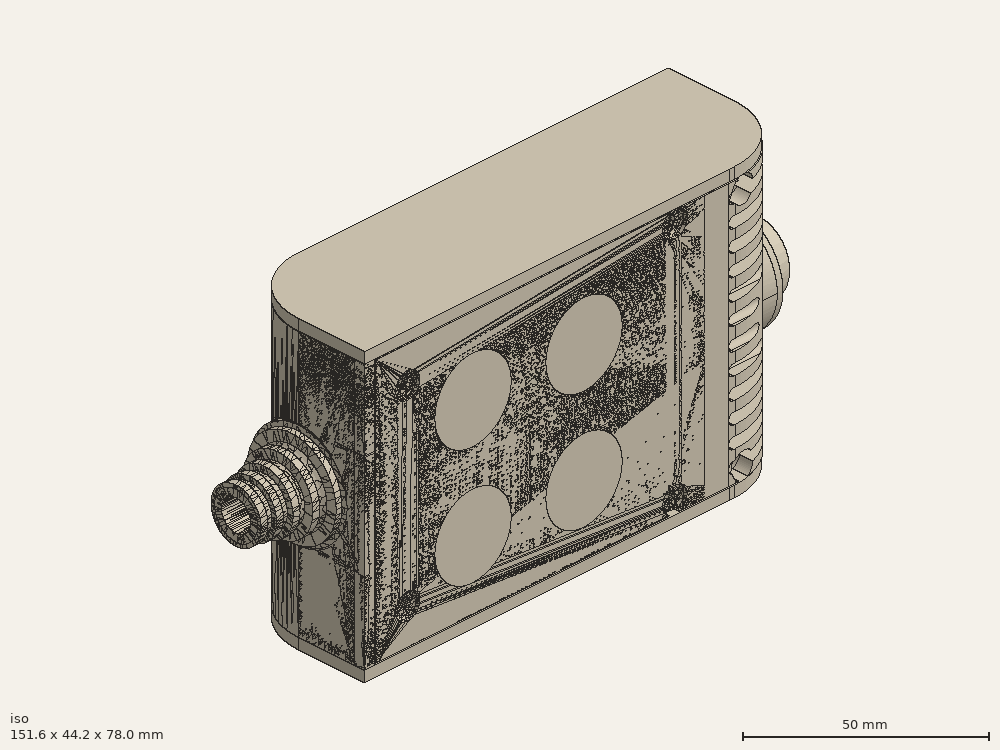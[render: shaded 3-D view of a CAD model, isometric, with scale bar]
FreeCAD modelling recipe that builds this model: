
FCSTD DOCUMENT  (FreeCAD 0.19R0.19.2)
Label: enclosure_188FCStd
License: All rights reserved
LicenseURL: http://en.wikipedia.org/wiki/All_rights_reserved
objects: Part::Revolution×152, Part::MultiFuse×146, Part::Feature×146, Sketcher::SketchObject×84, Part::Cut×70, Part::Cylinder×70, Part::Extrusion×67, Part::Fillet×58, Part::Box×36, App::MeasureDistance×4, PartDesign::Body×2, Image::ImagePlane×1
note: 831 computed .brp shape members not serialized (recipe doc carries the construction recipe); baked Part::Feature solids carry a one-line shape summary decoded from their .brp

FEATURE [Sketcher::SketchObject] Sketch  label="topSketch"
  FullyConstrained = true
  sketch-geometry (20):
    g0: LineSegment StartX=5.21097e-06 StartY=3 StartZ=0 EndX=5.21097e-06 EndY=19 EndZ=0
    g1: ArcOfCircle CenterX=19 CenterY=19 CenterZ=0 NormalX=0 NormalY=0 NormalZ=1 AngleXU=0 Radius=19 StartAngle=1.5708 EndAngle=3.14159
    g2: ArcOfCircle CenterX=19 CenterY=19 CenterZ=0 NormalX=0 NormalY=0 NormalZ=1 AngleXU=0 Radius=16 StartAngle=1.5708 EndAngle=3.14159
    g3: LineSegment StartX=114 StartY=35 StartZ=0 EndX=19 EndY=35 EndZ=0
    g4: LineSegment StartX=5.21097e-06 StartY=3 StartZ=0 EndX=5.21097e-06 EndY=0 EndZ=0
    g5: LineSegment StartX=3 StartY=0 StartZ=0 EndX=5.21097e-06 EndY=0 EndZ=0
    g6: LineSegment StartX=3 StartY=19 StartZ=0 EndX=3 EndY=0 EndZ=0
    g7: LineSegment StartX=19 StartY=38 StartZ=0 EndX=124 EndY=38 EndZ=0
    g8: Circle CenterX=119 CenterY=35 CenterZ=0 NormalX=0 NormalY=0 NormalZ=1 AngleXU=0 Radius=1
    g9: Circle CenterX=121 CenterY=35 CenterZ=0 NormalX=0 NormalY=0 NormalZ=1 AngleXU=0 Radius=1
    g10: Circle CenterX=121 CenterY=33 CenterZ=0 NormalX=0 NormalY=0 NormalZ=1 AngleXU=0 Radius=1
    g11: BSplineCurve PolesCount=3 KnotsCount=2 Degree=2 IsPeriodic=0
    g12: GeomPoint X=119 Y=35 Z=0
    g13: GeomPoint X=121 Y=33 Z=0
    g14: LineSegment StartX=119 StartY=35 StartZ=0 EndX=114 EndY=35 EndZ=0
    g15: ArcOfCircle CenterX=105 CenterY=19 CenterZ=0 NormalX=0 NormalY=0 NormalZ=1 AngleXU=0 Radius=19 StartAngle=5.7297 EndAngle=6.28319
    g16: ArcOfCircle CenterX=105 CenterY=19 CenterZ=0 NormalX=0 NormalY=0 NormalZ=1 AngleXU=0 Radius=16 StartAngle=5.60905 EndAngle=6.28319
    g17: LineSegment StartX=121 StartY=33 StartZ=0 EndX=121 EndY=19 EndZ=0
    g18: LineSegment StartX=124 StartY=38 StartZ=0 EndX=124 EndY=19 EndZ=0
    g19: LineSegment StartX=117.5 StartY=9.01251 StartZ=0 EndX=121.163 EndY=9.0125 EndZ=0
  constraints (46):
    c: Vertical(g0)
    c: Block(g0)
    c: Coincident(g1,g0)
    c: Block(g1)
    c: Coincident(g2,g1)
    c: Block(g2)
    c: Coincident(g3,g2)
    c: Horizontal(g3)
    c: Tangent(g3,g2)
    c: Coincident(g4,g0)
    c: Distance(g4) = 3
    c: Vertical(g4)
    c: Coincident(g5,g4)
    c: Horizontal(g5)
    c: Coincident(g6,g2)
    c: Coincident(g6,g5)
    c: Vertical(g6)
    c: Horizontal(g7)
    c: Distance(g7) = 105
    c: Coincident(g7,g1)
    c: Block(g3)
    c: Weight(g8) = 1
    c: Equal(g8,g9)
    c: Equal(g8,g10)
    c: InternalAlignment(g8,g11)
    c: InternalAlignment(g9,g11)
    c: InternalAlignment(g10,g11)
    c: InternalAlignment(g12,g11)
    c: InternalAlignment(g13,g11)
    c: Block(g11)
    c: Coincident(g14,g11)
    c: Coincident(g14,g3)
    c: Horizontal(g14)
    c: Block(g15)
    c: Coincident(g16,g15)
    c: Block(g16)
    c: Coincident(g17,g11)
    c: Coincident(g17,g16)
    c: Vertical(g17)
    c: Distance(g17) = 14
    c: Coincident(g18,g7)
    c: Coincident(g18,g15)
    c: Vertical(g18)
    c: Distance(g18) = 19
    c: Coincident(g19,g16)
    c: Coincident(g19,g15)
FEATURE [Sketcher::SketchObject] Sketch001  label="bottomSketch"
  FullyConstrained = true
  sketch-geometry (32):
    g0: LineSegment StartX=3.3 StartY=-6.03275e-07 StartZ=0 EndX=98 EndY=-6.03275e-07 EndZ=0
    g1: ArcOfCircle CenterX=98 CenterY=19 CenterZ=0 NormalX=0 NormalY=0 NormalZ=1 AngleXU=0 Radius=19 StartAngle=4.71239 EndAngle=5.71103
    g2: LineSegment StartX=6.3 StartY=8 StartZ=0 EndX=3.3 EndY=8 EndZ=0
    g3: LineSegment StartX=3.3 StartY=8 StartZ=0 EndX=3.3 EndY=-6.03275e-07 EndZ=0
    g4: ArcOfCircle CenterX=8.3 CenterY=5 CenterZ=0 NormalX=0 NormalY=0 NormalZ=1 AngleXU=0 Radius=2 StartAngle=3.14159 EndAngle=4.71239
    g5: LineSegment StartX=6.3 StartY=8 StartZ=0 EndX=6.3 EndY=5 EndZ=0
    g6: ArcOfCircle CenterX=98 CenterY=19 CenterZ=0 NormalX=0 NormalY=0 NormalZ=1 AngleXU=0 Radius=12.7 StartAngle=4.71239 EndAngle=6.28319
    g7: LineSegment StartX=94.7 StartY=3 StartZ=0 EndX=8.3 EndY=3 EndZ=0
    g8-g12: Circle x5 (B-spline internal-alignment scaffolding for g13; pole/knot coordinates omitted)
    g13: BSplineCurve PolesCount=5 KnotsCount=3 Degree=3 IsPeriodic=0
    g14: GeomPoint X=98 Y=6.3 Z=0
    g15: GeomPoint X=96.3938 Y=4.71946 Z=0
    g16: GeomPoint X=94.7 Y=3 Z=0
    g17-g23: Circle x7 (B-spline internal-alignment scaffolding for g24; pole/knot coordinates omitted)
    g24: BSplineCurve PolesCount=7 KnotsCount=5 Degree=3 IsPeriodic=0
    g25-g29: GeomPoint x5 (B-spline internal-alignment scaffolding for g24; pole/knot coordinates omitted)
    g30: ArcOfCircle CenterX=98 CenterY=19 CenterZ=0 NormalX=0 NormalY=0 NormalZ=1 AngleXU=0 Radius=15.7 StartAngle=5.81226 EndAngle=6.28319
    g31: LineSegment StartX=110.7 StartY=19 StartZ=0 EndX=113.7 EndY=19 EndZ=0
  constraints (41):
    c: Horizontal(g0)
    c: Coincident(g1,g0)
    c: Block(g1)
    c: Horizontal(g2)
    c: Distance(g2) = 3
    c: Coincident(g3,g2)
    c: Vertical(g3)
    c: Coincident(g3,g0)
    c: Block(g4)
    c: Block(g2)
    c: Coincident(g5,g2)
    c: Coincident(g5,g4)
    c: Vertical(g5)
    c: Coincident(g6,g1)
    c: Block(g6)
    c: Coincident(g7,g4)
    c: Horizontal(g7)
    c: Block(g0)
    c: Block(g7)
    c: Block(g3)
    c: Coincident(g13,g6)
    c: Weight(g8) = 1
    c: Equal(g8, g9-g12) x4
    c: Coincident(g13,g7)
    c: InternalAlignment(g8-g12 -> g13) x5
    c: InternalAlignment(g14,g13)
    c: InternalAlignment(g15,g13)
    c: InternalAlignment(g16,g13)
    c: Block(g13)
    c: Weight(g17) = 1
    c: Equal(g17, g18-g23) x6
    c: Coincident(g24,g1)
    c: InternalAlignment(g17-g23 -> g24) x7
    c: InternalAlignment(g25-g29 -> g24) x5
    c: Block(g24)
    c: Coincident(g30,g24)
    c: Coincident(g31,g6)
    c: Coincident(g31,g30)
    c: Horizontal(g31)
    c: Block(g31)
    c: Block(g30)
FEATURE [Part::Extrusion] Extrude  label="top"
  Base = -> Sketch
  Dir = (0,0,1)
  DirMode = 2
  FaceMakerClass = Part::FaceMakerBullseye
  LengthFwd = 72
  LengthRev = 0
  Solid = true
  Symmetric = false
FEATURE [Part::Extrusion] Extrude001  label="bottom"
  Base = -> Sketch001
  Dir = (0,0,1)
  DirMode = 2
  FaceMakerClass = Part::FaceMakerBullseye
  LengthFwd = 71.4
  LengthRev = 0
  Placement = pos=(0,0,0.3) rot=(0,0,1;0rad)
  Solid = true
  Symmetric = false
FEATURE [Sketcher::SketchObject] Sketch002  label="topSketch001"
  FullyConstrained = true
  sketch-geometry (8):
    g0: ArcOfCircle CenterX=19 CenterY=19.0975 CenterZ=0 NormalX=0 NormalY=0 NormalZ=1 AngleXU=0 Radius=18.9025 StartAngle=1.5708 EndAngle=3.14674
    g1: LineSegment StartX=0.0977805 StartY=19.0003 StartZ=0 EndX=0.0977805 EndY=0.000251602 EndZ=0
    g2: LineSegment StartX=19 StartY=38 StartZ=0 EndX=124 EndY=38 EndZ=0
    g3: LineSegment StartX=0.0977805 StartY=0.000251602 StartZ=0 EndX=105.098 EndY=0.000251602 EndZ=0
    g4: LineSegment StartX=124 StartY=38 StartZ=0 EndX=125.616 EndY=38 EndZ=0
    g5: LineSegment StartX=105.098 StartY=0.000251602 StartZ=0 EndX=106.713 EndY=0.000251602 EndZ=0
    g6: ArcOfCircle CenterX=106.616 CenterY=19 CenterZ=0 NormalX=0 NormalY=0 NormalZ=1 AngleXU=0 Radius=19 StartAngle=4.71754 EndAngle=6.28319
    g7: LineSegment StartX=125.616 StartY=38 StartZ=0 EndX=125.616 EndY=19 EndZ=0
  constraints (21):
    c: Block(g0)
    c: Coincident(g1,g0)
    c: Vertical(g1)
    c: Horizontal(g2)
    c: Distance(g2) = 105
    c: Coincident(g2,g0)
    c: Distance(g1) = 19
    c: Coincident(g3,g1)
    c: Horizontal(g3)
    c: Distance(g3) = 105
    c: Coincident(g4,g2)
    c: Horizontal(g4)
    c: Distance(g4) = 1.61553
    c: Horizontal(g5)
    c: Equal(g4,g5) = 1.61553
    c: Coincident(g5,g3)
    c: Block(g6)
    c: Coincident(g6,g5)
    c: Coincident(g7,g4)
    c: Coincident(g7,g6)
    c: Vertical(g7)
FEATURE [Part::Extrusion] Extrude002  label="sideA"
  Base = -> Sketch002
  Dir = (0,0,1)
  DirMode = 2
  FaceMakerClass = Part::FaceMakerBullseye
  LengthFwd = 3
  LengthRev = 0
  Placement = pos=(0,0,-3) rot=(0,0,1;0rad)
  Solid = true
  Symmetric = false
FEATURE [Sketcher::SketchObject] Sketch003  label="topSketch002"
  FullyConstrained = true
  sketch-geometry (6):
    g0: LineSegment StartX=19 StartY=38 StartZ=0 EndX=117 EndY=38 EndZ=0
    g1: ArcOfCircle CenterX=19 CenterY=19 CenterZ=0 NormalX=0 NormalY=0 NormalZ=1 AngleXU=0 Radius=19 StartAngle=1.5708 EndAngle=3.14159
    g2: LineSegment StartX=117 StartY=38 StartZ=0 EndX=117 EndY=19 EndZ=0
    g3: LineSegment StartX=98 StartY=1.0161e-12 StartZ=0 EndX=5.22862e-06 EndY=1.0161e-12 EndZ=0
    g4: LineSegment StartX=5.22862e-06 StartY=19 StartZ=0 EndX=5.22862e-06 EndY=1.0161e-12 EndZ=0
    g5: ArcOfCircle CenterX=98 CenterY=19 CenterZ=0 NormalX=0 NormalY=0 NormalZ=1 AngleXU=0 Radius=19 StartAngle=4.71239 EndAngle=6.28319
  constraints (16):
    c: Horizontal(g0)
    c: Distance(g0) = 98
    c: Coincident(g1,g0)
    c: Block(g1)
    c: Coincident(g2,g0)
    c: Vertical(g2)
    c: Distance(g2) = 19
    c: Horizontal(g3)
    c: Coincident(g4,g1)
    c: Vertical(g4)
    c: Coincident(g3,g4)
    c: Block(g3)
    c: Coincident(g5,g2)
    c: Coincident(g5,g3)
    c: Block(g0)
    c: Block(g5)
FEATURE [Sketcher::SketchObject] Sketch004
  FullyConstrained = true
  MapMode = 3
  Placement = pos=(0,0,0) rot=(1,0,0;1.5708rad)
  Support = -> [Extrude]
  sketch-geometry (8):
    g0: Circle CenterX=80.351 CenterY=-67.6202 CenterZ=0 NormalX=0 NormalY=0 NormalZ=1 AngleXU=0 Radius=2
    g1: Circle CenterX=80.351 CenterY=-67.6202 CenterZ=0 NormalX=0 NormalY=0 NormalZ=1 AngleXU=0 Radius=3
    g2: Circle CenterX=80.351 CenterY=-4.92017 CenterZ=0 NormalX=0 NormalY=0 NormalZ=1 AngleXU=0 Radius=2
    g3: Circle CenterX=80.351 CenterY=-4.92017 CenterZ=0 NormalX=0 NormalY=0 NormalZ=1 AngleXU=0 Radius=3
    g4: Circle CenterX=23.851 CenterY=-4.92017 CenterZ=0 NormalX=0 NormalY=0 NormalZ=1 AngleXU=0 Radius=2
    g5: Circle CenterX=23.851 CenterY=-4.92017 CenterZ=0 NormalX=0 NormalY=0 NormalZ=1 AngleXU=0 Radius=3
    g6: Circle CenterX=23.851 CenterY=-67.6202 CenterZ=0 NormalX=0 NormalY=0 NormalZ=1 AngleXU=0 Radius=2
    g7: Circle CenterX=23.851 CenterY=-67.6202 CenterZ=0 NormalX=0 NormalY=0 NormalZ=1 AngleXU=0 Radius=3
  constraints (8):
    c: Block(g3)
    c: Block(g2)
    c: Block(g1)
    c: Block(g0)
    c: Block(g6)
    c: Block(g7)
    c: Block(g4)
    c: Block(g5)
FEATURE [Part::Extrusion] Extrude004
  Base = -> Sketch004
  Dir = (0,-1,2e-16)
  DirMode = 2
  FaceMakerClass = Part::FaceMakerBullseye
  LengthFwd = 6
  LengthRev = 0
  Placement = pos=(0,9,0) rot=(0,0,1;0rad)
  Solid = true
  Symmetric = false
FEATURE [Sketcher::SketchObject] Sketch005
  FullyConstrained = true
  MapMode = 3
  Placement = pos=(0,0,0) rot=(1,0,0;1.5708rad)
  Support = -> [Extrude]
  sketch-geometry (8):
    g0: Circle CenterX=80.351 CenterY=-67.6202 CenterZ=0 NormalX=0 NormalY=0 NormalZ=1 AngleXU=0 Radius=3
    g1: Circle CenterX=80.351 CenterY=-4.92017 CenterZ=0 NormalX=0 NormalY=0 NormalZ=1 AngleXU=0 Radius=3
    g2: Circle CenterX=23.851 CenterY=-4.92017 CenterZ=0 NormalX=0 NormalY=0 NormalZ=1 AngleXU=0 Radius=3
    g3: Circle CenterX=23.851 CenterY=-67.6202 CenterZ=0 NormalX=0 NormalY=0 NormalZ=1 AngleXU=0 Radius=3
    g4: Circle CenterX=23.851 CenterY=-67.6202 CenterZ=0 NormalX=0 NormalY=0 NormalZ=1 AngleXU=0 Radius=5
    g5: Circle CenterX=80.351 CenterY=-67.6202 CenterZ=0 NormalX=0 NormalY=0 NormalZ=1 AngleXU=0 Radius=5
    g6: Circle CenterX=23.851 CenterY=-4.92017 CenterZ=0 NormalX=0 NormalY=0 NormalZ=1 AngleXU=0 Radius=5
    g7: Circle CenterX=80.351 CenterY=-4.92017 CenterZ=0 NormalX=0 NormalY=0 NormalZ=1 AngleXU=0 Radius=5
  constraints (8):
    c: Block(g1)
    c: Block(g0)
    c: Block(g3)
    c: Block(g2)
    c: Block(g5)
    c: Block(g4)
    c: Block(g6)
    c: Block(g7)
FEATURE [Part::Extrusion] Extrude005
  Base = -> Sketch005
  Dir = (0,-1,2e-16)
  DirMode = 2
  FaceMakerClass = Part::FaceMakerBullseye
  LengthFwd = 2
  LengthRev = 0
  Solid = true
  Symmetric = false
FEATURE [Sketcher::SketchObject] Sketch006
  FullyConstrained = true
  MapMode = 3
  Placement = pos=(0,0,0) rot=(1,0,0;1.5708rad)
  sketch-geometry (8):
    g0: Circle CenterX=80.351 CenterY=-67.6202 CenterZ=0 NormalX=0 NormalY=0 NormalZ=1 AngleXU=0 Radius=3
    g1: Circle CenterX=80.351 CenterY=-4.92017 CenterZ=0 NormalX=0 NormalY=0 NormalZ=1 AngleXU=0 Radius=3
    g2: Circle CenterX=23.851 CenterY=-4.92017 CenterZ=0 NormalX=0 NormalY=0 NormalZ=1 AngleXU=0 Radius=3
    g3: Circle CenterX=23.851 CenterY=-67.6202 CenterZ=0 NormalX=0 NormalY=0 NormalZ=1 AngleXU=0 Radius=3
    g4: Circle CenterX=23.851 CenterY=-67.6202 CenterZ=0 NormalX=0 NormalY=0 NormalZ=1 AngleXU=0 Radius=5
    g5: Circle CenterX=80.351 CenterY=-67.6202 CenterZ=0 NormalX=0 NormalY=0 NormalZ=1 AngleXU=0 Radius=5
    g6: Circle CenterX=23.851 CenterY=-4.92017 CenterZ=0 NormalX=0 NormalY=0 NormalZ=1 AngleXU=0 Radius=5
    g7: Circle CenterX=80.351 CenterY=-4.92017 CenterZ=0 NormalX=0 NormalY=0 NormalZ=1 AngleXU=0 Radius=5
  constraints (8):
    c: Block(g1)
    c: Block(g0)
    c: Block(g3)
    c: Block(g2)
    c: Block(g5)
    c: Block(g4)
    c: Block(g6)
    c: Block(g7)
FEATURE [Part::Extrusion] Extrude007
  Base = -> Sketch006
  Dir = (0,-1,2e-16)
  DirMode = 2
  FaceMakerClass = Part::FaceMakerBullseye
  LengthFwd = 2
  LengthRev = 0
  Solid = true
  Symmetric = false
FEATURE [Part::Fillet] Fillet
  Base = -> Extrude007
  Edges = 4 edges r=1.99: [Edge6,Edge12,Edge18,Edge24]
FEATURE [Part::Cut] Cut
  Base = -> Extrude005
  Placement = pos=(0,5,0) rot=(0,0,1;0rad)
  Tool = -> Fillet
FEATURE [Part::MultiFuse] Fusion  label="pCBScrews"
  Placement = pos=(-2.5,0,72.3) rot=(0,0,1;0rad)
  Shapes = -> [Extrude004,Cut]
FEATURE [App::MeasureDistance] Distance  label="Distance: 0.69 mm"
  Distance = 0.685967
  P1 = (24.0138,2.9647,0.3)
  P2 = (23.8901,3,-0.373787)
FEATURE [App::MeasureDistance] Distance001  label="Distance: 0.53 mm"
  Distance = 0.533607
  P1 = (80.2939,3,72.2334)
  P2 = (80.281,2.99661,71.7)
FEATURE [Part::Fillet] Fillet001
  Base = -> Extrude001
  Edges = 1 edges r=2.4: [Edge17]
FEATURE [Part::Fillet] Fillet002  label="bottom001"
  Base = -> Fillet001
  Edges = 1 edges r=2.4: [Edge36]
FEATURE [Part::Fillet] Fillet003  label="top001"
  Base = -> Extrude
  Edges = 1 edges r=2: [Edge1]
FEATURE [Sketcher::SketchObject] Sketch007
  FullyConstrained = true
  sketch-geometry (16):
    g0: LineSegment StartX=4 StartY=0 StartZ=0 EndX=4 EndY=2.4 EndZ=0
    g1: LineSegment StartX=4 StartY=2.4 StartZ=0 EndX=7 EndY=2.4 EndZ=0
    g2: LineSegment StartX=4 StartY=0 StartZ=0 EndX=5.7 EndY=0 EndZ=0
    g3: LineSegment StartX=5.7 StartY=0 StartZ=0 EndX=5.7 EndY=-5.6 EndZ=0
    g4-g8: Circle x5 (B-spline internal-alignment scaffolding for g9; pole/knot coordinates omitted)
    g9: BSplineCurve PolesCount=5 KnotsCount=3 Degree=3 IsPeriodic=0
    g10: GeomPoint X=7 Y=2.4 Z=0
    g11: GeomPoint X=10.4582 Y=-1.55472 Z=0
    g12: GeomPoint X=14 Y=-5.6 Z=0
    g13: LineSegment StartX=14 StartY=-5.6 StartZ=0 EndX=14 EndY=-14.1 EndZ=0
    g14: LineSegment StartX=14 StartY=-14.1 StartZ=0 EndX=6.5 EndY=-14.1 EndZ=0
    g15: LineSegment StartX=5.7 StartY=-5.6 StartZ=0 EndX=6.5 EndY=-14.1 EndZ=0
  constraints (28):
    c: Distance(g0) = 2.4
    c: Vertical(g0)
    c: Block(g0)
    c: Coincident(g1,g0)
    c: Horizontal(g1)
    c: Distance(g1) = 3
    c: Coincident(g2,g0)
    c: Horizontal(g2)
    c: Distance(g2) = 1.7
    c: Coincident(g3,g2)
    c: Vertical(g3)
    c: Distance(g3) = 5.6
    c: Coincident(g9,g1)
    c: Weight(g4) = 1
    c: Equal(g4, g5-g8) x4
    c: InternalAlignment(g4-g8 -> g9) x5
    c: InternalAlignment(g10,g9)
    c: InternalAlignment(g11,g9)
    c: InternalAlignment(g12,g9)
    c: Block(g9)
    c: Coincident(g13,g9)
    c: Vertical(g13)
    c: Distance(g13) = 8.5
    c: Coincident(g14,g13)
    c: Horizontal(g14)
    c: Distance(g14) = 7.5
    c: Coincident(g15,g3)
    c: Coincident(g15,g14)
FEATURE [Part::Feature] Face
  shape: bbox 10 x 16.5 x 2e-07 mm, 1 faces, 0 solids (baked)
FEATURE [Part::Revolution] Revolve  label="plugHousing"
  Angle = 360
  Axis = (0,1,0)
  Base = (0,0,0)
  FaceMakerClass = Part::FaceMakerBullseye
  Placement = pos=(0,0,36.15) rot=(0,0,1;0rad)
  Solid = false
  Source = -> Face
  Symmetric = false
FEATURE [Part::Feature] Face001
  shape: bbox 10 x 16.5 x 2e-07 mm, 1 faces, 0 solids (baked)
FEATURE [Part::Revolution] Revolve001  label="plugHousing001"
  Angle = 360
  Axis = (0,1,0)
  Base = (0,0,0)
  FaceMakerClass = Part::FaceMakerBullseye
  Placement = pos=(0,0,36.15) rot=(0,0,1;0rad)
  Solid = false
  Source = -> Face001
  Symmetric = false
FEATURE [Part::MultiFuse] Fusion001  label="plugHousing002"
  Placement = pos=(0,0,0) rot=(0,0,1;1.5708rad)
  Shapes = -> [Revolve001,Revolve]
FEATURE [Part::Feature] Face002
  shape: bbox 10 x 16.5 x 2e-07 mm, 1 faces, 0 solids (baked)
FEATURE [Part::Revolution] Revolve003  label="plugHousing005"
  Angle = 360
  Axis = (0,1,0)
  Base = (0,0,0)
  FaceMakerClass = Part::FaceMakerBullseye
  Placement = pos=(0,0,36.15) rot=(0,0,1;0rad)
  Solid = false
  Source = -> Face002
  Symmetric = false
FEATURE [Part::Feature] Face003
  shape: bbox 10 x 16.5 x 2e-07 mm, 1 faces, 0 solids (baked)
FEATURE [Part::Revolution] Revolve002  label="plugHousing003"
  Angle = 360
  Axis = (0,1,0)
  Base = (0,0,0)
  FaceMakerClass = Part::FaceMakerBullseye
  Placement = pos=(0,0,36.15) rot=(0,0,1;0rad)
  Solid = false
  Source = -> Face003
  Symmetric = false
FEATURE [Part::MultiFuse] Fusion002  label="plugHousing004"
  Placement = pos=(0,0,0) rot=(0,0,1;1.5708rad)
  Shapes = -> [Revolve002,Revolve003]
FEATURE [Part::MultiFuse] Fusion003  label="plugHousing006"
  Placement = pos=(0,19,0) rot=(0,0,1;3.14159rad)
  Shapes = -> [Fusion002,Fusion001]
FEATURE [Part::Feature] Face004
  shape: bbox 10 x 16.5 x 2e-07 mm, 1 faces, 0 solids (baked)
FEATURE [Part::Revolution] Revolve006  label="plugHousing010"
  Angle = 360
  Axis = (0,1,0)
  Base = (0,0,0)
  FaceMakerClass = Part::FaceMakerBullseye
  Placement = pos=(0,0,36.15) rot=(0,0,1;0rad)
  Solid = false
  Source = -> Face004
  Symmetric = false
FEATURE [Part::Feature] Face005
  shape: bbox 10 x 16.5 x 2e-07 mm, 1 faces, 0 solids (baked)
FEATURE [Part::Revolution] Revolve007  label="plugHousing011"
  Angle = 360
  Axis = (0,1,0)
  Base = (0,0,0)
  FaceMakerClass = Part::FaceMakerBullseye
  Placement = pos=(0,0,36.15) rot=(0,0,1;0rad)
  Solid = false
  Source = -> Face005
  Symmetric = false
FEATURE [Part::Feature] Face006
  shape: bbox 10 x 16.5 x 2e-07 mm, 1 faces, 0 solids (baked)
FEATURE [Part::Revolution] Revolve004  label="plugHousing007"
  Angle = 360
  Axis = (0,1,0)
  Base = (0,0,0)
  FaceMakerClass = Part::FaceMakerBullseye
  Placement = pos=(0,0,36.15) rot=(0,0,1;0rad)
  Solid = false
  Source = -> Face006
  Symmetric = false
FEATURE [Part::MultiFuse] Fusion004  label="plugHousing009"
  Placement = pos=(0,0,0) rot=(0,0,1;1.5708rad)
  Shapes = -> [Revolve004,Revolve007]
FEATURE [Part::Feature] Face007
  shape: bbox 10 x 16.5 x 2e-07 mm, 1 faces, 0 solids (baked)
FEATURE [Part::Revolution] Revolve005  label="plugHousing008"
  Angle = 360
  Axis = (0,1,0)
  Base = (0,0,0)
  FaceMakerClass = Part::FaceMakerBullseye
  Placement = pos=(0,0,36.15) rot=(0,0,1;0rad)
  Solid = false
  Source = -> Face007
  Symmetric = false
FEATURE [Part::MultiFuse] Fusion005  label="plugHousing012"
  Placement = pos=(0,0,0) rot=(0,0,1;1.5708rad)
  Shapes = -> [Revolve006,Revolve005]
FEATURE [Part::MultiFuse] Fusion006  label="plugHousing013"
  Placement = pos=(0,19,0) rot=(0,0,1;3.14159rad)
  Shapes = -> [Fusion005,Fusion004]
FEATURE [Part::MultiFuse] Fusion007  label="plugHousing014"
  Placement = pos=(122.621,0,-0.15) rot=(0,0,1;0rad)
  Shapes = -> [Fusion003,Fusion006]
FEATURE [Part::Cylinder] Cylinder002
  Angle = 360
  AttacherType = Attacher::AttachEngine3D
  Height = 20
  Placement = pos=(0,0,36.15) rot=(0,0,1;0rad)
  Radius = 4
FEATURE [Part::Cylinder] Cylinder003
  Angle = 360
  AttacherType = Attacher::AttachEngine3D
  Height = 10
  Placement = pos=(0,0,36.15) rot=(0,0,1;0rad)
  Radius = 4
FEATURE [Part::MultiFuse] Fusion009  label="removeToCreateHoleForPlugHousing"
  Placement = pos=(70,19,36.15) rot=(0,1,0;1.5708rad)
  Shapes = -> [Cylinder002,Cylinder003]
FEATURE [Part::Cylinder] Cylinder004
  Angle = 360
  AttacherType = Attacher::AttachEngine3D
  Height = 20
  Placement = pos=(0,0,36.15) rot=(0,0,1;0rad)
  Radius = 4
FEATURE [Part::Cylinder] Cylinder005
  Angle = 360
  AttacherType = Attacher::AttachEngine3D
  Height = 10
  Placement = pos=(0,0,36.15) rot=(0,0,1;0rad)
  Radius = 4
FEATURE [Part::MultiFuse] Fusion010  label="removeToCreateHoleForPlugHousing001"
  Placement = pos=(70,19,36.15) rot=(0,1,0;1.5708rad)
  Shapes = -> [Cylinder004,Cylinder005]
FEATURE [Part::Cut] Cut001
  Base = -> Fillet003
  Tool = -> Fusion010
FEATURE [Part::Cut] Cut002  label="Bottom"
  Base = -> Fillet002
  Tool = -> Fusion009
FEATURE [Part::Feature] Face008
  shape: bbox 10 x 16.5 x 2e-07 mm, 1 faces, 0 solids (baked)
FEATURE [Part::Revolution] Revolve011  label="plugHousing021"
  Angle = 360
  Axis = (0,1,0)
  Base = (0,0,0)
  FaceMakerClass = Part::FaceMakerBullseye
  Placement = pos=(0,0,36.15) rot=(0,0,1;0rad)
  Solid = false
  Source = -> Face008
  Symmetric = false
FEATURE [Part::Feature] Face009
  shape: bbox 10 x 16.5 x 2e-07 mm, 1 faces, 0 solids (baked)
FEATURE [Part::Revolution] Revolve012  label="plugHousing022"
  Angle = 360
  Axis = (0,1,0)
  Base = (0,0,0)
  FaceMakerClass = Part::FaceMakerBullseye
  Placement = pos=(0,0,36.15) rot=(0,0,1;0rad)
  Solid = false
  Source = -> Face009
  Symmetric = false
FEATURE [Part::Feature] Face010 .. Face013  x4 (patterned run collapsed; names and placements below)
  shape: bbox 10 x 16.5 x 2e-07 mm, 1 faces, 0 solids (baked)
FEATURE [Part::Revolution] Revolve015  label="plugHousing027"
  Angle = 360
  Axis = (0,1,0)
  Base = (0,0,0)
  FaceMakerClass = Part::FaceMakerBullseye
  Placement = pos=(0,0,36.15) rot=(0,0,1;0rad)
  Solid = false
  Source = -> Face013
  Symmetric = false
FEATURE [Part::Feature] Face014
  shape: bbox 10 x 16.5 x 2e-07 mm, 1 faces, 0 solids (baked)
FEATURE [Part::Feature] Face015
  shape: bbox 10 x 16.5 x 2e-07 mm, 1 faces, 0 solids (baked)
FEATURE [Part::Feature] Face016
  shape: bbox 10 x 16.5 x 2e-07 mm, 1 faces, 0 solids (baked)
FEATURE [Part::Revolution] Revolve019  label="plugHousing033"
  Angle = 360
  Axis = (0,1,0)
  Base = (0,0,0)
  FaceMakerClass = Part::FaceMakerBullseye
  Placement = pos=(0,0,36.15) rot=(0,0,1;0rad)
  Solid = false
  Source = -> Face016
  Symmetric = false
FEATURE [Part::Feature] Face017
  shape: bbox 10 x 16.5 x 2e-07 mm, 1 faces, 0 solids (baked)
FEATURE [Part::Revolution] Revolve020  label="plugHousing034"
  Angle = 360
  Axis = (0,1,0)
  Base = (0,0,0)
  FaceMakerClass = Part::FaceMakerBullseye
  Placement = pos=(0,0,36.15) rot=(0,0,1;0rad)
  Solid = false
  Source = -> Face017
  Symmetric = false
FEATURE [Part::Feature] Face018
  shape: bbox 10 x 16.5 x 2e-07 mm, 1 faces, 0 solids (baked)
FEATURE [Part::Revolution] Revolve016  label="plugHousing030"
  Angle = 360
  Axis = (0,1,0)
  Base = (0,0,0)
  FaceMakerClass = Part::FaceMakerBullseye
  Placement = pos=(0,0,36.15) rot=(0,0,1;0rad)
  Solid = false
  Source = -> Face018
  Symmetric = false
FEATURE [Part::MultiFuse] Fusion020  label="plugHousing038"
  Placement = pos=(0,0,0) rot=(0,0,1;1.5708rad)
  Shapes = -> [Revolve016,Revolve020]
FEATURE [Part::Feature] Face019
  shape: bbox 10 x 16.5 x 2e-07 mm, 1 faces, 0 solids (baked)
FEATURE [Part::Feature] Face020
  shape: bbox 10 x 16.5 x 2e-07 mm, 1 faces, 0 solids (baked)
FEATURE [Part::Revolution] Revolve017  label="plugHousing031"
  Angle = 360
  Axis = (0,1,0)
  Base = (0,0,0)
  FaceMakerClass = Part::FaceMakerBullseye
  Placement = pos=(0,0,36.15) rot=(0,0,1;0rad)
  Solid = false
  Source = -> Face020
  Symmetric = false
FEATURE [Part::MultiFuse] Fusion021  label="plugHousing039"
  Placement = pos=(0,0,0) rot=(0,0,1;1.5708rad)
  Shapes = -> [Revolve019,Revolve017]
FEATURE [Part::MultiFuse] Fusion023  label="plugHousing041"
  Placement = pos=(0,19,0) rot=(0,0,1;3.14159rad)
  Shapes = -> [Fusion021,Fusion020]
FEATURE [Part::Revolution] Revolve022  label="plugHousing043"
  Angle = 360
  Axis = (0,1,0)
  Base = (0,0,0)
  FaceMakerClass = Part::FaceMakerBullseye
  Placement = pos=(0,0,36.15) rot=(0,0,1;0rad)
  Solid = false
  Source = -> Face019
  Symmetric = false
FEATURE [Part::Feature] Face021
  shape: bbox 10 x 16.5 x 2e-07 mm, 1 faces, 0 solids (baked)
FEATURE [Part::Revolution] Revolve023  label="plugHousing044"
  Angle = 360
  Axis = (0,1,0)
  Base = (0,0,0)
  FaceMakerClass = Part::FaceMakerBullseye
  Placement = pos=(0,0,36.15) rot=(0,0,1;0rad)
  Solid = false
  Source = -> Face021
  Symmetric = false
FEATURE [Part::Feature] Face022
  shape: bbox 10 x 16.5 x 2e-07 mm, 1 faces, 0 solids (baked)
FEATURE [Part::Revolution] Revolve018  label="plugHousing032"
  Angle = 360
  Axis = (0,1,0)
  Base = (0,0,0)
  FaceMakerClass = Part::FaceMakerBullseye
  Placement = pos=(0,0,36.15) rot=(0,0,1;0rad)
  Solid = false
  Source = -> Face022
  Symmetric = false
FEATURE [Part::MultiFuse] Fusion022  label="plugHousing040"
  Placement = pos=(0,0,0) rot=(0,0,1;1.5708rad)
  Shapes = -> [Revolve018,Revolve023]
FEATURE [Part::Feature] Face023
  shape: bbox 10 x 16.5 x 2e-07 mm, 1 faces, 0 solids (baked)
FEATURE [Part::Revolution] Revolve021  label="plugHousing035"
  Angle = 360
  Axis = (0,1,0)
  Base = (0,0,0)
  FaceMakerClass = Part::FaceMakerBullseye
  Placement = pos=(0,0,36.15) rot=(0,0,1;0rad)
  Solid = false
  Source = -> Face023
  Symmetric = false
FEATURE [Part::MultiFuse] Fusion018  label="plugHousing036"
  Placement = pos=(0,0,0) rot=(0,0,1;1.5708rad)
  Shapes = -> [Revolve022,Revolve021]
FEATURE [Part::MultiFuse] Fusion019  label="plugHousing037"
  Placement = pos=(0,19,0) rot=(0,0,1;3.14159rad)
  Shapes = -> [Fusion018,Fusion022]
FEATURE [Part::MultiFuse] Fusion024  label="plugHousing042"
  Placement = pos=(122.621,0,-0.15) rot=(0,0,1;0rad)
  Shapes = -> [Fusion023,Fusion019]
FEATURE [Part::Cylinder] Cylinder006
  Angle = 360
  AttacherType = Attacher::AttachEngine3D
  Height = 20
  Placement = pos=(0,0,36.15) rot=(0,0,1;0rad)
  Radius = 14.3
FEATURE [Part::Cylinder] Cylinder007
  Angle = 360
  AttacherType = Attacher::AttachEngine3D
  Height = 10
  Placement = pos=(0,0,36.15) rot=(0,0,1;0rad)
  Radius = 4
FEATURE [Part::MultiFuse] Fusion026  label="removeToCreteHoleForPlugHousing"
  Placement = pos=(70,19,36) rot=(0,1,0;1.5708rad)
  Shapes = -> [Cylinder006,Cylinder007]
FEATURE [Part::Box] Box001  label="Cube001"
  AttacherType = Attacher::AttachEngine3D
  Height = 28
  Length = 3
  Placement = pos=(110.7,19,22) rot=(0,0,1;0rad)
  Width = 15.7
FEATURE [Part::Cut] Cut003  label="top002"
  Base = -> Cut001
  Tool = -> Fusion007
FEATURE [Part::Revolution] Revolve008  label="plugHousing015"
  Angle = 360
  Axis = (0,1,0)
  Base = (0,0,0)
  FaceMakerClass = Part::FaceMakerBullseye
  Placement = pos=(0,0,36.15) rot=(0,0,1;0rad)
  Solid = false
  Source = -> Face010
  Symmetric = false
FEATURE [Part::MultiFuse] Fusion013  label="plugHousing020"
  Placement = pos=(0,0,0) rot=(0,0,1;1.5708rad)
  Shapes = -> [Revolve008,Revolve012]
FEATURE [Part::Cut] Cut004  label="top003"
  Base = -> Cut003
  Placement = pos=(1,0,0) rot=(0,0,1;0rad)
  Tool = -> Fusion026
FEATURE [Part::Cylinder] Cylinder008
  Angle = 360
  AttacherType = Attacher::AttachEngine3D
  Height = 20
  Placement = pos=(0,0,36.15) rot=(0,0,1;0rad)
  Radius = 10.3
FEATURE [Part::Cylinder] Cylinder009
  Angle = 360
  AttacherType = Attacher::AttachEngine3D
  Height = 10
  Placement = pos=(0,0,36.15) rot=(0,0,1;0rad)
  Radius = 4
FEATURE [Part::MultiFuse] Fusion027  label="removeToCreteHoleForPlugHousing001"
  Placement = pos=(70,19,36) rot=(0,1,0;1.5708rad)
  Shapes = -> [Cylinder008,Cylinder009]
FEATURE [Part::Cut] Cut005  label="plugHousingTab"
  Base = -> Box001
  Tool = -> Fusion027
FEATURE [Part::MultiFuse] Fusion028  label="plugHousing045"
  Shapes = -> [Fusion024,Cut005]
FEATURE [Part::Box] Box002  label="Cube002"
  AttacherType = Attacher::AttachEngine3D
  Height = 28.8
  Length = 3
  Placement = pos=(107.3,28,21.6) rot=(0,0,1;0rad)
  Width = 7
FEATURE [Part::Box] Box003  label="Cube003"
  AttacherType = Attacher::AttachEngine3D
  Height = 3
  Length = 6.4
  Placement = pos=(107.3,28,18.6) rot=(0,0,1;0rad)
  Width = 7
FEATURE [Part::Box] Box004  label="Cube004"
  AttacherType = Attacher::AttachEngine3D
  Height = 3
  Length = 6.4
  Placement = pos=(107.3,28,50.4) rot=(0,0,1;0rad)
  Width = 7
FEATURE [Part::MultiFuse] Fusion029  label="plugHousingBracketHolder"
  Shapes = -> [Box004,Box002,Box003]
FEATURE [Part::Cylinder] Cylinder010
  Angle = 360
  AttacherType = Attacher::AttachEngine3D
  Height = 20
  Placement = pos=(0,0,36.15) rot=(0,0,1;0rad)
  Radius = 14.3
FEATURE [Part::Cylinder] Cylinder011
  Angle = 360
  AttacherType = Attacher::AttachEngine3D
  Height = 10
  Placement = pos=(0,0,36.15) rot=(0,0,1;0rad)
  Radius = 4
FEATURE [Part::MultiFuse] Fusion030  label="removeToCreteHoleForPlugHousing002"
  Placement = pos=(70,19,36) rot=(0,1,0;1.5708rad)
  Shapes = -> [Cylinder010,Cylinder011]
FEATURE [Part::Cut] Cut006  label="plugHousingBracketHolder001"
  Base = -> Fusion029
  Tool = -> Fusion030
FEATURE [Part::Cylinder] Cylinder012
  Angle = 360
  AttacherType = Attacher::AttachEngine3D
  Height = 20
  Placement = pos=(0,0,36.15) rot=(0,0,1;0rad)
  Radius = 7
FEATURE [Part::Cylinder] Cylinder013
  Angle = 360
  AttacherType = Attacher::AttachEngine3D
  Height = 10
  Placement = pos=(0,0,36.15) rot=(0,0,1;0rad)
  Radius = 4
FEATURE [Part::MultiFuse] Fusion032  label="removeToCreteHoleForPlugHousing003"
  Placement = pos=(70,19,36) rot=(0,1,0;1.5708rad)
  Shapes = -> [Cylinder012,Cylinder013]
FEATURE [Part::Cut] Cut007  label="bottom002"
  Base = -> Cut002
  Tool = -> Fusion032
FEATURE [Sketcher::SketchObject] Sketch008
  FullyConstrained = true
  sketch-geometry (54):
    g0: LineSegment StartX=-4.2 StartY=0 StartZ=0 EndX=-6.2 EndY=0 EndZ=0
    g1: LineSegment StartX=-14 StartY=-18 StartZ=0 EndX=-14 EndY=-26.5 EndZ=0
    g2: LineSegment StartX=-4.2 StartY=0 StartZ=0 EndX=-4.2 EndY=-13.4877 EndZ=0
    g3: Circle CenterX=-4.2 CenterY=-13.4877 CenterZ=0 NormalX=0 NormalY=0 NormalZ=1 AngleXU=0 Radius=1
    g4: Circle CenterX=-4.2 CenterY=-26.5 CenterZ=0 NormalX=0 NormalY=0 NormalZ=1 AngleXU=0 Radius=1
    g5: Circle CenterX=-8.2 CenterY=-26.5 CenterZ=0 NormalX=0 NormalY=0 NormalZ=1 AngleXU=0 Radius=1
    g6: BSplineCurve PolesCount=3 KnotsCount=2 Degree=2 IsPeriodic=0
    g7: GeomPoint X=-4.2 Y=-13.4877 Z=0
    g8: GeomPoint X=-8.2 Y=-26.5 Z=0
    g9: LineSegment StartX=-14 StartY=-26.5 StartZ=0 EndX=-8.2 EndY=-26.5 EndZ=0
    g10: LineSegment StartX=-10.15 StartY=-12 StartZ=0 EndX=-10.15 EndY=-14 EndZ=0
    g11: LineSegment StartX=-12.8401 StartY=-16 StartZ=0 EndX=-10.1571 EndY=-16 EndZ=0
    g12: LineSegment StartX=-10.15 StartY=-14 StartZ=0 EndX=-8.70761 EndY=-14 EndZ=0
    g13: LineSegment StartX=-12.8401 StartY=-16 StartZ=0 EndX=-12.8401 EndY=-17.6958 EndZ=0
    g14: LineSegment StartX=-10.15 StartY=-12 StartZ=0 EndX=-7.79258 EndY=-12 EndZ=0
    g15: Circle CenterX=-6.2215 CenterY=-2 CenterZ=0 NormalX=0 NormalY=0 NormalZ=1 AngleXU=0 Radius=1
    g16: Circle CenterX=-6.22762 CenterY=-2.58724 CenterZ=0 NormalX=0 NormalY=0 NormalZ=1 AngleXU=0 Radius=1
    g17: Circle CenterX=-6.32538 CenterY=-4 CenterZ=0 NormalX=0 NormalY=0 NormalZ=1 AngleXU=0 Radius=1
    g18: BSplineCurve PolesCount=3 KnotsCount=2 Degree=2 IsPeriodic=0
    g19: GeomPoint X=-6.2215 Y=-2 Z=0
    g20: GeomPoint X=-6.32538 Y=-4 Z=0
    g21: Circle CenterX=-6.48644 CenterY=-5.99526 CenterZ=0 NormalX=0 NormalY=0 NormalZ=1 AngleXU=0 Radius=1
    g22: Circle CenterX=-6.58486 CenterY=-6.99526 CenterZ=0 NormalX=0 NormalY=0 NormalZ=1 AngleXU=0 Radius=1
    g23: Circle CenterX=-6.77343 CenterY=-8 CenterZ=0 NormalX=0 NormalY=0 NormalZ=1 AngleXU=0 Radius=1
    g24: BSplineCurve PolesCount=3 KnotsCount=2 Degree=2 IsPeriodic=0
    g25: GeomPoint X=-6.48644 Y=-5.99526 Z=0
    g26: GeomPoint X=-6.77343 Y=-8 Z=0
    g27: Circle CenterX=-7.19003 CenterY=-10 CenterZ=0 NormalX=0 NormalY=0 NormalZ=1 AngleXU=0 Radius=1
    g28: Circle CenterX=-7.44407 CenterY=-11.0915 CenterZ=0 NormalX=0 NormalY=0 NormalZ=1 AngleXU=0 Radius=1
    g29: Circle CenterX=-7.79258 CenterY=-12 CenterZ=0 NormalX=0 NormalY=0 NormalZ=1 AngleXU=0 Radius=1
    g30: BSplineCurve PolesCount=3 KnotsCount=2 Degree=2 IsPeriodic=0
    g31: GeomPoint X=-7.19003 Y=-10 Z=0
    g32: GeomPoint X=-7.79258 Y=-12 Z=0
    g33: Circle CenterX=-8.70761 CenterY=-14 CenterZ=0 NormalX=0 NormalY=0 NormalZ=1 AngleXU=0 Radius=1
    g34: Circle CenterX=-9.33087 CenterY=-15.1837 CenterZ=0 NormalX=0 NormalY=0 NormalZ=1 AngleXU=0 Radius=1
    g35: Circle CenterX=-10.1571 CenterY=-16 CenterZ=0 NormalX=0 NormalY=0 NormalZ=1 AngleXU=0 Radius=1
    g36: BSplineCurve PolesCount=3 KnotsCount=2 Degree=2 IsPeriodic=0
    g37: GeomPoint X=-8.70761 Y=-14 Z=0
    g38: GeomPoint X=-10.1571 Y=-16 Z=0
    g39: Circle CenterX=-12.8401 CenterY=-17.6958 CenterZ=0 NormalX=0 NormalY=0 NormalZ=1 AngleXU=0 Radius=1
    g40: Circle CenterX=-13.3521 CenterY=-17.9027 CenterZ=0 NormalX=0 NormalY=0 NormalZ=1 AngleXU=0 Radius=1
    g41: Circle CenterX=-14 CenterY=-18 CenterZ=0 NormalX=0 NormalY=0 NormalZ=1 AngleXU=0 Radius=1
    g42: BSplineCurve PolesCount=3 KnotsCount=2 Degree=2 IsPeriodic=0
    g43: GeomPoint X=-12.8401 Y=-17.6958 Z=0
    g44: GeomPoint X=-14 Y=-18 Z=0
    g45: LineSegment StartX=-6.2 StartY=0 StartZ=0 EndX=-7.2 EndY=0 EndZ=0
    g46: LineSegment StartX=-7.2 StartY=0 StartZ=0 EndX=-7.2 EndY=-2 EndZ=0
    g47: LineSegment StartX=-7.2 StartY=-2 StartZ=0 EndX=-6.2215 EndY=-2 EndZ=0
    g48: LineSegment StartX=-6.32538 StartY=-4 StartZ=0 EndX=-7.65538 EndY=-4 EndZ=0
    g49: LineSegment StartX=-7.65538 StartY=-4 StartZ=0 EndX=-7.65538 EndY=-5.99526 EndZ=0
    g50: LineSegment StartX=-7.65538 StartY=-5.99526 StartZ=0 EndX=-6.48644 EndY=-5.99526 EndZ=0
    g51: LineSegment StartX=-6.77343 StartY=-8 StartZ=0 EndX=-8.43343 EndY=-8 EndZ=0
    g52: LineSegment StartX=-8.43343 StartY=-8 StartZ=0 EndX=-8.43343 EndY=-10 EndZ=0
    g53: LineSegment StartX=-8.43343 StartY=-10 StartZ=0 EndX=-7.19003 EndY=-10 EndZ=0
  constraints (112):
    c: Horizontal(g0)
    c: Distance(g0) = 2
    c: Block(g0)
    c: Vertical(g1)
    c: Coincident(g2,g0)
    c: Vertical(g2)
    c: Block(g2)
    c: Coincident(g6,g2)
    c: Weight(g3) = 1
    c: Equal(g3,g4)
    c: Equal(g3,g5)
    c: InternalAlignment(g3,g6)
    c: InternalAlignment(g4,g6)
    c: InternalAlignment(g5,g6)
    c: InternalAlignment(g7,g6)
    c: InternalAlignment(g8,g6)
    c: Block(g6)
    c: Coincident(g9,g1)
    c: Coincident(g9,g6)
    c: Horizontal(g9)
    c: Vertical(g10)
    c: Block(g10)
    c: Horizontal(g11)
    c: Block(g11)
    c: Coincident(g12,g10)
    c: Horizontal(g12)
    c: Block(g12)
    c: Coincident(g13,g11)
    c: Vertical(g13)
    c: Block(g13)
    c: Coincident(g14,g10)
    c: Horizontal(g14)
    c: Block(g14)
    c: Block(g9)
    c: Block(g1)
    c: Weight(g15) = 1
    c: Equal(g15,g16)
    c: Equal(g15,g17)
    c: InternalAlignment(g15,g18)
    c: InternalAlignment(g16,g18)
    c: InternalAlignment(g17,g18)
    c: InternalAlignment(g19,g18)
    c: InternalAlignment(g20,g18)
    c: Weight(g21) = 1
    c: Equal(g21,g22)
    c: Equal(g21,g23)
    c: InternalAlignment(g21,g24)
    c: InternalAlignment(g22,g24)
    c: InternalAlignment(g23,g24)
    c: InternalAlignment(g25,g24)
    c: InternalAlignment(g26,g24)
    c: Weight(g27) = 1
    c: Equal(g27,g28)
    c: Equal(g27,g29)
    c: Coincident(g30,g14)
    c: InternalAlignment(g27,g30)
    c: InternalAlignment(g28,g30)
    c: InternalAlignment(g29,g30)
    c: InternalAlignment(g31,g30)
    c: InternalAlignment(g32,g30)
    c: Coincident(g36,g12)
    c: Weight(g33) = 1
    c: Equal(g33,g34)
    c: Equal(g33,g35)
    c: Coincident(g36,g11)
    c: InternalAlignment(g33,g36)
    c: InternalAlignment(g34,g36)
    c: InternalAlignment(g35,g36)
    c: InternalAlignment(g37,g36)
    c: InternalAlignment(g38,g36)
    c: Coincident(g42,g13)
    c: Weight(g39) = 1
    c: Equal(g39,g40)
    c: Equal(g39,g41)
    c: Coincident(g42,g1)
    c: InternalAlignment(g39,g42)
    c: InternalAlignment(g40,g42)
    c: InternalAlignment(g41,g42)
    c: InternalAlignment(g43,g42)
    c: InternalAlignment(g44,g42)
    c: Block(g18)
    c: Block(g24)
    c: Block(g30)
    c: Block(g36)
    c: Block(g42)
    c: Horizontal(g45)
    c: Coincident(g45,g0)
    c: Vertical(g46)
    c: Coincident(g46,g45)
    c: Coincident(g47,g46)
    c: Coincident(g47,g18)
    c: Horizontal(g47)
    c: Block(g46)
    c: Coincident(g48,g18)
    c: Horizontal(g48)
    c: Distance(g48) = 1.33
    c: Vertical(g49)
    c: Coincident(g49,g48)
    c: Coincident(g50,g49)
    c: Coincident(g50,g24)
    c: Horizontal(g50)
    c: Tangent(g50,g22)
    c: Horizontal(g51)
    c: Coincident(g51,g24)
    c: Block(g51)
    c: Vertical(g52)
    c: Block(g52)
    c: Coincident(g52,g51)
    c: Coincident(g53,g52)
    c: Coincident(g53,g30)
    c: Horizontal(g53)
    c: Distance(g1) = 8.5
FEATURE [Part::Feature] Face024
  shape: bbox 9.8 x 26.5 x 2e-07 mm, 1 faces, 0 solids (baked)
FEATURE [Part::Revolution] Revolve024
  Angle = 360
  Axis = (0,1,0)
  Base = (0,0,0)
  FaceMakerClass = Part::FaceMakerBullseye
  Placement = pos=(0,0,0) rot=(0,0,1;1.5708rad)
  Solid = false
  Source = -> Face024
  Symmetric = false
FEATURE [Part::Feature] Face025
  shape: bbox 9.8 x 26.5 x 2e-07 mm, 1 faces, 0 solids (baked)
FEATURE [Part::Revolution] Revolve025
  Angle = 360
  Axis = (0,1,0)
  Base = (0,0,0)
  FaceMakerClass = Part::FaceMakerBullseye
  Placement = pos=(0,0,0) rot=(0,0,1;1.5708rad)
  Solid = false
  Source = -> Face025
  Symmetric = false
FEATURE [Part::MultiFuse] Fusion033
  Placement = pos=(-18,19,36) rot=(0,0,1;0rad)
  Shapes = -> [Revolve025,Revolve024]
FEATURE [Part::Cylinder] Cylinder014
  Angle = 360
  AttacherType = Attacher::AttachEngine3D
  Height = 20
  Placement = pos=(0,0,36.15) rot=(0,0,1;0rad)
  Radius = 14.3
FEATURE [Part::Cylinder] Cylinder015
  Angle = 360
  AttacherType = Attacher::AttachEngine3D
  Height = 10
  Placement = pos=(0,0,36.15) rot=(0,0,1;0rad)
  Radius = 4
FEATURE [Part::MultiFuse] Fusion034  label="removeToCreteHoleForPlugHousing004"
  Placement = pos=(-42,19,36) rot=(0,1,0;1.5708rad)
  Shapes = -> [Cylinder014,Cylinder015]
FEATURE [Part::Cut] Cut008  label="top004"
  Base = -> Cut004
  Placement = pos=(-1,0,0) rot=(0,0,1;0rad)
  Tool = -> Fusion034
FEATURE [Part::Box] Box005  label="Cube005"
  AttacherType = Attacher::AttachEngine3D
  Height = 28
  Length = 3
  Placement = pos=(110.7,19,22) rot=(0,0,1;0rad)
  Width = 15.7
FEATURE [Part::Cylinder] Cylinder016
  Angle = 360
  AttacherType = Attacher::AttachEngine3D
  Height = 10
  Placement = pos=(0,0,36.15) rot=(0,0,1;0rad)
  Radius = 4
FEATURE [Part::Cylinder] Cylinder017
  Angle = 360
  AttacherType = Attacher::AttachEngine3D
  Height = 20
  Placement = pos=(0,0,36.15) rot=(0,0,1;0rad)
  Radius = 10.3
FEATURE [Part::MultiFuse] Fusion035  label="removeToCreteHoleForPlugHousing005"
  Placement = pos=(70,19,36) rot=(0,1,0;1.5708rad)
  Shapes = -> [Cylinder017,Cylinder016]
FEATURE [Part::Cut] Cut009  label="plugHousingTab001"
  Base = -> Box005
  Placement = pos=(-107.4,-14,0) rot=(0,0,1;0rad)
  Tool = -> Fusion035
FEATURE [Part::Box] Box006  label="Cube006"
  AttacherType = Attacher::AttachEngine3D
  Height = 28
  Length = 3
  Placement = pos=(110.7,19,22) rot=(0,0,1;0rad)
  Width = 15.7
FEATURE [Part::Cylinder] Cylinder018
  Angle = 360
  AttacherType = Attacher::AttachEngine3D
  Height = 10
  Placement = pos=(0,0,36.15) rot=(0,0,1;0rad)
  Radius = 4
FEATURE [Part::Cylinder] Cylinder019
  Angle = 360
  AttacherType = Attacher::AttachEngine3D
  Height = 20
  Placement = pos=(0,0,36.15) rot=(0,0,1;0rad)
  Radius = 10.3
FEATURE [Part::MultiFuse] Fusion036  label="removeToCreteHoleForPlugHousing006"
  Placement = pos=(70,19,36) rot=(0,1,0;1.5708rad)
  Shapes = -> [Cylinder019,Cylinder018]
FEATURE [Part::Cut] Cut010  label="plugHousingTab002"
  Base = -> Box006
  Placement = pos=(-107.4,-14,0) rot=(0,0,1;0rad)
  Tool = -> Fusion036
FEATURE [Part::MultiFuse] Fusion037
  Placement = pos=(9.6,23,0) rot=(0,0,1;3.14159rad)
  Shapes = -> [Cut009,Cut010]
FEATURE [Part::Box] Box  label="Cube"
  AttacherType = Attacher::AttachEngine3D
  Height = 10
  Length = 3
  Placement = pos=(3.3,4,12) rot=(0,0,1;0rad)
  Width = 10
FEATURE [Part::Fillet] Fillet004
  Base = -> Fusion028
  Edges = 1 edges r=2: [Edge25]
FEATURE [Part::Fillet] Fillet005  label="plugHousing046"
  Base = -> Fillet004
  Edges = 1 edges r=2: [Edge8]
FEATURE [Part::Fillet] Fillet006
  Base = -> Box
  Edges = 1 edges r=2: [Edge11]
FEATURE [Part::Box] Box007  label="Cube007"
  AttacherType = Attacher::AttachEngine3D
  Height = 10
  Length = 3
  Placement = pos=(3.3,4,50) rot=(0,0,1;0rad)
  Width = 10
FEATURE [Part::Fillet] Fillet007
  Base = -> Box007
  Edges = 1 edges r=2: [Edge12]
FEATURE [Part::Box] Box008  label="Cube008"
  AttacherType = Attacher::AttachEngine3D
  Height = 28
  Length = 4
  Placement = pos=(5,0,22) rot=(0,0,1;0rad)
  Width = 10
FEATURE [Part::Fillet] Fillet008
  Base = -> Box008
  Edges = 1 edges r=1: [Edge7]
FEATURE [Part::Fillet] Fillet009
  Base = -> Fillet008
  Edges = 1 edges r=2: [Edge5]
FEATURE [Part::Fillet] Fillet010
  Base = -> Fillet009
  Edges = 1 edges r=2: [Edge2]
FEATURE [Sketcher::SketchObject] Sketch009  label="topSketch003"
  FullyConstrained = true
  sketch-geometry (4):
    g0: LineSegment StartX=16.8446 StartY=31.512 StartZ=0 EndX=16.3251 EndY=34.4666 EndZ=0
    g1: ArcOfCircle CenterX=19 CenterY=19.2524 CenterZ=0 NormalX=0 NormalY=0 NormalZ=1 AngleXU=0 Radius=15.4476 StartAngle=1.74483 EndAngle=2.72717
    g2: ArcOfCircle CenterX=19 CenterY=19.2524 CenterZ=0 NormalX=0 NormalY=0 NormalZ=1 AngleXU=0 Radius=12.4476 StartAngle=1.74483 EndAngle=2.73189
    g3: LineSegment StartX=4.86004 StartY=25.4725 StartZ=0 EndX=7.58253 EndY=24.2107 EndZ=0
  constraints (7):
    c: Block(g0)
    c: Coincident(g1,g0)
    c: Coincident(g2,g0)
    c: Coincident(g3,g1)
    c: Coincident(g3,g2)
    c: Block(g1)
    c: Block(g2)
FEATURE [Part::Extrusion] Extrude008
  Base = -> Sketch009
  Dir = (0,0,1)
  DirMode = 2
  FaceMakerClass = Part::FaceMakerBullseye
  LengthFwd = 10
  LengthRev = 0
  Placement = pos=(0,0,31) rot=(0,0,1;0rad)
  Solid = true
  Symmetric = false
FEATURE [Part::Cylinder] Cylinder020
  Angle = 360
  AttacherType = Attacher::AttachEngine3D
  Height = 20
  Placement = pos=(0,0,36.15) rot=(0,0,1;0rad)
  Radius = 8.2
FEATURE [Part::Cylinder] Cylinder021
  Angle = 360
  AttacherType = Attacher::AttachEngine3D
  Height = 10
  Placement = pos=(0,0,36.15) rot=(0,0,1;0rad)
  Radius = 4
FEATURE [Part::MultiFuse] Fusion038  label="removeToCreteHoleForPlugHousing007"
  Placement = pos=(-42,19,36) rot=(0,1,0;1.5708rad)
  Shapes = -> [Cylinder020,Cylinder021]
FEATURE [Part::Cut] Cut011
  Base = -> Extrude008
  Tool = -> Fusion038
FEATURE [Part::Fillet] Fillet011
  Base = -> Cut011
  Edges = 1 edges r=2: [Edge1]
FEATURE [Part::Fillet] Fillet012
  Base = -> Fillet011
  Edges = 1 edges r=2.5: [Edge1]
FEATURE [Part::Fillet] Fillet013
  Base = -> Fillet012
  Edges = 1 edges r=2.5: [Edge2]
FEATURE [Part::Box] Box010  label="Cube010"
  AttacherType = Attacher::AttachEngine3D
  Height = 16
  Length = 8
  Placement = pos=(12.7,31.52,28) rot=(0,0,1;0rad)
  Width = 4
FEATURE [Sketcher::SketchObject] Sketch010  label="topSketch004"
  FullyConstrained = true
  sketch-geometry (4):
    g0: LineSegment StartX=16.8446 StartY=31.512 StartZ=0 EndX=16.3251 EndY=34.4666 EndZ=0
    g1: ArcOfCircle CenterX=19 CenterY=19.2524 CenterZ=0 NormalX=0 NormalY=0 NormalZ=1 AngleXU=0 Radius=15.4476 StartAngle=1.74483 EndAngle=2.72717
    g2: ArcOfCircle CenterX=19 CenterY=19.2524 CenterZ=0 NormalX=0 NormalY=0 NormalZ=1 AngleXU=0 Radius=12.4476 StartAngle=1.74483 EndAngle=2.73189
    g3: LineSegment StartX=4.86004 StartY=25.4725 StartZ=0 EndX=7.58253 EndY=24.2107 EndZ=0
  constraints (7):
    c: Block(g0)
    c: Coincident(g1,g0)
    c: Coincident(g2,g0)
    c: Coincident(g3,g1)
    c: Coincident(g3,g2)
    c: Block(g1)
    c: Block(g2)
FEATURE [Part::Cylinder] Cylinder022
  Angle = 360
  AttacherType = Attacher::AttachEngine3D
  Height = 10
  Placement = pos=(0,0,36.15) rot=(0,0,1;0rad)
  Radius = 4
FEATURE [Sketcher::SketchObject] Sketch011  label="topSketch005"
  FullyConstrained = true
  sketch-geometry (4):
    g0: LineSegment StartX=16.8446 StartY=31.512 StartZ=0 EndX=16.3251 EndY=34.4666 EndZ=0
    g1: ArcOfCircle CenterX=19 CenterY=19.2524 CenterZ=0 NormalX=0 NormalY=0 NormalZ=1 AngleXU=0 Radius=15.4476 StartAngle=1.74483 EndAngle=2.72717
    g2: ArcOfCircle CenterX=19 CenterY=19.2524 CenterZ=0 NormalX=0 NormalY=0 NormalZ=1 AngleXU=0 Radius=12.4476 StartAngle=1.74483 EndAngle=2.73189
    g3: LineSegment StartX=4.86004 StartY=25.4725 StartZ=0 EndX=7.58253 EndY=24.2107 EndZ=0
  constraints (7):
    c: Block(g0)
    c: Coincident(g1,g0)
    c: Coincident(g2,g0)
    c: Coincident(g3,g1)
    c: Coincident(g3,g2)
    c: Block(g1)
    c: Block(g2)
FEATURE [Part::Extrusion] Extrude010
  Base = -> Sketch011
  Dir = (0,0,1)
  DirMode = 2
  FaceMakerClass = Part::FaceMakerBullseye
  LengthFwd = 10.6
  LengthRev = 0
  Placement = pos=(0,0,31) rot=(0,0,1;0rad)
  Solid = true
  Symmetric = false
FEATURE [Part::Cylinder] Cylinder023
  Angle = 360
  AttacherType = Attacher::AttachEngine3D
  Height = 20
  Placement = pos=(0,0,36.15) rot=(0,0,1;0rad)
  Radius = 8.2
FEATURE [Part::MultiFuse] Fusion039  label="removeToCreteHoleForPlugHousing008"
  Placement = pos=(-42,19,36) rot=(0,1,0;1.5708rad)
  Shapes = -> [Cylinder023,Cylinder022]
FEATURE [Part::Cut] Cut012
  Base = -> Extrude010
  Placement = pos=(0,0,-0.3) rot=(0,0,1;0rad)
  Tool = -> Fusion039
FEATURE [Part::Cut] Cut013
  Base = -> Box010
  Tool = -> Cut012
FEATURE [Part::Fillet] Fillet014
  Base = -> Cut013
  Edges = 1 edges r=0.7: [Edge13]
FEATURE [Part::Fillet] Fillet015
  Base = -> Fillet014
  Edges = 1 edges r=0.7: [Edge13]
FEATURE [Part::Fillet] Fillet016
  Base = -> Fillet015
  Edges = 1 edges r=0.7: [Edge16]
FEATURE [Part::Fillet] Fillet017
  Base = -> Fillet016
  Edges = 1 edges r=0.7: [Edge11]
FEATURE [Part::Fillet] Fillet018
  Base = -> Fillet017
  Edges = 1 edges r=0.7: [Edge10]
FEATURE [Part::Fillet] Fillet019
  Base = -> Fillet018
  Edges = 1 edges r=1.2: [Edge5]
FEATURE [Part::Fillet] Fillet020
  Base = -> Fillet019
  Edges = 1 edges r=1.2: [Edge12]
FEATURE [Part::Fillet] Fillet021
  Base = -> Fillet020
  Edges = 1 edges r=2: [Edge1]
  Placement = pos=(0.3,0,0) rot=(0,0,1;0rad)
FEATURE [Part::MultiFuse] Fusion040  label="top005"
  Shapes = -> [Cut008,Fillet021]
FEATURE [Part::MultiFuse] Fusion041  label="wireHolder"
  Shapes = -> [Fusion033,Fillet013]
FEATURE [Part::MultiFuse] Fusion042
  Shapes = -> [Fillet007,Fusion041]
FEATURE [Part::MultiFuse] Fusion043  label="wireHolder001"
  Shapes = -> [Fusion042,Fillet010]
FEATURE [Part::MultiFuse] Fusion044  label="wireHolder002"
  Shapes = -> [Fillet006,Fusion037,Fusion043]
FEATURE [Part::Feature] Face026
  shape: bbox 11 x 6 x 2e-07 mm, 1 faces, 0 solids (baked)
FEATURE [Part::Revolution] Revolve026
  Angle = 360
  Axis = (0,1,0)
  Base = (0,0,0)
  FaceMakerClass = Part::FaceMakerBullseye
  Placement = pos=(30.3,-1,19.7) rot=(0,0,1;0rad)
  Solid = false
  Source = -> Face026
  Symmetric = false
FEATURE [Sketcher::SketchObject] Sketch013  label="topSketch006"
  FullyConstrained = true
  sketch-geometry (13):
    g0: LineSegment StartX=117 StartY=19 StartZ=0 EndX=117 EndY=38 EndZ=0
    g1: ArcOfCircle CenterX=98 CenterY=19 CenterZ=0 NormalX=0 NormalY=0 NormalZ=1 AngleXU=0 Radius=19 StartAngle=5.7297 EndAngle=6.28319
    g2: LineSegment StartX=0 StartY=3 StartZ=0 EndX=0 EndY=19 EndZ=0
    g3: LineSegment StartX=19 StartY=38 StartZ=0 EndX=117 EndY=38 EndZ=0
    g4: ArcOfCircle CenterX=19 CenterY=19 CenterZ=0 NormalX=0 NormalY=0 NormalZ=1 AngleXU=0 Radius=19 StartAngle=1.5708 EndAngle=3.14159
    g5: ArcOfCircle CenterX=19 CenterY=19 CenterZ=0 NormalX=0 NormalY=0 NormalZ=1 AngleXU=0 Radius=16 StartAngle=1.5708 EndAngle=3.14159
    g6: ArcOfCircle CenterX=98 CenterY=19 CenterZ=0 NormalX=0 NormalY=0 NormalZ=1 AngleXU=0 Radius=16 StartAngle=5.60905 EndAngle=6.28319
    g7: LineSegment StartX=114 StartY=19 StartZ=0 EndX=114 EndY=35 EndZ=0
    g8: LineSegment StartX=110.5 StartY=9.01251 StartZ=0 EndX=114.163 EndY=9.01251 EndZ=0
    g9: LineSegment StartX=114 StartY=35 StartZ=0 EndX=19 EndY=35 EndZ=0
    g10: LineSegment StartX=0 StartY=3 StartZ=0 EndX=0 EndY=0 EndZ=0
    g11: LineSegment StartX=3 StartY=0 StartZ=0 EndX=0 EndY=0 EndZ=0
    g12: LineSegment StartX=3 StartY=19 StartZ=0 EndX=3 EndY=0 EndZ=0
  constraints (33):
    c: Vertical(g0)
    c: Distance(g0) = 19
    c: Block(g0)
    c: Coincident(g1,g0)
    c: Block(g1)
    c: Vertical(g2)
    c: Block(g2)
    c: Coincident(g3,g0)
    c: Horizontal(g3)
    c: Distance(g3) = 98
    c: Coincident(g4,g3)
    c: Coincident(g4,g2)
    c: Block(g4)
    c: Coincident(g5,g4)
    c: Coincident(g6,g1)
    c: Block(g6)
    c: Block(g5)
    c: Coincident(g7,g6)
    c: Vertical(g7)
    c: Coincident(g8,g6)
    c: Coincident(g8,g1)
    c: Coincident(g9,g7)
    c: Coincident(g9,g5)
    c: Horizontal(g9)
    c: Tangent(g9,g5)
    c: Coincident(g10,g2)
    c: Distance(g10) = 3
    c: Vertical(g10)
    c: Coincident(g11,g10)
    c: Horizontal(g11)
    c: Coincident(g12,g5)
    c: Coincident(g12,g11)
    c: Vertical(g12)
FEATURE [Part::Extrusion] Extrude011  label="top006"
  Base = -> Sketch013
  Dir = (0,0,1)
  DirMode = 2
  FaceMakerClass = Part::FaceMakerBullseye
  LengthFwd = 72
  LengthRev = 0
  Solid = true
  Symmetric = false
FEATURE [Sketcher::SketchObject] Sketch014
  FullyConstrained = true
  MapMode = 3
  Placement = pos=(0,0,0) rot=(1,0,0;1.5708rad)
  Support = -> [Extrude011]
  sketch-geometry (8):
    g0: Circle CenterX=80.351 CenterY=-67.6202 CenterZ=0 NormalX=0 NormalY=0 NormalZ=1 AngleXU=0 Radius=2
    g1: Circle CenterX=80.351 CenterY=-67.6202 CenterZ=0 NormalX=0 NormalY=0 NormalZ=1 AngleXU=0 Radius=3
    g2: Circle CenterX=80.351 CenterY=-4.92017 CenterZ=0 NormalX=0 NormalY=0 NormalZ=1 AngleXU=0 Radius=2
    g3: Circle CenterX=80.351 CenterY=-4.92017 CenterZ=0 NormalX=0 NormalY=0 NormalZ=1 AngleXU=0 Radius=3
    g4: Circle CenterX=23.851 CenterY=-4.92017 CenterZ=0 NormalX=0 NormalY=0 NormalZ=1 AngleXU=0 Radius=2
    g5: Circle CenterX=23.851 CenterY=-4.92017 CenterZ=0 NormalX=0 NormalY=0 NormalZ=1 AngleXU=0 Radius=3
    g6: Circle CenterX=23.851 CenterY=-67.6202 CenterZ=0 NormalX=0 NormalY=0 NormalZ=1 AngleXU=0 Radius=2
    g7: Circle CenterX=23.851 CenterY=-67.6202 CenterZ=0 NormalX=0 NormalY=0 NormalZ=1 AngleXU=0 Radius=3
  constraints (8):
    c: Block(g3)
    c: Block(g2)
    c: Block(g1)
    c: Block(g0)
    c: Block(g6)
    c: Block(g7)
    c: Block(g4)
    c: Block(g5)
FEATURE [Part::Feature] Face027
  shape: bbox 11 x 6 x 2e-07 mm, 1 faces, 0 solids (baked)
FEATURE [Part::Revolution] Revolve027
  Angle = 360
  Axis = (0,1,0)
  Base = (0,0,0)
  FaceMakerClass = Part::FaceMakerBullseye
  Placement = pos=(30.3,-1,51.7) rot=(0,0,1;0rad)
  Solid = false
  Source = -> Face027
  Symmetric = false
FEATURE [Part::Feature] Face028
  shape: bbox 11 x 6 x 2e-07 mm, 1 faces, 0 solids (baked)
FEATURE [Part::Revolution] Revolve028
  Angle = 360
  Axis = (0,1,0)
  Base = (0,0,0)
  FaceMakerClass = Part::FaceMakerBullseye
  Placement = pos=(62.3,-1,19.7) rot=(0,0,1;0rad)
  Solid = false
  Source = -> Face028
  Symmetric = false
FEATURE [Part::Feature] Face029
  shape: bbox 11 x 6 x 2e-07 mm, 1 faces, 0 solids (baked)
FEATURE [Part::Revolution] Revolve029
  Angle = 360
  Axis = (0,1,0)
  Base = (0,0,0)
  FaceMakerClass = Part::FaceMakerBullseye
  Placement = pos=(62.3,-1,51.7) rot=(0,0,1;0rad)
  Solid = false
  Source = -> Face029
  Symmetric = false
FEATURE [Part::Feature] Wire
  shape: bbox 11 x 5.2 x 2e-07 mm, 0 faces, 0 solids (baked)
FEATURE [Part::Revolution] Revolve030
  Angle = 360
  Axis = (0,1,0)
  Base = (0,0,0)
  FaceMakerClass = Part::FaceMakerBullseye
  Placement = pos=(30.3,38,19.7) rot=(0,0,1;0rad)
  Solid = true
  Source = -> Wire
  Symmetric = false
FEATURE [Part::Feature] Wire001
  shape: bbox 11 x 5.2 x 2e-07 mm, 0 faces, 0 solids (baked)
FEATURE [Part::Revolution] Revolve031
  Angle = 360
  Axis = (0,1,0)
  Base = (0,0,0)
  FaceMakerClass = Part::FaceMakerBullseye
  Placement = pos=(30.3,38,51.7) rot=(0,0,1;0rad)
  Solid = true
  Source = -> Wire001
  Symmetric = false
FEATURE [Part::Feature] Wire002
  shape: bbox 11 x 5.2 x 2e-07 mm, 0 faces, 0 solids (baked)
FEATURE [Part::Revolution] Revolve032
  Angle = 360
  Axis = (0,1,0)
  Base = (0,0,0)
  FaceMakerClass = Part::FaceMakerBullseye
  Placement = pos=(62.3,38,51.7) rot=(0,0,1;0rad)
  Solid = true
  Source = -> Wire002
  Symmetric = false
FEATURE [Part::Feature] Wire003
  shape: bbox 11 x 5.2 x 2e-07 mm, 0 faces, 0 solids (baked)
FEATURE [Part::Revolution] Revolve033
  Angle = 360
  Axis = (0,1,0)
  Base = (0,0,0)
  FaceMakerClass = Part::FaceMakerBullseye
  Placement = pos=(62.3,38,19.7) rot=(0,0,1;0rad)
  Solid = true
  Source = -> Wire003
  Symmetric = false
FEATURE [Part::MultiFuse] Fusion045  label="altRandScrewHousing"
  Shapes = -> [Revolve029,Revolve027,Revolve028,Revolve026]
FEATURE [Part::MultiFuse] Fusion046  label="fanScrewHousing"
  Shapes = -> [Revolve033,Revolve032,Revolve031,Revolve030]
FEATURE [Sketcher::SketchObject] Sketch015
  FullyConstrained = true
  sketch-geometry (17):
    g0: Circle CenterX=-3.5 CenterY=23.5 CenterZ=0 NormalX=0 NormalY=0 NormalZ=1 AngleXU=0 Radius=1
    g1: Circle CenterX=-1 CenterY=15.25 CenterZ=0 NormalX=0 NormalY=0 NormalZ=1 AngleXU=0 Radius=1
    g2: Circle CenterX=-3.5 CenterY=7 CenterZ=0 NormalX=0 NormalY=0 NormalZ=1 AngleXU=0 Radius=1
    g3: BSplineCurve PolesCount=3 KnotsCount=2 Degree=2 IsPeriodic=0
    g4: GeomPoint X=-3.5 Y=23.5 Z=0
    g5: GeomPoint X=-3.5 Y=7 Z=0
    g6: Circle CenterX=-4.8 CenterY=30.5 CenterZ=0 NormalX=0 NormalY=0 NormalZ=1 AngleXU=0 Radius=1
    g7: Circle CenterX=-3.5 CenterY=30.5 CenterZ=0 NormalX=0 NormalY=0 NormalZ=1 AngleXU=0 Radius=1
    g8: Circle CenterX=-3.5 CenterY=29.2 CenterZ=0 NormalX=0 NormalY=0 NormalZ=1 AngleXU=0 Radius=1
    g9: BSplineCurve PolesCount=3 KnotsCount=2 Degree=2 IsPeriodic=0
    g10: GeomPoint X=-4.8 Y=30.5 Z=0
    g11: GeomPoint X=-3.5 Y=29.2 Z=0
    g12: LineSegment StartX=-3.5 StartY=29.2 StartZ=0 EndX=-3.5 EndY=23.5 EndZ=0
    g13: LineSegment StartX=-4.8 StartY=30.5 StartZ=0 EndX=0 EndY=30.5 EndZ=0
    g14: LineSegment StartX=-3.5 StartY=0.3 StartZ=0 EndX=0 EndY=0.3 EndZ=0
    g15: LineSegment StartX=-3.5 StartY=0.3 StartZ=0 EndX=-3.5 EndY=7 EndZ=0
    g16: LineSegment StartX=0 StartY=0.3 StartZ=0 EndX=0 EndY=30.5 EndZ=0
  constraints (33):
    c: Weight(g0) = 1
    c: Equal(g0,g1)
    c: Equal(g0,g2)
    c: InternalAlignment(g0,g3)
    c: InternalAlignment(g1,g3)
    c: InternalAlignment(g2,g3)
    c: InternalAlignment(g4,g3)
    c: InternalAlignment(g5,g3)
    c: Block(g3)
    c: Weight(g6) = 1
    c: Equal(g6,g7)
    c: Equal(g6,g8)
    c: InternalAlignment(g6,g9)
    c: InternalAlignment(g7,g9)
    c: InternalAlignment(g8,g9)
    c: InternalAlignment(g10,g9)
    c: InternalAlignment(g11,g9)
    c: Block(g9)
    c: Coincident(g12,g9)
    c: Coincident(g12,g3)
    c: Vertical(g12)
    c: Coincident(g13,g9)
    c: Horizontal(g13)
    c: Distance(g13) = 4.8
    c: Horizontal(g14)
    c: Block(g14)
    c: Coincident(g15,g14)
    c: Coincident(g15,g3)
    c: Vertical(g15)
    c: Coincident(g16,g14)
    c: Coincident(g16,g13)
    c: Vertical(g16)
    c: Tangent(g16,g1)
FEATURE [Sketcher::SketchObject] Sketch016
  FullyConstrained = true
  sketch-geometry (16):
    g0: Circle CenterX=-3.5 CenterY=23.5 CenterZ=0 NormalX=0 NormalY=0 NormalZ=1 AngleXU=0 Radius=1
    g1: Circle CenterX=-1 CenterY=15.25 CenterZ=0 NormalX=0 NormalY=0 NormalZ=1 AngleXU=0 Radius=1
    g2: Circle CenterX=-3.5 CenterY=7 CenterZ=0 NormalX=0 NormalY=0 NormalZ=1 AngleXU=0 Radius=1
    g3: BSplineCurve PolesCount=3 KnotsCount=2 Degree=2 IsPeriodic=0
    g4: GeomPoint X=-3.5 Y=23.5 Z=0
    g5: GeomPoint X=-3.5 Y=7 Z=0
    g6: LineSegment StartX=-3.5 StartY=28.2 StartZ=0 EndX=-3.5 EndY=23.5 EndZ=0
    g7: LineSegment StartX=0 StartY=29.5 StartZ=0 EndX=0 EndY=30 EndZ=0
    g8: LineSegment StartX=-3.5 StartY=28.2 StartZ=0 EndX=-3.5 EndY=30 EndZ=0
    g9: LineSegment StartX=0 StartY=30 StartZ=0 EndX=0 EndY=30.5 EndZ=0
    g10: LineSegment StartX=0 StartY=30.5 StartZ=0 EndX=-3.5 EndY=30.5 EndZ=0
    g11: LineSegment StartX=-3.5 StartY=30.5 StartZ=0 EndX=-3.5 EndY=30 EndZ=0
    g12: LineSegment StartX=0 StartY=29.5 StartZ=0 EndX=0 EndY=5 EndZ=0
    g13: LineSegment StartX=-3.5 StartY=0.3 StartZ=0 EndX=-3.5 EndY=7 EndZ=0
    g14: LineSegment StartX=-3.5 StartY=0.3 StartZ=0 EndX=0 EndY=0.3 EndZ=0
    g15: LineSegment StartX=0 StartY=5 StartZ=0 EndX=0 EndY=0.3 EndZ=0
  constraints (39):
    c: Weight(g0) = 1
    c: Equal(g0,g1)
    c: Equal(g0,g2)
    c: InternalAlignment(g0,g3)
    c: InternalAlignment(g1,g3)
    c: InternalAlignment(g2,g3)
    c: InternalAlignment(g4,g3)
    c: InternalAlignment(g5,g3)
    c: Block(g3)
    c: Coincident(g6,g3)
    c: Vertical(g6)
    c: Vertical(g7)
    c: Distance(g7) = 0.5
    c: Coincident(g8,g6)
    c: Vertical(g8)
    c: Block(g6)
    c: Block(g7)
    c: Vertical(g9)
    c: Equal(g7,g9) = 0.5
    c: Block(g9)
    c: Coincident(g9,g7)
    c: Horizontal(g10)
    c: Coincident(g10,g9)
    c: Coincident(g11,g10)
    c: Coincident(g11,g8)
    c: Vertical(g11)
    c: Block(g11)
    c: Coincident(g12,g7)
    c: Vertical(g12)
    c: Coincident(g13,g3)
    c: Vertical(g13)
    c: Distance(g13) = 6.7
    c: Coincident(g14,g13)
    c: Horizontal(g14)
    c: Block(g14)
    c: Coincident(g15,g12)
    c: Coincident(g15,g14)
    c: Vertical(g15)
    c: Block(g15)
FEATURE [Sketcher::SketchObject] Sketch017
  FullyConstrained = true
  sketch-geometry (11):
    g0: LineSegment StartX=-3.5 StartY=1e-16 StartZ=0 EndX=-1.6 EndY=1e-16 EndZ=0
    g1: LineSegment StartX=-1.6 StartY=1e-16 StartZ=0 EndX=-1.6 EndY=1.5 EndZ=0
    g2: LineSegment StartX=-3.5 StartY=1.5 StartZ=0 EndX=-1.6 EndY=1.5 EndZ=0
    g3: LineSegment StartX=-3.5 StartY=1e-16 StartZ=0 EndX=-4.8 EndY=1e-16 EndZ=0
    g4: Circle CenterX=-3.5 CenterY=1.3 CenterZ=0 NormalX=0 NormalY=0 NormalZ=1 AngleXU=0 Radius=1
    g5: Circle CenterX=-3.5 CenterY=1e-16 CenterZ=0 NormalX=0 NormalY=0 NormalZ=1 AngleXU=0 Radius=1
    g6: Circle CenterX=-4.8 CenterY=1e-16 CenterZ=0 NormalX=0 NormalY=0 NormalZ=1 AngleXU=0 Radius=1
    g7: BSplineCurve PolesCount=3 KnotsCount=2 Degree=2 IsPeriodic=0
    g8: GeomPoint X=-3.5 Y=1.3 Z=0
    g9: GeomPoint X=-4.8 Y=1e-16 Z=0
    g10: LineSegment StartX=-3.5 StartY=1.3 StartZ=0 EndX=-3.5 EndY=1.5 EndZ=0
  constraints (24):
    c: Horizontal(g0)
    c: Distance(g0) = 1.9
    c: Block(g0)
    c: Coincident(g1,g0)
    c: Vertical(g1)
    c: Coincident(g2,g1)
    c: Horizontal(g2)
    c: Coincident(g3,g0)
    c: Horizontal(g3)
    c: Distance(g3) = 1.3
    c: Weight(g4) = 1
    c: Equal(g4,g5)
    c: Coincident(g5,g0)
    c: Equal(g4,g6)
    c: Coincident(g7,g3)
    c: InternalAlignment(g4,g7)
    c: InternalAlignment(g5,g7)
    c: InternalAlignment(g6,g7)
    c: InternalAlignment(g8,g7)
    c: InternalAlignment(g9,g7)
    c: Coincident(g10,g7)
    c: Coincident(g10,g2)
    c: Vertical(g10)
    c: Block(g10)
FEATURE [Part::Feature] Face035
  shape: bbox 3.2 x 1.5 x 2e-07 mm, 1 faces, 0 solids (baked)
FEATURE [Part::Revolution] Revolve039  label="backCaseScrewRetainer"
  Angle = 360
  Axis = (0,1,0)
  Base = (0,0,0)
  FaceMakerClass = Part::FaceMakerBullseye
  Placement = pos=(12.5,3,62) rot=(0,0,1;0rad)
  Solid = false
  Source = -> Face035
  Symmetric = false
FEATURE [Part::Feature] Face036
  shape: bbox 3.2 x 1.5 x 2e-07 mm, 1 faces, 0 solids (baked)
FEATURE [Part::Feature] Face039
  shape: bbox 4.8 x 30.2 x 2e-07 mm, 1 faces, 0 solids (baked)
FEATURE [Part::Revolution] Revolve043  label="frontCaseScrewPost002"
  Angle = 360
  Axis = (0,1,0)
  Base = (0,0,0)
  FaceMakerClass = Part::FaceMakerBullseye
  Placement = pos=(89.5,4.5,3.5) rot=(0,0,1;0rad)
  Solid = false
  Source = -> Face039
  Symmetric = false
FEATURE [Part::Feature] Face042
  shape: bbox 4.8 x 30.2 x 2e-07 mm, 1 faces, 0 solids (baked)
FEATURE [Part::Revolution] Revolve046  label="frontCaseScrewPost003"
  Angle = 360
  Axis = (0,1,0)
  Base = (0,0,0)
  FaceMakerClass = Part::FaceMakerBullseye
  Placement = pos=(89.5,4.5,68.5) rot=(0,0,1;0rad)
  Solid = false
  Source = -> Face042
  Symmetric = false
FEATURE [Part::Feature] Face043
  shape: bbox 3.2 x 1.5 x 2e-07 mm, 1 faces, 0 solids (baked)
FEATURE [Part::Revolution] Revolve047  label="frontCaseScrewRetainer002"
  Angle = 360
  Axis = (0,1,0)
  Base = (0,0,0)
  FaceMakerClass = Part::FaceMakerBullseye
  Placement = pos=(89.5,3,68.5) rot=(0,0,1;0rad)
  Solid = false
  Source = -> Face043
  Symmetric = false
FEATURE [Part::Feature] Face044
  shape: bbox 3.2 x 1.5 x 2e-07 mm, 1 faces, 0 solids (baked)
FEATURE [Part::Revolution] Revolve048  label="frontCaseScrewRetainer003"
  Angle = 360
  Axis = (0,1,0)
  Base = (0,0,0)
  FaceMakerClass = Part::FaceMakerBullseye
  Placement = pos=(89.5,3,3.5) rot=(0,0,1;0rad)
  Solid = false
  Source = -> Face044
  Symmetric = false
FEATURE [App::MeasureDistance] Distance002  label="Distance: 1.67 mm"
  Distance = 1.66921
  P1 = (99.2361,4.7524,71.7)
  P2 = (99.2347,6.42161,71.7)
FEATURE [Sketcher::SketchObject] Sketch018
  FullyConstrained = true
  sketch-geometry (7):
    g0: LineSegment StartX=0 StartY=0 StartZ=0 EndX=0 EndY=6 EndZ=0
    g1: Circle CenterX=0 CenterY=0 CenterZ=0 NormalX=0 NormalY=0 NormalZ=1 AngleXU=0 Radius=1
    g2: Circle CenterX=8 CenterY=6 CenterZ=0 NormalX=0 NormalY=0 NormalZ=1 AngleXU=0 Radius=1
    g3: BSplineCurve PolesCount=3 KnotsCount=2 Degree=2 IsPeriodic=0
    g4: GeomPoint X=0 Y=0 Z=0
    g5: GeomPoint X=8 Y=6 Z=0
    g6: LineSegment StartX=0 StartY=6 StartZ=0 EndX=8 EndY=6 EndZ=0
  constraints (14):
    c: Coincident(g0,g-1)
    c: Distance(g0) = 6
    c: Vertical(g0)
    c: Coincident(g3,g0)
    c: Weight(g1) = 1
    c: Equal(g1,g2)
    c: InternalAlignment(g1,g3)
    c: InternalAlignment(g2,g3)
    c: InternalAlignment(g4,g3)
    c: InternalAlignment(g5,g3)
    c: Block(g3)
    c: Coincident(g6,g0)
    c: Coincident(g6,g3)
    c: Horizontal(g6)
FEATURE [Part::Extrusion] Extrude012  label="caseScrewPillarBracket"
  Base = -> Sketch018
  Dir = (0,0,1)
  DirMode = 2
  FaceMakerClass = Part::FaceMakerBullseye
  LengthFwd = 2.4
  LengthRev = 0
  Placement = pos=(15.76,29,8.8) rot=(0,1,0;0rad)
  Solid = true
  Symmetric = false
FEATURE [Sketcher::SketchObject] Sketch019
  FullyConstrained = true
  sketch-geometry (7):
    g0: LineSegment StartX=0 StartY=0 StartZ=0 EndX=0 EndY=6 EndZ=0
    g1: Circle CenterX=0 CenterY=0 CenterZ=0 NormalX=0 NormalY=0 NormalZ=1 AngleXU=0 Radius=1
    g2: Circle CenterX=8 CenterY=6 CenterZ=0 NormalX=0 NormalY=0 NormalZ=1 AngleXU=0 Radius=1
    g3: BSplineCurve PolesCount=3 KnotsCount=2 Degree=2 IsPeriodic=0
    g4: GeomPoint X=0 Y=0 Z=0
    g5: GeomPoint X=8 Y=6 Z=0
    g6: LineSegment StartX=0 StartY=6 StartZ=0 EndX=8 EndY=6 EndZ=0
  constraints (14):
    c: Coincident(g0,g-1)
    c: Distance(g0) = 6
    c: Vertical(g0)
    c: Coincident(g3,g0)
    c: Weight(g1) = 1
    c: Equal(g1,g2)
    c: InternalAlignment(g1,g3)
    c: InternalAlignment(g2,g3)
    c: InternalAlignment(g4,g3)
    c: InternalAlignment(g5,g3)
    c: Block(g3)
    c: Coincident(g6,g0)
    c: Coincident(g6,g3)
    c: Horizontal(g6)
FEATURE [Part::Extrusion] Extrude013  label="caseScrewPillarBracket001"
  Base = -> Sketch019
  Dir = (0,0,1)
  DirMode = 2
  FaceMakerClass = Part::FaceMakerBullseye
  LengthFwd = 2.4
  LengthRev = 0
  Placement = pos=(15.76,29,60.8) rot=(0,0,1;0rad)
  Solid = true
  Symmetric = false
FEATURE [Sketcher::SketchObject] Sketch020
  FullyConstrained = true
  sketch-geometry (7):
    g0: LineSegment StartX=0 StartY=0 StartZ=0 EndX=0 EndY=6 EndZ=0
    g1: Circle CenterX=0 CenterY=0 CenterZ=0 NormalX=0 NormalY=0 NormalZ=1 AngleXU=0 Radius=1
    g2: Circle CenterX=8 CenterY=6 CenterZ=0 NormalX=0 NormalY=0 NormalZ=1 AngleXU=0 Radius=1
    g3: BSplineCurve PolesCount=3 KnotsCount=2 Degree=2 IsPeriodic=0
    g4: GeomPoint X=0 Y=0 Z=0
    g5: GeomPoint X=8 Y=6 Z=0
    g6: LineSegment StartX=0 StartY=6 StartZ=0 EndX=8 EndY=6 EndZ=0
  constraints (14):
    c: Coincident(g0,g-1)
    c: Distance(g0) = 6
    c: Vertical(g0)
    c: Coincident(g3,g0)
    c: Weight(g1) = 1
    c: Equal(g1,g2)
    c: InternalAlignment(g1,g3)
    c: InternalAlignment(g2,g3)
    c: InternalAlignment(g4,g3)
    c: InternalAlignment(g5,g3)
    c: Block(g3)
    c: Coincident(g6,g0)
    c: Coincident(g6,g3)
    c: Horizontal(g6)
FEATURE [Part::Extrusion] Extrude014  label="caseScrewPillarBracket002"
  Base = -> Sketch020
  Dir = (0,0,1)
  DirMode = 2
  FaceMakerClass = Part::FaceMakerBullseye
  LengthFwd = 2.4
  LengthRev = 0
  Placement = pos=(13.7,29,13.26) rot=(0,-1,0;1.5708rad)
  Solid = true
  Symmetric = false
FEATURE [Sketcher::SketchObject] Sketch021
  FullyConstrained = true
  sketch-geometry (7):
    g0: LineSegment StartX=0 StartY=0 StartZ=0 EndX=0 EndY=6 EndZ=0
    g1: Circle CenterX=0 CenterY=0 CenterZ=0 NormalX=0 NormalY=0 NormalZ=1 AngleXU=0 Radius=1
    g2: Circle CenterX=8 CenterY=6 CenterZ=0 NormalX=0 NormalY=0 NormalZ=1 AngleXU=0 Radius=1
    g3: BSplineCurve PolesCount=3 KnotsCount=2 Degree=2 IsPeriodic=0
    g4: GeomPoint X=0 Y=0 Z=0
    g5: GeomPoint X=8 Y=6 Z=0
    g6: LineSegment StartX=0 StartY=6 StartZ=0 EndX=8 EndY=6 EndZ=0
  constraints (14):
    c: Coincident(g0,g-1)
    c: Distance(g0) = 6
    c: Vertical(g0)
    c: Coincident(g3,g0)
    c: Weight(g1) = 1
    c: Equal(g1,g2)
    c: InternalAlignment(g1,g3)
    c: InternalAlignment(g2,g3)
    c: InternalAlignment(g4,g3)
    c: InternalAlignment(g5,g3)
    c: Block(g3)
    c: Coincident(g6,g0)
    c: Coincident(g6,g3)
    c: Horizontal(g6)
FEATURE [Part::Extrusion] Extrude015  label="caseScrewPillarBracket003"
  Base = -> Sketch021
  Dir = (0,0,1)
  DirMode = 2
  FaceMakerClass = Part::FaceMakerBullseye
  LengthFwd = 2.4
  LengthRev = 0
  Placement = pos=(11.3,29,58.74) rot=(0,1,0;1.5708rad)
  Solid = true
  Symmetric = false
FEATURE [Sketcher::SketchObject] Sketch022
  FullyConstrained = true
  sketch-geometry (7):
    g0: LineSegment StartX=0 StartY=0 StartZ=0 EndX=0 EndY=6 EndZ=0
    g1: Circle CenterX=0 CenterY=0 CenterZ=0 NormalX=0 NormalY=0 NormalZ=1 AngleXU=0 Radius=1
    g2: Circle CenterX=8 CenterY=6 CenterZ=0 NormalX=0 NormalY=0 NormalZ=1 AngleXU=0 Radius=1
    g3: BSplineCurve PolesCount=3 KnotsCount=2 Degree=2 IsPeriodic=0
    g4: GeomPoint X=0 Y=0 Z=0
    g5: GeomPoint X=8 Y=6 Z=0
    g6: LineSegment StartX=0 StartY=6 StartZ=0 EndX=8 EndY=6 EndZ=0
  constraints (14):
    c: Coincident(g0,g-1)
    c: Distance(g0) = 6
    c: Vertical(g0)
    c: Coincident(g3,g0)
    c: Weight(g1) = 1
    c: Equal(g1,g2)
    c: InternalAlignment(g1,g3)
    c: InternalAlignment(g2,g3)
    c: InternalAlignment(g4,g3)
    c: InternalAlignment(g5,g3)
    c: Block(g3)
    c: Coincident(g6,g0)
    c: Coincident(g6,g3)
    c: Horizontal(g6)
FEATURE [Part::Extrusion] Extrude016  label="caseScrewPillarBracket004"
  Base = -> Sketch022
  Dir = (0,0,1)
  DirMode = 2
  FaceMakerClass = Part::FaceMakerBullseye
  LengthFwd = 2.4
  LengthRev = 0
  Placement = pos=(88.3,29,65.23) rot=(0,1,0;1.5708rad)
  Solid = true
  Symmetric = false
FEATURE [Sketcher::SketchObject] Sketch023
  FullyConstrained = true
  sketch-geometry (7):
    g0: LineSegment StartX=0 StartY=0 StartZ=0 EndX=0 EndY=6 EndZ=0
    g1: Circle CenterX=0 CenterY=0 CenterZ=0 NormalX=0 NormalY=0 NormalZ=1 AngleXU=0 Radius=1
    g2: Circle CenterX=8 CenterY=6 CenterZ=0 NormalX=0 NormalY=0 NormalZ=1 AngleXU=0 Radius=1
    g3: BSplineCurve PolesCount=3 KnotsCount=2 Degree=2 IsPeriodic=0
    g4: GeomPoint X=0 Y=0 Z=0
    g5: GeomPoint X=8 Y=6 Z=0
    g6: LineSegment StartX=0 StartY=6 StartZ=0 EndX=8 EndY=6 EndZ=0
  constraints (14):
    c: Coincident(g0,g-1)
    c: Distance(g0) = 6
    c: Vertical(g0)
    c: Coincident(g3,g0)
    c: Weight(g1) = 1
    c: Equal(g1,g2)
    c: InternalAlignment(g1,g3)
    c: InternalAlignment(g2,g3)
    c: InternalAlignment(g4,g3)
    c: InternalAlignment(g5,g3)
    c: Block(g3)
    c: Coincident(g6,g0)
    c: Coincident(g6,g3)
    c: Horizontal(g6)
FEATURE [Part::Extrusion] Extrude017  label="caseScrewPillarBracket005"
  Base = -> Sketch023
  Dir = (0,0,1)
  DirMode = 2
  FaceMakerClass = Part::FaceMakerBullseye
  LengthFwd = 2.4
  LengthRev = 0
  Placement = pos=(90.7,29,6.77) rot=(0,-1,0;1.5708rad)
  Solid = true
  Symmetric = false
FEATURE [Sketcher::SketchObject] Sketch024
  FullyConstrained = true
  sketch-geometry (7):
    g0: LineSegment StartX=0 StartY=0 StartZ=0 EndX=0 EndY=6 EndZ=0
    g1: Circle CenterX=0 CenterY=0 CenterZ=0 NormalX=0 NormalY=0 NormalZ=1 AngleXU=0 Radius=1
    g2: Circle CenterX=8 CenterY=6 CenterZ=0 NormalX=0 NormalY=0 NormalZ=1 AngleXU=0 Radius=1
    g3: BSplineCurve PolesCount=3 KnotsCount=2 Degree=2 IsPeriodic=0
    g4: GeomPoint X=0 Y=0 Z=0
    g5: GeomPoint X=8 Y=6 Z=0
    g6: LineSegment StartX=0 StartY=6 StartZ=0 EndX=8 EndY=6 EndZ=0
  constraints (14):
    c: Coincident(g0,g-1)
    c: Distance(g0) = 6
    c: Vertical(g0)
    c: Coincident(g3,g0)
    c: Weight(g1) = 1
    c: Equal(g1,g2)
    c: InternalAlignment(g1,g3)
    c: InternalAlignment(g2,g3)
    c: InternalAlignment(g4,g3)
    c: InternalAlignment(g5,g3)
    c: Block(g3)
    c: Coincident(g6,g0)
    c: Coincident(g6,g3)
    c: Horizontal(g6)
FEATURE [Part::Extrusion] Extrude018  label="caseScrewPillarBracket006"
  Base = -> Sketch024
  Dir = (0,0,1)
  DirMode = 2
  FaceMakerClass = Part::FaceMakerBullseye
  LengthFwd = 2.4
  LengthRev = 0
  Placement = pos=(103.7,29,6.77) rot=(0,-1,0;1.5708rad)
  Solid = true
  Symmetric = false
FEATURE [Sketcher::SketchObject] Sketch025
  FullyConstrained = true
  sketch-geometry (7):
    g0: LineSegment StartX=0 StartY=0 StartZ=0 EndX=0 EndY=6 EndZ=0
    g1: Circle CenterX=0 CenterY=0 CenterZ=0 NormalX=0 NormalY=0 NormalZ=1 AngleXU=0 Radius=1
    g2: Circle CenterX=8 CenterY=6 CenterZ=0 NormalX=0 NormalY=0 NormalZ=1 AngleXU=0 Radius=1
    g3: BSplineCurve PolesCount=3 KnotsCount=2 Degree=2 IsPeriodic=0
    g4: GeomPoint X=0 Y=0 Z=0
    g5: GeomPoint X=8 Y=6 Z=0
    g6: LineSegment StartX=0 StartY=6 StartZ=0 EndX=8 EndY=6 EndZ=0
  constraints (14):
    c: Coincident(g0,g-1)
    c: Distance(g0) = 6
    c: Vertical(g0)
    c: Coincident(g3,g0)
    c: Weight(g1) = 1
    c: Equal(g1,g2)
    c: InternalAlignment(g1,g3)
    c: InternalAlignment(g2,g3)
    c: InternalAlignment(g4,g3)
    c: InternalAlignment(g5,g3)
    c: Block(g3)
    c: Coincident(g6,g0)
    c: Coincident(g6,g3)
    c: Horizontal(g6)
FEATURE [Part::Extrusion] Extrude019  label="caseScrewPillarBracket007"
  Base = -> Sketch025
  Dir = (0,0,1)
  DirMode = 2
  FaceMakerClass = Part::FaceMakerBullseye
  LengthFwd = 2.4
  LengthRev = 0
  Placement = pos=(101.3,29,65.23) rot=(0,1,0;1.5708rad)
  Solid = true
  Symmetric = false
FEATURE [Part::Box] Box011  label="frontCaseScrewPillarBracket"
  AttacherType = Attacher::AttachEngine3D
  Height = 2.4
  Length = 16
  Placement = pos=(87,28,2.3) rot=(0,0,1;0rad)
  Width = 7
FEATURE [Part::Box] Box012  label="frontCaseScrewPillarBracket001"
  AttacherType = Attacher::AttachEngine3D
  Height = 2.4
  Length = 16
  Placement = pos=(87,28,67.3) rot=(0,0,1;0rad)
  Width = 7
FEATURE [Sketcher::SketchObject] Sketch026
  FullyConstrained = true
  sketch-geometry (17):
    g0: Circle CenterX=-3.5 CenterY=23.5 CenterZ=0 NormalX=0 NormalY=0 NormalZ=1 AngleXU=0 Radius=1
    g1: Circle CenterX=-1 CenterY=15.25 CenterZ=0 NormalX=0 NormalY=0 NormalZ=1 AngleXU=0 Radius=1
    g2: Circle CenterX=-3.5 CenterY=7 CenterZ=0 NormalX=0 NormalY=0 NormalZ=1 AngleXU=0 Radius=1
    g3: BSplineCurve PolesCount=3 KnotsCount=2 Degree=2 IsPeriodic=0
    g4: GeomPoint X=-3.5 Y=23.5 Z=0
    g5: GeomPoint X=-3.5 Y=7 Z=0
    g6: Circle CenterX=-4.8 CenterY=30.5 CenterZ=0 NormalX=0 NormalY=0 NormalZ=1 AngleXU=0 Radius=1
    g7: Circle CenterX=-3.5 CenterY=30.5 CenterZ=0 NormalX=0 NormalY=0 NormalZ=1 AngleXU=0 Radius=1
    g8: Circle CenterX=-3.5 CenterY=29.2 CenterZ=0 NormalX=0 NormalY=0 NormalZ=1 AngleXU=0 Radius=1
    g9: BSplineCurve PolesCount=3 KnotsCount=2 Degree=2 IsPeriodic=0
    g10: GeomPoint X=-4.8 Y=30.5 Z=0
    g11: GeomPoint X=-3.5 Y=29.2 Z=0
    g12: LineSegment StartX=-3.5 StartY=29.2 StartZ=0 EndX=-3.5 EndY=23.5 EndZ=0
    g13: LineSegment StartX=-4.8 StartY=30.5 StartZ=0 EndX=0 EndY=30.5 EndZ=0
    g14: LineSegment StartX=-3.5 StartY=5 StartZ=0 EndX=-3.5 EndY=7 EndZ=0
    g15: LineSegment StartX=0 StartY=5 StartZ=0 EndX=0 EndY=30.5 EndZ=0
    g16: LineSegment StartX=-3.5 StartY=5 StartZ=0 EndX=0 EndY=5 EndZ=0
  constraints (33):
    c: Weight(g0) = 1
    c: Equal(g0,g1)
    c: Equal(g0,g2)
    c: InternalAlignment(g0,g3)
    c: InternalAlignment(g1,g3)
    c: InternalAlignment(g2,g3)
    c: InternalAlignment(g4,g3)
    c: InternalAlignment(g5,g3)
    c: Block(g3)
    c: Weight(g6) = 1
    c: Equal(g6,g7)
    c: Equal(g6,g8)
    c: InternalAlignment(g6,g9)
    c: InternalAlignment(g7,g9)
    c: InternalAlignment(g8,g9)
    c: InternalAlignment(g10,g9)
    c: InternalAlignment(g11,g9)
    c: Block(g9)
    c: Coincident(g12,g9)
    c: Coincident(g12,g3)
    c: Vertical(g12)
    c: Coincident(g13,g9)
    c: Horizontal(g13)
    c: Distance(g13) = 4.8
    c: Coincident(g14,g3)
    c: Vertical(g14)
    c: Coincident(g15,g13)
    c: Vertical(g15)
    c: Tangent(g15,g1)
    c: Distance(g14) = 2
    c: Coincident(g16,g14)
    c: Horizontal(g16)
    c: Coincident(g15,g16)
FEATURE [Part::Feature] Face050
  shape: bbox 4.8 x 25.5 x 2e-07 mm, 1 faces, 0 solids (baked)
FEATURE [Part::Revolution] Revolve054  label="moreFrontCaseScrewPost001"
  Angle = 360
  Axis = (0,1,0)
  Base = (0,0,0)
  FaceMakerClass = Part::FaceMakerBullseye
  Placement = pos=(102.5,4.5,3.5) rot=(0,0,1;0rad)
  Solid = false
  Source = -> Face050
  Symmetric = false
FEATURE [Part::Feature] Face051
  shape: bbox 4.8 x 25.5 x 2e-07 mm, 1 faces, 0 solids (baked)
FEATURE [Part::Revolution] Revolve055  label="moreFrontCaseScrewPost002"
  Angle = 360
  Axis = (0,1,0)
  Base = (0,0,0)
  FaceMakerClass = Part::FaceMakerBullseye
  Placement = pos=(102.5,4.5,68.5) rot=(0,0,1;0rad)
  Solid = false
  Source = -> Face051
  Symmetric = false
FEATURE [Sketcher::SketchObject] Sketch027
  FullyConstrained = true
  sketch-geometry (10):
    g0: LineSegment StartX=-1.6 StartY=4.7 StartZ=0 EndX=-1.6 EndY=1.7 EndZ=0
    g1: LineSegment StartX=-3.5 StartY=4.7 StartZ=0 EndX=-1.6 EndY=4.7 EndZ=0
    g2: LineSegment StartX=-1.6 StartY=1.7 StartZ=0 EndX=-1.6 EndY=1.5 EndZ=0
    g3: LineSegment StartX=-1.6 StartY=1.5 StartZ=0 EndX=-5.2 EndY=1.5 EndZ=0
    g4: Circle CenterX=-3.5 CenterY=4.7 CenterZ=0 NormalX=0 NormalY=0 NormalZ=1 AngleXU=0 Radius=1
    g5: Circle CenterX=-3.59627 CenterY=2.99743 CenterZ=0 NormalX=0 NormalY=0 NormalZ=1 AngleXU=0 Radius=1
    g6: Circle CenterX=-5.2 CenterY=1.5 CenterZ=0 NormalX=0 NormalY=0 NormalZ=1 AngleXU=0 Radius=1
    g7: BSplineCurve PolesCount=3 KnotsCount=2 Degree=2 IsPeriodic=0
    g8: GeomPoint X=-3.5 Y=4.7 Z=0
    g9: GeomPoint X=-5.2 Y=1.5 Z=0
  constraints (23):
    c: Vertical(g0)
    c: Distance(g0) = 3
    c: Coincident(g1,g0)
    c: Horizontal(g1)
    c: Block(g0)
    c: Block(g1)
    c: Coincident(g2,g0)
    c: Vertical(g2)
    c: Distance(g2) = 0.2
    c: Coincident(g3,g2)
    c: Horizontal(g3)
    c: Block(g3)
    c: Coincident(g7,g1)
    c: Weight(g4) = 1
    c: Equal(g4,g5)
    c: Equal(g4,g6)
    c: Coincident(g7,g3)
    c: InternalAlignment(g4,g7)
    c: InternalAlignment(g5,g7)
    c: InternalAlignment(g6,g7)
    c: InternalAlignment(g8,g7)
    c: InternalAlignment(g9,g7)
    c: Block(g7)
FEATURE [Sketcher::SketchObject] Sketch028
  FullyConstrained = true
  sketch-geometry (18):
    g0: LineSegment StartX=0 StartY=3e-16 StartZ=0 EndX=0 EndY=1.7 EndZ=0
    g1: LineSegment StartX=-3.5 StartY=0 StartZ=0 EndX=-3.5 EndY=0.9 EndZ=0
    g2: Circle CenterX=-2.7 CenterY=1.7 CenterZ=0 NormalX=0 NormalY=0 NormalZ=1 AngleXU=0 Radius=1
    g3: Circle CenterX=-3.5 CenterY=1.7 CenterZ=0 NormalX=0 NormalY=0 NormalZ=1 AngleXU=0 Radius=1
    g4: Circle CenterX=-3.5 CenterY=0.9 CenterZ=0 NormalX=0 NormalY=0 NormalZ=1 AngleXU=0 Radius=1
    g5: BSplineCurve PolesCount=3 KnotsCount=2 Degree=2 IsPeriodic=0
    g6: GeomPoint X=-2.7 Y=1.7 Z=0
    g7: GeomPoint X=-3.5 Y=0.9 Z=0
    g8: LineSegment StartX=-3.5 StartY=0 StartZ=0 EndX=-3.5 EndY=-7 EndZ=0
    g9: LineSegment StartX=0 StartY=3e-16 StartZ=0 EndX=0 EndY=-7 EndZ=0
    g10: LineSegment StartX=-3.5 StartY=-7 StartZ=0 EndX=0 EndY=-7 EndZ=0
    g11: LineSegment StartX=-2.7 StartY=1.7 StartZ=0 EndX=-1.6 EndY=1.7 EndZ=0
    g12: LineSegment StartX=0 StartY=1.7 StartZ=0 EndX=0 EndY=4.5 EndZ=0
    g13: LineSegment StartX=0 StartY=4.5 StartZ=0 EndX=0 EndY=10.8 EndZ=0
    g14: LineSegment StartX=0 StartY=10.8 StartZ=0 EndX=-2 EndY=10.8 EndZ=0
    g15: LineSegment StartX=-1.6 StartY=4.7 StartZ=0 EndX=-1.6 EndY=1.7 EndZ=0
    g16: LineSegment StartX=-1.6 StartY=4.7 StartZ=0 EndX=-2 EndY=4.7 EndZ=0
    g17: LineSegment StartX=-2 StartY=4.7 StartZ=0 EndX=-2 EndY=10.8 EndZ=0
  constraints (44):
    c: Vertical(g0)
    c: Vertical(g1)
    c: Distance(g1) = 0.9
    c: Block(g0)
    c: Distance(g0) = 1.7
    c: Weight(g2) = 1
    c: Equal(g2,g3)
    c: Equal(g2,g4)
    c: Coincident(g5,g1)
    c: InternalAlignment(g2,g5)
    c: InternalAlignment(g3,g5)
    c: InternalAlignment(g4,g5)
    c: InternalAlignment(g6,g5)
    c: InternalAlignment(g7,g5)
    c: Block(g5)
    c: Coincident(g8,g1)
    c: Vertical(g8)
    c: Distance(g8) = 7
    c: Vertical(g9)
    c: Equal(g8,g9) = 7
    c: Coincident(g9,g0)
    c: Coincident(g10,g8)
    c: Coincident(g10,g9)
    c: Horizontal(g10)
    c: Coincident(g11,g5)
    c: Horizontal(g11)
    c: Coincident(g12,g0)
    c: Vertical(g12)
    c: Distance(g12) = 2.8
    c: Coincident(g13,g12)
    c: Vertical(g13)
    c: Distance(g13) = 6.3
    c: Coincident(g14,g13)
    c: Horizontal(g14)
    c: Distance(g14) = 2
    c: Vertical(g15)
    c: Distance(g15) = 3
    c: Block(g11)
    c: Coincident(g15,g11)
    c: Coincident(g16,g15)
    c: Horizontal(g16)
    c: Coincident(g17,g16)
    c: Coincident(g17,g14)
    c: Vertical(g17)
FEATURE [Part::Revolution] Revolve040  label="backCaseScrewRetainer001"
  Angle = 360
  Axis = (0,1,0)
  Base = (0,0,0)
  FaceMakerClass = Part::FaceMakerBullseye
  Placement = pos=(12.5,3,10) rot=(0,0,1;0rad)
  Solid = false
  Source = -> Face036
  Symmetric = false
FEATURE [Part::Feature] Face055
  shape: bbox 3.5 x 30.2 x 2e-07 mm, 1 faces, 0 solids (baked)
FEATURE [Part::Revolution] Revolve059  label="backCaseScrewPost"
  Angle = 360
  Axis = (0,1,0)
  Base = (0,0,0)
  FaceMakerClass = Part::FaceMakerBullseye
  Placement = pos=(12.5,4.5,10) rot=(0,0,1;0rad)
  Solid = false
  Source = -> Face055
  Symmetric = false
FEATURE [Part::Feature] Face056
  shape: bbox 3.5 x 30.2 x 2e-07 mm, 1 faces, 0 solids (baked)
FEATURE [Part::Revolution] Revolve060  label="backCaseScrewPost001"
  Angle = 360
  Axis = (0,1,0)
  Base = (0,0,0)
  FaceMakerClass = Part::FaceMakerBullseye
  Placement = pos=(12.5,4.5,62) rot=(0,0,1;0rad)
  Solid = false
  Source = -> Face056
  Symmetric = false
FEATURE [Part::Feature] Face057
  shape: bbox 3.5 x 17.8 x 2e-07 mm, 1 faces, 0 solids (baked)
FEATURE [Part::Revolution] Revolve061  label="removeToCreateScrewAndThreadedInsertHole"
  Angle = 360
  Axis = (0,1,0)
  Base = (0,0,0)
  FaceMakerClass = Part::FaceMakerBullseye
  Placement = pos=(12.5,0,10) rot=(0,0,1;0rad)
  Solid = false
  Source = -> Face057
  Symmetric = false
FEATURE [Part::Feature] Face058
  shape: bbox 3.5 x 17.8 x 2e-07 mm, 1 faces, 0 solids (baked)
FEATURE [Part::Revolution] Revolve062  label="removeToCreateScrewAndThreadedInsertHole001"
  Angle = 360
  Axis = (0,1,0)
  Base = (0,0,0)
  FaceMakerClass = Part::FaceMakerBullseye
  Placement = pos=(12.5,0,62) rot=(0,0,1;0rad)
  Solid = false
  Source = -> Face058
  Symmetric = false
FEATURE [Part::Feature] Face059
  shape: bbox 3.5 x 17.8 x 2e-07 mm, 1 faces, 0 solids (baked)
FEATURE [Part::Revolution] Revolve063  label="removeToCreateScrewAndThreadedInsertHole002"
  Angle = 360
  Axis = (0,1,0)
  Base = (0,0,0)
  FaceMakerClass = Part::FaceMakerBullseye
  Placement = pos=(89.5,0,68.5) rot=(0,0,1;0rad)
  Solid = false
  Source = -> Face059
  Symmetric = false
FEATURE [Part::Feature] Face060
  shape: bbox 3.5 x 17.8 x 2e-07 mm, 1 faces, 0 solids (baked)
FEATURE [Part::Revolution] Revolve064  label="removeToCreateScrewAndThreadedInsertHole003"
  Angle = 360
  Axis = (0,1,0)
  Base = (0,0,0)
  FaceMakerClass = Part::FaceMakerBullseye
  Placement = pos=(89.5,0,3.5) rot=(0,0,1;0rad)
  Solid = false
  Source = -> Face060
  Symmetric = false
FEATURE [Part::Feature] Face061
  shape: bbox 3.5 x 17.8 x 2e-07 mm, 1 faces, 0 solids (baked)
FEATURE [Part::Revolution] Revolve065  label="removeToCreateScrewAndThreadedInsertHole004"
  Angle = 360
  Axis = (0,1,0)
  Base = (0,0,0)
  FaceMakerClass = Part::FaceMakerBullseye
  Placement = pos=(102.5,4.7,3.5) rot=(0,0,1;0rad)
  Solid = false
  Source = -> Face061
  Symmetric = false
FEATURE [Part::Feature] Face062
  shape: bbox 3.5 x 17.8 x 2e-07 mm, 1 faces, 0 solids (baked)
FEATURE [Part::Revolution] Revolve066  label="removeToCreateScrewAndThreadedInsertHole005"
  Angle = 360
  Axis = (0,1,0)
  Base = (0,0,0)
  FaceMakerClass = Part::FaceMakerBullseye
  Placement = pos=(102.5,4.7,68.5) rot=(0,0,1;0rad)
  Solid = false
  Source = -> Face062
  Symmetric = false
FEATURE [Part::MultiFuse] Fusion047  label="makeHoles"
  Shapes = -> [Revolve066,Revolve065,Revolve064,Revolve063,Revolve062,Revolve061]
FEATURE [Part::Feature] Face063
  shape: bbox 3.6 x 3.2 x 2e-07 mm, 1 faces, 0 solids (baked)
FEATURE [Part::Revolution] Revolve067  label="moreFrontCaseScrewRetainer002"
  Angle = 360
  Axis = (0,1,0)
  Base = (0,0,0)
  FaceMakerClass = Part::FaceMakerBullseye
  Placement = pos=(102.5,4.5,68.5) rot=(0,0,1;0rad)
  Solid = false
  Source = -> Face063
  Symmetric = false
FEATURE [Part::Feature] Face064
  shape: bbox 3.6 x 3.2 x 2e-07 mm, 1 faces, 0 solids (baked)
FEATURE [Part::Revolution] Revolve068  label="moreFrontCaseScrewRetainer003"
  Angle = 360
  Axis = (0,1,0)
  Base = (0,0,0)
  FaceMakerClass = Part::FaceMakerBullseye
  Placement = pos=(102.5,4.5,3.5) rot=(0,0,1;0rad)
  Solid = false
  Source = -> Face064
  Symmetric = false
FEATURE [Part::Feature] Face065
  shape: bbox 3.5 x 17.8 x 2e-07 mm, 1 faces, 0 solids (baked)
FEATURE [Part::Revolution] Revolve069  label="removeToCreateScrewAndThreadedInsertHole006"
  Angle = 360
  Axis = (0,1,0)
  Base = (0,0,0)
  FaceMakerClass = Part::FaceMakerBullseye
  Placement = pos=(12.5,0,10) rot=(0,0,1;0rad)
  Solid = false
  Source = -> Face065
  Symmetric = false
FEATURE [Part::Feature] Face066
  shape: bbox 3.5 x 17.8 x 2e-07 mm, 1 faces, 0 solids (baked)
FEATURE [Part::Revolution] Revolve070  label="removeToCreateScrewAndThreadedInsertHole007"
  Angle = 360
  Axis = (0,1,0)
  Base = (0,0,0)
  FaceMakerClass = Part::FaceMakerBullseye
  Placement = pos=(12.5,0,62) rot=(0,0,1;0rad)
  Solid = false
  Source = -> Face066
  Symmetric = false
FEATURE [Part::Feature] Face067
  shape: bbox 3.5 x 17.8 x 2e-07 mm, 1 faces, 0 solids (baked)
FEATURE [Part::Revolution] Revolve071  label="removeToCreateScrewAndThreadedInsertHole008"
  Angle = 360
  Axis = (0,1,0)
  Base = (0,0,0)
  FaceMakerClass = Part::FaceMakerBullseye
  Placement = pos=(89.5,0,68.5) rot=(0,0,1;0rad)
  Solid = false
  Source = -> Face067
  Symmetric = false
FEATURE [Part::Feature] Face068
  shape: bbox 3.5 x 17.8 x 2e-07 mm, 1 faces, 0 solids (baked)
FEATURE [Part::Revolution] Revolve072  label="removeToCreateScrewAndThreadedInsertHole009"
  Angle = 360
  Axis = (0,1,0)
  Base = (0,0,0)
  FaceMakerClass = Part::FaceMakerBullseye
  Placement = pos=(89.5,0,3.5) rot=(0,0,1;0rad)
  Solid = false
  Source = -> Face068
  Symmetric = false
FEATURE [Part::Feature] Face069
  shape: bbox 3.5 x 17.8 x 2e-07 mm, 1 faces, 0 solids (baked)
FEATURE [Part::Feature] Face070
  shape: bbox 3.5 x 17.8 x 2e-07 mm, 1 faces, 0 solids (baked)
FEATURE [Part::Revolution] Revolve073  label="removeToCreateScrewAndThreadedInsertHole010"
  Angle = 360
  Axis = (0,1,0)
  Base = (0,0,0)
  FaceMakerClass = Part::FaceMakerBullseye
  Placement = pos=(102.5,4.7,3.5) rot=(0,0,1;0rad)
  Solid = false
  Source = -> Face069
  Symmetric = false
FEATURE [Part::Revolution] Revolve074  label="removeToCreateScrewAndThreadedInsertHole011"
  Angle = 360
  Axis = (0,1,0)
  Base = (0,0,0)
  FaceMakerClass = Part::FaceMakerBullseye
  Placement = pos=(102.5,4.7,68.5) rot=(0,0,1;0rad)
  Solid = false
  Source = -> Face070
  Symmetric = false
FEATURE [Part::MultiFuse] Fusion048  label="makeHoles001"
  Shapes = -> [Revolve074,Revolve073,Revolve072,Revolve071,Revolve070,Revolve069]
FEATURE [Part::MultiFuse] Fusion049  label="caseScrewRetainers"
  Shapes = -> [Revolve067,Revolve068,Revolve048,Revolve047,Revolve039,Revolve040]
FEATURE [Part::Cut] Cut015  label="caseScrewRetainers001"
  Base = -> Fusion049
  Tool = -> Fusion048
FEATURE [Part::MultiFuse] Fusion050  label="casePillars"
  Shapes = -> [Revolve055,Revolve054,Revolve043,Revolve046,Revolve059,Revolve060]
FEATURE [Part::Feature] Face071 .. Face076  x6 (patterned run collapsed; names and placements below)
  shape: bbox 3.5 x 17.8 x 2e-07 mm, 1 faces, 0 solids (baked)
FEATURE [Part::Revolution] Revolve075  label="removeToCreateScrewAndThreadedInsertHole012"
  Angle = 360
  Axis = (0,1,0)
  Base = (0,0,0)
  FaceMakerClass = Part::FaceMakerBullseye
  Placement = pos=(12.5,0,10) rot=(0,0,1;0rad)
  Solid = false
  Source = -> Face071
  Symmetric = false
FEATURE [Part::Revolution] Revolve076  label="removeToCreateScrewAndThreadedInsertHole013"
  Angle = 360
  Axis = (0,1,0)
  Base = (0,0,0)
  FaceMakerClass = Part::FaceMakerBullseye
  Placement = pos=(12.5,0,62) rot=(0,0,1;0rad)
  Solid = false
  Source = -> Face072
  Symmetric = false
FEATURE [Part::Revolution] Revolve077  label="removeToCreateScrewAndThreadedInsertHole014"
  Angle = 360
  Axis = (0,1,0)
  Base = (0,0,0)
  FaceMakerClass = Part::FaceMakerBullseye
  Placement = pos=(89.5,0,68.5) rot=(0,0,1;0rad)
  Solid = false
  Source = -> Face073
  Symmetric = false
FEATURE [Part::Revolution] Revolve078  label="removeToCreateScrewAndThreadedInsertHole015"
  Angle = 360
  Axis = (0,1,0)
  Base = (0,0,0)
  FaceMakerClass = Part::FaceMakerBullseye
  Placement = pos=(89.5,0,3.5) rot=(0,0,1;0rad)
  Solid = false
  Source = -> Face074
  Symmetric = false
FEATURE [Part::Revolution] Revolve079  label="removeToCreateScrewAndThreadedInsertHole016"
  Angle = 360
  Axis = (0,1,0)
  Base = (0,0,0)
  FaceMakerClass = Part::FaceMakerBullseye
  Placement = pos=(102.5,4.7,3.5) rot=(0,0,1;0rad)
  Solid = false
  Source = -> Face075
  Symmetric = false
FEATURE [Part::Revolution] Revolve080  label="removeToCreateScrewAndThreadedInsertHole017"
  Angle = 360
  Axis = (0,1,0)
  Base = (0,0,0)
  FaceMakerClass = Part::FaceMakerBullseye
  Placement = pos=(102.5,4.7,68.5) rot=(0,0,1;0rad)
  Solid = false
  Source = -> Face076
  Symmetric = false
FEATURE [Part::MultiFuse] Fusion051  label="makeHoles002"
  Shapes = -> [Revolve080,Revolve079,Revolve078,Revolve077,Revolve076,Revolve075]
FEATURE [Part::Cut] Cut016  label="caesPillars"
  Base = -> Fusion050
  Tool = -> Fusion051
FEATURE [Part::Revolution] Revolve009  label="plugHousing016"
  Angle = 360
  Axis = (0,1,0)
  Base = (0,0,0)
  FaceMakerClass = Part::FaceMakerBullseye
  Placement = pos=(0,0,36.15) rot=(0,0,1;0rad)
  Solid = false
  Source = -> Face012
  Symmetric = false
FEATURE [Part::MultiFuse] Fusion014  label="plugHousing023"
  Placement = pos=(0,0,0) rot=(0,0,1;1.5708rad)
  Shapes = -> [Revolve011,Revolve009]
FEATURE [Part::Revolution] Revolve010  label="plugHousing017"
  Angle = 360
  Axis = (0,1,0)
  Base = (0,0,0)
  FaceMakerClass = Part::FaceMakerBullseye
  Placement = pos=(0,0,36.15) rot=(0,0,1;0rad)
  Solid = false
  Source = -> Face014
  Symmetric = false
FEATURE [Part::MultiFuse] Fusion015  label="plugHousing024"
  Placement = pos=(0,0,0) rot=(0,0,1;1.5708rad)
  Shapes = -> [Revolve010,Revolve015]
FEATURE [Part::Revolution] Revolve014  label="plugHousing026"
  Angle = 360
  Axis = (0,1,0)
  Base = (0,0,0)
  FaceMakerClass = Part::FaceMakerBullseye
  Placement = pos=(0,0,36.15) rot=(0,0,1;0rad)
  Solid = false
  Source = -> Face011
  Symmetric = false
FEATURE [Part::Revolution] Revolve013  label="plugHousing025"
  Angle = 360
  Axis = (0,1,0)
  Base = (0,0,0)
  FaceMakerClass = Part::FaceMakerBullseye
  Placement = pos=(0,0,36.15) rot=(0,0,1;0rad)
  Solid = false
  Source = -> Face015
  Symmetric = false
FEATURE [Part::MultiFuse] Fusion016  label="plugHousing028"
  Placement = pos=(0,19,0) rot=(0,0,1;3.14159rad)
  Shapes = -> [Fusion014,Fusion013]
FEATURE [Part::MultiFuse] Fusion011  label="plugHousing018"
  Placement = pos=(0,0,0) rot=(0,0,1;1.5708rad)
  Shapes = -> [Revolve014,Revolve013]
FEATURE [Part::MultiFuse] Fusion012  label="plugHousing019"
  Placement = pos=(0,19,0) rot=(0,0,1;3.14159rad)
  Shapes = -> [Fusion011,Fusion015]
FEATURE [Part::MultiFuse] Fusion017  label="plugHousing029"
  Placement = pos=(122.621,0,-0.15) rot=(0,0,1;0rad)
  Shapes = -> [Fusion016,Fusion012]
FEATURE [Part::MultiFuse] Fusion052  label="casePillarRetainers"
  Shapes = -> [Extrude012,Extrude013,Extrude014,Extrude015,Extrude016,Extrude017,Extrude018,Extrude019,Box011,Box012]
FEATURE [Part::Feature] Face077
  shape: bbox 3.5 x 17.8 x 2e-07 mm, 1 faces, 0 solids (baked)
FEATURE [Part::Revolution] Revolve081  label="removeToCreateScrewAndThreadedInsertHole018"
  Angle = 360
  Axis = (0,1,0)
  Base = (0,0,0)
  FaceMakerClass = Part::FaceMakerBullseye
  Placement = pos=(62.3,30.3,19.7) rot=(0,0,1;0rad)
  Solid = false
  Source = -> Face077
  Symmetric = false
FEATURE [Part::Feature] Face078
  shape: bbox 3.5 x 17.8 x 2e-07 mm, 1 faces, 0 solids (baked)
FEATURE [Part::Revolution] Revolve082  label="removeToCreateScrewAndThreadedInsertHole019"
  Angle = 360
  Axis = (0,1,0)
  Base = (0,0,0)
  FaceMakerClass = Part::FaceMakerBullseye
  Placement = pos=(62.3,30.3,51.7) rot=(0,0,1;0rad)
  Solid = false
  Source = -> Face078
  Symmetric = false
FEATURE [Part::Feature] Face079
  shape: bbox 3.5 x 17.8 x 2e-07 mm, 1 faces, 0 solids (baked)
FEATURE [Part::Revolution] Revolve083  label="removeToCreateScrewAndThreadedInsertHole020"
  Angle = 360
  Axis = (0,1,0)
  Base = (0,0,0)
  FaceMakerClass = Part::FaceMakerBullseye
  Placement = pos=(30.3,30.3,19.7) rot=(0,0,1;0rad)
  Solid = false
  Source = -> Face079
  Symmetric = false
FEATURE [Part::Feature] Face080
  shape: bbox 3.5 x 17.8 x 2e-07 mm, 1 faces, 0 solids (baked)
FEATURE [Part::Revolution] Revolve084  label="removeToCreateScrewAndThreadedInsertHole021"
  Angle = 360
  Axis = (0,1,0)
  Base = (0,0,0)
  FaceMakerClass = Part::FaceMakerBullseye
  Placement = pos=(30.3,30.3,51.7) rot=(0,0,1;0rad)
  Solid = false
  Source = -> Face080
  Symmetric = false
FEATURE [Part::MultiFuse] Fusion053  label="createThreadedInsertHolesForFan"
  Shapes = -> [Revolve081,Revolve082,Revolve083,Revolve084]
FEATURE [Part::Cut] Cut017  label="fanScrewHousing001"
  Base = -> Fusion046
  Tool = -> Fusion053
FEATURE [Part::Feature] Face081
  shape: bbox 3.5 x 17.8 x 2e-07 mm, 1 faces, 0 solids (baked)
FEATURE [Part::Revolution] Revolve085  label="removeToCreateScrewAndThreadedInsertHole022"
  Angle = 360
  Axis = (0,1,0)
  Base = (0,0,0)
  FaceMakerClass = Part::FaceMakerBullseye
  Placement = pos=(62.3,30.3,19.7) rot=(0,0,1;0rad)
  Solid = false
  Source = -> Face081
  Symmetric = false
FEATURE [Part::Feature] Face082
  shape: bbox 3.5 x 17.8 x 2e-07 mm, 1 faces, 0 solids (baked)
FEATURE [Part::Revolution] Revolve086  label="removeToCreateScrewAndThreadedInsertHole023"
  Angle = 360
  Axis = (0,1,0)
  Base = (0,0,0)
  FaceMakerClass = Part::FaceMakerBullseye
  Placement = pos=(62.3,30.3,51.7) rot=(0,0,1;0rad)
  Solid = false
  Source = -> Face082
  Symmetric = false
FEATURE [Part::Feature] Face083
  shape: bbox 3.5 x 17.8 x 2e-07 mm, 1 faces, 0 solids (baked)
FEATURE [Part::Revolution] Revolve087  label="removeToCreateScrewAndThreadedInsertHole024"
  Angle = 360
  Axis = (0,1,0)
  Base = (0,0,0)
  FaceMakerClass = Part::FaceMakerBullseye
  Placement = pos=(30.3,30.3,19.7) rot=(0,0,1;0rad)
  Solid = false
  Source = -> Face083
  Symmetric = false
FEATURE [Part::Feature] Face084
  shape: bbox 3.5 x 17.8 x 2e-07 mm, 1 faces, 0 solids (baked)
FEATURE [Part::Revolution] Revolve088  label="removeToCreateScrewAndThreadedInsertHole025"
  Angle = 360
  Axis = (0,1,0)
  Base = (0,0,0)
  FaceMakerClass = Part::FaceMakerBullseye
  Placement = pos=(30.3,30.3,51.7) rot=(0,0,1;0rad)
  Solid = false
  Source = -> Face084
  Symmetric = false
FEATURE [Part::MultiFuse] Fusion054  label="createThreadedInsertHolesForFan001"
  Shapes = -> [Revolve085,Revolve086,Revolve087,Revolve088]
FEATURE [Part::Cut] Cut018  label="top007"
  Base = -> Fusion040
  Tool = -> Fusion054
FEATURE [Sketcher::SketchObject] Sketch029
  FullyConstrained = false
  Placement = pos=(0,0,0) rot=(1,0,0;1.5708rad)
  sketch-geometry (24):
    g0: ArcOfCircle CenterX=-4 CenterY=-10.5 CenterZ=0 NormalX=0 NormalY=0 NormalZ=1 AngleXU=0 Radius=1.5 StartAngle=6e-16 EndAngle=3.14159
    g1: ArcOfCircle CenterX=-34.2 CenterY=-10.5 CenterZ=0 NormalX=0 NormalY=0 NormalZ=1 AngleXU=0 Radius=1.5 StartAngle=0 EndAngle=3.14159
    g2: ArcOfCircle CenterX=-34.2 CenterY=-27.7 CenterZ=0 NormalX=0 NormalY=0 NormalZ=1 AngleXU=0 Radius=1.5 StartAngle=3.14159 EndAngle=6.28319
    g3: ArcOfCircle CenterX=-4 CenterY=-27.7 CenterZ=0 NormalX=0 NormalY=0 NormalZ=1 AngleXU=0 Radius=1.5 StartAngle=3.1416 EndAngle=6.28319
    g4: ArcOfCircle CenterX=-10 CenterY=-4.3 CenterZ=0 NormalX=0 NormalY=0 NormalZ=1 AngleXU=0 Radius=1.5 StartAngle=2e-16 EndAngle=3.14159
    g5: ArcOfCircle CenterX=-16.1 CenterY=-1.8 CenterZ=0 NormalX=0 NormalY=0 NormalZ=1 AngleXU=0 Radius=1.5 StartAngle=5e-16 EndAngle=3.14159
    g6: ArcOfCircle CenterX=-22.1 CenterY=-1.8 CenterZ=0 NormalX=0 NormalY=0 NormalZ=1 AngleXU=0 Radius=1.5 StartAngle=5e-16 EndAngle=3.14159
    g7: ArcOfCircle CenterX=-28.2 CenterY=-4.3 CenterZ=0 NormalX=0 NormalY=0 NormalZ=1 AngleXU=0 Radius=1.5 StartAngle=2e-16 EndAngle=3.14159
    g8: ArcOfCircle CenterX=-10 CenterY=-33.9 CenterZ=0 NormalX=0 NormalY=0 NormalZ=1 AngleXU=0 Radius=1.5 StartAngle=3.14159 EndAngle=6.28319
    g9: ArcOfCircle CenterX=-16.1 CenterY=-36.4 CenterZ=0 NormalX=0 NormalY=0 NormalZ=1 AngleXU=0 Radius=1.5 StartAngle=3.14159 EndAngle=6.28319
    g10: ArcOfCircle CenterX=-22.1 CenterY=-36.4 CenterZ=0 NormalX=0 NormalY=0 NormalZ=1 AngleXU=0 Radius=1.5 StartAngle=3.14159 EndAngle=6.28319
    g11: ArcOfCircle CenterX=-28.2 CenterY=-33.9 CenterZ=0 NormalX=0 NormalY=0 NormalZ=1 AngleXU=0 Radius=1.5 StartAngle=3.14159 EndAngle=6.28319
    g12: LineSegment StartX=-35.7 StartY=-10.5 StartZ=0 EndX=-35.7 EndY=-27.7 EndZ=0
    g13: LineSegment StartX=-32.7 StartY=-10.5 StartZ=0 EndX=-32.7 EndY=-27.7 EndZ=0
    g14: LineSegment StartX=-29.7 StartY=-33.9 StartZ=0 EndX=-29.7 EndY=-4.3 EndZ=0
    g15: LineSegment StartX=-26.7 StartY=-33.9 StartZ=0 EndX=-26.7 EndY=-4.3 EndZ=0
    g16: LineSegment StartX=-2.5 StartY=-10.5 StartZ=0 EndX=-2.5 EndY=-27.7 EndZ=0
    g17: LineSegment StartX=-8.5 StartY=-4.3 StartZ=0 EndX=-8.5 EndY=-33.9 EndZ=0
    g18: LineSegment StartX=-5.5 StartY=-10.5 StartZ=0 EndX=-5.5 EndY=-27.7 EndZ=0
    g19: LineSegment StartX=-11.5 StartY=-4.3 StartZ=0 EndX=-11.5 EndY=-33.9 EndZ=0
    g20: LineSegment StartX=-14.6 StartY=-1.8 StartZ=0 EndX=-14.6 EndY=-36.4 EndZ=0
    g21: LineSegment StartX=-17.6 StartY=-1.8 StartZ=0 EndX=-17.6 EndY=-36.4 EndZ=0
    g22: LineSegment StartX=-20.6 StartY=-36.4 StartZ=0 EndX=-20.6 EndY=-1.8 EndZ=0
    g23: LineSegment StartX=-23.6 StartY=-1.8 StartZ=0 EndX=-23.6 EndY=-36.4 EndZ=0
  constraints (48):
    c: Block(g0)
    c: Block(g1)
    c: Block(g2)
    c: Block(g3)
    c: Block(g4)
    c: Block(g5)
    c: Block(g6)
    c: Block(g7)
    c: Block(g8)
    c: Block(g9)
    c: Block(g10)
    c: Block(g11)
    c: Coincident(g12,g1)
    c: Coincident(g12,g2)
    c: Vertical(g12)
    c: Coincident(g13,g1)
    c: Coincident(g13,g2)
    c: Vertical(g13)
    c: Coincident(g14,g11)
    c: Coincident(g14,g7)
    c: Vertical(g14)
    c: Coincident(g15,g11)
    c: Coincident(g15,g7)
    c: Vertical(g15)
    c: Coincident(g16,g0)
    c: Coincident(g16,g3)
    c: Vertical(g16)
    c: Coincident(g17,g4)
    c: Coincident(g17,g8)
    c: Vertical(g17)
    c: Coincident(g18,g0)
    c: Coincident(g18,g3)
    c: Vertical(g18)
    c: Coincident(g19,g4)
    c: Coincident(g19,g8)
    c: Vertical(g19)
    c: Coincident(g20,g5)
    c: Coincident(g20,g9)
    c: Vertical(g20)
    c: Coincident(g21,g5)
    c: Coincident(g21,g9)
    c: Vertical(g21)
    c: Coincident(g22,g10)
    c: Coincident(g22,g6)
    c: Vertical(g22)
    c: Coincident(g23,g6)
    c: Coincident(g23,g10)
    c: Vertical(g23)
FEATURE [Part::Extrusion] Extrude020  label="removeToCreateFanGrillHoles"
  Base = -> Sketch029
  Dir = (0,-1,6e-16)
  DirMode = 2
  FaceMakerClass = Part::FaceMakerBullseye
  LengthFwd = 10
  LengthRev = 0
  Placement = pos=(65.4,44,54.82) rot=(0,0,1;0rad)
  Solid = true
  Symmetric = false
FEATURE [Part::MultiFuse] Fusion055  label="top008"
  Shapes = -> [Cut017,Cut018]
FEATURE [Part::Cut] Cut019  label="top009"
  Base = -> Fusion055
  Tool = -> Extrude020
FEATURE [App::MeasureDistance] Distance003  label="Distance: 71.95 mm"
  Distance = 71.9513
  P1 = (117,38,72)
  P2 = (117,38,0.0487319)
FEATURE [Sketcher::SketchObject] Sketch030
  FullyConstrained = true
  Placement = pos=(117,19,0) rot=(0.57735,0.57735,0.57735;2.0944rad)
  sketch-geometry (48):
    g0: LineSegment StartX=-49.19 StartY=69.25 StartZ=0 EndX=-49.19 EndY=66.25 EndZ=0
    g1: LineSegment StartX=-49.19 StartY=63.5 StartZ=0 EndX=-49.19 EndY=60.5 EndZ=0
    g2: LineSegment StartX=-49.19 StartY=57.75 StartZ=0 EndX=-49.19 EndY=54.75 EndZ=0
    g3: LineSegment StartX=-49.19 StartY=52 StartZ=0 EndX=-49.19 EndY=49 EndZ=0
    g4: LineSegment StartX=-49.19 StartY=46.25 StartZ=0 EndX=-49.19 EndY=43.25 EndZ=0
    g5: LineSegment StartX=-49.19 StartY=40.5 StartZ=0 EndX=-49.19 EndY=37.5 EndZ=0
    g6: LineSegment StartX=-49.19 StartY=34.5 StartZ=0 EndX=-49.19 EndY=31.5 EndZ=0
    g7: LineSegment StartX=-49.19 StartY=28.75 StartZ=0 EndX=-49.19 EndY=25.75 EndZ=0
    g8: LineSegment StartX=-49.19 StartY=23 StartZ=0 EndX=-49.19 EndY=20 EndZ=0
    g9: LineSegment StartX=-49.19 StartY=17.25 StartZ=0 EndX=-49.19 EndY=14.25 EndZ=0
    g10: LineSegment StartX=-49.19 StartY=11.5 StartZ=0 EndX=-49.19 EndY=8.5 EndZ=0
    g11: LineSegment StartX=-49.19 StartY=5.75 StartZ=0 EndX=-49.19 EndY=2.75 EndZ=0
    g12: ArcOfCircle CenterX=-1.5 CenterY=67.75 CenterZ=0 NormalX=0 NormalY=0 NormalZ=1 AngleXU=0 Radius=1.5 StartAngle=4.71239 EndAngle=7.85398
    g13: ArcOfCircle CenterX=-1.5 CenterY=62 CenterZ=0 NormalX=0 NormalY=0 NormalZ=1 AngleXU=0 Radius=1.5 StartAngle=4.71239 EndAngle=7.85398
    g14: ArcOfCircle CenterX=-1.5 CenterY=56.25 CenterZ=0 NormalX=0 NormalY=0 NormalZ=1 AngleXU=0 Radius=1.5 StartAngle=4.71239 EndAngle=7.85398
    g15: ArcOfCircle CenterX=-11.49 CenterY=50.5 CenterZ=0 NormalX=0 NormalY=0 NormalZ=1 AngleXU=0 Radius=1.5 StartAngle=4.71239 EndAngle=7.85398
    g16: ArcOfCircle CenterX=-16.28 CenterY=44.75 CenterZ=0 NormalX=0 NormalY=0 NormalZ=1 AngleXU=0 Radius=1.5 StartAngle=4.71239 EndAngle=7.85398
    g17: ArcOfCircle CenterX=-18.2337 CenterY=39 CenterZ=0 NormalX=0 NormalY=0 NormalZ=1 AngleXU=0 Radius=1.5 StartAngle=4.71485 EndAngle=7.85398
    g18: ArcOfCircle CenterX=-16.2837 CenterY=27.25 CenterZ=0 NormalX=0 NormalY=0 NormalZ=1 AngleXU=0 Radius=1.5 StartAngle=4.71485 EndAngle=7.85398
    g19: ArcOfCircle CenterX=-18.2337 CenterY=33 CenterZ=0 NormalX=0 NormalY=0 NormalZ=1 AngleXU=0 Radius=1.5 StartAngle=4.71485 EndAngle=7.85398
    g20: ArcOfCircle CenterX=-11.49 CenterY=21.5 CenterZ=0 NormalX=0 NormalY=0 NormalZ=1 AngleXU=0 Radius=1.5 StartAngle=4.71239 EndAngle=7.85398
    g21: ArcOfCircle CenterX=-1.5 CenterY=4.25 CenterZ=0 NormalX=0 NormalY=0 NormalZ=1 AngleXU=0 Radius=1.5 StartAngle=4.71239 EndAngle=7.85398
    g22: ArcOfCircle CenterX=-1.5 CenterY=10 CenterZ=0 NormalX=0 NormalY=0 NormalZ=1 AngleXU=0 Radius=1.5 StartAngle=4.71239 EndAngle=7.85398
    g23: ArcOfCircle CenterX=-1.5 CenterY=15.75 CenterZ=0 NormalX=0 NormalY=0 NormalZ=1 AngleXU=0 Radius=1.5 StartAngle=4.71239 EndAngle=7.85398
    g24: LineSegment StartX=-49.19 StartY=69.25 StartZ=0 EndX=-1.5 EndY=69.25 EndZ=0
    g25: LineSegment StartX=-49.19 StartY=66.25 StartZ=0 EndX=-1.5 EndY=66.25 EndZ=0
    g26: LineSegment StartX=-49.19 StartY=63.5 StartZ=0 EndX=-1.5 EndY=63.5 EndZ=0
    g27: LineSegment StartX=-49.19 StartY=60.5 StartZ=0 EndX=-1.5 EndY=60.5 EndZ=0
    g28: LineSegment StartX=-49.19 StartY=57.75 StartZ=0 EndX=-1.5 EndY=57.75 EndZ=0
    g29: LineSegment StartX=-49.19 StartY=54.75 StartZ=0 EndX=-1.5 EndY=54.75 EndZ=0
    g30: LineSegment StartX=-49.19 StartY=52 StartZ=0 EndX=-11.49 EndY=52 EndZ=0
    g31: LineSegment StartX=-49.19 StartY=49 StartZ=0 EndX=-11.49 EndY=49 EndZ=0
    g32: LineSegment StartX=-49.19 StartY=46.25 StartZ=0 EndX=-16.28 EndY=46.25 EndZ=0
    g33: LineSegment StartX=-49.19 StartY=43.25 StartZ=0 EndX=-16.28 EndY=43.25 EndZ=0
    g34: LineSegment StartX=-49.19 StartY=40.5 StartZ=0 EndX=-18.2337 EndY=40.5 EndZ=0
    g35: LineSegment StartX=-49.19 StartY=37.5 StartZ=0 EndX=-18.23 EndY=37.5 EndZ=0
    g36: LineSegment StartX=-49.19 StartY=34.5 StartZ=0 EndX=-18.2337 EndY=34.5 EndZ=0
    g37: LineSegment StartX=-49.19 StartY=31.5 StartZ=0 EndX=-18.23 EndY=31.5 EndZ=0
    g38: LineSegment StartX=-49.19 StartY=28.75 StartZ=0 EndX=-16.2837 EndY=28.75 EndZ=0
    g39: LineSegment StartX=-49.19 StartY=25.75 StartZ=0 EndX=-16.28 EndY=25.75 EndZ=0
    g40: LineSegment StartX=-49.19 StartY=23 StartZ=0 EndX=-11.49 EndY=23 EndZ=0
    g41: LineSegment StartX=-49.19 StartY=20 StartZ=0 EndX=-11.49 EndY=20 EndZ=0
    g42: LineSegment StartX=-49.19 StartY=17.25 StartZ=0 EndX=-1.5 EndY=17.25 EndZ=0
    g43: LineSegment StartX=-49.19 StartY=14.25 StartZ=0 EndX=-1.5 EndY=14.25 EndZ=0
    g44: LineSegment StartX=-49.19 StartY=11.5 StartZ=0 EndX=-1.5 EndY=11.5 EndZ=0
    g45: LineSegment StartX=-49.19 StartY=8.5 StartZ=0 EndX=-1.5 EndY=8.5 EndZ=0
    g46: LineSegment StartX=-49.19 StartY=5.75 StartZ=0 EndX=-1.5 EndY=5.75 EndZ=0
    g47: LineSegment StartX=-49.19 StartY=2.75 StartZ=0 EndX=-1.5 EndY=2.75 EndZ=0
  constraints (120):
    c: Vertical(g0)
    c: Distance(g0) = 3
    c: Block(g0)
    c: Vertical(g1)
    c: Distance(g1) = 3
    c: Vertical(g2)
    c: Equal(g0,g2) = 3
    c: Block(g2)
    c: Vertical(g3)
    c: Equal(g1,g3) = 3
    c: Vertical(g4)
    c: Equal(g0,g4) = 3
    c: Block(g4)
    c: Vertical(g5)
    c: Equal(g1,g5) = 3
    c: Vertical(g6)
    c: Equal(g0,g6) = 3
    c: Block(g6)
    c: Vertical(g7)
    c: Equal(g1,g7) = 3
    c: Vertical(g8)
    c: Equal(g0,g8) = 3
    c: Block(g8)
    c: Vertical(g9)
    c: Equal(g1,g9) = 3
    c: Vertical(g10)
    c: Equal(g0,g10) = 3
    c: Block(g10)
    c: Vertical(g11)
    c: Equal(g1,g11) = 3
    c: Block(g12)
    c: Block(g13)
    c: Block(g14)
    c: Block(g15)
    c: Block(g16)
    c: Block(g17)
    c: Block(g18)
    c: Block(g19)
    c: Block(g20)
    c: Block(g21)
    c: Block(g22)
    c: Block(g23)
    c: Block(g11)
    c: Block(g9)
    c: Block(g7)
    c: Block(g5)
    c: Block(g3)
    c: Block(g1)
    c: Coincident(g24,g0)
    c: Coincident(g24,g12)
    c: Horizontal(g24)
    c: Coincident(g25,g0)
    c: Coincident(g25,g12)
    c: Horizontal(g25)
    c: Coincident(g26,g1)
    c: Coincident(g26,g13)
    c: Horizontal(g26)
    c: Coincident(g27,g1)
    c: Coincident(g27,g13)
    c: Horizontal(g27)
    c: Coincident(g28,g2)
    c: Coincident(g28,g14)
    c: Horizontal(g28)
    c: Coincident(g29,g2)
    c: Coincident(g29,g14)
    c: Horizontal(g29)
    c: Coincident(g30,g3)
    c: Coincident(g30,g15)
    c: Horizontal(g30)
    c: Coincident(g31,g3)
    c: Coincident(g31,g15)
    c: Horizontal(g31)
    c: Coincident(g32,g4)
    c: Coincident(g32,g16)
    c: Horizontal(g32)
    c: Coincident(g33,g4)
    c: Coincident(g33,g16)
    c: Horizontal(g33)
    c: Coincident(g34,g5)
    c: Coincident(g34,g17)
    c: Horizontal(g34)
    c: Coincident(g35,g5)
    c: Coincident(g35,g17)
    c: Horizontal(g35)
    c: Coincident(g36,g6)
    c: Coincident(g36,g19)
    c: Horizontal(g36)
    c: Coincident(g37,g6)
    c: Coincident(g37,g19)
    c: Horizontal(g37)
    c: Coincident(g38,g7)
    c: Coincident(g38,g18)
    c: Horizontal(g38)
    c: Coincident(g39,g7)
    c: Coincident(g39,g18)
    c: Horizontal(g39)
    c: Coincident(g40,g8)
    c: Coincident(g40,g20)
    c: Horizontal(g40)
    c: Coincident(g41,g8)
    c: Coincident(g41,g20)
    c: Horizontal(g41)
    c: Coincident(g42,g9)
    c: Coincident(g42,g23)
    c: Horizontal(g42)
    c: Coincident(g43,g9)
    c: Coincident(g43,g23)
    c: Horizontal(g43)
    c: Coincident(g44,g10)
    c: Coincident(g44,g22)
    c: Horizontal(g44)
    c: Coincident(g45,g10)
    c: Coincident(g45,g22)
    c: Horizontal(g45)
    c: Coincident(g46,g11)
    c: Coincident(g46,g21)
    c: Horizontal(g46)
    c: Coincident(g47,g11)
    c: Coincident(g47,g21)
    c: Horizontal(g47)
FEATURE [Sketcher::SketchObject] Sketch031
  FullyConstrained = true
  Placement = pos=(117,19,0) rot=(0.57735,0.57735,0.57735;2.0944rad)
  sketch-geometry (24):
    g0: ArcOfCircle CenterX=-49.19 CenterY=67.75 CenterZ=0 NormalX=0 NormalY=0 NormalZ=1 AngleXU=0 Radius=1.5 StartAngle=1.5708 EndAngle=4.71239
    g1: ArcOfCircle CenterX=-49.19 CenterY=62 CenterZ=0 NormalX=0 NormalY=0 NormalZ=1 AngleXU=0 Radius=1.5 StartAngle=1.5708 EndAngle=4.71239
    g2: ArcOfCircle CenterX=-49.19 CenterY=56.25 CenterZ=0 NormalX=0 NormalY=0 NormalZ=1 AngleXU=0 Radius=1.5 StartAngle=1.5708 EndAngle=4.71239
    g3: ArcOfCircle CenterX=-49.19 CenterY=50.5 CenterZ=0 NormalX=0 NormalY=0 NormalZ=1 AngleXU=0 Radius=1.5 StartAngle=1.5708 EndAngle=4.71239
    g4: ArcOfCircle CenterX=-49.19 CenterY=44.75 CenterZ=0 NormalX=0 NormalY=0 NormalZ=1 AngleXU=0 Radius=1.5 StartAngle=1.5708 EndAngle=4.71239
    g5: ArcOfCircle CenterX=-49.19 CenterY=39 CenterZ=0 NormalX=0 NormalY=0 NormalZ=1 AngleXU=0 Radius=1.5 StartAngle=1.5708 EndAngle=4.71239
    g6: ArcOfCircle CenterX=-49.19 CenterY=33 CenterZ=0 NormalX=0 NormalY=0 NormalZ=1 AngleXU=0 Radius=1.5 StartAngle=1.5708 EndAngle=4.71239
    g7: ArcOfCircle CenterX=-49.19 CenterY=27.25 CenterZ=0 NormalX=0 NormalY=0 NormalZ=1 AngleXU=0 Radius=1.5 StartAngle=1.5708 EndAngle=4.71239
    g8: ArcOfCircle CenterX=-49.19 CenterY=21.5 CenterZ=0 NormalX=0 NormalY=0 NormalZ=1 AngleXU=0 Radius=1.5 StartAngle=1.5708 EndAngle=4.71239
    g9: ArcOfCircle CenterX=-49.19 CenterY=15.75 CenterZ=0 NormalX=0 NormalY=0 NormalZ=1 AngleXU=0 Radius=1.5 StartAngle=1.5708 EndAngle=4.71239
    g10: ArcOfCircle CenterX=-49.19 CenterY=10 CenterZ=0 NormalX=0 NormalY=0 NormalZ=1 AngleXU=0 Radius=1.5 StartAngle=1.5708 EndAngle=4.71239
    g11: ArcOfCircle CenterX=-49.19 CenterY=4.25 CenterZ=0 NormalX=0 NormalY=0 NormalZ=1 AngleXU=0 Radius=1.5 StartAngle=1.5708 EndAngle=4.71239
    g12: LineSegment StartX=-49.19 StartY=69.25 StartZ=0 EndX=-49.19 EndY=66.25 EndZ=0
    g13: LineSegment StartX=-49.19 StartY=63.5 StartZ=0 EndX=-49.19 EndY=60.5 EndZ=0
    g14: LineSegment StartX=-49.19 StartY=57.75 StartZ=0 EndX=-49.19 EndY=54.75 EndZ=0
    g15: LineSegment StartX=-49.19 StartY=52 StartZ=0 EndX=-49.19 EndY=49 EndZ=0
    g16: LineSegment StartX=-49.19 StartY=46.25 StartZ=0 EndX=-49.19 EndY=43.25 EndZ=0
    g17: LineSegment StartX=-49.19 StartY=40.5 StartZ=0 EndX=-49.19 EndY=37.5 EndZ=0
    g18: LineSegment StartX=-49.19 StartY=34.5 StartZ=0 EndX=-49.19 EndY=31.5 EndZ=0
    g19: LineSegment StartX=-49.19 StartY=28.75 StartZ=0 EndX=-49.19 EndY=25.75 EndZ=0
    g20: LineSegment StartX=-49.19 StartY=23 StartZ=0 EndX=-49.19 EndY=20 EndZ=0
    g21: LineSegment StartX=-49.19 StartY=17.25 StartZ=0 EndX=-49.19 EndY=14.25 EndZ=0
    g22: LineSegment StartX=-49.19 StartY=11.5 StartZ=0 EndX=-49.19 EndY=8.5 EndZ=0
    g23: LineSegment StartX=-49.19 StartY=5.75 StartZ=0 EndX=-49.19 EndY=2.75 EndZ=0
  constraints (48):
    c: Block(g0)
    c: Block(g1)
    c: Block(g2)
    c: Block(g3)
    c: Block(g4)
    c: Block(g5)
    c: Block(g6)
    c: Block(g7)
    c: Block(g8)
    c: Block(g9)
    c: Block(g10)
    c: Block(g11)
    c: Coincident(g12,g0)
    c: Coincident(g12,g0)
    c: Vertical(g12)
    c: Vertical(g13)
    c: Coincident(g13,g1)
    c: Vertical(g14)
    c: Coincident(g14,g2)
    c: Vertical(g15)
    c: Coincident(g15,g3)
    c: Vertical(g16)
    c: Coincident(g16,g4)
    c: Vertical(g17)
    c: Coincident(g17,g5)
    c: Vertical(g18)
    c: Coincident(g18,g6)
    c: Vertical(g19)
    c: Coincident(g19,g7)
    c: Vertical(g20)
    c: Coincident(g20,g8)
    c: Vertical(g21)
    c: Coincident(g21,g9)
    c: Vertical(g22)
    c: Coincident(g22,g10)
    c: Vertical(g23)
    c: Coincident(g23,g11)
    c: Block(g23)
    c: Block(g22)
    c: Block(g21)
    c: Block(g20)
    c: Block(g13)
    c: Block(g14)
    c: Block(g15)
    c: Block(g16)
    c: Block(g17)
    c: Block(g18)
    c: Block(g19)
FEATURE [Part::Extrusion] Extrude022
  Base = -> Sketch030
  Dir = (1,-2e-16,2e-16)
  DirMode = 2
  FaceMakerClass = Part::FaceMakerBullseye
  LengthFwd = 19
  LengthRev = 0
  Placement = pos=(-19,0,0) rot=(0,0,1;0rad)
  Solid = true
  Symmetric = false
FEATURE [Part::Fillet] Fillet022
  Base = -> Extrude022
  Edges = 24 edges r=1.49: [Edge6,Edge11,Edge18,Edge23,Edge30,Edge35,Edge42,Edge47,Edge54,Edge59,Edge66,Edge71,Edge78,Edge83,Edge90,Edge95,Edge102,Edge107,Edge114,Edge119,Edge126,Edge131,Edge138,Edge143]
FEATURE [Part::Cut] Cut020  label="top010"
  Base = -> Cut019
  Tool = -> Fillet022
FEATURE [Sketcher::SketchObject] Sketch032
  FullyConstrained = true
  Placement = pos=(117,19,0) rot=(0.57735,0.57735,0.57735;2.0944rad)
  sketch-geometry (48):
    g0: LineSegment StartX=-49.19 StartY=69.25 StartZ=0 EndX=-49.19 EndY=66.25 EndZ=0
    g1: LineSegment StartX=-49.19 StartY=63.5 StartZ=0 EndX=-49.19 EndY=60.5 EndZ=0
    g2: LineSegment StartX=-49.19 StartY=57.75 StartZ=0 EndX=-49.19 EndY=54.75 EndZ=0
    g3: LineSegment StartX=-49.19 StartY=52 StartZ=0 EndX=-49.19 EndY=49 EndZ=0
    g4: LineSegment StartX=-49.19 StartY=46.25 StartZ=0 EndX=-49.19 EndY=43.25 EndZ=0
    g5: LineSegment StartX=-49.19 StartY=40.5 StartZ=0 EndX=-49.19 EndY=37.5 EndZ=0
    g6: LineSegment StartX=-49.19 StartY=34.5 StartZ=0 EndX=-49.19 EndY=31.5 EndZ=0
    g7: LineSegment StartX=-49.19 StartY=28.75 StartZ=0 EndX=-49.19 EndY=25.75 EndZ=0
    g8: LineSegment StartX=-49.19 StartY=23 StartZ=0 EndX=-49.19 EndY=20 EndZ=0
    g9: LineSegment StartX=-49.19 StartY=17.25 StartZ=0 EndX=-49.19 EndY=14.25 EndZ=0
    g10: LineSegment StartX=-49.19 StartY=11.5 StartZ=0 EndX=-49.19 EndY=8.5 EndZ=0
    g11: LineSegment StartX=-49.19 StartY=5.75 StartZ=0 EndX=-49.19 EndY=2.75 EndZ=0
    g12: ArcOfCircle CenterX=-1.5 CenterY=67.75 CenterZ=0 NormalX=0 NormalY=0 NormalZ=1 AngleXU=0 Radius=1.5 StartAngle=4.71239 EndAngle=7.85398
    g13: ArcOfCircle CenterX=-1.5 CenterY=62 CenterZ=0 NormalX=0 NormalY=0 NormalZ=1 AngleXU=0 Radius=1.5 StartAngle=4.71239 EndAngle=7.85398
    g14: ArcOfCircle CenterX=-1.5 CenterY=56.25 CenterZ=0 NormalX=0 NormalY=0 NormalZ=1 AngleXU=0 Radius=1.5 StartAngle=4.71239 EndAngle=7.85398
    g15: ArcOfCircle CenterX=-11.49 CenterY=50.5 CenterZ=0 NormalX=0 NormalY=0 NormalZ=1 AngleXU=0 Radius=1.5 StartAngle=4.71239 EndAngle=7.85398
    g16: ArcOfCircle CenterX=-16.28 CenterY=44.75 CenterZ=0 NormalX=0 NormalY=0 NormalZ=1 AngleXU=0 Radius=1.5 StartAngle=4.71239 EndAngle=7.85398
    g17: ArcOfCircle CenterX=-18.2337 CenterY=39 CenterZ=0 NormalX=0 NormalY=0 NormalZ=1 AngleXU=0 Radius=1.5 StartAngle=4.71485 EndAngle=7.85398
    g18: ArcOfCircle CenterX=-16.2837 CenterY=27.25 CenterZ=0 NormalX=0 NormalY=0 NormalZ=1 AngleXU=0 Radius=1.5 StartAngle=4.71485 EndAngle=7.85398
    g19: ArcOfCircle CenterX=-18.2337 CenterY=33 CenterZ=0 NormalX=0 NormalY=0 NormalZ=1 AngleXU=0 Radius=1.5 StartAngle=4.71485 EndAngle=7.85398
    g20: ArcOfCircle CenterX=-11.49 CenterY=21.5 CenterZ=0 NormalX=0 NormalY=0 NormalZ=1 AngleXU=0 Radius=1.5 StartAngle=4.71239 EndAngle=7.85398
    g21: ArcOfCircle CenterX=-1.5 CenterY=4.25 CenterZ=0 NormalX=0 NormalY=0 NormalZ=1 AngleXU=0 Radius=1.5 StartAngle=4.71239 EndAngle=7.85398
    g22: ArcOfCircle CenterX=-1.5 CenterY=10 CenterZ=0 NormalX=0 NormalY=0 NormalZ=1 AngleXU=0 Radius=1.5 StartAngle=4.71239 EndAngle=7.85398
    g23: ArcOfCircle CenterX=-1.5 CenterY=15.75 CenterZ=0 NormalX=0 NormalY=0 NormalZ=1 AngleXU=0 Radius=1.5 StartAngle=4.71239 EndAngle=7.85398
    g24: LineSegment StartX=-49.19 StartY=69.25 StartZ=0 EndX=-1.5 EndY=69.25 EndZ=0
    g25: LineSegment StartX=-49.19 StartY=66.25 StartZ=0 EndX=-1.5 EndY=66.25 EndZ=0
    g26: LineSegment StartX=-49.19 StartY=63.5 StartZ=0 EndX=-1.5 EndY=63.5 EndZ=0
    g27: LineSegment StartX=-49.19 StartY=60.5 StartZ=0 EndX=-1.5 EndY=60.5 EndZ=0
    g28: LineSegment StartX=-49.19 StartY=57.75 StartZ=0 EndX=-1.5 EndY=57.75 EndZ=0
    g29: LineSegment StartX=-49.19 StartY=54.75 StartZ=0 EndX=-1.5 EndY=54.75 EndZ=0
    g30: LineSegment StartX=-49.19 StartY=52 StartZ=0 EndX=-11.49 EndY=52 EndZ=0
    g31: LineSegment StartX=-49.19 StartY=49 StartZ=0 EndX=-11.49 EndY=49 EndZ=0
    g32: LineSegment StartX=-49.19 StartY=46.25 StartZ=0 EndX=-16.28 EndY=46.25 EndZ=0
    g33: LineSegment StartX=-49.19 StartY=43.25 StartZ=0 EndX=-16.28 EndY=43.25 EndZ=0
    g34: LineSegment StartX=-49.19 StartY=40.5 StartZ=0 EndX=-18.2337 EndY=40.5 EndZ=0
    g35: LineSegment StartX=-49.19 StartY=37.5 StartZ=0 EndX=-18.23 EndY=37.5 EndZ=0
    g36: LineSegment StartX=-49.19 StartY=34.5 StartZ=0 EndX=-18.2337 EndY=34.5 EndZ=0
    g37: LineSegment StartX=-49.19 StartY=31.5 StartZ=0 EndX=-18.23 EndY=31.5 EndZ=0
    g38: LineSegment StartX=-49.19 StartY=28.75 StartZ=0 EndX=-16.2837 EndY=28.75 EndZ=0
    g39: LineSegment StartX=-49.19 StartY=25.75 StartZ=0 EndX=-16.28 EndY=25.75 EndZ=0
    g40: LineSegment StartX=-49.19 StartY=23 StartZ=0 EndX=-11.49 EndY=23 EndZ=0
    g41: LineSegment StartX=-49.19 StartY=20 StartZ=0 EndX=-11.49 EndY=20 EndZ=0
    g42: LineSegment StartX=-49.19 StartY=17.25 StartZ=0 EndX=-1.5 EndY=17.25 EndZ=0
    g43: LineSegment StartX=-49.19 StartY=14.25 StartZ=0 EndX=-1.5 EndY=14.25 EndZ=0
    g44: LineSegment StartX=-49.19 StartY=11.5 StartZ=0 EndX=-1.5 EndY=11.5 EndZ=0
    g45: LineSegment StartX=-49.19 StartY=8.5 StartZ=0 EndX=-1.5 EndY=8.5 EndZ=0
    g46: LineSegment StartX=-49.19 StartY=5.75 StartZ=0 EndX=-1.5 EndY=5.75 EndZ=0
    g47: LineSegment StartX=-49.19 StartY=2.75 StartZ=0 EndX=-1.5 EndY=2.75 EndZ=0
  constraints (120):
    c: Vertical(g0)
    c: Distance(g0) = 3
    c: Block(g0)
    c: Vertical(g1)
    c: Distance(g1) = 3
    c: Vertical(g2)
    c: Equal(g0,g2) = 3
    c: Block(g2)
    c: Vertical(g3)
    c: Equal(g1,g3) = 3
    c: Vertical(g4)
    c: Equal(g0,g4) = 3
    c: Block(g4)
    c: Vertical(g5)
    c: Equal(g1,g5) = 3
    c: Vertical(g6)
    c: Equal(g0,g6) = 3
    c: Block(g6)
    c: Vertical(g7)
    c: Equal(g1,g7) = 3
    c: Vertical(g8)
    c: Equal(g0,g8) = 3
    c: Block(g8)
    c: Vertical(g9)
    c: Equal(g1,g9) = 3
    c: Vertical(g10)
    c: Equal(g0,g10) = 3
    c: Block(g10)
    c: Vertical(g11)
    c: Equal(g1,g11) = 3
    c: Block(g12)
    c: Block(g13)
    c: Block(g14)
    c: Block(g15)
    c: Block(g16)
    c: Block(g17)
    c: Block(g18)
    c: Block(g19)
    c: Block(g20)
    c: Block(g21)
    c: Block(g22)
    c: Block(g23)
    c: Block(g11)
    c: Block(g9)
    c: Block(g7)
    c: Block(g5)
    c: Block(g3)
    c: Block(g1)
    c: Coincident(g24,g0)
    c: Coincident(g24,g12)
    c: Horizontal(g24)
    c: Coincident(g25,g0)
    c: Coincident(g25,g12)
    c: Horizontal(g25)
    c: Coincident(g26,g1)
    c: Coincident(g26,g13)
    c: Horizontal(g26)
    c: Coincident(g27,g1)
    c: Coincident(g27,g13)
    c: Horizontal(g27)
    c: Coincident(g28,g2)
    c: Coincident(g28,g14)
    c: Horizontal(g28)
    c: Coincident(g29,g2)
    c: Coincident(g29,g14)
    c: Horizontal(g29)
    c: Coincident(g30,g3)
    c: Coincident(g30,g15)
    c: Horizontal(g30)
    c: Coincident(g31,g3)
    c: Coincident(g31,g15)
    c: Horizontal(g31)
    c: Coincident(g32,g4)
    c: Coincident(g32,g16)
    c: Horizontal(g32)
    c: Coincident(g33,g4)
    c: Coincident(g33,g16)
    c: Horizontal(g33)
    c: Coincident(g34,g5)
    c: Coincident(g34,g17)
    c: Horizontal(g34)
    c: Coincident(g35,g5)
    c: Coincident(g35,g17)
    c: Horizontal(g35)
    c: Coincident(g36,g6)
    c: Coincident(g36,g19)
    c: Horizontal(g36)
    c: Coincident(g37,g6)
    c: Coincident(g37,g19)
    c: Horizontal(g37)
    c: Coincident(g38,g7)
    c: Coincident(g38,g18)
    c: Horizontal(g38)
    c: Coincident(g39,g7)
    c: Coincident(g39,g18)
    c: Horizontal(g39)
    c: Coincident(g40,g8)
    c: Coincident(g40,g20)
    c: Horizontal(g40)
    c: Coincident(g41,g8)
    c: Coincident(g41,g20)
    c: Horizontal(g41)
    c: Coincident(g42,g9)
    c: Coincident(g42,g23)
    c: Horizontal(g42)
    c: Coincident(g43,g9)
    c: Coincident(g43,g23)
    c: Horizontal(g43)
    c: Coincident(g44,g10)
    c: Coincident(g44,g22)
    c: Horizontal(g44)
    c: Coincident(g45,g10)
    c: Coincident(g45,g22)
    c: Horizontal(g45)
    c: Coincident(g46,g11)
    c: Coincident(g46,g21)
    c: Horizontal(g46)
    c: Coincident(g47,g11)
    c: Coincident(g47,g21)
    c: Horizontal(g47)
FEATURE [Part::Extrusion] Extrude023
  Base = -> Sketch032
  Dir = (1,-2e-16,2e-16)
  DirMode = 2
  FaceMakerClass = Part::FaceMakerBullseye
  LengthFwd = 19
  LengthRev = 0
  Placement = pos=(-19,0,0) rot=(0,0,1;0rad)
  Solid = true
  Symmetric = false
FEATURE [Part::Fillet] Fillet023
  Base = -> Extrude023
  Edges = <same value as first occurrence — deduplicated (x6 in doc)>
  Placement = pos=(0,0.05,0) rot=(0,0,1;0rad)
FEATURE [Part::Cut] Cut014  label="bottom003"
  Base = -> Cut007
  Tool = -> Fusion047
FEATURE [Part::Cut] Cut021  label="bottom004"
  Base = -> Cut014
  Tool = -> Fillet023
FEATURE [Sketcher::SketchObject] Sketch033
  FullyConstrained = true
  Placement = pos=(117,19,0) rot=(0.57735,0.57735,0.57735;2.0944rad)
  sketch-geometry (8):
    g0: LineSegment StartX=-49.19 StartY=69.25 StartZ=0 EndX=-49.19 EndY=66.25 EndZ=0
    g1: LineSegment StartX=-49.19 StartY=5.75 StartZ=0 EndX=-49.19 EndY=2.75 EndZ=0
    g2: ArcOfCircle CenterX=-1.5 CenterY=67.75 CenterZ=0 NormalX=0 NormalY=0 NormalZ=1 AngleXU=0 Radius=1.5 StartAngle=4.71239 EndAngle=7.85398
    g3: ArcOfCircle CenterX=-1.5 CenterY=4.25 CenterZ=0 NormalX=0 NormalY=0 NormalZ=1 AngleXU=0 Radius=1.5 StartAngle=4.71239 EndAngle=7.85398
    g4: LineSegment StartX=-49.19 StartY=69.25 StartZ=0 EndX=-1.5 EndY=69.25 EndZ=0
    g5: LineSegment StartX=-49.19 StartY=66.25 StartZ=0 EndX=-1.5 EndY=66.25 EndZ=0
    g6: LineSegment StartX=-49.19 StartY=5.75 StartZ=0 EndX=-1.5 EndY=5.75 EndZ=0
    g7: LineSegment StartX=-49.19 StartY=2.75 StartZ=0 EndX=-1.5 EndY=2.75 EndZ=0
  constraints (19):
    c: Vertical(g0)
    c: Distance(g0) = 3
    c: Block(g0)
    c: Vertical(g1)
    c: Block(g2)
    c: Block(g3)
    c: Block(g1)
    c: Coincident(g4,g0)
    c: Coincident(g4,g2)
    c: Horizontal(g4)
    c: Coincident(g5,g0)
    c: Coincident(g5,g2)
    c: Horizontal(g5)
    c: Coincident(g6,g1)
    c: Coincident(g6,g3)
    c: Horizontal(g6)
    c: Coincident(g7,g1)
    c: Coincident(g7,g3)
    c: Horizontal(g7)
FEATURE [Sketcher::SketchObject] Sketch034
  FullyConstrained = true
  Placement = pos=(117,19,0) rot=(0.57735,0.57735,0.57735;2.0944rad)
  sketch-geometry (8):
    g0: LineSegment StartX=-49.19 StartY=63.5 StartZ=0 EndX=-49.19 EndY=60.5 EndZ=0
    g1: LineSegment StartX=-49.19 StartY=11.5 StartZ=0 EndX=-49.19 EndY=8.5 EndZ=0
    g2: ArcOfCircle CenterX=-1.5 CenterY=62 CenterZ=0 NormalX=0 NormalY=0 NormalZ=1 AngleXU=0 Radius=1.5 StartAngle=4.71239 EndAngle=7.85398
    g3: ArcOfCircle CenterX=-1.5 CenterY=10 CenterZ=0 NormalX=0 NormalY=0 NormalZ=1 AngleXU=0 Radius=1.5 StartAngle=4.71239 EndAngle=7.85398
    g4: LineSegment StartX=-49.19 StartY=63.5 StartZ=0 EndX=-1.5 EndY=63.5 EndZ=0
    g5: LineSegment StartX=-49.19 StartY=60.5 StartZ=0 EndX=-1.5 EndY=60.5 EndZ=0
    g6: LineSegment StartX=-49.19 StartY=11.5 StartZ=0 EndX=-1.5 EndY=11.5 EndZ=0
    g7: LineSegment StartX=-49.19 StartY=8.5 StartZ=0 EndX=-1.5 EndY=8.5 EndZ=0
  constraints (19):
    c: Vertical(g0)
    c: Distance(g0) = 3
    c: Vertical(g1)
    c: Block(g1)
    c: Block(g2)
    c: Block(g3)
    c: Block(g0)
    c: Coincident(g4,g0)
    c: Coincident(g4,g2)
    c: Horizontal(g4)
    c: Coincident(g5,g0)
    c: Coincident(g5,g2)
    c: Horizontal(g5)
    c: Coincident(g6,g1)
    c: Coincident(g6,g3)
    c: Horizontal(g6)
    c: Coincident(g7,g1)
    c: Coincident(g7,g3)
    c: Horizontal(g7)
FEATURE [Part::Extrusion] Extrude024
  Base = -> Sketch033
  Dir = (1,0,0)
  DirMode = 2
  FaceMakerClass = Part::FaceMakerBullseye
  LengthFwd = 10
  LengthRev = 0
  Solid = true
  Symmetric = false
FEATURE [Part::Extrusion] Extrude025
  Base = -> Sketch034
  Dir = (1,0,0)
  DirMode = 2
  FaceMakerClass = Part::FaceMakerBullseye
  LengthFwd = 10
  LengthRev = 0
  Solid = true
  Symmetric = false
FEATURE [Part::Fillet] Fillet024  label="removeFromtMoreFrontCaseScrewRetainers"
  Base = -> Extrude024
  Edges = 4 edges r=1.49: [Edge6,Edge11,Edge18,Edge23]
  Placement = pos=(-11,0,0) rot=(0,0,1;0rad)
FEATURE [Part::Fillet] Fillet025  label="removeFromtMoreFrontCaseScrewRetainers001"
  Base = -> Extrude025
  Edges = 4 edges r=1.49: [Edge6,Edge11,Edge18,Edge23]
  Placement = pos=(-19,0,0) rot=(0,0,1;0rad)
FEATURE [Part::Cut] Cut022
  Base = -> Cut015
  Tool = -> Fillet025
FEATURE [Part::Cut] Cut023  label="screwRetainers"
  Base = -> Cut022
  Tool = -> Fillet024
FEATURE [Part::MultiFuse] Fusion056  label="bottom005"
  Shapes = -> [Fusion044,Cut021]
FEATURE [Part::MultiFuse] Fusion057  label="casePillars001"
  Shapes = -> [Cut016,Fusion052]
FEATURE [Part::MultiFuse] Fusion058  label="bottom006"
  Shapes = -> [Fusion056,Cut023]
FEATURE [Part::MultiFuse] Fusion059  label="bottom007"
  Shapes = -> [Fusion058,Fillet005]
FEATURE [Part::MultiFuse] Fusion060  label="bottom008"
  Shapes = -> [Fusion059,Fusion]
FEATURE [Part::MultiFuse] Fusion061  label="top011"
  Shapes = -> [Cut006,Cut020]
FEATURE [Part::MultiFuse] Fusion062  label="top012"
  Shapes = -> [Fusion057,Fusion061]
FEATURE [Sketcher::SketchObject] Sketch035  label="topSketch007"
  FullyConstrained = true
  sketch-geometry (6):
    g0: LineSegment StartX=19 StartY=38 StartZ=0 EndX=117 EndY=38 EndZ=0
    g1: ArcOfCircle CenterX=19 CenterY=19 CenterZ=0 NormalX=0 NormalY=0 NormalZ=1 AngleXU=0 Radius=19 StartAngle=1.5708 EndAngle=3.14159
    g2: LineSegment StartX=117 StartY=38 StartZ=0 EndX=117 EndY=19 EndZ=0
    g3: LineSegment StartX=98 StartY=1.0161e-12 StartZ=0 EndX=5.22862e-06 EndY=1.0161e-12 EndZ=0
    g4: LineSegment StartX=5.22862e-06 StartY=19 StartZ=0 EndX=5.22862e-06 EndY=1.0161e-12 EndZ=0
    g5: ArcOfCircle CenterX=98 CenterY=19 CenterZ=0 NormalX=0 NormalY=0 NormalZ=1 AngleXU=0 Radius=19 StartAngle=4.71239 EndAngle=6.28319
  constraints (16):
    c: Horizontal(g0)
    c: Distance(g0) = 98
    c: Coincident(g1,g0)
    c: Block(g1)
    c: Coincident(g2,g0)
    c: Vertical(g2)
    c: Distance(g2) = 19
    c: Horizontal(g3)
    c: Coincident(g4,g1)
    c: Vertical(g4)
    c: Coincident(g3,g4)
    c: Block(g3)
    c: Coincident(g5,g2)
    c: Coincident(g5,g3)
    c: Block(g0)
    c: Block(g5)
FEATURE [Part::Extrusion] Extrude026  label="sideA001"
  Base = -> Sketch035
  Dir = (0,0,1)
  DirMode = 2
  FaceMakerClass = Part::FaceMakerBullseye
  LengthFwd = 3
  LengthRev = 0
  Placement = pos=(0,0,-2.7) rot=(0,0,1;0rad)
  Solid = true
  Symmetric = false
FEATURE [Sketcher::SketchObject] Sketch036  label="topSketch008"
  FullyConstrained = true
  sketch-geometry (6):
    g0: LineSegment StartX=19 StartY=38 StartZ=0 EndX=117 EndY=38 EndZ=0
    g1: ArcOfCircle CenterX=19 CenterY=19 CenterZ=0 NormalX=0 NormalY=0 NormalZ=1 AngleXU=0 Radius=19 StartAngle=1.5708 EndAngle=3.14159
    g2: LineSegment StartX=117 StartY=38 StartZ=0 EndX=117 EndY=19 EndZ=0
    g3: LineSegment StartX=98 StartY=1.0161e-12 StartZ=0 EndX=5.22862e-06 EndY=1.0161e-12 EndZ=0
    g4: LineSegment StartX=5.22862e-06 StartY=19 StartZ=0 EndX=5.22862e-06 EndY=1.0161e-12 EndZ=0
    g5: ArcOfCircle CenterX=98 CenterY=19 CenterZ=0 NormalX=0 NormalY=0 NormalZ=1 AngleXU=0 Radius=19 StartAngle=4.71239 EndAngle=6.28319
  constraints (16):
    c: Horizontal(g0)
    c: Distance(g0) = 98
    c: Coincident(g1,g0)
    c: Block(g1)
    c: Coincident(g2,g0)
    c: Vertical(g2)
    c: Distance(g2) = 19
    c: Horizontal(g3)
    c: Coincident(g4,g1)
    c: Vertical(g4)
    c: Coincident(g3,g4)
    c: Block(g3)
    c: Coincident(g5,g2)
    c: Coincident(g5,g3)
    c: Block(g0)
    c: Block(g5)
FEATURE [Part::Extrusion] Extrude027  label="sideB001"
  Base = -> Sketch036
  Dir = (0,0,1)
  DirMode = 2
  FaceMakerClass = Part::FaceMakerBullseye
  LengthFwd = 3
  LengthRev = 0
  Placement = pos=(0,0,71.7) rot=(0,0,1;0rad)
  Solid = true
  Symmetric = false
FEATURE [Part::MultiFuse] Fusion064  label="removeFromBottom"
  Shapes = -> [Extrude026,Extrude027]
FEATURE [Part::Cut] Cut024  label="bottom009"
  Base = -> Fusion060
  Tool = -> Fusion064
FEATURE [Sketcher::SketchObject] Sketch037  label="topSketch009"
  FullyConstrained = true
  sketch-geometry (8):
    g0: ArcOfCircle CenterX=19 CenterY=19.1201 CenterZ=0 NormalX=0 NormalY=0 NormalZ=1 AngleXU=0 Radius=18.8799 StartAngle=1.5708 EndAngle=3.14793
    g1: LineSegment StartX=0.120501 StartY=19.0004 StartZ=0 EndX=0.120501 EndY=0.000382114 EndZ=0
    g2: LineSegment StartX=19 StartY=38 StartZ=0 EndX=124 EndY=38 EndZ=0
    g3: LineSegment StartX=0.120501 StartY=0.000382114 StartZ=0 EndX=105.121 EndY=0.000382114 EndZ=0
    g4: LineSegment StartX=124 StartY=38 StartZ=0 EndX=125.616 EndY=38 EndZ=0
    g5: LineSegment StartX=105.121 StartY=0.000382114 StartZ=0 EndX=106.736 EndY=0.000382114 EndZ=0
    g6: ArcOfCircle CenterX=106.616 CenterY=19 CenterZ=0 NormalX=0 NormalY=0 NormalZ=1 AngleXU=0 Radius=19 StartAngle=4.71873 EndAngle=6.28319
    g7: LineSegment StartX=125.616 StartY=38 StartZ=0 EndX=125.616 EndY=19 EndZ=0
  constraints (21):
    c: Block(g0)
    c: Coincident(g1,g0)
    c: Vertical(g1)
    c: Horizontal(g2)
    c: Distance(g2) = 105
    c: Coincident(g2,g0)
    c: Distance(g1) = 19
    c: Coincident(g3,g1)
    c: Horizontal(g3)
    c: Distance(g3) = 105
    c: Coincident(g4,g2)
    c: Horizontal(g4)
    c: Distance(g4) = 1.61553
    c: Horizontal(g5)
    c: Equal(g4,g5) = 1.61553
    c: Coincident(g5,g3)
    c: Block(g6)
    c: Coincident(g6,g5)
    c: Coincident(g7,g4)
    c: Coincident(g7,g6)
    c: Vertical(g7)
FEATURE [Part::Extrusion] Extrude028  label="sideB"
  Base = -> Sketch037
  Dir = (0,0,1)
  DirMode = 2
  FaceMakerClass = Part::FaceMakerBullseye
  LengthFwd = 3
  LengthRev = 0
  Placement = pos=(0,0,72) rot=(0,0,1;0rad)
  Solid = true
  Symmetric = false
FEATURE [Sketcher::SketchObject] Sketch038  label="topSketch010"
  FullyConstrained = true
  sketch-geometry (22):
    g0: LineSegment StartX=5.21097e-06 StartY=3 StartZ=0 EndX=5.21097e-06 EndY=19 EndZ=0
    g1: ArcOfCircle CenterX=19 CenterY=19 CenterZ=0 NormalX=0 NormalY=0 NormalZ=1 AngleXU=0 Radius=19 StartAngle=1.5708 EndAngle=3.14159
    g2: ArcOfCircle CenterX=19 CenterY=19 CenterZ=0 NormalX=0 NormalY=0 NormalZ=1 AngleXU=0 Radius=16 StartAngle=1.5708 EndAngle=3.14159
    g3: LineSegment StartX=114 StartY=35 StartZ=0 EndX=19 EndY=35 EndZ=0
    g4: LineSegment StartX=5.21097e-06 StartY=3 StartZ=0 EndX=5.21097e-06 EndY=0 EndZ=0
    g5: LineSegment StartX=3 StartY=0 StartZ=0 EndX=5.21097e-06 EndY=0 EndZ=0
    g6: LineSegment StartX=3 StartY=19 StartZ=0 EndX=3 EndY=0 EndZ=0
    g7: LineSegment StartX=19 StartY=38 StartZ=0 EndX=124 EndY=38 EndZ=0
    g8: Circle CenterX=119 CenterY=35 CenterZ=0 NormalX=0 NormalY=0 NormalZ=1 AngleXU=0 Radius=1
    g9: Circle CenterX=121 CenterY=35 CenterZ=0 NormalX=0 NormalY=0 NormalZ=1 AngleXU=0 Radius=1
    g10: Circle CenterX=121 CenterY=33 CenterZ=0 NormalX=0 NormalY=0 NormalZ=1 AngleXU=0 Radius=1
    g11: BSplineCurve PolesCount=3 KnotsCount=2 Degree=2 IsPeriodic=0
    g12: GeomPoint X=119 Y=35 Z=0
    g13: GeomPoint X=121 Y=33 Z=0
    g14: LineSegment StartX=119 StartY=35 StartZ=0 EndX=114 EndY=35 EndZ=0
    g15: ArcOfCircle CenterX=105 CenterY=19 CenterZ=0 NormalX=0 NormalY=0 NormalZ=1 AngleXU=0 Radius=16 StartAngle=5.60905 EndAngle=6.28319
    g16: LineSegment StartX=121 StartY=33 StartZ=0 EndX=121 EndY=19 EndZ=0
    g17: LineSegment StartX=117.5 StartY=9.01251 StartZ=0 EndX=121.163 EndY=9.0125 EndZ=0
    g18: ArcOfCircle CenterX=105 CenterY=19 CenterZ=0 NormalX=0 NormalY=0 NormalZ=1 AngleXU=0 Radius=20.6155 StartAngle=5.7297 EndAngle=6.28319
    g19: LineSegment StartX=121.163 StartY=9.0125 StartZ=0 EndX=122.538 EndY=8.16329 EndZ=0
    g20: LineSegment StartX=124 StartY=38 StartZ=0 EndX=125.616 EndY=38 EndZ=0
    g21: LineSegment StartX=125.616 StartY=19 StartZ=0 EndX=125.616 EndY=38 EndZ=0
  constraints (49):
    c: Vertical(g0)
    c: Block(g0)
    c: Coincident(g1,g0)
    c: Block(g1)
    c: Coincident(g2,g1)
    c: Block(g2)
    c: Coincident(g3,g2)
    c: Horizontal(g3)
    c: Tangent(g3,g2)
    c: Coincident(g4,g0)
    c: Distance(g4) = 3
    c: Vertical(g4)
    c: Coincident(g5,g4)
    c: Horizontal(g5)
    c: Coincident(g6,g2)
    c: Coincident(g6,g5)
    c: Vertical(g6)
    c: Horizontal(g7)
    c: Distance(g7) = 105
    c: Coincident(g7,g1)
    c: Block(g3)
    c: Weight(g8) = 1
    c: Equal(g8,g9)
    c: Equal(g8,g10)
    c: InternalAlignment(g8,g11)
    c: InternalAlignment(g9,g11)
    c: InternalAlignment(g10,g11)
    c: InternalAlignment(g12,g11)
    c: InternalAlignment(g13,g11)
    c: Block(g11)
    c: Coincident(g14,g11)
    c: Coincident(g14,g3)
    c: Horizontal(g14)
    c: Block(g15)
    c: Coincident(g16,g11)
    c: Coincident(g16,g15)
    c: Vertical(g16)
    c: Distance(g16) = 14
    c: Coincident(g17,g15)
    c: Block(g18)
    c: Coincident(g19,g18)
    c: Coincident(g20,g7)
    c: Horizontal(g20)
    c: Vertical(g21)
    c: Coincident(g20,g21)
    c: Block(g20)
    c: Block(g21)
    c: Block(g19)
    c: Block(g17)
FEATURE [Part::Extrusion] Extrude029
  Base = -> Sketch038
  Dir = (0,0,1)
  DirMode = 2
  FaceMakerClass = Part::FaceMakerBullseye
  LengthFwd = 72
  LengthRev = 0
  Solid = true
  Symmetric = false
FEATURE [Part::Feature] Face085
  shape: bbox 4.8 x 25.5 x 2e-07 mm, 1 faces, 0 solids (baked)
FEATURE [Part::Revolution] Revolve089  label="moreFrontCaseScrewPost003"
  Angle = 360
  Axis = (0,1,0)
  Base = (0,0,0)
  FaceMakerClass = Part::FaceMakerBullseye
  Placement = pos=(109.5,4.5,3.5) rot=(0,0,1;0rad)
  Solid = false
  Source = -> Face085
  Symmetric = false
FEATURE [Part::Feature] Face086
  shape: bbox 4.8 x 25.5 x 2e-07 mm, 1 faces, 0 solids (baked)
FEATURE [Part::Revolution] Revolve090  label="moreFrontCaseScrewPost004"
  Angle = 360
  Axis = (0,1,0)
  Base = (0,0,0)
  FaceMakerClass = Part::FaceMakerBullseye
  Placement = pos=(109.5,4.5,68.5) rot=(0,0,1;0rad)
  Solid = false
  Source = -> Face086
  Symmetric = false
FEATURE [Part::Fillet] Fillet026  label="top013"
  Base = -> Extrude029
  Edges = 1 edges r=2: [Edge35]
FEATURE [Sketcher::SketchObject] Sketch039
  FullyConstrained = true
  sketch-geometry (7):
    g0: LineSegment StartX=0 StartY=0 StartZ=0 EndX=0 EndY=6 EndZ=0
    g1: Circle CenterX=0 CenterY=0 CenterZ=0 NormalX=0 NormalY=0 NormalZ=1 AngleXU=0 Radius=1
    g2: Circle CenterX=8 CenterY=6 CenterZ=0 NormalX=0 NormalY=0 NormalZ=1 AngleXU=0 Radius=1
    g3: BSplineCurve PolesCount=3 KnotsCount=2 Degree=2 IsPeriodic=0
    g4: GeomPoint X=0 Y=0 Z=0
    g5: GeomPoint X=8 Y=6 Z=0
    g6: LineSegment StartX=0 StartY=6 StartZ=0 EndX=8 EndY=6 EndZ=0
  constraints (14):
    c: Coincident(g0,g-1)
    c: Distance(g0) = 6
    c: Vertical(g0)
    c: Coincident(g3,g0)
    c: Weight(g1) = 1
    c: Equal(g1,g2)
    c: InternalAlignment(g1,g3)
    c: InternalAlignment(g2,g3)
    c: InternalAlignment(g4,g3)
    c: InternalAlignment(g5,g3)
    c: Block(g3)
    c: Coincident(g6,g0)
    c: Coincident(g6,g3)
    c: Horizontal(g6)
FEATURE [Sketcher::SketchObject] Sketch040
  FullyConstrained = true
  sketch-geometry (7):
    g0: LineSegment StartX=0 StartY=0 StartZ=0 EndX=0 EndY=6 EndZ=0
    g1: Circle CenterX=0 CenterY=0 CenterZ=0 NormalX=0 NormalY=0 NormalZ=1 AngleXU=0 Radius=1
    g2: Circle CenterX=8 CenterY=6 CenterZ=0 NormalX=0 NormalY=0 NormalZ=1 AngleXU=0 Radius=1
    g3: BSplineCurve PolesCount=3 KnotsCount=2 Degree=2 IsPeriodic=0
    g4: GeomPoint X=0 Y=0 Z=0
    g5: GeomPoint X=8 Y=6 Z=0
    g6: LineSegment StartX=0 StartY=6 StartZ=0 EndX=8 EndY=6 EndZ=0
  constraints (14):
    c: Coincident(g0,g-1)
    c: Distance(g0) = 6
    c: Vertical(g0)
    c: Coincident(g3,g0)
    c: Weight(g1) = 1
    c: Equal(g1,g2)
    c: InternalAlignment(g1,g3)
    c: InternalAlignment(g2,g3)
    c: InternalAlignment(g4,g3)
    c: InternalAlignment(g5,g3)
    c: Block(g3)
    c: Coincident(g6,g0)
    c: Coincident(g6,g3)
    c: Horizontal(g6)
FEATURE [Sketcher::SketchObject] Sketch041
  FullyConstrained = true
  sketch-geometry (7):
    g0: LineSegment StartX=0 StartY=0 StartZ=0 EndX=0 EndY=6 EndZ=0
    g1: Circle CenterX=0 CenterY=0 CenterZ=0 NormalX=0 NormalY=0 NormalZ=1 AngleXU=0 Radius=1
    g2: Circle CenterX=8 CenterY=6 CenterZ=0 NormalX=0 NormalY=0 NormalZ=1 AngleXU=0 Radius=1
    g3: BSplineCurve PolesCount=3 KnotsCount=2 Degree=2 IsPeriodic=0
    g4: GeomPoint X=0 Y=0 Z=0
    g5: GeomPoint X=8 Y=6 Z=0
    g6: LineSegment StartX=0 StartY=6 StartZ=0 EndX=8 EndY=6 EndZ=0
  constraints (14):
    c: Coincident(g0,g-1)
    c: Distance(g0) = 6
    c: Vertical(g0)
    c: Coincident(g3,g0)
    c: Weight(g1) = 1
    c: Equal(g1,g2)
    c: InternalAlignment(g1,g3)
    c: InternalAlignment(g2,g3)
    c: InternalAlignment(g4,g3)
    c: InternalAlignment(g5,g3)
    c: Block(g3)
    c: Coincident(g6,g0)
    c: Coincident(g6,g3)
    c: Horizontal(g6)
FEATURE [Sketcher::SketchObject] Sketch042
  FullyConstrained = true
  sketch-geometry (7):
    g0: LineSegment StartX=0 StartY=0 StartZ=0 EndX=0 EndY=6 EndZ=0
    g1: Circle CenterX=0 CenterY=0 CenterZ=0 NormalX=0 NormalY=0 NormalZ=1 AngleXU=0 Radius=1
    g2: Circle CenterX=8 CenterY=6 CenterZ=0 NormalX=0 NormalY=0 NormalZ=1 AngleXU=0 Radius=1
    g3: BSplineCurve PolesCount=3 KnotsCount=2 Degree=2 IsPeriodic=0
    g4: GeomPoint X=0 Y=0 Z=0
    g5: GeomPoint X=8 Y=6 Z=0
    g6: LineSegment StartX=0 StartY=6 StartZ=0 EndX=8 EndY=6 EndZ=0
  constraints (14):
    c: Coincident(g0,g-1)
    c: Distance(g0) = 6
    c: Vertical(g0)
    c: Coincident(g3,g0)
    c: Weight(g1) = 1
    c: Equal(g1,g2)
    c: InternalAlignment(g1,g3)
    c: InternalAlignment(g2,g3)
    c: InternalAlignment(g4,g3)
    c: InternalAlignment(g5,g3)
    c: Block(g3)
    c: Coincident(g6,g0)
    c: Coincident(g6,g3)
    c: Horizontal(g6)
FEATURE [Part::Extrusion] Extrude030  label="caseScrewPillarBracket008"
  Base = -> Sketch039
  Dir = (0,0,1)
  DirMode = 2
  FaceMakerClass = Part::FaceMakerBullseye
  LengthFwd = 2.4
  LengthRev = 0
  Placement = pos=(15.76,29,8.8) rot=(0,1,0;0rad)
  Solid = true
  Symmetric = false
FEATURE [Part::Extrusion] Extrude031  label="caseScrewPillarBracket009"
  Base = -> Sketch040
  Dir = (0,0,1)
  DirMode = 2
  FaceMakerClass = Part::FaceMakerBullseye
  LengthFwd = 2.4
  LengthRev = 0
  Placement = pos=(15.76,29,60.8) rot=(0,0,1;0rad)
  Solid = true
  Symmetric = false
FEATURE [Part::Extrusion] Extrude032  label="caseScrewPillarBracket010"
  Base = -> Sketch041
  Dir = (0,0,1)
  DirMode = 2
  FaceMakerClass = Part::FaceMakerBullseye
  LengthFwd = 2.4
  LengthRev = 0
  Placement = pos=(13.7,29,13.26) rot=(0,-1,0;1.5708rad)
  Solid = true
  Symmetric = false
FEATURE [Part::Extrusion] Extrude033  label="caseScrewPillarBracket011"
  Base = -> Sketch042
  Dir = (0,0,1)
  DirMode = 2
  FaceMakerClass = Part::FaceMakerBullseye
  LengthFwd = 2.4
  LengthRev = 0
  Placement = pos=(11.3,29,58.74) rot=(0,1,0;1.5708rad)
  Solid = true
  Symmetric = false
FEATURE [Sketcher::SketchObject] Sketch043
  FullyConstrained = true
  sketch-geometry (7):
    g0: LineSegment StartX=0 StartY=0 StartZ=0 EndX=0 EndY=6 EndZ=0
    g1: Circle CenterX=0 CenterY=0 CenterZ=0 NormalX=0 NormalY=0 NormalZ=1 AngleXU=0 Radius=1
    g2: Circle CenterX=8 CenterY=6 CenterZ=0 NormalX=0 NormalY=0 NormalZ=1 AngleXU=0 Radius=1
    g3: BSplineCurve PolesCount=3 KnotsCount=2 Degree=2 IsPeriodic=0
    g4: GeomPoint X=0 Y=0 Z=0
    g5: GeomPoint X=8 Y=6 Z=0
    g6: LineSegment StartX=0 StartY=6 StartZ=0 EndX=8 EndY=6 EndZ=0
  constraints (14):
    c: Coincident(g0,g-1)
    c: Distance(g0) = 6
    c: Vertical(g0)
    c: Coincident(g3,g0)
    c: Weight(g1) = 1
    c: Equal(g1,g2)
    c: InternalAlignment(g1,g3)
    c: InternalAlignment(g2,g3)
    c: InternalAlignment(g4,g3)
    c: InternalAlignment(g5,g3)
    c: Block(g3)
    c: Coincident(g6,g0)
    c: Coincident(g6,g3)
    c: Horizontal(g6)
FEATURE [Part::Extrusion] Extrude034  label="caseScrewPillarBracket012"
  Base = -> Sketch043
  Dir = (0,0,1)
  DirMode = 2
  FaceMakerClass = Part::FaceMakerBullseye
  LengthFwd = 2.4
  LengthRev = 0
  Placement = pos=(88.3,29,65.23) rot=(0,1,0;1.5708rad)
  Solid = true
  Symmetric = false
FEATURE [Sketcher::SketchObject] Sketch044
  FullyConstrained = true
  sketch-geometry (7):
    g0: LineSegment StartX=0 StartY=0 StartZ=0 EndX=0 EndY=6 EndZ=0
    g1: Circle CenterX=0 CenterY=0 CenterZ=0 NormalX=0 NormalY=0 NormalZ=1 AngleXU=0 Radius=1
    g2: Circle CenterX=8 CenterY=6 CenterZ=0 NormalX=0 NormalY=0 NormalZ=1 AngleXU=0 Radius=1
    g3: BSplineCurve PolesCount=3 KnotsCount=2 Degree=2 IsPeriodic=0
    g4: GeomPoint X=0 Y=0 Z=0
    g5: GeomPoint X=8 Y=6 Z=0
    g6: LineSegment StartX=0 StartY=6 StartZ=0 EndX=8 EndY=6 EndZ=0
  constraints (14):
    c: Coincident(g0,g-1)
    c: Distance(g0) = 6
    c: Vertical(g0)
    c: Coincident(g3,g0)
    c: Weight(g1) = 1
    c: Equal(g1,g2)
    c: InternalAlignment(g1,g3)
    c: InternalAlignment(g2,g3)
    c: InternalAlignment(g4,g3)
    c: InternalAlignment(g5,g3)
    c: Block(g3)
    c: Coincident(g6,g0)
    c: Coincident(g6,g3)
    c: Horizontal(g6)
FEATURE [Part::Extrusion] Extrude035  label="caseScrewPillarBracket013"
  Base = -> Sketch044
  Dir = (0,0,1)
  DirMode = 2
  FaceMakerClass = Part::FaceMakerBullseye
  LengthFwd = 2.4
  LengthRev = 0
  Placement = pos=(90.7,29,6.77) rot=(0,-1,0;1.5708rad)
  Solid = true
  Symmetric = false
FEATURE [Sketcher::SketchObject] Sketch045
  FullyConstrained = true
  sketch-geometry (7):
    g0: LineSegment StartX=0 StartY=0 StartZ=0 EndX=0 EndY=6 EndZ=0
    g1: Circle CenterX=0 CenterY=0 CenterZ=0 NormalX=0 NormalY=0 NormalZ=1 AngleXU=0 Radius=1
    g2: Circle CenterX=8 CenterY=6 CenterZ=0 NormalX=0 NormalY=0 NormalZ=1 AngleXU=0 Radius=1
    g3: BSplineCurve PolesCount=3 KnotsCount=2 Degree=2 IsPeriodic=0
    g4: GeomPoint X=0 Y=0 Z=0
    g5: GeomPoint X=8 Y=6 Z=0
    g6: LineSegment StartX=0 StartY=6 StartZ=0 EndX=8 EndY=6 EndZ=0
  constraints (14):
    c: Coincident(g0,g-1)
    c: Distance(g0) = 6
    c: Vertical(g0)
    c: Coincident(g3,g0)
    c: Weight(g1) = 1
    c: Equal(g1,g2)
    c: InternalAlignment(g1,g3)
    c: InternalAlignment(g2,g3)
    c: InternalAlignment(g4,g3)
    c: InternalAlignment(g5,g3)
    c: Block(g3)
    c: Coincident(g6,g0)
    c: Coincident(g6,g3)
    c: Horizontal(g6)
FEATURE [Sketcher::SketchObject] Sketch046
  FullyConstrained = true
  sketch-geometry (7):
    g0: LineSegment StartX=0 StartY=0 StartZ=0 EndX=0 EndY=6 EndZ=0
    g1: Circle CenterX=0 CenterY=0 CenterZ=0 NormalX=0 NormalY=0 NormalZ=1 AngleXU=0 Radius=1
    g2: Circle CenterX=8 CenterY=6 CenterZ=0 NormalX=0 NormalY=0 NormalZ=1 AngleXU=0 Radius=1
    g3: BSplineCurve PolesCount=3 KnotsCount=2 Degree=2 IsPeriodic=0
    g4: GeomPoint X=0 Y=0 Z=0
    g5: GeomPoint X=8 Y=6 Z=0
    g6: LineSegment StartX=0 StartY=6 StartZ=0 EndX=8 EndY=6 EndZ=0
  constraints (14):
    c: Coincident(g0,g-1)
    c: Distance(g0) = 6
    c: Vertical(g0)
    c: Coincident(g3,g0)
    c: Weight(g1) = 1
    c: Equal(g1,g2)
    c: InternalAlignment(g1,g3)
    c: InternalAlignment(g2,g3)
    c: InternalAlignment(g4,g3)
    c: InternalAlignment(g5,g3)
    c: Block(g3)
    c: Coincident(g6,g0)
    c: Coincident(g6,g3)
    c: Horizontal(g6)
FEATURE [Part::Extrusion] Extrude036  label="caseScrewPillarBracket014"
  Base = -> Sketch045
  Dir = (0,0,1)
  DirMode = 2
  FaceMakerClass = Part::FaceMakerBullseye
  LengthFwd = 2.4
  LengthRev = 0
  Placement = pos=(110.7,29,6.77) rot=(0,-1,0;1.5708rad)
  Solid = true
  Symmetric = false
FEATURE [Part::Extrusion] Extrude037  label="caseScrewPillarBracket015"
  Base = -> Sketch046
  Dir = (0,0,1)
  DirMode = 2
  FaceMakerClass = Part::FaceMakerBullseye
  LengthFwd = 2.4
  LengthRev = 0
  Placement = pos=(108.3,29,65.23) rot=(0,1,0;1.5708rad)
  Solid = true
  Symmetric = false
FEATURE [Part::Box] Box013  label="frontCaseScrewPillarBracket002"
  AttacherType = Attacher::AttachEngine3D
  Height = 2.4
  Length = 22
  Placement = pos=(87,28,2.3) rot=(0,0,1;0rad)
  Width = 7
FEATURE [Part::Box] Box014  label="frontCaseScrewPillarBracket003"
  AttacherType = Attacher::AttachEngine3D
  Height = 2.4
  Length = 22
  Placement = pos=(87,28,67.3) rot=(0,0,1;0rad)
  Width = 7
FEATURE [Part::Feature] Face087
  shape: bbox 4.8 x 30.2 x 2e-07 mm, 1 faces, 0 solids (baked)
FEATURE [Part::Revolution] Revolve091  label="frontCaseScrewPost004"
  Angle = 360
  Axis = (0,1,0)
  Base = (0,0,0)
  FaceMakerClass = Part::FaceMakerBullseye
  Placement = pos=(89.5,4.5,3.5) rot=(0,0,1;0rad)
  Solid = false
  Source = -> Face087
  Symmetric = false
FEATURE [Part::Feature] Face088
  shape: bbox 4.8 x 30.2 x 2e-07 mm, 1 faces, 0 solids (baked)
FEATURE [Part::Revolution] Revolve092  label="frontCaseScrewPost005"
  Angle = 360
  Axis = (0,1,0)
  Base = (0,0,0)
  FaceMakerClass = Part::FaceMakerBullseye
  Placement = pos=(89.5,4.5,68.5) rot=(0,0,1;0rad)
  Solid = false
  Source = -> Face088
  Symmetric = false
FEATURE [Part::Feature] Face089
  shape: bbox 3.5 x 30.2 x 2e-07 mm, 1 faces, 0 solids (baked)
FEATURE [Part::Revolution] Revolve093  label="backCaseScrewPost002"
  Angle = 360
  Axis = (0,1,0)
  Base = (0,0,0)
  FaceMakerClass = Part::FaceMakerBullseye
  Placement = pos=(12.5,4.5,10) rot=(0,0,1;0rad)
  Solid = false
  Source = -> Face089
  Symmetric = false
FEATURE [Part::Feature] Face090
  shape: bbox 3.5 x 30.2 x 2e-07 mm, 1 faces, 0 solids (baked)
FEATURE [Part::Revolution] Revolve094  label="backCaseScrewPost003"
  Angle = 360
  Axis = (0,1,0)
  Base = (0,0,0)
  FaceMakerClass = Part::FaceMakerBullseye
  Placement = pos=(12.5,4.5,62) rot=(0,0,1;0rad)
  Solid = false
  Source = -> Face090
  Symmetric = false
FEATURE [Part::Box] Box015  label="Cube011"
  AttacherType = Attacher::AttachEngine3D
  Height = 28.8
  Length = 3
  Placement = pos=(107.3,28,21.6) rot=(0,0,1;0rad)
  Width = 7
FEATURE [Part::Box] Box016  label="Cube012"
  AttacherType = Attacher::AttachEngine3D
  Height = 3
  Length = 7.4
  Placement = pos=(107.3,28,18.6) rot=(0,0,1;0rad)
  Width = 7
FEATURE [Part::Box] Box017  label="Cube013"
  AttacherType = Attacher::AttachEngine3D
  Height = 3
  Length = 7.4
  Placement = pos=(107.3,28,50.4) rot=(0,0,1;0rad)
  Width = 7
FEATURE [Part::Cylinder] Cylinder024
  Angle = 360
  AttacherType = Attacher::AttachEngine3D
  Height = 20
  Placement = pos=(0,0,36.15) rot=(0,0,1;0rad)
  Radius = 14.3
FEATURE [Part::Cylinder] Cylinder025
  Angle = 360
  AttacherType = Attacher::AttachEngine3D
  Height = 10
  Placement = pos=(0,0,36.15) rot=(0,0,1;0rad)
  Radius = 4
FEATURE [Part::MultiFuse] Fusion066  label="removeToCreteHoleForPlugHousing009"
  Placement = pos=(70,19,36) rot=(0,1,0;1.5708rad)
  Shapes = -> [Cylinder024,Cylinder025]
FEATURE [Part::MultiFuse] Fusion065  label="plugHousingBracketHolder002"
  Shapes = -> [Box017,Box015,Box016]
FEATURE [Part::Cut] Cut025  label="plugHousingBracketHolder003"
  Base = -> Fusion065
  Placement = pos=(7,0,0) rot=(0,0,1;0rad)
  Tool = -> Fusion066
FEATURE [Sketcher::SketchObject] Sketch047
  FullyConstrained = false
  Placement = pos=(0,0,0) rot=(1,0,0;1.5708rad)
  sketch-geometry (24):
    g0: ArcOfCircle CenterX=-4 CenterY=-10.5 CenterZ=0 NormalX=0 NormalY=0 NormalZ=1 AngleXU=0 Radius=1.5 StartAngle=6e-16 EndAngle=3.14159
    g1: ArcOfCircle CenterX=-34.2 CenterY=-10.5 CenterZ=0 NormalX=0 NormalY=0 NormalZ=1 AngleXU=0 Radius=1.5 StartAngle=0 EndAngle=3.14159
    g2: ArcOfCircle CenterX=-34.2 CenterY=-27.7 CenterZ=0 NormalX=0 NormalY=0 NormalZ=1 AngleXU=0 Radius=1.5 StartAngle=3.14159 EndAngle=6.28319
    g3: ArcOfCircle CenterX=-4 CenterY=-27.7 CenterZ=0 NormalX=0 NormalY=0 NormalZ=1 AngleXU=0 Radius=1.5 StartAngle=3.1416 EndAngle=6.28319
    g4: ArcOfCircle CenterX=-10 CenterY=-4.3 CenterZ=0 NormalX=0 NormalY=0 NormalZ=1 AngleXU=0 Radius=1.5 StartAngle=2e-16 EndAngle=3.14159
    g5: ArcOfCircle CenterX=-16.1 CenterY=-1.8 CenterZ=0 NormalX=0 NormalY=0 NormalZ=1 AngleXU=0 Radius=1.5 StartAngle=5e-16 EndAngle=3.14159
    g6: ArcOfCircle CenterX=-22.1 CenterY=-1.8 CenterZ=0 NormalX=0 NormalY=0 NormalZ=1 AngleXU=0 Radius=1.5 StartAngle=5e-16 EndAngle=3.14159
    g7: ArcOfCircle CenterX=-28.2 CenterY=-4.3 CenterZ=0 NormalX=0 NormalY=0 NormalZ=1 AngleXU=0 Radius=1.5 StartAngle=2e-16 EndAngle=3.14159
    g8: ArcOfCircle CenterX=-10 CenterY=-33.9 CenterZ=0 NormalX=0 NormalY=0 NormalZ=1 AngleXU=0 Radius=1.5 StartAngle=3.14159 EndAngle=6.28319
    g9: ArcOfCircle CenterX=-16.1 CenterY=-36.4 CenterZ=0 NormalX=0 NormalY=0 NormalZ=1 AngleXU=0 Radius=1.5 StartAngle=3.14159 EndAngle=6.28319
    g10: ArcOfCircle CenterX=-22.1 CenterY=-36.4 CenterZ=0 NormalX=0 NormalY=0 NormalZ=1 AngleXU=0 Radius=1.5 StartAngle=3.14159 EndAngle=6.28319
    g11: ArcOfCircle CenterX=-28.2 CenterY=-33.9 CenterZ=0 NormalX=0 NormalY=0 NormalZ=1 AngleXU=0 Radius=1.5 StartAngle=3.14159 EndAngle=6.28319
    g12: LineSegment StartX=-35.7 StartY=-10.5 StartZ=0 EndX=-35.7 EndY=-27.7 EndZ=0
    g13: LineSegment StartX=-32.7 StartY=-10.5 StartZ=0 EndX=-32.7 EndY=-27.7 EndZ=0
    g14: LineSegment StartX=-29.7 StartY=-33.9 StartZ=0 EndX=-29.7 EndY=-4.3 EndZ=0
    g15: LineSegment StartX=-26.7 StartY=-33.9 StartZ=0 EndX=-26.7 EndY=-4.3 EndZ=0
    g16: LineSegment StartX=-2.5 StartY=-10.5 StartZ=0 EndX=-2.5 EndY=-27.7 EndZ=0
    g17: LineSegment StartX=-8.5 StartY=-4.3 StartZ=0 EndX=-8.5 EndY=-33.9 EndZ=0
    g18: LineSegment StartX=-5.5 StartY=-10.5 StartZ=0 EndX=-5.5 EndY=-27.7 EndZ=0
    g19: LineSegment StartX=-11.5 StartY=-4.3 StartZ=0 EndX=-11.5 EndY=-33.9 EndZ=0
    g20: LineSegment StartX=-14.6 StartY=-1.8 StartZ=0 EndX=-14.6 EndY=-36.4 EndZ=0
    g21: LineSegment StartX=-17.6 StartY=-1.8 StartZ=0 EndX=-17.6 EndY=-36.4 EndZ=0
    g22: LineSegment StartX=-20.6 StartY=-36.4 StartZ=0 EndX=-20.6 EndY=-1.8 EndZ=0
    g23: LineSegment StartX=-23.6 StartY=-1.8 StartZ=0 EndX=-23.6 EndY=-36.4 EndZ=0
  constraints (48):
    c: Block(g0)
    c: Block(g1)
    c: Block(g2)
    c: Block(g3)
    c: Block(g4)
    c: Block(g5)
    c: Block(g6)
    c: Block(g7)
    c: Block(g8)
    c: Block(g9)
    c: Block(g10)
    c: Block(g11)
    c: Coincident(g12,g1)
    c: Coincident(g12,g2)
    c: Vertical(g12)
    c: Coincident(g13,g1)
    c: Coincident(g13,g2)
    c: Vertical(g13)
    c: Coincident(g14,g11)
    c: Coincident(g14,g7)
    c: Vertical(g14)
    c: Coincident(g15,g11)
    c: Coincident(g15,g7)
    c: Vertical(g15)
    c: Coincident(g16,g0)
    c: Coincident(g16,g3)
    c: Vertical(g16)
    c: Coincident(g17,g4)
    c: Coincident(g17,g8)
    c: Vertical(g17)
    c: Coincident(g18,g0)
    c: Coincident(g18,g3)
    c: Vertical(g18)
    c: Coincident(g19,g4)
    c: Coincident(g19,g8)
    c: Vertical(g19)
    c: Coincident(g20,g5)
    c: Coincident(g20,g9)
    c: Vertical(g20)
    c: Coincident(g21,g5)
    c: Coincident(g21,g9)
    c: Vertical(g21)
    c: Coincident(g22,g10)
    c: Coincident(g22,g6)
    c: Vertical(g22)
    c: Coincident(g23,g6)
    c: Coincident(g23,g10)
    c: Vertical(g23)
FEATURE [Part::Extrusion] Extrude038  label="removeToCreateFanGrillHoles001"
  Base = -> Sketch047
  Dir = (0,-1,6e-16)
  DirMode = 2
  FaceMakerClass = Part::FaceMakerBullseye
  LengthFwd = 10
  LengthRev = 0
  Placement = pos=(65.4,44,54.82) rot=(0,0,1;0rad)
  Solid = true
  Symmetric = false
FEATURE [Part::Feature] Wire004
  shape: bbox 11 x 5.2 x 2e-07 mm, 0 faces, 0 solids (baked)
FEATURE [Part::Revolution] Revolve095
  Angle = 360
  Axis = (0,1,0)
  Base = (0,0,0)
  FaceMakerClass = Part::FaceMakerBullseye
  Placement = pos=(30.3,38,19.7) rot=(0,0,1;0rad)
  Solid = true
  Source = -> Wire004
  Symmetric = false
FEATURE [Part::Feature] Wire005
  shape: bbox 11 x 5.2 x 2e-07 mm, 0 faces, 0 solids (baked)
FEATURE [Part::Revolution] Revolve096
  Angle = 360
  Axis = (0,1,0)
  Base = (0,0,0)
  FaceMakerClass = Part::FaceMakerBullseye
  Placement = pos=(30.3,38,51.7) rot=(0,0,1;0rad)
  Solid = true
  Source = -> Wire005
  Symmetric = false
FEATURE [Part::Feature] Wire006
  shape: bbox 11 x 5.2 x 2e-07 mm, 0 faces, 0 solids (baked)
FEATURE [Part::Revolution] Revolve097
  Angle = 360
  Axis = (0,1,0)
  Base = (0,0,0)
  FaceMakerClass = Part::FaceMakerBullseye
  Placement = pos=(62.3,38,51.7) rot=(0,0,1;0rad)
  Solid = true
  Source = -> Wire006
  Symmetric = false
FEATURE [Part::Feature] Wire007
  shape: bbox 11 x 5.2 x 2e-07 mm, 0 faces, 0 solids (baked)
FEATURE [Part::Revolution] Revolve098
  Angle = 360
  Axis = (0,1,0)
  Base = (0,0,0)
  FaceMakerClass = Part::FaceMakerBullseye
  Placement = pos=(62.3,38,19.7) rot=(0,0,1;0rad)
  Solid = true
  Source = -> Wire007
  Symmetric = false
FEATURE [Part::MultiFuse] Fusion067  label="fanScrewHousing002"
  Shapes = -> [Revolve098,Revolve097,Revolve096,Revolve095]
FEATURE [Part::Feature] Face091 .. Face094  x4 (patterned run collapsed; names and placements below)
  shape: bbox 3.5 x 17.8 x 2e-07 mm, 1 faces, 0 solids (baked)
FEATURE [Part::Revolution] Revolve099  label="removeToCreateScrewAndThreadedInsertHole026"
  Angle = 360
  Axis = (0,1,0)
  Base = (0,0,0)
  FaceMakerClass = Part::FaceMakerBullseye
  Placement = pos=(62.3,30.3,19.7) rot=(0,0,1;0rad)
  Solid = false
  Source = -> Face091
  Symmetric = false
FEATURE [Part::Revolution] Revolve100  label="removeToCreateScrewAndThreadedInsertHole027"
  Angle = 360
  Axis = (0,1,0)
  Base = (0,0,0)
  FaceMakerClass = Part::FaceMakerBullseye
  Placement = pos=(62.3,30.3,51.7) rot=(0,0,1;0rad)
  Solid = false
  Source = -> Face092
  Symmetric = false
FEATURE [Part::Revolution] Revolve101  label="removeToCreateScrewAndThreadedInsertHole028"
  Angle = 360
  Axis = (0,1,0)
  Base = (0,0,0)
  FaceMakerClass = Part::FaceMakerBullseye
  Placement = pos=(30.3,30.3,19.7) rot=(0,0,1;0rad)
  Solid = false
  Source = -> Face093
  Symmetric = false
FEATURE [Part::Revolution] Revolve102  label="removeToCreateScrewAndThreadedInsertHole029"
  Angle = 360
  Axis = (0,1,0)
  Base = (0,0,0)
  FaceMakerClass = Part::FaceMakerBullseye
  Placement = pos=(30.3,30.3,51.7) rot=(0,0,1;0rad)
  Solid = false
  Source = -> Face094
  Symmetric = false
FEATURE [Part::MultiFuse] Fusion068  label="createThreadedInsertHolesForFan002"
  Shapes = -> [Revolve099,Revolve100,Revolve101,Revolve102]
FEATURE [Part::Cut] Cut026  label="fanScrewHousing003"
  Base = -> Fusion067
  Tool = -> Fusion068
FEATURE [Sketcher::SketchObject] Sketch048
  FullyConstrained = false
  Placement = pos=(0,0,0) rot=(1,0,0;1.5708rad)
  sketch-geometry (24):
    g0: ArcOfCircle CenterX=-4 CenterY=-10.5 CenterZ=0 NormalX=0 NormalY=0 NormalZ=1 AngleXU=0 Radius=1.5 StartAngle=6e-16 EndAngle=3.14159
    g1: ArcOfCircle CenterX=-34.2 CenterY=-10.5 CenterZ=0 NormalX=0 NormalY=0 NormalZ=1 AngleXU=0 Radius=1.5 StartAngle=0 EndAngle=3.14159
    g2: ArcOfCircle CenterX=-34.2 CenterY=-27.7 CenterZ=0 NormalX=0 NormalY=0 NormalZ=1 AngleXU=0 Radius=1.5 StartAngle=3.14159 EndAngle=6.28319
    g3: ArcOfCircle CenterX=-4 CenterY=-27.7 CenterZ=0 NormalX=0 NormalY=0 NormalZ=1 AngleXU=0 Radius=1.5 StartAngle=3.1416 EndAngle=6.28319
    g4: ArcOfCircle CenterX=-10 CenterY=-4.3 CenterZ=0 NormalX=0 NormalY=0 NormalZ=1 AngleXU=0 Radius=1.5 StartAngle=2e-16 EndAngle=3.14159
    g5: ArcOfCircle CenterX=-16.1 CenterY=-1.8 CenterZ=0 NormalX=0 NormalY=0 NormalZ=1 AngleXU=0 Radius=1.5 StartAngle=5e-16 EndAngle=3.14159
    g6: ArcOfCircle CenterX=-22.1 CenterY=-1.8 CenterZ=0 NormalX=0 NormalY=0 NormalZ=1 AngleXU=0 Radius=1.5 StartAngle=5e-16 EndAngle=3.14159
    g7: ArcOfCircle CenterX=-28.2 CenterY=-4.3 CenterZ=0 NormalX=0 NormalY=0 NormalZ=1 AngleXU=0 Radius=1.5 StartAngle=2e-16 EndAngle=3.14159
    g8: ArcOfCircle CenterX=-10 CenterY=-33.9 CenterZ=0 NormalX=0 NormalY=0 NormalZ=1 AngleXU=0 Radius=1.5 StartAngle=3.14159 EndAngle=6.28319
    g9: ArcOfCircle CenterX=-16.1 CenterY=-36.4 CenterZ=0 NormalX=0 NormalY=0 NormalZ=1 AngleXU=0 Radius=1.5 StartAngle=3.14159 EndAngle=6.28319
    g10: ArcOfCircle CenterX=-22.1 CenterY=-36.4 CenterZ=0 NormalX=0 NormalY=0 NormalZ=1 AngleXU=0 Radius=1.5 StartAngle=3.14159 EndAngle=6.28319
    g11: ArcOfCircle CenterX=-28.2 CenterY=-33.9 CenterZ=0 NormalX=0 NormalY=0 NormalZ=1 AngleXU=0 Radius=1.5 StartAngle=3.14159 EndAngle=6.28319
    g12: LineSegment StartX=-35.7 StartY=-10.5 StartZ=0 EndX=-35.7 EndY=-27.7 EndZ=0
    g13: LineSegment StartX=-32.7 StartY=-10.5 StartZ=0 EndX=-32.7 EndY=-27.7 EndZ=0
    g14: LineSegment StartX=-29.7 StartY=-33.9 StartZ=0 EndX=-29.7 EndY=-4.3 EndZ=0
    g15: LineSegment StartX=-26.7 StartY=-33.9 StartZ=0 EndX=-26.7 EndY=-4.3 EndZ=0
    g16: LineSegment StartX=-2.5 StartY=-10.5 StartZ=0 EndX=-2.5 EndY=-27.7 EndZ=0
    g17: LineSegment StartX=-8.5 StartY=-4.3 StartZ=0 EndX=-8.5 EndY=-33.9 EndZ=0
    g18: LineSegment StartX=-5.5 StartY=-10.5 StartZ=0 EndX=-5.5 EndY=-27.7 EndZ=0
    g19: LineSegment StartX=-11.5 StartY=-4.3 StartZ=0 EndX=-11.5 EndY=-33.9 EndZ=0
    g20: LineSegment StartX=-14.6 StartY=-1.8 StartZ=0 EndX=-14.6 EndY=-36.4 EndZ=0
    g21: LineSegment StartX=-17.6 StartY=-1.8 StartZ=0 EndX=-17.6 EndY=-36.4 EndZ=0
    g22: LineSegment StartX=-20.6 StartY=-36.4 StartZ=0 EndX=-20.6 EndY=-1.8 EndZ=0
    g23: LineSegment StartX=-23.6 StartY=-1.8 StartZ=0 EndX=-23.6 EndY=-36.4 EndZ=0
  constraints (48):
    c: Block(g0)
    c: Block(g1)
    c: Block(g2)
    c: Block(g3)
    c: Block(g4)
    c: Block(g5)
    c: Block(g6)
    c: Block(g7)
    c: Block(g8)
    c: Block(g9)
    c: Block(g10)
    c: Block(g11)
    c: Coincident(g12,g1)
    c: Coincident(g12,g2)
    c: Vertical(g12)
    c: Coincident(g13,g1)
    c: Coincident(g13,g2)
    c: Vertical(g13)
    c: Coincident(g14,g11)
    c: Coincident(g14,g7)
    c: Vertical(g14)
    c: Coincident(g15,g11)
    c: Coincident(g15,g7)
    c: Vertical(g15)
    c: Coincident(g16,g0)
    c: Coincident(g16,g3)
    c: Vertical(g16)
    c: Coincident(g17,g4)
    c: Coincident(g17,g8)
    c: Vertical(g17)
    c: Coincident(g18,g0)
    c: Coincident(g18,g3)
    c: Vertical(g18)
    c: Coincident(g19,g4)
    c: Coincident(g19,g8)
    c: Vertical(g19)
    c: Coincident(g20,g5)
    c: Coincident(g20,g9)
    c: Vertical(g20)
    c: Coincident(g21,g5)
    c: Coincident(g21,g9)
    c: Vertical(g21)
    c: Coincident(g22,g10)
    c: Coincident(g22,g6)
    c: Vertical(g22)
    c: Coincident(g23,g6)
    c: Coincident(g23,g10)
    c: Vertical(g23)
FEATURE [Part::Extrusion] Extrude039  label="removeToCreateFanGrillHoles002"
  Base = -> Sketch048
  Dir = (0,-1,6e-16)
  DirMode = 2
  FaceMakerClass = Part::FaceMakerBullseye
  LengthFwd = 10
  LengthRev = 0
  Placement = pos=(65.4,44,54.82) rot=(0,0,1;0rad)
  Solid = true
  Symmetric = false
FEATURE [Part::Cut] Cut027  label="fanScrewHousing004"
  Base = -> Cut026
  Tool = -> Extrude038
FEATURE [Part::Cut] Cut028  label="top014"
  Base = -> Fillet026
  Tool = -> Extrude039
FEATURE [Part::Feature] Face095 .. Face098  x4 (patterned run collapsed; names and placements below)
  shape: bbox 3.5 x 17.8 x 2e-07 mm, 1 faces, 0 solids (baked)
FEATURE [Part::Revolution] Revolve103  label="removeToCreateScrewAndThreadedInsertHole030"
  Angle = 360
  Axis = (0,1,0)
  Base = (0,0,0)
  FaceMakerClass = Part::FaceMakerBullseye
  Placement = pos=(62.3,30.3,19.7) rot=(0,0,1;0rad)
  Solid = false
  Source = -> Face095
  Symmetric = false
FEATURE [Part::Revolution] Revolve104  label="removeToCreateScrewAndThreadedInsertHole031"
  Angle = 360
  Axis = (0,1,0)
  Base = (0,0,0)
  FaceMakerClass = Part::FaceMakerBullseye
  Placement = pos=(62.3,30.3,51.7) rot=(0,0,1;0rad)
  Solid = false
  Source = -> Face096
  Symmetric = false
FEATURE [Part::Revolution] Revolve105  label="removeToCreateScrewAndThreadedInsertHole032"
  Angle = 360
  Axis = (0,1,0)
  Base = (0,0,0)
  FaceMakerClass = Part::FaceMakerBullseye
  Placement = pos=(30.3,30.3,19.7) rot=(0,0,1;0rad)
  Solid = false
  Source = -> Face097
  Symmetric = false
FEATURE [Part::Revolution] Revolve106  label="removeToCreateScrewAndThreadedInsertHole033"
  Angle = 360
  Axis = (0,1,0)
  Base = (0,0,0)
  FaceMakerClass = Part::FaceMakerBullseye
  Placement = pos=(30.3,30.3,51.7) rot=(0,0,1;0rad)
  Solid = false
  Source = -> Face098
  Symmetric = false
FEATURE [Part::MultiFuse] Fusion069  label="createThreadedInsertHolesForFan003"
  Shapes = -> [Revolve103,Revolve104,Revolve105,Revolve106]
FEATURE [Part::Cut] Cut029  label="top015"
  Base = -> Cut028
  Tool = -> Fusion054
FEATURE [Part::Cut] Cut030  label="fanScrewHousing005"
  Base = -> Cut027
  Tool = -> Fusion069
FEATURE [Part::Cylinder] Cylinder026  label="removeToCreteHoleForPlugHousing010"
  Angle = 360
  AttacherType = Attacher::AttachEngine3D
  Height = 20
  Placement = pos=(-2,19,36) rot=(0,1,0;1.5708rad)
  Radius = 14.3
FEATURE [Part::Box] Box018  label="removeToCreteHoleForPlugHousing011"
  AttacherType = Attacher::AttachEngine3D
  Height = 28.6
  Length = 10
  Placement = pos=(-2,0,21.7) rot=(0,0,1;0rad)
  Width = 19
FEATURE [Part::Box] Box019  label="wireHolderBottomCaseBit"
  AttacherType = Attacher::AttachEngine3D
  Height = 28
  Length = 3
  Placement = pos=(0,0,22) rot=(0,0,1;0rad)
  Width = 21
FEATURE [Part::Cylinder] Cylinder027  label="removeToCreteHoleForPlugHousing012"
  Angle = 360
  AttacherType = Attacher::AttachEngine3D
  Height = 20
  Placement = pos=(-2,19,36) rot=(0,1,0;1.5708rad)
  Radius = 14.3
FEATURE [Part::Cut] Cut031  label="wireHolderBottomCaseBit001"
  Base = -> Box019
  Tool = -> Cylinder027
FEATURE [Part::MultiFuse] Fusion070  label="removeToCreteHoleForPlugHousing013"
  Shapes = -> [Box018,Cylinder026]
FEATURE [Part::Cut] Cut032  label="top016"
  Base = -> Cut029
  Tool = -> Fusion070
FEATURE [Part::Cylinder] Cylinder028
  Angle = 360
  AttacherType = Attacher::AttachEngine3D
  Height = 20
  Placement = pos=(0,0,36.15) rot=(0,0,1;0rad)
  Radius = 14.3
FEATURE [Part::Cylinder] Cylinder029
  Angle = 360
  AttacherType = Attacher::AttachEngine3D
  Height = 10
  Placement = pos=(0,0,36.15) rot=(0,0,1;0rad)
  Radius = 4
FEATURE [Part::MultiFuse] Fusion071  label="removeToCreteHoleForPlugHousing014"
  Placement = pos=(70,19,36) rot=(0,1,0;1.5708rad)
  Shapes = -> [Cylinder028,Cylinder029]
FEATURE [Sketcher::SketchObject] Sketch049  label="topSketch011"
  FullyConstrained = true
  sketch-geometry (4):
    g0: ArcOfCircle CenterX=105 CenterY=19 CenterZ=0 NormalX=0 NormalY=0 NormalZ=1 AngleXU=0 Radius=20.6155 StartAngle=5.54125 EndAngle=6.28319
    g1: ArcOfCircle CenterX=105 CenterY=19 CenterZ=0 NormalX=0 NormalY=0 NormalZ=1 AngleXU=0 Radius=13 StartAngle=5.54125 EndAngle=6.28319
    g2: LineSegment StartX=118 StartY=19 StartZ=0 EndX=125.616 EndY=19 EndZ=0
    g3: LineSegment StartX=114.583 StartY=10.2157 StartZ=0 EndX=120.197 EndY=5.06982 EndZ=0
  constraints (7):
    c: Block(g0)
    c: Block(g1)
    c: Coincident(g2,g1)
    c: Coincident(g2,g0)
    c: Horizontal(g2)
    c: Coincident(g3,g1)
    c: Coincident(g3,g0)
FEATURE [Part::Box] Box020  label="removeToCreteHoleForPlugHousing015"
  AttacherType = Attacher::AttachEngine3D
  Height = 28.6
  Length = 20
  Placement = pos=(106.15,0,21.7) rot=(0,0,1;0rad)
  Width = 19
FEATURE [Part::MultiFuse] Fusion072  label="removeToCreteHoleForPlugHousing016"
  Shapes = -> [Box020,Fusion071]
FEATURE [Part::Cut] Cut033  label="removeToCreteHoleForPlugHousing017"
  Base = -> Cut032
  Tool = -> Fusion072
FEATURE [Part::Cylinder] Cylinder030
  Angle = 360
  AttacherType = Attacher::AttachEngine3D
  Height = 20
  Placement = pos=(0,0,36.15) rot=(0,0,1;0rad)
  Radius = 14.3
FEATURE [Part::Cylinder] Cylinder031
  Angle = 360
  AttacherType = Attacher::AttachEngine3D
  Height = 10
  Placement = pos=(0,0,36.15) rot=(0,0,1;0rad)
  Radius = 4
FEATURE [Part::Box] Box021  label="removeToCreteHoleForPlugHousing019"
  AttacherType = Attacher::AttachEngine3D
  Height = 28.6
  Length = 20
  Placement = pos=(106.15,0,21.7) rot=(0,0,1;0rad)
  Width = 19
FEATURE [Part::MultiFuse] Fusion074  label="removeToCreteHoleForPlugHousing020"
  Placement = pos=(70,19,36) rot=(0,1,0;1.5708rad)
  Shapes = -> [Cylinder030,Cylinder031]
FEATURE [Part::MultiFuse] Fusion073  label="removeToCreteHoleForPlugHousing018"
  Placement = pos=(0,0,28.3) rot=(0,0,1;0rad)
  Shapes = -> [Box021,Fusion074]
FEATURE [Part::Cylinder] Cylinder032
  Angle = 360
  AttacherType = Attacher::AttachEngine3D
  Height = 20
  Placement = pos=(0,0,36.15) rot=(0,0,1;0rad)
  Radius = 14.3
FEATURE [Part::Cylinder] Cylinder033
  Angle = 360
  AttacherType = Attacher::AttachEngine3D
  Height = 10
  Placement = pos=(0,0,36.15) rot=(0,0,1;0rad)
  Radius = 4
FEATURE [Part::Box] Box022  label="removeToCreteHoleForPlugHousing021"
  AttacherType = Attacher::AttachEngine3D
  Height = 28.6
  Length = 20
  Placement = pos=(106.15,0,21.7) rot=(0,0,1;0rad)
  Width = 19
FEATURE [Part::MultiFuse] Fusion076  label="removeToCreteHoleForPlugHousing023"
  Placement = pos=(70,19,36) rot=(0,1,0;1.5708rad)
  Shapes = -> [Cylinder032,Cylinder033]
FEATURE [Part::MultiFuse] Fusion075  label="removeToCreteHoleForPlugHousing022"
  Placement = pos=(0,0,-28.3) rot=(0,0,1;0rad)
  Shapes = -> [Box022,Fusion076]
FEATURE [Part::MultiFuse] Fusion077  label="removeToCreatePlugHousingBottomBit"
  Shapes = -> [Fusion075,Fusion073]
FEATURE [Part::Cylinder] Cylinder034
  Angle = 360
  AttacherType = Attacher::AttachEngine3D
  Height = 20
  Placement = pos=(0,0,36.15) rot=(0,0,1;0rad)
  Radius = 14
FEATURE [Part::Cylinder] Cylinder035
  Angle = 360
  AttacherType = Attacher::AttachEngine3D
  Height = 10
  Placement = pos=(0,0,36.15) rot=(0,0,1;0rad)
  Radius = 4
FEATURE [Part::MultiFuse] Fusion078  label="removeToCreteHoleForPlugHousing024"
  Placement = pos=(70,19,36) rot=(0,1,0;1.5708rad)
  Shapes = -> [Cylinder034,Cylinder035]
FEATURE [Part::MultiFuse] Fusion079  label="removeToCreatePlugHousingBottomBit001"
  Shapes = -> [Fusion078,Fusion077]
FEATURE [Part::Extrusion] Extrude040  label="bottomPlugHousingBit"
  Base = -> Sketch049
  Dir = (0,0,1)
  DirMode = 2
  FaceMakerClass = Part::FaceMakerBullseye
  LengthFwd = 72
  LengthRev = 0
  Solid = true
  Symmetric = false
FEATURE [Part::Cut] Cut034  label="bottomPlugHousingBit001"
  Base = -> Extrude040
  Placement = pos=(-0.09,0,0) rot=(0,0,1;0rad)
  Tool = -> Fusion079
FEATURE [Part::Box] Box023  label="Cube014"
  AttacherType = Attacher::AttachEngine3D
  Height = 16
  Length = 8
  Placement = pos=(12.7,31.52,28) rot=(0,0,1;0rad)
  Width = 4
FEATURE [Part::Cylinder] Cylinder036
  Angle = 360
  AttacherType = Attacher::AttachEngine3D
  Height = 10
  Placement = pos=(0,0,36.15) rot=(0,0,1;0rad)
  Radius = 4
FEATURE [Part::Cylinder] Cylinder037
  Angle = 360
  AttacherType = Attacher::AttachEngine3D
  Height = 20
  Placement = pos=(0,0,36.15) rot=(0,0,1;0rad)
  Radius = 8.2
FEATURE [Part::MultiFuse] Fusion080  label="removeToCreteHoleForPlugHousing025"
  Placement = pos=(-42,19,36) rot=(0,1,0;1.5708rad)
  Shapes = -> [Cylinder037,Cylinder036]
FEATURE [Sketcher::SketchObject] Sketch050  label="topSketch012"
  FullyConstrained = true
  sketch-geometry (4):
    g0: LineSegment StartX=16.8446 StartY=31.512 StartZ=0 EndX=16.3251 EndY=34.4666 EndZ=0
    g1: ArcOfCircle CenterX=19 CenterY=19.2524 CenterZ=0 NormalX=0 NormalY=0 NormalZ=1 AngleXU=0 Radius=15.4476 StartAngle=1.74483 EndAngle=2.72717
    g2: ArcOfCircle CenterX=19 CenterY=19.2524 CenterZ=0 NormalX=0 NormalY=0 NormalZ=1 AngleXU=0 Radius=12.4476 StartAngle=1.74483 EndAngle=2.73189
    g3: LineSegment StartX=4.86004 StartY=25.4725 StartZ=0 EndX=7.58253 EndY=24.2107 EndZ=0
  constraints (7):
    c: Block(g0)
    c: Coincident(g1,g0)
    c: Coincident(g2,g0)
    c: Coincident(g3,g1)
    c: Coincident(g3,g2)
    c: Block(g1)
    c: Block(g2)
FEATURE [Part::Extrusion] Extrude041
  Base = -> Sketch050
  Dir = (0,0,1)
  DirMode = 2
  FaceMakerClass = Part::FaceMakerBullseye
  LengthFwd = 10.6
  LengthRev = 0
  Placement = pos=(0,0,31) rot=(0,0,1;0rad)
  Solid = true
  Symmetric = false
FEATURE [Part::Cut] Cut035
  Base = -> Extrude041
  Placement = pos=(0,0,-0.3) rot=(0,0,1;0rad)
  Tool = -> Fusion080
FEATURE [Part::Cut] Cut036
  Base = -> Box023
  Tool = -> Cut035
FEATURE [Part::Fillet] Fillet027
  Base = -> Cut036
  Edges = 1 edges r=0.7: [Edge13]
FEATURE [Part::Fillet] Fillet028
  Base = -> Fillet027
  Edges = 1 edges r=0.7: [Edge13]
FEATURE [Part::Fillet] Fillet029
  Base = -> Fillet028
  Edges = 1 edges r=0.7: [Edge16]
FEATURE [Part::Fillet] Fillet030
  Base = -> Fillet029
  Edges = 1 edges r=0.7: [Edge11]
FEATURE [Part::Fillet] Fillet031
  Base = -> Fillet030
  Edges = 1 edges r=0.7: [Edge10]
FEATURE [Part::Fillet] Fillet032
  Base = -> Fillet031
  Edges = 1 edges r=1.2: [Edge5]
FEATURE [Part::Fillet] Fillet033
  Base = -> Fillet032
  Edges = 1 edges r=1.2: [Edge12]
FEATURE [Part::Fillet] Fillet034  label="wireHousingRetainer"
  Base = -> Fillet033
  Edges = 1 edges r=2: [Edge1]
  Placement = pos=(0.3,0,0) rot=(0,0,1;0rad)
FEATURE [Part::Feature] Face099
  shape: bbox 3.5 x 17.8 x 2e-07 mm, 1 faces, 0 solids (baked)
FEATURE [Part::Revolution] Revolve107  label="removeToCreateScrewAndThreadedInsertHole034"
  Angle = 360
  Axis = (0,1,0)
  Base = (0,0,0)
  FaceMakerClass = Part::FaceMakerBullseye
  Placement = pos=(12.5,0,10) rot=(0,0,1;0rad)
  Solid = false
  Source = -> Face099
  Symmetric = false
FEATURE [Part::Feature] Face100
  shape: bbox 3.5 x 17.8 x 2e-07 mm, 1 faces, 0 solids (baked)
FEATURE [Part::Revolution] Revolve108  label="removeToCreateScrewAndThreadedInsertHole035"
  Angle = 360
  Axis = (0,1,0)
  Base = (0,0,0)
  FaceMakerClass = Part::FaceMakerBullseye
  Placement = pos=(12.5,0,62) rot=(0,0,1;0rad)
  Solid = false
  Source = -> Face100
  Symmetric = false
FEATURE [Part::Feature] Face101
  shape: bbox 3.5 x 17.8 x 2e-07 mm, 1 faces, 0 solids (baked)
FEATURE [Part::Revolution] Revolve109  label="removeToCreateScrewAndThreadedInsertHole036"
  Angle = 360
  Axis = (0,1,0)
  Base = (0,0,0)
  FaceMakerClass = Part::FaceMakerBullseye
  Placement = pos=(89.5,0,68.5) rot=(0,0,1;0rad)
  Solid = false
  Source = -> Face101
  Symmetric = false
FEATURE [Part::Feature] Face102
  shape: bbox 3.5 x 17.8 x 2e-07 mm, 1 faces, 0 solids (baked)
FEATURE [Part::Revolution] Revolve110  label="removeToCreateScrewAndThreadedInsertHole037"
  Angle = 360
  Axis = (0,1,0)
  Base = (0,0,0)
  FaceMakerClass = Part::FaceMakerBullseye
  Placement = pos=(89.5,0,3.5) rot=(0,0,1;0rad)
  Solid = false
  Source = -> Face102
  Symmetric = false
FEATURE [Part::Feature] Face103
  shape: bbox 3.5 x 17.8 x 2e-07 mm, 1 faces, 0 solids (baked)
FEATURE [Part::Revolution] Revolve111  label="removeToCreateScrewAndThreadedInsertHole038"
  Angle = 360
  Axis = (0,1,0)
  Base = (0,0,0)
  FaceMakerClass = Part::FaceMakerBullseye
  Placement = pos=(109.5,4.7,3.5) rot=(0,0,1;0rad)
  Solid = false
  Source = -> Face103
  Symmetric = false
FEATURE [Part::Feature] Face104
  shape: bbox 3.5 x 17.8 x 2e-07 mm, 1 faces, 0 solids (baked)
FEATURE [Part::Revolution] Revolve112  label="removeToCreateScrewAndThreadedInsertHole039"
  Angle = 360
  Axis = (0,1,0)
  Base = (0,0,0)
  FaceMakerClass = Part::FaceMakerBullseye
  Placement = pos=(109.5,4.7,68.5) rot=(0,0,1;0rad)
  Solid = false
  Source = -> Face104
  Symmetric = false
FEATURE [Part::MultiFuse] Fusion081  label="removeToCreateScrewAndThreadedInsertHole040"
  Shapes = -> [Revolve107,Revolve108,Revolve109,Revolve110,Revolve111,Revolve112]
FEATURE [Part::MultiFuse] Fusion082  label="casePillars002"
  Shapes = -> [Revolve094,Revolve092,Revolve090,Revolve089,Revolve091,Revolve093]
FEATURE [Part::Cut] Cut037  label="casePillars003"
  Base = -> Fusion082
  Tool = -> Fusion081
FEATURE [Sketcher::SketchObject] Sketch051
  FullyConstrained = true
  Placement = pos=(117,19,0) rot=(0.57735,0.57735,0.57735;2.0944rad)
  sketch-geometry (48):
    g0: LineSegment StartX=-49.19 StartY=69.25 StartZ=0 EndX=-49.19 EndY=66.25 EndZ=0
    g1: LineSegment StartX=-49.19 StartY=63.5 StartZ=0 EndX=-49.19 EndY=60.5 EndZ=0
    g2: LineSegment StartX=-49.19 StartY=57.75 StartZ=0 EndX=-49.19 EndY=54.75 EndZ=0
    g3: LineSegment StartX=-49.19 StartY=52 StartZ=0 EndX=-49.19 EndY=49 EndZ=0
    g4: LineSegment StartX=-49.19 StartY=46.25 StartZ=0 EndX=-49.19 EndY=43.25 EndZ=0
    g5: LineSegment StartX=-49.19 StartY=40.5 StartZ=0 EndX=-49.19 EndY=37.5 EndZ=0
    g6: LineSegment StartX=-49.19 StartY=34.5 StartZ=0 EndX=-49.19 EndY=31.5 EndZ=0
    g7: LineSegment StartX=-49.19 StartY=28.75 StartZ=0 EndX=-49.19 EndY=25.75 EndZ=0
    g8: LineSegment StartX=-49.19 StartY=23 StartZ=0 EndX=-49.19 EndY=20 EndZ=0
    g9: LineSegment StartX=-49.19 StartY=17.25 StartZ=0 EndX=-49.19 EndY=14.25 EndZ=0
    g10: LineSegment StartX=-49.19 StartY=11.5 StartZ=0 EndX=-49.19 EndY=8.5 EndZ=0
    g11: LineSegment StartX=-49.19 StartY=5.75 StartZ=0 EndX=-49.19 EndY=2.75 EndZ=0
    g12: ArcOfCircle CenterX=-1.5 CenterY=67.75 CenterZ=0 NormalX=0 NormalY=0 NormalZ=1 AngleXU=0 Radius=1.5 StartAngle=4.71239 EndAngle=7.85398
    g13: ArcOfCircle CenterX=-1.5 CenterY=62 CenterZ=0 NormalX=0 NormalY=0 NormalZ=1 AngleXU=0 Radius=1.5 StartAngle=4.71239 EndAngle=7.85398
    g14: ArcOfCircle CenterX=-1.5 CenterY=56.25 CenterZ=0 NormalX=0 NormalY=0 NormalZ=1 AngleXU=0 Radius=1.5 StartAngle=4.71239 EndAngle=7.85398
    g15: ArcOfCircle CenterX=-11.49 CenterY=50.5 CenterZ=0 NormalX=0 NormalY=0 NormalZ=1 AngleXU=0 Radius=1.5 StartAngle=4.71239 EndAngle=7.85398
    g16: ArcOfCircle CenterX=-16.28 CenterY=44.75 CenterZ=0 NormalX=0 NormalY=0 NormalZ=1 AngleXU=0 Radius=1.5 StartAngle=4.71239 EndAngle=7.85398
    g17: ArcOfCircle CenterX=-18.2337 CenterY=39 CenterZ=0 NormalX=0 NormalY=0 NormalZ=1 AngleXU=0 Radius=1.5 StartAngle=4.71485 EndAngle=7.85398
    g18: ArcOfCircle CenterX=-16.2837 CenterY=27.25 CenterZ=0 NormalX=0 NormalY=0 NormalZ=1 AngleXU=0 Radius=1.5 StartAngle=4.71485 EndAngle=7.85398
    g19: ArcOfCircle CenterX=-18.2337 CenterY=33 CenterZ=0 NormalX=0 NormalY=0 NormalZ=1 AngleXU=0 Radius=1.5 StartAngle=4.71485 EndAngle=7.85398
    g20: ArcOfCircle CenterX=-11.49 CenterY=21.5 CenterZ=0 NormalX=0 NormalY=0 NormalZ=1 AngleXU=0 Radius=1.5 StartAngle=4.71239 EndAngle=7.85398
    g21: ArcOfCircle CenterX=-1.5 CenterY=4.25 CenterZ=0 NormalX=0 NormalY=0 NormalZ=1 AngleXU=0 Radius=1.5 StartAngle=4.71239 EndAngle=7.85398
    g22: ArcOfCircle CenterX=-1.5 CenterY=10 CenterZ=0 NormalX=0 NormalY=0 NormalZ=1 AngleXU=0 Radius=1.5 StartAngle=4.71239 EndAngle=7.85398
    g23: ArcOfCircle CenterX=-1.5 CenterY=15.75 CenterZ=0 NormalX=0 NormalY=0 NormalZ=1 AngleXU=0 Radius=1.5 StartAngle=4.71239 EndAngle=7.85398
    g24: LineSegment StartX=-49.19 StartY=69.25 StartZ=0 EndX=-1.5 EndY=69.25 EndZ=0
    g25: LineSegment StartX=-49.19 StartY=66.25 StartZ=0 EndX=-1.5 EndY=66.25 EndZ=0
    g26: LineSegment StartX=-49.19 StartY=63.5 StartZ=0 EndX=-1.5 EndY=63.5 EndZ=0
    g27: LineSegment StartX=-49.19 StartY=60.5 StartZ=0 EndX=-1.5 EndY=60.5 EndZ=0
    g28: LineSegment StartX=-49.19 StartY=57.75 StartZ=0 EndX=-1.5 EndY=57.75 EndZ=0
    g29: LineSegment StartX=-49.19 StartY=54.75 StartZ=0 EndX=-1.5 EndY=54.75 EndZ=0
    g30: LineSegment StartX=-49.19 StartY=52 StartZ=0 EndX=-11.49 EndY=52 EndZ=0
    g31: LineSegment StartX=-49.19 StartY=49 StartZ=0 EndX=-11.49 EndY=49 EndZ=0
    g32: LineSegment StartX=-49.19 StartY=46.25 StartZ=0 EndX=-16.28 EndY=46.25 EndZ=0
    g33: LineSegment StartX=-49.19 StartY=43.25 StartZ=0 EndX=-16.28 EndY=43.25 EndZ=0
    g34: LineSegment StartX=-49.19 StartY=40.5 StartZ=0 EndX=-18.2337 EndY=40.5 EndZ=0
    g35: LineSegment StartX=-49.19 StartY=37.5 StartZ=0 EndX=-18.23 EndY=37.5 EndZ=0
    g36: LineSegment StartX=-49.19 StartY=34.5 StartZ=0 EndX=-18.2337 EndY=34.5 EndZ=0
    g37: LineSegment StartX=-49.19 StartY=31.5 StartZ=0 EndX=-18.23 EndY=31.5 EndZ=0
    g38: LineSegment StartX=-49.19 StartY=28.75 StartZ=0 EndX=-16.2837 EndY=28.75 EndZ=0
    g39: LineSegment StartX=-49.19 StartY=25.75 StartZ=0 EndX=-16.28 EndY=25.75 EndZ=0
    g40: LineSegment StartX=-49.19 StartY=23 StartZ=0 EndX=-11.49 EndY=23 EndZ=0
    g41: LineSegment StartX=-49.19 StartY=20 StartZ=0 EndX=-11.49 EndY=20 EndZ=0
    g42: LineSegment StartX=-49.19 StartY=17.25 StartZ=0 EndX=-1.5 EndY=17.25 EndZ=0
    g43: LineSegment StartX=-49.19 StartY=14.25 StartZ=0 EndX=-1.5 EndY=14.25 EndZ=0
    g44: LineSegment StartX=-49.19 StartY=11.5 StartZ=0 EndX=-1.5 EndY=11.5 EndZ=0
    g45: LineSegment StartX=-49.19 StartY=8.5 StartZ=0 EndX=-1.5 EndY=8.5 EndZ=0
    g46: LineSegment StartX=-49.19 StartY=5.75 StartZ=0 EndX=-1.5 EndY=5.75 EndZ=0
    g47: LineSegment StartX=-49.19 StartY=2.75 StartZ=0 EndX=-1.5 EndY=2.75 EndZ=0
  constraints (120):
    c: Vertical(g0)
    c: Distance(g0) = 3
    c: Block(g0)
    c: Vertical(g1)
    c: Distance(g1) = 3
    c: Vertical(g2)
    c: Equal(g0,g2) = 3
    c: Block(g2)
    c: Vertical(g3)
    c: Equal(g1,g3) = 3
    c: Vertical(g4)
    c: Equal(g0,g4) = 3
    c: Block(g4)
    c: Vertical(g5)
    c: Equal(g1,g5) = 3
    c: Vertical(g6)
    c: Equal(g0,g6) = 3
    c: Block(g6)
    c: Vertical(g7)
    c: Equal(g1,g7) = 3
    c: Vertical(g8)
    c: Equal(g0,g8) = 3
    c: Block(g8)
    c: Vertical(g9)
    c: Equal(g1,g9) = 3
    c: Vertical(g10)
    c: Equal(g0,g10) = 3
    c: Block(g10)
    c: Vertical(g11)
    c: Equal(g1,g11) = 3
    c: Block(g12)
    c: Block(g13)
    c: Block(g14)
    c: Block(g15)
    c: Block(g16)
    c: Block(g17)
    c: Block(g18)
    c: Block(g19)
    c: Block(g20)
    c: Block(g21)
    c: Block(g22)
    c: Block(g23)
    c: Block(g11)
    c: Block(g9)
    c: Block(g7)
    c: Block(g5)
    c: Block(g3)
    c: Block(g1)
    c: Coincident(g24,g0)
    c: Coincident(g24,g12)
    c: Horizontal(g24)
    c: Coincident(g25,g0)
    c: Coincident(g25,g12)
    c: Horizontal(g25)
    c: Coincident(g26,g1)
    c: Coincident(g26,g13)
    c: Horizontal(g26)
    c: Coincident(g27,g1)
    c: Coincident(g27,g13)
    c: Horizontal(g27)
    c: Coincident(g28,g2)
    c: Coincident(g28,g14)
    c: Horizontal(g28)
    c: Coincident(g29,g2)
    c: Coincident(g29,g14)
    c: Horizontal(g29)
    c: Coincident(g30,g3)
    c: Coincident(g30,g15)
    c: Horizontal(g30)
    c: Coincident(g31,g3)
    c: Coincident(g31,g15)
    c: Horizontal(g31)
    c: Coincident(g32,g4)
    c: Coincident(g32,g16)
    c: Horizontal(g32)
    c: Coincident(g33,g4)
    c: Coincident(g33,g16)
    c: Horizontal(g33)
    c: Coincident(g34,g5)
    c: Coincident(g34,g17)
    c: Horizontal(g34)
    c: Coincident(g35,g5)
    c: Coincident(g35,g17)
    c: Horizontal(g35)
    c: Coincident(g36,g6)
    c: Coincident(g36,g19)
    c: Horizontal(g36)
    c: Coincident(g37,g6)
    c: Coincident(g37,g19)
    c: Horizontal(g37)
    c: Coincident(g38,g7)
    c: Coincident(g38,g18)
    c: Horizontal(g38)
    c: Coincident(g39,g7)
    c: Coincident(g39,g18)
    c: Horizontal(g39)
    c: Coincident(g40,g8)
    c: Coincident(g40,g20)
    c: Horizontal(g40)
    c: Coincident(g41,g8)
    c: Coincident(g41,g20)
    c: Horizontal(g41)
    c: Coincident(g42,g9)
    c: Coincident(g42,g23)
    c: Horizontal(g42)
    c: Coincident(g43,g9)
    c: Coincident(g43,g23)
    c: Horizontal(g43)
    c: Coincident(g44,g10)
    c: Coincident(g44,g22)
    c: Horizontal(g44)
    c: Coincident(g45,g10)
    c: Coincident(g45,g22)
    c: Horizontal(g45)
    c: Coincident(g46,g11)
    c: Coincident(g46,g21)
    c: Horizontal(g46)
    c: Coincident(g47,g11)
    c: Coincident(g47,g21)
    c: Horizontal(g47)
FEATURE [Part::Extrusion] Extrude042
  Base = -> Sketch051
  Dir = (1,-2e-16,2e-16)
  DirMode = 2
  FaceMakerClass = Part::FaceMakerBullseye
  LengthFwd = 19
  LengthRev = 0
  Placement = pos=(-19,0,0) rot=(0,0,1;0rad)
  Solid = true
  Symmetric = false
FEATURE [Part::Fillet] Fillet035  label="removeToCreateVentalationHoles"
  Base = -> Extrude042
  Edges = <same value as first occurrence — deduplicated (x6 in doc)>
  Placement = pos=(7,0,0) rot=(0,0,1;0rad)
FEATURE [Part::Cut] Cut038  label="top017"
  Base = -> Cut033
  Tool = -> Fillet035
FEATURE [Sketcher::SketchObject] Sketch052  label="bottomSketch001"
  FullyConstrained = true
  sketch-geometry (45):
    g0: LineSegment StartX=6.29999 StartY=8 StartZ=0 EndX=3.29999 EndY=8 EndZ=0
    g1: LineSegment StartX=3.29999 StartY=8 StartZ=0 EndX=3.29999 EndY=-6.03275e-07 EndZ=0
    g2: ArcOfCircle CenterX=8.29999 CenterY=5 CenterZ=0 NormalX=0 NormalY=0 NormalZ=1 AngleXU=0 Radius=2 StartAngle=3.14159 EndAngle=4.71239
    g3: LineSegment StartX=6.29999 StartY=8 StartZ=0 EndX=6.29999 EndY=5 EndZ=0
    g4: ArcOfCircle CenterX=105 CenterY=19 CenterZ=0 NormalX=0 NormalY=0 NormalZ=1 AngleXU=0 Radius=12.7 StartAngle=4.71239 EndAngle=5.94289
    g5-g11: Circle x7 (B-spline internal-alignment scaffolding for g12; pole/knot coordinates omitted)
    g12: BSplineCurve PolesCount=7 KnotsCount=5 Degree=3 IsPeriodic=0
    g13-g17: GeomPoint x5 (B-spline internal-alignment scaffolding for g12; pole/knot coordinates omitted)
    g18: ArcOfCircle CenterX=105 CenterY=19 CenterZ=0 NormalX=0 NormalY=0 NormalZ=1 AngleXU=0 Radius=15.7 StartAngle=5.81226 EndAngle=6.28319
    g19: BSplineCurve PolesCount=5 KnotsCount=3 Degree=3 IsPeriodic=0
    g20: LineSegment StartX=8.29999 StartY=3 StartZ=0 EndX=101.7 EndY=3 EndZ=0
    g21: LineSegment StartX=3.29999 StartY=-6.03275e-07 StartZ=0 EndX=105 EndY=-6.03275e-07 EndZ=0
    g22: LineSegment StartX=120.974 StartY=8.71251 StartZ=0 EndX=122.332 EndY=7.83778 EndZ=0
    g23: LineSegment StartX=105 StartY=-6.03274e-07 StartZ=0 EndX=113 EndY=-6.03274e-07 EndZ=0
    g24: ArcOfCircle CenterX=105 CenterY=19 CenterZ=0 NormalX=0 NormalY=0 NormalZ=1 AngleXU=0 Radius=20.6155 StartAngle=5.11091 EndAngle=5.71103
    g25: ArcOfCircle CenterX=117.7 CenterY=19 CenterZ=0 NormalX=0 NormalY=0 NormalZ=1 AngleXU=0 Radius=3 StartAngle=1.2e-15 EndAngle=2.10468
    g26: Circle CenterX=116.345 CenterY=16.3232 CenterZ=0 NormalX=0 NormalY=0 NormalZ=1 AngleXU=0 Radius=1
    g27: Circle CenterX=117.24 CenterY=15.7584 CenterZ=0 NormalX=0 NormalY=0 NormalZ=1 AngleXU=0 Radius=1
    g28: Circle CenterX=116.972 CenterY=14.7612 CenterZ=0 NormalX=0 NormalY=0 NormalZ=1 AngleXU=0 Radius=1
    g29: BSplineCurve PolesCount=3 KnotsCount=2 Degree=2 IsPeriodic=0
    g30: GeomPoint X=116.345 Y=16.3232 Z=0
    g31: GeomPoint X=116.972 Y=14.7612 Z=0
    g32: Circle CenterX=115.828 CenterY=17.157 CenterZ=0 NormalX=0 NormalY=0 NormalZ=1 AngleXU=0 Radius=1
    g33: Circle CenterX=115.841 CenterY=16.639 CenterZ=0 NormalX=0 NormalY=0 NormalZ=1 AngleXU=0 Radius=1
    g34: Circle CenterX=116.345 CenterY=16.3232 CenterZ=0 NormalX=0 NormalY=0 NormalZ=1 AngleXU=0 Radius=1
    g35: BSplineCurve PolesCount=3 KnotsCount=2 Degree=2 IsPeriodic=0
    g36: GeomPoint X=115.828 Y=17.157 Z=0
    g37: GeomPoint X=116.345 Y=16.3232 Z=0
    g38: LineSegment StartX=115.828 StartY=17.157 StartZ=0 EndX=115.828 EndY=20.8307 EndZ=0
    g39: Circle CenterX=115.828 CenterY=20.8307 CenterZ=0 NormalX=0 NormalY=0 NormalZ=1 AngleXU=0 Radius=1
    g40: Circle CenterX=115.831 CenterY=21.3396 CenterZ=0 NormalX=0 NormalY=0 NormalZ=1 AngleXU=0 Radius=1
    g41: Circle CenterX=116.173 CenterY=21.5825 CenterZ=0 NormalX=0 NormalY=0 NormalZ=1 AngleXU=0 Radius=1
    g42: BSplineCurve PolesCount=3 KnotsCount=2 Degree=2 IsPeriodic=0
    g43: GeomPoint X=115.828 Y=20.8307 Z=0
    g44: GeomPoint X=116.173 Y=21.5825 Z=0
  constraints (70):
    c: Horizontal(g0)
    c: Distance(g0) = 3
    c: Coincident(g1,g0)
    c: Vertical(g1)
    c: Block(g2)
    c: Block(g0)
    c: Coincident(g3,g0)
    c: Coincident(g3,g2)
    c: Vertical(g3)
    c: Block(g1)
    c: Block(g4)
    c: Coincident(g19,g4)
    c: Block(g19)
    c: Equal(g5, g6-g11) x6
    c: InternalAlignment(g5-g11 -> g12) x7
    c: InternalAlignment(g13-g17 -> g12) x5
    c: Block(g12)
    c: Coincident(g18,g12)
    c: Block(g18)
    c: Coincident(g20,g2)
    c: Coincident(g20,g19)
    c: Horizontal(g20)
    c: Distance(g20) = 93.4
    c: Coincident(g21,g1)
    c: Horizontal(g21)
    c: Distance(g21) = 101.7
    c: Horizontal(g23)
    c: Distance(g23) = 8
    c: Coincident(g24,g23)
    c: Block(g23)
    c: Coincident(g22,g24)
    c: Block(g24)
    c: Block(g22)
    c: Distance(g22) = 1.61553
    c: Coincident(g25,g18)
    c: Block(g25)
    c: Weight(g26) = 1
    c: Equal(g26,g27)
    c: Equal(g26,g28)
    c: Coincident(g29,g4)
    c: InternalAlignment(g26,g29)
    c: InternalAlignment(g27,g29)
    c: InternalAlignment(g28,g29)
    c: InternalAlignment(g30,g29)
    c: InternalAlignment(g31,g29)
    c: Block(g29)
    c: Weight(g32) = 1
    c: Equal(g32,g33)
    c: Equal(g32,g34)
    c: Coincident(g35,g29)
    c: InternalAlignment(g32,g35)
    c: InternalAlignment(g33,g35)
    c: InternalAlignment(g34,g35)
    c: InternalAlignment(g36,g35)
    c: InternalAlignment(g37,g35)
    c: Block(g35)
    c: Coincident(g38,g35)
    c: Vertical(g38)
    c: Block(g38)
    c: Coincident(g42,g38)
    c: Weight(g39) = 1
    c: Equal(g39,g40)
    c: Equal(g39,g41)
    c: Coincident(g42,g25)
    c: InternalAlignment(g39,g42)
    c: InternalAlignment(g40,g42)
    c: InternalAlignment(g41,g42)
    c: InternalAlignment(g43,g42)
    c: InternalAlignment(g44,g42)
    c: Block(g42)
FEATURE [Part::Extrusion] Extrude043  label="bottom010"
  Base = -> Sketch052
  Dir = (0,0,1)
  DirMode = 2
  FaceMakerClass = Part::FaceMakerBullseye
  LengthFwd = 71.4
  LengthRev = 0
  Placement = pos=(0,0,0.3) rot=(0,0,1;0rad)
  Solid = true
  Symmetric = false
FEATURE [Sketcher::SketchObject] Sketch053  label="topSketch013"
  FullyConstrained = true
  sketch-geometry (22):
    g0: LineSegment StartX=5.21097e-06 StartY=3 StartZ=0 EndX=5.21097e-06 EndY=19 EndZ=0
    g1: ArcOfCircle CenterX=19 CenterY=19 CenterZ=0 NormalX=0 NormalY=0 NormalZ=1 AngleXU=0 Radius=19 StartAngle=1.5708 EndAngle=3.14159
    g2: ArcOfCircle CenterX=19 CenterY=19 CenterZ=0 NormalX=0 NormalY=0 NormalZ=1 AngleXU=0 Radius=16 StartAngle=1.5708 EndAngle=3.14159
    g3: LineSegment StartX=114 StartY=35 StartZ=0 EndX=19 EndY=35 EndZ=0
    g4: LineSegment StartX=5.21097e-06 StartY=3 StartZ=0 EndX=5.21097e-06 EndY=0 EndZ=0
    g5: LineSegment StartX=3 StartY=0 StartZ=0 EndX=5.21097e-06 EndY=0 EndZ=0
    g6: LineSegment StartX=3 StartY=19 StartZ=0 EndX=3 EndY=0 EndZ=0
    g7: LineSegment StartX=19 StartY=38 StartZ=0 EndX=124 EndY=38 EndZ=0
    g8: Circle CenterX=119 CenterY=35 CenterZ=0 NormalX=0 NormalY=0 NormalZ=1 AngleXU=0 Radius=1
    g9: Circle CenterX=121 CenterY=35 CenterZ=0 NormalX=0 NormalY=0 NormalZ=1 AngleXU=0 Radius=1
    g10: Circle CenterX=121 CenterY=33 CenterZ=0 NormalX=0 NormalY=0 NormalZ=1 AngleXU=0 Radius=1
    g11: BSplineCurve PolesCount=3 KnotsCount=2 Degree=2 IsPeriodic=0
    g12: GeomPoint X=119 Y=35 Z=0
    g13: GeomPoint X=121 Y=33 Z=0
    g14: LineSegment StartX=119 StartY=35 StartZ=0 EndX=114 EndY=35 EndZ=0
    g15: ArcOfCircle CenterX=105 CenterY=19 CenterZ=0 NormalX=0 NormalY=0 NormalZ=1 AngleXU=0 Radius=16 StartAngle=5.60905 EndAngle=6.28319
    g16: LineSegment StartX=121 StartY=33 StartZ=0 EndX=121 EndY=19 EndZ=0
    g17: LineSegment StartX=117.5 StartY=9.01251 StartZ=0 EndX=121.163 EndY=9.0125 EndZ=0
    g18: ArcOfCircle CenterX=105 CenterY=19 CenterZ=0 NormalX=0 NormalY=0 NormalZ=1 AngleXU=0 Radius=20.6155 StartAngle=5.7297 EndAngle=6.28319
    g19: LineSegment StartX=121.163 StartY=9.0125 StartZ=0 EndX=122.538 EndY=8.16329 EndZ=0
    g20: LineSegment StartX=124 StartY=38 StartZ=0 EndX=125.616 EndY=38 EndZ=0
    g21: LineSegment StartX=125.616 StartY=19 StartZ=0 EndX=125.616 EndY=38 EndZ=0
  constraints (50):
    c: Vertical(g0)
    c: Block(g0)
    c: Coincident(g1,g0)
    c: Block(g1)
    c: Coincident(g2,g1)
    c: Block(g2)
    c: Coincident(g3,g2)
    c: Horizontal(g3)
    c: Tangent(g3,g2)
    c: Coincident(g4,g0)
    c: Distance(g4) = 3
    c: Vertical(g4)
    c: Coincident(g5,g4)
    c: Horizontal(g5)
    c: Coincident(g6,g2)
    c: Coincident(g6,g5)
    c: Vertical(g6)
    c: Horizontal(g7)
    c: Distance(g7) = 105
    c: Coincident(g7,g1)
    c: Block(g3)
    c: Weight(g8) = 1
    c: Equal(g8,g9)
    c: Equal(g8,g10)
    c: InternalAlignment(g8,g11)
    c: InternalAlignment(g9,g11)
    c: InternalAlignment(g10,g11)
    c: InternalAlignment(g12,g11)
    c: InternalAlignment(g13,g11)
    c: Block(g11)
    c: Coincident(g14,g11)
    c: Coincident(g14,g3)
    c: Horizontal(g14)
    c: Block(g15)
    c: Coincident(g16,g11)
    c: Coincident(g16,g15)
    c: Vertical(g16)
    c: Distance(g16) = 14
    c: Coincident(g17,g15)
    c: Block(g18)
    c: Coincident(g19,g18)
    c: Coincident(g20,g7)
    c: Horizontal(g20)
    c: Vertical(g21)
    c: Coincident(g20,g21)
    c: Block(g20)
    c: Block(g21)
    c: Block(g19)
    c: Block(g17)
    c: Distance(g20) = 1.61553
FEATURE [Part::Extrusion] Extrude044
  Base = -> Sketch053
  Dir = (0,0,1)
  DirMode = 2
  FaceMakerClass = Part::FaceMakerBullseye
  LengthFwd = 72
  LengthRev = 0
  Solid = true
  Symmetric = false
FEATURE [Part::Fillet] Fillet036  label="top018"
  Base = -> Extrude044
  Edges = 1 edges r=2: [Edge41]
FEATURE [Sketcher::SketchObject] Sketch054
  FullyConstrained = false
  Placement = pos=(0,0,0) rot=(1,0,0;1.5708rad)
  sketch-geometry (24):
    g0: ArcOfCircle CenterX=-4 CenterY=-10.5 CenterZ=0 NormalX=0 NormalY=0 NormalZ=1 AngleXU=0 Radius=1.5 StartAngle=6e-16 EndAngle=3.14159
    g1: ArcOfCircle CenterX=-34.2 CenterY=-10.5 CenterZ=0 NormalX=0 NormalY=0 NormalZ=1 AngleXU=0 Radius=1.5 StartAngle=0 EndAngle=3.14159
    g2: ArcOfCircle CenterX=-34.2 CenterY=-27.7 CenterZ=0 NormalX=0 NormalY=0 NormalZ=1 AngleXU=0 Radius=1.5 StartAngle=3.14159 EndAngle=6.28319
    g3: ArcOfCircle CenterX=-4 CenterY=-27.7 CenterZ=0 NormalX=0 NormalY=0 NormalZ=1 AngleXU=0 Radius=1.5 StartAngle=3.1416 EndAngle=6.28319
    g4: ArcOfCircle CenterX=-10 CenterY=-4.3 CenterZ=0 NormalX=0 NormalY=0 NormalZ=1 AngleXU=0 Radius=1.5 StartAngle=2e-16 EndAngle=3.14159
    g5: ArcOfCircle CenterX=-16.1 CenterY=-1.8 CenterZ=0 NormalX=0 NormalY=0 NormalZ=1 AngleXU=0 Radius=1.5 StartAngle=5e-16 EndAngle=3.14159
    g6: ArcOfCircle CenterX=-22.1 CenterY=-1.8 CenterZ=0 NormalX=0 NormalY=0 NormalZ=1 AngleXU=0 Radius=1.5 StartAngle=5e-16 EndAngle=3.14159
    g7: ArcOfCircle CenterX=-28.2 CenterY=-4.3 CenterZ=0 NormalX=0 NormalY=0 NormalZ=1 AngleXU=0 Radius=1.5 StartAngle=2e-16 EndAngle=3.14159
    g8: ArcOfCircle CenterX=-10 CenterY=-33.9 CenterZ=0 NormalX=0 NormalY=0 NormalZ=1 AngleXU=0 Radius=1.5 StartAngle=3.14159 EndAngle=6.28319
    g9: ArcOfCircle CenterX=-16.1 CenterY=-36.4 CenterZ=0 NormalX=0 NormalY=0 NormalZ=1 AngleXU=0 Radius=1.5 StartAngle=3.14159 EndAngle=6.28319
    g10: ArcOfCircle CenterX=-22.1 CenterY=-36.4 CenterZ=0 NormalX=0 NormalY=0 NormalZ=1 AngleXU=0 Radius=1.5 StartAngle=3.14159 EndAngle=6.28319
    g11: ArcOfCircle CenterX=-28.2 CenterY=-33.9 CenterZ=0 NormalX=0 NormalY=0 NormalZ=1 AngleXU=0 Radius=1.5 StartAngle=3.14159 EndAngle=6.28319
    g12: LineSegment StartX=-35.7 StartY=-10.5 StartZ=0 EndX=-35.7 EndY=-27.7 EndZ=0
    g13: LineSegment StartX=-32.7 StartY=-10.5 StartZ=0 EndX=-32.7 EndY=-27.7 EndZ=0
    g14: LineSegment StartX=-29.7 StartY=-33.9 StartZ=0 EndX=-29.7 EndY=-4.3 EndZ=0
    g15: LineSegment StartX=-26.7 StartY=-33.9 StartZ=0 EndX=-26.7 EndY=-4.3 EndZ=0
    g16: LineSegment StartX=-2.5 StartY=-10.5 StartZ=0 EndX=-2.5 EndY=-27.7 EndZ=0
    g17: LineSegment StartX=-8.5 StartY=-4.3 StartZ=0 EndX=-8.5 EndY=-33.9 EndZ=0
    g18: LineSegment StartX=-5.5 StartY=-10.5 StartZ=0 EndX=-5.5 EndY=-27.7 EndZ=0
    g19: LineSegment StartX=-11.5 StartY=-4.3 StartZ=0 EndX=-11.5 EndY=-33.9 EndZ=0
    g20: LineSegment StartX=-14.6 StartY=-1.8 StartZ=0 EndX=-14.6 EndY=-36.4 EndZ=0
    g21: LineSegment StartX=-17.6 StartY=-1.8 StartZ=0 EndX=-17.6 EndY=-36.4 EndZ=0
    g22: LineSegment StartX=-20.6 StartY=-36.4 StartZ=0 EndX=-20.6 EndY=-1.8 EndZ=0
    g23: LineSegment StartX=-23.6 StartY=-1.8 StartZ=0 EndX=-23.6 EndY=-36.4 EndZ=0
  constraints (48):
    c: Block(g0)
    c: Block(g1)
    c: Block(g2)
    c: Block(g3)
    c: Block(g4)
    c: Block(g5)
    c: Block(g6)
    c: Block(g7)
    c: Block(g8)
    c: Block(g9)
    c: Block(g10)
    c: Block(g11)
    c: Coincident(g12,g1)
    c: Coincident(g12,g2)
    c: Vertical(g12)
    c: Coincident(g13,g1)
    c: Coincident(g13,g2)
    c: Vertical(g13)
    c: Coincident(g14,g11)
    c: Coincident(g14,g7)
    c: Vertical(g14)
    c: Coincident(g15,g11)
    c: Coincident(g15,g7)
    c: Vertical(g15)
    c: Coincident(g16,g0)
    c: Coincident(g16,g3)
    c: Vertical(g16)
    c: Coincident(g17,g4)
    c: Coincident(g17,g8)
    c: Vertical(g17)
    c: Coincident(g18,g0)
    c: Coincident(g18,g3)
    c: Vertical(g18)
    c: Coincident(g19,g4)
    c: Coincident(g19,g8)
    c: Vertical(g19)
    c: Coincident(g20,g5)
    c: Coincident(g20,g9)
    c: Vertical(g20)
    c: Coincident(g21,g5)
    c: Coincident(g21,g9)
    c: Vertical(g21)
    c: Coincident(g22,g10)
    c: Coincident(g22,g6)
    c: Vertical(g22)
    c: Coincident(g23,g6)
    c: Coincident(g23,g10)
    c: Vertical(g23)
FEATURE [Part::Extrusion] Extrude045  label="removeToCreateFanGrillHoles003"
  Base = -> Sketch054
  Dir = (0,-1,6e-16)
  DirMode = 2
  FaceMakerClass = Part::FaceMakerBullseye
  LengthFwd = 10
  LengthRev = 0
  Placement = pos=(65.4,44,54.82) rot=(0,0,1;0rad)
  Solid = true
  Symmetric = false
FEATURE [Part::Feature] Face105 .. Face108  x4 (patterned run collapsed; names and placements below)
  shape: bbox 3.5 x 17.8 x 2e-07 mm, 1 faces, 0 solids (baked)
FEATURE [Part::Revolution] Revolve113  label="removeToCreateScrewAndThreadedInsertHole041"
  Angle = 360
  Axis = (0,1,0)
  Base = (0,0,0)
  FaceMakerClass = Part::FaceMakerBullseye
  Placement = pos=(62.3,30.3,19.7) rot=(0,0,1;0rad)
  Solid = false
  Source = -> Face105
  Symmetric = false
FEATURE [Part::Revolution] Revolve114  label="removeToCreateScrewAndThreadedInsertHole042"
  Angle = 360
  Axis = (0,1,0)
  Base = (0,0,0)
  FaceMakerClass = Part::FaceMakerBullseye
  Placement = pos=(62.3,30.3,51.7) rot=(0,0,1;0rad)
  Solid = false
  Source = -> Face106
  Symmetric = false
FEATURE [Part::Revolution] Revolve115  label="removeToCreateScrewAndThreadedInsertHole043"
  Angle = 360
  Axis = (0,1,0)
  Base = (0,0,0)
  FaceMakerClass = Part::FaceMakerBullseye
  Placement = pos=(30.3,30.3,19.7) rot=(0,0,1;0rad)
  Solid = false
  Source = -> Face107
  Symmetric = false
FEATURE [Part::Revolution] Revolve116  label="removeToCreateScrewAndThreadedInsertHole044"
  Angle = 360
  Axis = (0,1,0)
  Base = (0,0,0)
  FaceMakerClass = Part::FaceMakerBullseye
  Placement = pos=(30.3,30.3,51.7) rot=(0,0,1;0rad)
  Solid = false
  Source = -> Face108
  Symmetric = false
FEATURE [Part::MultiFuse] Fusion083  label="createThreadedInsertHolesForFan004"
  Shapes = -> [Revolve113,Revolve114,Revolve115,Revolve116]
FEATURE [Part::Box] Box024  label="removeToCreteHoleForPlugHousing026"
  AttacherType = Attacher::AttachEngine3D
  Height = 28.6
  Length = 10
  Placement = pos=(-2,0,21.7) rot=(0,0,1;0rad)
  Width = 19
FEATURE [Part::Cylinder] Cylinder038  label="removeToCreteHoleForPlugHousing027"
  Angle = 360
  AttacherType = Attacher::AttachEngine3D
  Height = 20
  Placement = pos=(-2,19,36) rot=(0,1,0;1.5708rad)
  Radius = 14.3
FEATURE [Part::MultiFuse] Fusion084  label="removeToCreteHoleForPlugHousing028"
  Shapes = -> [Box024,Cylinder038]
FEATURE [Part::Cylinder] Cylinder039
  Angle = 360
  AttacherType = Attacher::AttachEngine3D
  Height = 20
  Placement = pos=(0,0,36.15) rot=(0,0,1;0rad)
  Radius = 14.3
FEATURE [Part::Cylinder] Cylinder040
  Angle = 360
  AttacherType = Attacher::AttachEngine3D
  Height = 10
  Placement = pos=(0,0,36.15) rot=(0,0,1;0rad)
  Radius = 4
FEATURE [Part::Box] Box025  label="removeToCreteHoleForPlugHousing030"
  AttacherType = Attacher::AttachEngine3D
  Height = 28.6
  Length = 20
  Placement = pos=(106.15,0,21.7) rot=(0,0,1;0rad)
  Width = 19
FEATURE [Part::MultiFuse] Fusion086  label="removeToCreteHoleForPlugHousing031"
  Placement = pos=(70,19,36) rot=(0,1,0;1.5708rad)
  Shapes = -> [Cylinder039,Cylinder040]
FEATURE [Part::MultiFuse] Fusion085  label="removeToCreteHoleForPlugHousing029"
  Shapes = -> [Box025,Fusion086]
FEATURE [Sketcher::SketchObject] Sketch055
  FullyConstrained = true
  Placement = pos=(117,19,0) rot=(0.57735,0.57735,0.57735;2.0944rad)
  sketch-geometry (48):
    g0: LineSegment StartX=-49.19 StartY=69.25 StartZ=0 EndX=-49.19 EndY=66.25 EndZ=0
    g1: LineSegment StartX=-49.19 StartY=63.5 StartZ=0 EndX=-49.19 EndY=60.5 EndZ=0
    g2: LineSegment StartX=-49.19 StartY=57.75 StartZ=0 EndX=-49.19 EndY=54.75 EndZ=0
    g3: LineSegment StartX=-49.19 StartY=52 StartZ=0 EndX=-49.19 EndY=49 EndZ=0
    g4: LineSegment StartX=-49.19 StartY=46.25 StartZ=0 EndX=-49.19 EndY=43.25 EndZ=0
    g5: LineSegment StartX=-49.19 StartY=40.5 StartZ=0 EndX=-49.19 EndY=37.5 EndZ=0
    g6: LineSegment StartX=-49.19 StartY=34.5 StartZ=0 EndX=-49.19 EndY=31.5 EndZ=0
    g7: LineSegment StartX=-49.19 StartY=28.75 StartZ=0 EndX=-49.19 EndY=25.75 EndZ=0
    g8: LineSegment StartX=-49.19 StartY=23 StartZ=0 EndX=-49.19 EndY=20 EndZ=0
    g9: LineSegment StartX=-49.19 StartY=17.25 StartZ=0 EndX=-49.19 EndY=14.25 EndZ=0
    g10: LineSegment StartX=-49.19 StartY=11.5 StartZ=0 EndX=-49.19 EndY=8.5 EndZ=0
    g11: LineSegment StartX=-49.19 StartY=5.75 StartZ=0 EndX=-49.19 EndY=2.75 EndZ=0
    g12: ArcOfCircle CenterX=-1.5 CenterY=67.75 CenterZ=0 NormalX=0 NormalY=0 NormalZ=1 AngleXU=0 Radius=1.5 StartAngle=4.71239 EndAngle=7.85398
    g13: ArcOfCircle CenterX=-1.5 CenterY=62 CenterZ=0 NormalX=0 NormalY=0 NormalZ=1 AngleXU=0 Radius=1.5 StartAngle=4.71239 EndAngle=7.85398
    g14: ArcOfCircle CenterX=-1.5 CenterY=56.25 CenterZ=0 NormalX=0 NormalY=0 NormalZ=1 AngleXU=0 Radius=1.5 StartAngle=4.71239 EndAngle=7.85398
    g15: ArcOfCircle CenterX=-11.49 CenterY=50.5 CenterZ=0 NormalX=0 NormalY=0 NormalZ=1 AngleXU=0 Radius=1.5 StartAngle=4.71239 EndAngle=7.85398
    g16: ArcOfCircle CenterX=-16.28 CenterY=44.75 CenterZ=0 NormalX=0 NormalY=0 NormalZ=1 AngleXU=0 Radius=1.5 StartAngle=4.71239 EndAngle=7.85398
    g17: ArcOfCircle CenterX=-18.2337 CenterY=39 CenterZ=0 NormalX=0 NormalY=0 NormalZ=1 AngleXU=0 Radius=1.5 StartAngle=4.71485 EndAngle=7.85398
    g18: ArcOfCircle CenterX=-16.2837 CenterY=27.25 CenterZ=0 NormalX=0 NormalY=0 NormalZ=1 AngleXU=0 Radius=1.5 StartAngle=4.71485 EndAngle=7.85398
    g19: ArcOfCircle CenterX=-18.2337 CenterY=33 CenterZ=0 NormalX=0 NormalY=0 NormalZ=1 AngleXU=0 Radius=1.5 StartAngle=4.71485 EndAngle=7.85398
    g20: ArcOfCircle CenterX=-11.49 CenterY=21.5 CenterZ=0 NormalX=0 NormalY=0 NormalZ=1 AngleXU=0 Radius=1.5 StartAngle=4.71239 EndAngle=7.85398
    g21: ArcOfCircle CenterX=-1.5 CenterY=4.25 CenterZ=0 NormalX=0 NormalY=0 NormalZ=1 AngleXU=0 Radius=1.5 StartAngle=4.71239 EndAngle=7.85398
    g22: ArcOfCircle CenterX=-1.5 CenterY=10 CenterZ=0 NormalX=0 NormalY=0 NormalZ=1 AngleXU=0 Radius=1.5 StartAngle=4.71239 EndAngle=7.85398
    g23: ArcOfCircle CenterX=-1.5 CenterY=15.75 CenterZ=0 NormalX=0 NormalY=0 NormalZ=1 AngleXU=0 Radius=1.5 StartAngle=4.71239 EndAngle=7.85398
    g24: LineSegment StartX=-49.19 StartY=69.25 StartZ=0 EndX=-1.5 EndY=69.25 EndZ=0
    g25: LineSegment StartX=-49.19 StartY=66.25 StartZ=0 EndX=-1.5 EndY=66.25 EndZ=0
    g26: LineSegment StartX=-49.19 StartY=63.5 StartZ=0 EndX=-1.5 EndY=63.5 EndZ=0
    g27: LineSegment StartX=-49.19 StartY=60.5 StartZ=0 EndX=-1.5 EndY=60.5 EndZ=0
    g28: LineSegment StartX=-49.19 StartY=57.75 StartZ=0 EndX=-1.5 EndY=57.75 EndZ=0
    g29: LineSegment StartX=-49.19 StartY=54.75 StartZ=0 EndX=-1.5 EndY=54.75 EndZ=0
    g30: LineSegment StartX=-49.19 StartY=52 StartZ=0 EndX=-11.49 EndY=52 EndZ=0
    g31: LineSegment StartX=-49.19 StartY=49 StartZ=0 EndX=-11.49 EndY=49 EndZ=0
    g32: LineSegment StartX=-49.19 StartY=46.25 StartZ=0 EndX=-16.28 EndY=46.25 EndZ=0
    g33: LineSegment StartX=-49.19 StartY=43.25 StartZ=0 EndX=-16.28 EndY=43.25 EndZ=0
    g34: LineSegment StartX=-49.19 StartY=40.5 StartZ=0 EndX=-18.2337 EndY=40.5 EndZ=0
    g35: LineSegment StartX=-49.19 StartY=37.5 StartZ=0 EndX=-18.23 EndY=37.5 EndZ=0
    g36: LineSegment StartX=-49.19 StartY=34.5 StartZ=0 EndX=-18.2337 EndY=34.5 EndZ=0
    g37: LineSegment StartX=-49.19 StartY=31.5 StartZ=0 EndX=-18.23 EndY=31.5 EndZ=0
    g38: LineSegment StartX=-49.19 StartY=28.75 StartZ=0 EndX=-16.2837 EndY=28.75 EndZ=0
    g39: LineSegment StartX=-49.19 StartY=25.75 StartZ=0 EndX=-16.28 EndY=25.75 EndZ=0
    g40: LineSegment StartX=-49.19 StartY=23 StartZ=0 EndX=-11.49 EndY=23 EndZ=0
    g41: LineSegment StartX=-49.19 StartY=20 StartZ=0 EndX=-11.49 EndY=20 EndZ=0
    g42: LineSegment StartX=-49.19 StartY=17.25 StartZ=0 EndX=-1.5 EndY=17.25 EndZ=0
    g43: LineSegment StartX=-49.19 StartY=14.25 StartZ=0 EndX=-1.5 EndY=14.25 EndZ=0
    g44: LineSegment StartX=-49.19 StartY=11.5 StartZ=0 EndX=-1.5 EndY=11.5 EndZ=0
    g45: LineSegment StartX=-49.19 StartY=8.5 StartZ=0 EndX=-1.5 EndY=8.5 EndZ=0
    g46: LineSegment StartX=-49.19 StartY=5.75 StartZ=0 EndX=-1.5 EndY=5.75 EndZ=0
    g47: LineSegment StartX=-49.19 StartY=2.75 StartZ=0 EndX=-1.5 EndY=2.75 EndZ=0
  constraints (120):
    c: Vertical(g0)
    c: Distance(g0) = 3
    c: Block(g0)
    c: Vertical(g1)
    c: Distance(g1) = 3
    c: Vertical(g2)
    c: Equal(g0,g2) = 3
    c: Block(g2)
    c: Vertical(g3)
    c: Equal(g1,g3) = 3
    c: Vertical(g4)
    c: Equal(g0,g4) = 3
    c: Block(g4)
    c: Vertical(g5)
    c: Equal(g1,g5) = 3
    c: Vertical(g6)
    c: Equal(g0,g6) = 3
    c: Block(g6)
    c: Vertical(g7)
    c: Equal(g1,g7) = 3
    c: Vertical(g8)
    c: Equal(g0,g8) = 3
    c: Block(g8)
    c: Vertical(g9)
    c: Equal(g1,g9) = 3
    c: Vertical(g10)
    c: Equal(g0,g10) = 3
    c: Block(g10)
    c: Vertical(g11)
    c: Equal(g1,g11) = 3
    c: Block(g12)
    c: Block(g13)
    c: Block(g14)
    c: Block(g15)
    c: Block(g16)
    c: Block(g17)
    c: Block(g18)
    c: Block(g19)
    c: Block(g20)
    c: Block(g21)
    c: Block(g22)
    c: Block(g23)
    c: Block(g11)
    c: Block(g9)
    c: Block(g7)
    c: Block(g5)
    c: Block(g3)
    c: Block(g1)
    c: Coincident(g24,g0)
    c: Coincident(g24,g12)
    c: Horizontal(g24)
    c: Coincident(g25,g0)
    c: Coincident(g25,g12)
    c: Horizontal(g25)
    c: Coincident(g26,g1)
    c: Coincident(g26,g13)
    c: Horizontal(g26)
    c: Coincident(g27,g1)
    c: Coincident(g27,g13)
    c: Horizontal(g27)
    c: Coincident(g28,g2)
    c: Coincident(g28,g14)
    c: Horizontal(g28)
    c: Coincident(g29,g2)
    c: Coincident(g29,g14)
    c: Horizontal(g29)
    c: Coincident(g30,g3)
    c: Coincident(g30,g15)
    c: Horizontal(g30)
    c: Coincident(g31,g3)
    c: Coincident(g31,g15)
    c: Horizontal(g31)
    c: Coincident(g32,g4)
    c: Coincident(g32,g16)
    c: Horizontal(g32)
    c: Coincident(g33,g4)
    c: Coincident(g33,g16)
    c: Horizontal(g33)
    c: Coincident(g34,g5)
    c: Coincident(g34,g17)
    c: Horizontal(g34)
    c: Coincident(g35,g5)
    c: Coincident(g35,g17)
    c: Horizontal(g35)
    c: Coincident(g36,g6)
    c: Coincident(g36,g19)
    c: Horizontal(g36)
    c: Coincident(g37,g6)
    c: Coincident(g37,g19)
    c: Horizontal(g37)
    c: Coincident(g38,g7)
    c: Coincident(g38,g18)
    c: Horizontal(g38)
    c: Coincident(g39,g7)
    c: Coincident(g39,g18)
    c: Horizontal(g39)
    c: Coincident(g40,g8)
    c: Coincident(g40,g20)
    c: Horizontal(g40)
    c: Coincident(g41,g8)
    c: Coincident(g41,g20)
    c: Horizontal(g41)
    c: Coincident(g42,g9)
    c: Coincident(g42,g23)
    c: Horizontal(g42)
    c: Coincident(g43,g9)
    c: Coincident(g43,g23)
    c: Horizontal(g43)
    c: Coincident(g44,g10)
    c: Coincident(g44,g22)
    c: Horizontal(g44)
    c: Coincident(g45,g10)
    c: Coincident(g45,g22)
    c: Horizontal(g45)
    c: Coincident(g46,g11)
    c: Coincident(g46,g21)
    c: Horizontal(g46)
    c: Coincident(g47,g11)
    c: Coincident(g47,g21)
    c: Horizontal(g47)
FEATURE [Part::Extrusion] Extrude046
  Base = -> Sketch055
  Dir = (1,0,0)
  DirMode = 2
  FaceMakerClass = Part::FaceMakerBullseye
  LengthFwd = 23
  LengthRev = 0
  Placement = pos=(-19,0,0) rot=(0,0,1;0rad)
  Solid = true
  Symmetric = false
FEATURE [Part::Fillet] Fillet038  label="removeToCreateVentalationHoles001"
  Base = -> Extrude046
  Edges = <same value as first occurrence — deduplicated (x6 in doc)>
  Placement = pos=(7,0,0) rot=(0,0,1;0rad)
FEATURE [Sketcher::SketchObject] Sketch056  label="topSketch014"
  FullyConstrained = true
  sketch-geometry (22):
    g0: LineSegment StartX=5.21097e-06 StartY=3 StartZ=0 EndX=5.21097e-06 EndY=19 EndZ=0
    g1: ArcOfCircle CenterX=19 CenterY=19 CenterZ=0 NormalX=0 NormalY=0 NormalZ=1 AngleXU=0 Radius=19 StartAngle=1.5708 EndAngle=3.14159
    g2: ArcOfCircle CenterX=19 CenterY=19 CenterZ=0 NormalX=0 NormalY=0 NormalZ=1 AngleXU=0 Radius=16 StartAngle=1.5708 EndAngle=3.14159
    g3: LineSegment StartX=114 StartY=35 StartZ=0 EndX=19 EndY=35 EndZ=0
    g4: LineSegment StartX=5.21097e-06 StartY=3 StartZ=0 EndX=5.21097e-06 EndY=0 EndZ=0
    g5: LineSegment StartX=3 StartY=0 StartZ=0 EndX=5.21097e-06 EndY=0 EndZ=0
    g6: LineSegment StartX=3 StartY=19 StartZ=0 EndX=3 EndY=0 EndZ=0
    g7: LineSegment StartX=19 StartY=38 StartZ=0 EndX=124 EndY=38 EndZ=0
    g8: Circle CenterX=119 CenterY=35 CenterZ=0 NormalX=0 NormalY=0 NormalZ=1 AngleXU=0 Radius=1
    g9: Circle CenterX=121 CenterY=35 CenterZ=0 NormalX=0 NormalY=0 NormalZ=1 AngleXU=0 Radius=1
    g10: Circle CenterX=121 CenterY=33 CenterZ=0 NormalX=0 NormalY=0 NormalZ=1 AngleXU=0 Radius=1
    g11: BSplineCurve PolesCount=3 KnotsCount=2 Degree=2 IsPeriodic=0
    g12: GeomPoint X=119 Y=35 Z=0
    g13: GeomPoint X=121 Y=33 Z=0
    g14: LineSegment StartX=119 StartY=35 StartZ=0 EndX=114 EndY=35 EndZ=0
    g15: ArcOfCircle CenterX=105 CenterY=19 CenterZ=0 NormalX=0 NormalY=0 NormalZ=1 AngleXU=0 Radius=16 StartAngle=5.60905 EndAngle=6.28319
    g16: LineSegment StartX=121 StartY=33 StartZ=0 EndX=121 EndY=19 EndZ=0
    g17: LineSegment StartX=117.5 StartY=9.01251 StartZ=0 EndX=121.163 EndY=9.0125 EndZ=0
    g18: ArcOfCircle CenterX=105 CenterY=19 CenterZ=0 NormalX=0 NormalY=0 NormalZ=1 AngleXU=0 Radius=20.6155 StartAngle=5.7297 EndAngle=6.28319
    g19: LineSegment StartX=121.163 StartY=9.0125 StartZ=0 EndX=122.538 EndY=8.16329 EndZ=0
    g20: LineSegment StartX=124 StartY=38 StartZ=0 EndX=125.616 EndY=38 EndZ=0
    g21: LineSegment StartX=125.616 StartY=19 StartZ=0 EndX=125.616 EndY=38 EndZ=0
  constraints (49):
    c: Vertical(g0)
    c: Block(g0)
    c: Coincident(g1,g0)
    c: Block(g1)
    c: Coincident(g2,g1)
    c: Block(g2)
    c: Coincident(g3,g2)
    c: Horizontal(g3)
    c: Tangent(g3,g2)
    c: Coincident(g4,g0)
    c: Distance(g4) = 3
    c: Vertical(g4)
    c: Coincident(g5,g4)
    c: Horizontal(g5)
    c: Coincident(g6,g2)
    c: Coincident(g6,g5)
    c: Vertical(g6)
    c: Horizontal(g7)
    c: Distance(g7) = 105
    c: Coincident(g7,g1)
    c: Block(g3)
    c: Weight(g8) = 1
    c: Equal(g8,g9)
    c: Equal(g8,g10)
    c: InternalAlignment(g8,g11)
    c: InternalAlignment(g9,g11)
    c: InternalAlignment(g10,g11)
    c: InternalAlignment(g12,g11)
    c: InternalAlignment(g13,g11)
    c: Block(g11)
    c: Coincident(g14,g11)
    c: Coincident(g14,g3)
    c: Horizontal(g14)
    c: Block(g15)
    c: Coincident(g16,g11)
    c: Coincident(g16,g15)
    c: Vertical(g16)
    c: Distance(g16) = 14
    c: Coincident(g17,g15)
    c: Block(g18)
    c: Coincident(g19,g18)
    c: Coincident(g20,g7)
    c: Horizontal(g20)
    c: Vertical(g21)
    c: Coincident(g20,g21)
    c: Block(g20)
    c: Block(g21)
    c: Block(g19)
    c: Block(g17)
FEATURE [Part::Box] Box026  label="removeToCreteHoleForPlugHousing032"
  AttacherType = Attacher::AttachEngine3D
  Height = 28.6
  Length = 10
  Placement = pos=(-2,0,21.7) rot=(0,0,1;0rad)
  Width = 19
FEATURE [Part::Feature] Face109 .. Face112  x4 (patterned run collapsed; names and placements below)
  shape: bbox 3.5 x 17.8 x 2e-07 mm, 1 faces, 0 solids (baked)
FEATURE [Part::Revolution] Revolve117  label="removeToCreateScrewAndThreadedInsertHole045"
  Angle = 360
  Axis = (0,1,0)
  Base = (0,0,0)
  FaceMakerClass = Part::FaceMakerBullseye
  Placement = pos=(62.3,30.3,19.7) rot=(0,0,1;0rad)
  Solid = false
  Source = -> Face109
  Symmetric = false
FEATURE [Part::Revolution] Revolve118  label="removeToCreateScrewAndThreadedInsertHole046"
  Angle = 360
  Axis = (0,1,0)
  Base = (0,0,0)
  FaceMakerClass = Part::FaceMakerBullseye
  Placement = pos=(62.3,30.3,51.7) rot=(0,0,1;0rad)
  Solid = false
  Source = -> Face110
  Symmetric = false
FEATURE [Part::Revolution] Revolve119  label="removeToCreateScrewAndThreadedInsertHole047"
  Angle = 360
  Axis = (0,1,0)
  Base = (0,0,0)
  FaceMakerClass = Part::FaceMakerBullseye
  Placement = pos=(30.3,30.3,19.7) rot=(0,0,1;0rad)
  Solid = false
  Source = -> Face111
  Symmetric = false
FEATURE [Part::Revolution] Revolve120  label="removeToCreateScrewAndThreadedInsertHole048"
  Angle = 360
  Axis = (0,1,0)
  Base = (0,0,0)
  FaceMakerClass = Part::FaceMakerBullseye
  Placement = pos=(30.3,30.3,51.7) rot=(0,0,1;0rad)
  Solid = false
  Source = -> Face112
  Symmetric = false
FEATURE [Part::MultiFuse] Fusion087  label="createThreadedInsertHolesForFan005"
  Shapes = -> [Revolve117,Revolve118,Revolve119,Revolve120]
FEATURE [Part::Extrusion] Extrude047
  Base = -> Sketch056
  Dir = (0,0,1)
  DirMode = 2
  FaceMakerClass = Part::FaceMakerBullseye
  LengthFwd = 72
  LengthRev = 0
  Solid = true
  Symmetric = false
FEATURE [Part::Fillet] Fillet039  label="top019"
  Base = -> Extrude047
  Edges = 1 edges r=2: [Edge35]
FEATURE [Sketcher::SketchObject] Sketch057
  FullyConstrained = false
  Placement = pos=(0,0,0) rot=(1,0,0;1.5708rad)
  sketch-geometry (24):
    g0: ArcOfCircle CenterX=-4 CenterY=-10.5 CenterZ=0 NormalX=0 NormalY=0 NormalZ=1 AngleXU=0 Radius=1.5 StartAngle=6e-16 EndAngle=3.14159
    g1: ArcOfCircle CenterX=-34.2 CenterY=-10.5 CenterZ=0 NormalX=0 NormalY=0 NormalZ=1 AngleXU=0 Radius=1.5 StartAngle=0 EndAngle=3.14159
    g2: ArcOfCircle CenterX=-34.2 CenterY=-27.7 CenterZ=0 NormalX=0 NormalY=0 NormalZ=1 AngleXU=0 Radius=1.5 StartAngle=3.14159 EndAngle=6.28319
    g3: ArcOfCircle CenterX=-4 CenterY=-27.7 CenterZ=0 NormalX=0 NormalY=0 NormalZ=1 AngleXU=0 Radius=1.5 StartAngle=3.1416 EndAngle=6.28319
    g4: ArcOfCircle CenterX=-10 CenterY=-4.3 CenterZ=0 NormalX=0 NormalY=0 NormalZ=1 AngleXU=0 Radius=1.5 StartAngle=2e-16 EndAngle=3.14159
    g5: ArcOfCircle CenterX=-16.1 CenterY=-1.8 CenterZ=0 NormalX=0 NormalY=0 NormalZ=1 AngleXU=0 Radius=1.5 StartAngle=5e-16 EndAngle=3.14159
    g6: ArcOfCircle CenterX=-22.1 CenterY=-1.8 CenterZ=0 NormalX=0 NormalY=0 NormalZ=1 AngleXU=0 Radius=1.5 StartAngle=5e-16 EndAngle=3.14159
    g7: ArcOfCircle CenterX=-28.2 CenterY=-4.3 CenterZ=0 NormalX=0 NormalY=0 NormalZ=1 AngleXU=0 Radius=1.5 StartAngle=2e-16 EndAngle=3.14159
    g8: ArcOfCircle CenterX=-10 CenterY=-33.9 CenterZ=0 NormalX=0 NormalY=0 NormalZ=1 AngleXU=0 Radius=1.5 StartAngle=3.14159 EndAngle=6.28319
    g9: ArcOfCircle CenterX=-16.1 CenterY=-36.4 CenterZ=0 NormalX=0 NormalY=0 NormalZ=1 AngleXU=0 Radius=1.5 StartAngle=3.14159 EndAngle=6.28319
    g10: ArcOfCircle CenterX=-22.1 CenterY=-36.4 CenterZ=0 NormalX=0 NormalY=0 NormalZ=1 AngleXU=0 Radius=1.5 StartAngle=3.14159 EndAngle=6.28319
    g11: ArcOfCircle CenterX=-28.2 CenterY=-33.9 CenterZ=0 NormalX=0 NormalY=0 NormalZ=1 AngleXU=0 Radius=1.5 StartAngle=3.14159 EndAngle=6.28319
    g12: LineSegment StartX=-35.7 StartY=-10.5 StartZ=0 EndX=-35.7 EndY=-27.7 EndZ=0
    g13: LineSegment StartX=-32.7 StartY=-10.5 StartZ=0 EndX=-32.7 EndY=-27.7 EndZ=0
    g14: LineSegment StartX=-29.7 StartY=-33.9 StartZ=0 EndX=-29.7 EndY=-4.3 EndZ=0
    g15: LineSegment StartX=-26.7 StartY=-33.9 StartZ=0 EndX=-26.7 EndY=-4.3 EndZ=0
    g16: LineSegment StartX=-2.5 StartY=-10.5 StartZ=0 EndX=-2.5 EndY=-27.7 EndZ=0
    g17: LineSegment StartX=-8.5 StartY=-4.3 StartZ=0 EndX=-8.5 EndY=-33.9 EndZ=0
    g18: LineSegment StartX=-5.5 StartY=-10.5 StartZ=0 EndX=-5.5 EndY=-27.7 EndZ=0
    g19: LineSegment StartX=-11.5 StartY=-4.3 StartZ=0 EndX=-11.5 EndY=-33.9 EndZ=0
    g20: LineSegment StartX=-14.6 StartY=-1.8 StartZ=0 EndX=-14.6 EndY=-36.4 EndZ=0
    g21: LineSegment StartX=-17.6 StartY=-1.8 StartZ=0 EndX=-17.6 EndY=-36.4 EndZ=0
    g22: LineSegment StartX=-20.6 StartY=-36.4 StartZ=0 EndX=-20.6 EndY=-1.8 EndZ=0
    g23: LineSegment StartX=-23.6 StartY=-1.8 StartZ=0 EndX=-23.6 EndY=-36.4 EndZ=0
  constraints (48):
    c: Block(g0)
    c: Block(g1)
    c: Block(g2)
    c: Block(g3)
    c: Block(g4)
    c: Block(g5)
    c: Block(g6)
    c: Block(g7)
    c: Block(g8)
    c: Block(g9)
    c: Block(g10)
    c: Block(g11)
    c: Coincident(g12,g1)
    c: Coincident(g12,g2)
    c: Vertical(g12)
    c: Coincident(g13,g1)
    c: Coincident(g13,g2)
    c: Vertical(g13)
    c: Coincident(g14,g11)
    c: Coincident(g14,g7)
    c: Vertical(g14)
    c: Coincident(g15,g11)
    c: Coincident(g15,g7)
    c: Vertical(g15)
    c: Coincident(g16,g0)
    c: Coincident(g16,g3)
    c: Vertical(g16)
    c: Coincident(g17,g4)
    c: Coincident(g17,g8)
    c: Vertical(g17)
    c: Coincident(g18,g0)
    c: Coincident(g18,g3)
    c: Vertical(g18)
    c: Coincident(g19,g4)
    c: Coincident(g19,g8)
    c: Vertical(g19)
    c: Coincident(g20,g5)
    c: Coincident(g20,g9)
    c: Vertical(g20)
    c: Coincident(g21,g5)
    c: Coincident(g21,g9)
    c: Vertical(g21)
    c: Coincident(g22,g10)
    c: Coincident(g22,g6)
    c: Vertical(g22)
    c: Coincident(g23,g6)
    c: Coincident(g23,g10)
    c: Vertical(g23)
FEATURE [Part::Extrusion] Extrude048  label="removeToCreateFanGrillHoles004"
  Base = -> Sketch057
  Dir = (0,-1,6e-16)
  DirMode = 2
  FaceMakerClass = Part::FaceMakerBullseye
  LengthFwd = 10
  LengthRev = 0
  Placement = pos=(65.4,44,54.82) rot=(0,0,1;0rad)
  Solid = true
  Symmetric = false
FEATURE [Part::Cut] Cut040  label="top021"
  Base = -> Fillet039
  Tool = -> Extrude048
FEATURE [Part::Cylinder] Cylinder041  label="removeToCreteHoleForPlugHousing034"
  Angle = 360
  AttacherType = Attacher::AttachEngine3D
  Height = 20
  Placement = pos=(-2,19,36) rot=(0,1,0;1.5708rad)
  Radius = 14.3
FEATURE [Part::MultiFuse] Fusion089  label="removeToCreteHoleForPlugHousing035"
  Shapes = -> [Box026,Cylinder041]
FEATURE [Part::Cylinder] Cylinder042
  Angle = 360
  AttacherType = Attacher::AttachEngine3D
  Height = 20
  Placement = pos=(0,0,36.15) rot=(0,0,1;0rad)
  Radius = 14.3
FEATURE [Part::Cylinder] Cylinder043
  Angle = 360
  AttacherType = Attacher::AttachEngine3D
  Height = 10
  Placement = pos=(0,0,36.15) rot=(0,0,1;0rad)
  Radius = 4
FEATURE [Part::Box] Box027  label="removeToCreteHoleForPlugHousing036"
  AttacherType = Attacher::AttachEngine3D
  Height = 28.6
  Length = 20
  Placement = pos=(106.15,0,21.7) rot=(0,0,1;0rad)
  Width = 19
FEATURE [Part::Cut] Cut041  label="top022"
  Base = -> Cut040
  Tool = -> Fusion087
FEATURE [Part::Cut] Cut039  label="top020"
  Base = -> Cut041
  Tool = -> Fusion089
FEATURE [Part::MultiFuse] Fusion090  label="removeToCreteHoleForPlugHousing037"
  Placement = pos=(70,19,36) rot=(0,1,0;1.5708rad)
  Shapes = -> [Cylinder042,Cylinder043]
FEATURE [Part::MultiFuse] Fusion088  label="removeToCreteHoleForPlugHousing033"
  Shapes = -> [Box027,Fusion090]
FEATURE [Part::Cut] Cut042  label="removeToCreteHoleForPlugHousing038"
  Base = -> Cut039
  Tool = -> Fusion088
FEATURE [Part::MultiFuse] Fusion091  label="removeFromTop"
  Shapes = -> [Fillet038,Fusion085,Fusion084,Fusion083,Extrude045]
FEATURE [Part::Cut] Cut043  label="REAL TOP ====="
  Base = -> Fillet036
  Tool = -> Fusion091
FEATURE [Part::MultiFuse] Fusion092  label="caseScrewPillarBracket016"
  Shapes = -> [Extrude030,Extrude031,Extrude032,Extrude033,Extrude034,Extrude035,Extrude036,Extrude037,Box013,Box014]
FEATURE [Sketcher::SketchObject] Sketch058  label="topSketch015"
  FullyConstrained = true
  sketch-geometry (20):
    g0: LineSegment StartX=5.21097e-06 StartY=3 StartZ=0 EndX=5.21097e-06 EndY=19 EndZ=0
    g1: ArcOfCircle CenterX=19 CenterY=19 CenterZ=0 NormalX=0 NormalY=0 NormalZ=1 AngleXU=0 Radius=19 StartAngle=1.5708 EndAngle=3.14159
    g2: ArcOfCircle CenterX=19 CenterY=19 CenterZ=0 NormalX=0 NormalY=0 NormalZ=1 AngleXU=0 Radius=16 StartAngle=1.5708 EndAngle=3.14159
    g3: LineSegment StartX=114 StartY=35 StartZ=0 EndX=19 EndY=35 EndZ=0
    g4: LineSegment StartX=5.21097e-06 StartY=3 StartZ=0 EndX=5.21097e-06 EndY=0 EndZ=0
    g5: LineSegment StartX=3 StartY=0 StartZ=0 EndX=5.21097e-06 EndY=0 EndZ=0
    g6: LineSegment StartX=3 StartY=19 StartZ=0 EndX=3 EndY=0 EndZ=0
    g7: LineSegment StartX=19 StartY=38 StartZ=0 EndX=124 EndY=38 EndZ=0
    g8: Circle CenterX=119 CenterY=35 CenterZ=0 NormalX=0 NormalY=0 NormalZ=1 AngleXU=0 Radius=1
    g9: Circle CenterX=121 CenterY=35 CenterZ=0 NormalX=0 NormalY=0 NormalZ=1 AngleXU=0 Radius=1
    g10: Circle CenterX=121 CenterY=33 CenterZ=0 NormalX=0 NormalY=0 NormalZ=1 AngleXU=0 Radius=1
    g11: BSplineCurve PolesCount=3 KnotsCount=2 Degree=2 IsPeriodic=0
    g12: GeomPoint X=119 Y=35 Z=0
    g13: GeomPoint X=121 Y=33 Z=0
    g14: LineSegment StartX=119 StartY=35 StartZ=0 EndX=114 EndY=35 EndZ=0
    g15: ArcOfCircle CenterX=105 CenterY=19 CenterZ=0 NormalX=0 NormalY=0 NormalZ=1 AngleXU=0 Radius=19 StartAngle=5.7297 EndAngle=6.28319
    g16: ArcOfCircle CenterX=105 CenterY=19 CenterZ=0 NormalX=0 NormalY=0 NormalZ=1 AngleXU=0 Radius=16 StartAngle=5.60905 EndAngle=6.28319
    g17: LineSegment StartX=121 StartY=33 StartZ=0 EndX=121 EndY=19 EndZ=0
    g18: LineSegment StartX=124 StartY=38 StartZ=0 EndX=124 EndY=19 EndZ=0
    g19: LineSegment StartX=117.5 StartY=9.01251 StartZ=0 EndX=121.163 EndY=9.0125 EndZ=0
  constraints (46):
    c: Vertical(g0)
    c: Block(g0)
    c: Coincident(g1,g0)
    c: Block(g1)
    c: Coincident(g2,g1)
    c: Block(g2)
    c: Coincident(g3,g2)
    c: Horizontal(g3)
    c: Tangent(g3,g2)
    c: Coincident(g4,g0)
    c: Distance(g4) = 3
    c: Vertical(g4)
    c: Coincident(g5,g4)
    c: Horizontal(g5)
    c: Coincident(g6,g2)
    c: Coincident(g6,g5)
    c: Vertical(g6)
    c: Horizontal(g7)
    c: Distance(g7) = 105
    c: Coincident(g7,g1)
    c: Block(g3)
    c: Weight(g8) = 1
    c: Equal(g8,g9)
    c: Equal(g8,g10)
    c: InternalAlignment(g8,g11)
    c: InternalAlignment(g9,g11)
    c: InternalAlignment(g10,g11)
    c: InternalAlignment(g12,g11)
    c: InternalAlignment(g13,g11)
    c: Block(g11)
    c: Coincident(g14,g11)
    c: Coincident(g14,g3)
    c: Horizontal(g14)
    c: Block(g15)
    c: Coincident(g16,g15)
    c: Block(g16)
    c: Coincident(g17,g11)
    c: Coincident(g17,g16)
    c: Vertical(g17)
    c: Distance(g17) = 14
    c: Coincident(g18,g7)
    c: Coincident(g18,g15)
    c: Vertical(g18)
    c: Distance(g18) = 19
    c: Coincident(g19,g16)
    c: Coincident(g19,g15)
FEATURE [Part::Extrusion] Extrude049  label="top023"
  Base = -> Sketch058
  Dir = (0,0,1)
  DirMode = 2
  FaceMakerClass = Part::FaceMakerBullseye
  LengthFwd = 72
  LengthRev = 0
  Solid = true
  Symmetric = false
FEATURE [Sketcher::SketchObject] Sketch059
  FullyConstrained = true
  MapMode = 3
  Placement = pos=(0,0,0) rot=(1,0,0;1.5708rad)
  Support = -> [Extrude049]
  sketch-geometry (8):
    g0: Circle CenterX=80.351 CenterY=-67.6202 CenterZ=0 NormalX=0 NormalY=0 NormalZ=1 AngleXU=0 Radius=2
    g1: Circle CenterX=80.351 CenterY=-67.6202 CenterZ=0 NormalX=0 NormalY=0 NormalZ=1 AngleXU=0 Radius=3
    g2: Circle CenterX=80.351 CenterY=-4.92017 CenterZ=0 NormalX=0 NormalY=0 NormalZ=1 AngleXU=0 Radius=2
    g3: Circle CenterX=80.351 CenterY=-4.92017 CenterZ=0 NormalX=0 NormalY=0 NormalZ=1 AngleXU=0 Radius=3
    g4: Circle CenterX=23.851 CenterY=-4.92017 CenterZ=0 NormalX=0 NormalY=0 NormalZ=1 AngleXU=0 Radius=2
    g5: Circle CenterX=23.851 CenterY=-4.92017 CenterZ=0 NormalX=0 NormalY=0 NormalZ=1 AngleXU=0 Radius=3
    g6: Circle CenterX=23.851 CenterY=-67.6202 CenterZ=0 NormalX=0 NormalY=0 NormalZ=1 AngleXU=0 Radius=2
    g7: Circle CenterX=23.851 CenterY=-67.6202 CenterZ=0 NormalX=0 NormalY=0 NormalZ=1 AngleXU=0 Radius=3
  constraints (8):
    c: Block(g3)
    c: Block(g2)
    c: Block(g1)
    c: Block(g0)
    c: Block(g6)
    c: Block(g7)
    c: Block(g4)
    c: Block(g5)
FEATURE [Sketcher::SketchObject] Sketch060
  FullyConstrained = true
  MapMode = 3
  Placement = pos=(0,0,0) rot=(1,0,0;1.5708rad)
  Support = -> [Extrude049]
  sketch-geometry (8):
    g0: Circle CenterX=80.351 CenterY=-67.6202 CenterZ=0 NormalX=0 NormalY=0 NormalZ=1 AngleXU=0 Radius=3
    g1: Circle CenterX=80.351 CenterY=-4.92017 CenterZ=0 NormalX=0 NormalY=0 NormalZ=1 AngleXU=0 Radius=3
    g2: Circle CenterX=23.851 CenterY=-4.92017 CenterZ=0 NormalX=0 NormalY=0 NormalZ=1 AngleXU=0 Radius=3
    g3: Circle CenterX=23.851 CenterY=-67.6202 CenterZ=0 NormalX=0 NormalY=0 NormalZ=1 AngleXU=0 Radius=3
    g4: Circle CenterX=23.851 CenterY=-67.6202 CenterZ=0 NormalX=0 NormalY=0 NormalZ=1 AngleXU=0 Radius=5
    g5: Circle CenterX=80.351 CenterY=-67.6202 CenterZ=0 NormalX=0 NormalY=0 NormalZ=1 AngleXU=0 Radius=5
    g6: Circle CenterX=23.851 CenterY=-4.92017 CenterZ=0 NormalX=0 NormalY=0 NormalZ=1 AngleXU=0 Radius=5
    g7: Circle CenterX=80.351 CenterY=-4.92017 CenterZ=0 NormalX=0 NormalY=0 NormalZ=1 AngleXU=0 Radius=5
  constraints (8):
    c: Block(g1)
    c: Block(g0)
    c: Block(g3)
    c: Block(g2)
    c: Block(g5)
    c: Block(g4)
    c: Block(g6)
    c: Block(g7)
FEATURE [Sketcher::SketchObject] Sketch061
  FullyConstrained = true
  MapMode = 3
  Placement = pos=(0,0,0) rot=(1,0,0;1.5708rad)
  sketch-geometry (8):
    g0: Circle CenterX=80.351 CenterY=-67.6202 CenterZ=0 NormalX=0 NormalY=0 NormalZ=1 AngleXU=0 Radius=3
    g1: Circle CenterX=80.351 CenterY=-4.92017 CenterZ=0 NormalX=0 NormalY=0 NormalZ=1 AngleXU=0 Radius=3
    g2: Circle CenterX=23.851 CenterY=-4.92017 CenterZ=0 NormalX=0 NormalY=0 NormalZ=1 AngleXU=0 Radius=3
    g3: Circle CenterX=23.851 CenterY=-67.6202 CenterZ=0 NormalX=0 NormalY=0 NormalZ=1 AngleXU=0 Radius=3
    g4: Circle CenterX=23.851 CenterY=-67.6202 CenterZ=0 NormalX=0 NormalY=0 NormalZ=1 AngleXU=0 Radius=5
    g5: Circle CenterX=80.351 CenterY=-67.6202 CenterZ=0 NormalX=0 NormalY=0 NormalZ=1 AngleXU=0 Radius=5
    g6: Circle CenterX=23.851 CenterY=-4.92017 CenterZ=0 NormalX=0 NormalY=0 NormalZ=1 AngleXU=0 Radius=5
    g7: Circle CenterX=80.351 CenterY=-4.92017 CenterZ=0 NormalX=0 NormalY=0 NormalZ=1 AngleXU=0 Radius=5
  constraints (8):
    c: Block(g1)
    c: Block(g0)
    c: Block(g3)
    c: Block(g2)
    c: Block(g5)
    c: Block(g4)
    c: Block(g6)
    c: Block(g7)
FEATURE [Sketcher::SketchObject] Sketch062  label="topSketch016"
  FullyConstrained = true
  sketch-geometry (20):
    g0: LineSegment StartX=5.21097e-06 StartY=3 StartZ=0 EndX=5.21097e-06 EndY=19 EndZ=0
    g1: ArcOfCircle CenterX=19 CenterY=19 CenterZ=0 NormalX=0 NormalY=0 NormalZ=1 AngleXU=0 Radius=19 StartAngle=1.5708 EndAngle=3.14159
    g2: ArcOfCircle CenterX=19 CenterY=19 CenterZ=0 NormalX=0 NormalY=0 NormalZ=1 AngleXU=0 Radius=16 StartAngle=1.5708 EndAngle=3.14159
    g3: LineSegment StartX=114 StartY=35 StartZ=0 EndX=19 EndY=35 EndZ=0
    g4: LineSegment StartX=5.21097e-06 StartY=3 StartZ=0 EndX=5.21097e-06 EndY=0 EndZ=0
    g5: LineSegment StartX=3 StartY=0 StartZ=0 EndX=5.21097e-06 EndY=0 EndZ=0
    g6: LineSegment StartX=3 StartY=19 StartZ=0 EndX=3 EndY=0 EndZ=0
    g7: LineSegment StartX=19 StartY=38 StartZ=0 EndX=124 EndY=38 EndZ=0
    g8: Circle CenterX=119 CenterY=35 CenterZ=0 NormalX=0 NormalY=0 NormalZ=1 AngleXU=0 Radius=1
    g9: Circle CenterX=121 CenterY=35 CenterZ=0 NormalX=0 NormalY=0 NormalZ=1 AngleXU=0 Radius=1
    g10: Circle CenterX=121 CenterY=33 CenterZ=0 NormalX=0 NormalY=0 NormalZ=1 AngleXU=0 Radius=1
    g11: BSplineCurve PolesCount=3 KnotsCount=2 Degree=2 IsPeriodic=0
    g12: GeomPoint X=119 Y=35 Z=0
    g13: GeomPoint X=121 Y=33 Z=0
    g14: LineSegment StartX=119 StartY=35 StartZ=0 EndX=114 EndY=35 EndZ=0
    g15: ArcOfCircle CenterX=105 CenterY=19 CenterZ=0 NormalX=0 NormalY=0 NormalZ=1 AngleXU=0 Radius=19 StartAngle=5.7297 EndAngle=6.28319
    g16: ArcOfCircle CenterX=105 CenterY=19 CenterZ=0 NormalX=0 NormalY=0 NormalZ=1 AngleXU=0 Radius=16 StartAngle=5.60905 EndAngle=6.28319
    g17: LineSegment StartX=121 StartY=33 StartZ=0 EndX=121 EndY=19 EndZ=0
    g18: LineSegment StartX=124 StartY=38 StartZ=0 EndX=124 EndY=19 EndZ=0
    g19: LineSegment StartX=117.5 StartY=9.01251 StartZ=0 EndX=121.163 EndY=9.0125 EndZ=0
  constraints (46):
    c: Vertical(g0)
    c: Block(g0)
    c: Coincident(g1,g0)
    c: Block(g1)
    c: Coincident(g2,g1)
    c: Block(g2)
    c: Coincident(g3,g2)
    c: Horizontal(g3)
    c: Tangent(g3,g2)
    c: Coincident(g4,g0)
    c: Distance(g4) = 3
    c: Vertical(g4)
    c: Coincident(g5,g4)
    c: Horizontal(g5)
    c: Coincident(g6,g2)
    c: Coincident(g6,g5)
    c: Vertical(g6)
    c: Horizontal(g7)
    c: Distance(g7) = 105
    c: Coincident(g7,g1)
    c: Block(g3)
    c: Weight(g8) = 1
    c: Equal(g8,g9)
    c: Equal(g8,g10)
    c: InternalAlignment(g8,g11)
    c: InternalAlignment(g9,g11)
    c: InternalAlignment(g10,g11)
    c: InternalAlignment(g12,g11)
    c: InternalAlignment(g13,g11)
    c: Block(g11)
    c: Coincident(g14,g11)
    c: Coincident(g14,g3)
    c: Horizontal(g14)
    c: Block(g15)
    c: Coincident(g16,g15)
    c: Block(g16)
    c: Coincident(g17,g11)
    c: Coincident(g17,g16)
    c: Vertical(g17)
    c: Distance(g17) = 14
    c: Coincident(g18,g7)
    c: Coincident(g18,g15)
    c: Vertical(g18)
    c: Distance(g18) = 19
    c: Coincident(g19,g16)
    c: Coincident(g19,g15)
FEATURE [Part::Extrusion] Extrude053  label="top024"
  Base = -> Sketch062
  Dir = (0,0,1)
  DirMode = 2
  FaceMakerClass = Part::FaceMakerBullseye
  LengthFwd = 72
  LengthRev = 0
  Solid = true
  Symmetric = false
FEATURE [Sketcher::SketchObject] Sketch063
  FullyConstrained = true
  MapMode = 3
  Placement = pos=(0,0,0) rot=(1,0,0;1.5708rad)
  Support = -> [Extrude053]
  sketch-geometry (8):
    g0: Circle CenterX=80.351 CenterY=-67.6202 CenterZ=0 NormalX=0 NormalY=0 NormalZ=1 AngleXU=0 Radius=2
    g1: Circle CenterX=80.351 CenterY=-67.6202 CenterZ=0 NormalX=0 NormalY=0 NormalZ=1 AngleXU=0 Radius=3
    g2: Circle CenterX=80.351 CenterY=-4.92017 CenterZ=0 NormalX=0 NormalY=0 NormalZ=1 AngleXU=0 Radius=2
    g3: Circle CenterX=80.351 CenterY=-4.92017 CenterZ=0 NormalX=0 NormalY=0 NormalZ=1 AngleXU=0 Radius=3
    g4: Circle CenterX=23.851 CenterY=-4.92017 CenterZ=0 NormalX=0 NormalY=0 NormalZ=1 AngleXU=0 Radius=2
    g5: Circle CenterX=23.851 CenterY=-4.92017 CenterZ=0 NormalX=0 NormalY=0 NormalZ=1 AngleXU=0 Radius=3
    g6: Circle CenterX=23.851 CenterY=-67.6202 CenterZ=0 NormalX=0 NormalY=0 NormalZ=1 AngleXU=0 Radius=2
    g7: Circle CenterX=23.851 CenterY=-67.6202 CenterZ=0 NormalX=0 NormalY=0 NormalZ=1 AngleXU=0 Radius=3
  constraints (8):
    c: Block(g3)
    c: Block(g2)
    c: Block(g1)
    c: Block(g0)
    c: Block(g6)
    c: Block(g7)
    c: Block(g4)
    c: Block(g5)
FEATURE [Part::Extrusion] Extrude054
  Base = -> Sketch063
  Dir = (0,-1,2e-16)
  DirMode = 2
  FaceMakerClass = Part::FaceMakerBullseye
  LengthFwd = 6
  LengthRev = 0
  Placement = pos=(0,9,0) rot=(0,0,1;0rad)
  Solid = true
  Symmetric = false
FEATURE [Sketcher::SketchObject] Sketch064  label="topSketch017"
  FullyConstrained = true
  sketch-geometry (20):
    g0: LineSegment StartX=5.21097e-06 StartY=3 StartZ=0 EndX=5.21097e-06 EndY=19 EndZ=0
    g1: ArcOfCircle CenterX=19 CenterY=19 CenterZ=0 NormalX=0 NormalY=0 NormalZ=1 AngleXU=0 Radius=19 StartAngle=1.5708 EndAngle=3.14159
    g2: ArcOfCircle CenterX=19 CenterY=19 CenterZ=0 NormalX=0 NormalY=0 NormalZ=1 AngleXU=0 Radius=16 StartAngle=1.5708 EndAngle=3.14159
    g3: LineSegment StartX=114 StartY=35 StartZ=0 EndX=19 EndY=35 EndZ=0
    g4: LineSegment StartX=5.21097e-06 StartY=3 StartZ=0 EndX=5.21097e-06 EndY=0 EndZ=0
    g5: LineSegment StartX=3 StartY=0 StartZ=0 EndX=5.21097e-06 EndY=0 EndZ=0
    g6: LineSegment StartX=3 StartY=19 StartZ=0 EndX=3 EndY=0 EndZ=0
    g7: LineSegment StartX=19 StartY=38 StartZ=0 EndX=124 EndY=38 EndZ=0
    g8: Circle CenterX=119 CenterY=35 CenterZ=0 NormalX=0 NormalY=0 NormalZ=1 AngleXU=0 Radius=1
    g9: Circle CenterX=121 CenterY=35 CenterZ=0 NormalX=0 NormalY=0 NormalZ=1 AngleXU=0 Radius=1
    g10: Circle CenterX=121 CenterY=33 CenterZ=0 NormalX=0 NormalY=0 NormalZ=1 AngleXU=0 Radius=1
    g11: BSplineCurve PolesCount=3 KnotsCount=2 Degree=2 IsPeriodic=0
    g12: GeomPoint X=119 Y=35 Z=0
    g13: GeomPoint X=121 Y=33 Z=0
    g14: LineSegment StartX=119 StartY=35 StartZ=0 EndX=114 EndY=35 EndZ=0
    g15: ArcOfCircle CenterX=105 CenterY=19 CenterZ=0 NormalX=0 NormalY=0 NormalZ=1 AngleXU=0 Radius=19 StartAngle=5.7297 EndAngle=6.28319
    g16: ArcOfCircle CenterX=105 CenterY=19 CenterZ=0 NormalX=0 NormalY=0 NormalZ=1 AngleXU=0 Radius=16 StartAngle=5.60905 EndAngle=6.28319
    g17: LineSegment StartX=121 StartY=33 StartZ=0 EndX=121 EndY=19 EndZ=0
    g18: LineSegment StartX=124 StartY=38 StartZ=0 EndX=124 EndY=19 EndZ=0
    g19: LineSegment StartX=117.5 StartY=9.01251 StartZ=0 EndX=121.163 EndY=9.0125 EndZ=0
  constraints (46):
    c: Vertical(g0)
    c: Block(g0)
    c: Coincident(g1,g0)
    c: Block(g1)
    c: Coincident(g2,g1)
    c: Block(g2)
    c: Coincident(g3,g2)
    c: Horizontal(g3)
    c: Tangent(g3,g2)
    c: Coincident(g4,g0)
    c: Distance(g4) = 3
    c: Vertical(g4)
    c: Coincident(g5,g4)
    c: Horizontal(g5)
    c: Coincident(g6,g2)
    c: Coincident(g6,g5)
    c: Vertical(g6)
    c: Horizontal(g7)
    c: Distance(g7) = 105
    c: Coincident(g7,g1)
    c: Block(g3)
    c: Weight(g8) = 1
    c: Equal(g8,g9)
    c: Equal(g8,g10)
    c: InternalAlignment(g8,g11)
    c: InternalAlignment(g9,g11)
    c: InternalAlignment(g10,g11)
    c: InternalAlignment(g12,g11)
    c: InternalAlignment(g13,g11)
    c: Block(g11)
    c: Coincident(g14,g11)
    c: Coincident(g14,g3)
    c: Horizontal(g14)
    c: Block(g15)
    c: Coincident(g16,g15)
    c: Block(g16)
    c: Coincident(g17,g11)
    c: Coincident(g17,g16)
    c: Vertical(g17)
    c: Distance(g17) = 14
    c: Coincident(g18,g7)
    c: Coincident(g18,g15)
    c: Vertical(g18)
    c: Distance(g18) = 19
    c: Coincident(g19,g16)
    c: Coincident(g19,g15)
FEATURE [Sketcher::SketchObject] Sketch065
  FullyConstrained = true
  MapMode = 3
  Placement = pos=(0,0,0) rot=(1,0,0;1.5708rad)
  sketch-geometry (8):
    g0: Circle CenterX=80.351 CenterY=-67.6202 CenterZ=0 NormalX=0 NormalY=0 NormalZ=1 AngleXU=0 Radius=3
    g1: Circle CenterX=80.351 CenterY=-4.92017 CenterZ=0 NormalX=0 NormalY=0 NormalZ=1 AngleXU=0 Radius=3
    g2: Circle CenterX=23.851 CenterY=-4.92017 CenterZ=0 NormalX=0 NormalY=0 NormalZ=1 AngleXU=0 Radius=3
    g3: Circle CenterX=23.851 CenterY=-67.6202 CenterZ=0 NormalX=0 NormalY=0 NormalZ=1 AngleXU=0 Radius=3
    g4: Circle CenterX=23.851 CenterY=-67.6202 CenterZ=0 NormalX=0 NormalY=0 NormalZ=1 AngleXU=0 Radius=5
    g5: Circle CenterX=80.351 CenterY=-67.6202 CenterZ=0 NormalX=0 NormalY=0 NormalZ=1 AngleXU=0 Radius=5
    g6: Circle CenterX=23.851 CenterY=-4.92017 CenterZ=0 NormalX=0 NormalY=0 NormalZ=1 AngleXU=0 Radius=5
    g7: Circle CenterX=80.351 CenterY=-4.92017 CenterZ=0 NormalX=0 NormalY=0 NormalZ=1 AngleXU=0 Radius=5
  constraints (8):
    c: Block(g1)
    c: Block(g0)
    c: Block(g3)
    c: Block(g2)
    c: Block(g5)
    c: Block(g4)
    c: Block(g6)
    c: Block(g7)
FEATURE [Part::Extrusion] Extrude056
  Base = -> Sketch065
  Dir = (0,-1,2e-16)
  DirMode = 2
  FaceMakerClass = Part::FaceMakerBullseye
  LengthFwd = 2
  LengthRev = 0
  Solid = true
  Symmetric = false
FEATURE [Part::Extrusion] Extrude057  label="top025"
  Base = -> Sketch064
  Dir = (0,0,1)
  DirMode = 2
  FaceMakerClass = Part::FaceMakerBullseye
  LengthFwd = 72
  LengthRev = 0
  Solid = true
  Symmetric = false
FEATURE [Sketcher::SketchObject] Sketch066
  FullyConstrained = true
  MapMode = 3
  Placement = pos=(0,0,0) rot=(1,0,0;1.5708rad)
  Support = -> [Extrude057]
  sketch-geometry (8):
    g0: Circle CenterX=80.351 CenterY=-67.6202 CenterZ=0 NormalX=0 NormalY=0 NormalZ=1 AngleXU=0 Radius=3
    g1: Circle CenterX=80.351 CenterY=-4.92017 CenterZ=0 NormalX=0 NormalY=0 NormalZ=1 AngleXU=0 Radius=3
    g2: Circle CenterX=23.851 CenterY=-4.92017 CenterZ=0 NormalX=0 NormalY=0 NormalZ=1 AngleXU=0 Radius=3
    g3: Circle CenterX=23.851 CenterY=-67.6202 CenterZ=0 NormalX=0 NormalY=0 NormalZ=1 AngleXU=0 Radius=3
    g4: Circle CenterX=23.851 CenterY=-67.6202 CenterZ=0 NormalX=0 NormalY=0 NormalZ=1 AngleXU=0 Radius=5
    g5: Circle CenterX=80.351 CenterY=-67.6202 CenterZ=0 NormalX=0 NormalY=0 NormalZ=1 AngleXU=0 Radius=5
    g6: Circle CenterX=23.851 CenterY=-4.92017 CenterZ=0 NormalX=0 NormalY=0 NormalZ=1 AngleXU=0 Radius=5
    g7: Circle CenterX=80.351 CenterY=-4.92017 CenterZ=0 NormalX=0 NormalY=0 NormalZ=1 AngleXU=0 Radius=5
  constraints (8):
    c: Block(g1)
    c: Block(g0)
    c: Block(g3)
    c: Block(g2)
    c: Block(g5)
    c: Block(g4)
    c: Block(g6)
    c: Block(g7)
FEATURE [Part::Extrusion] Extrude055
  Base = -> Sketch066
  Dir = (0,-1,2e-16)
  DirMode = 2
  FaceMakerClass = Part::FaceMakerBullseye
  LengthFwd = 2
  LengthRev = 0
  Solid = true
  Symmetric = false
FEATURE [Part::Fillet] Fillet041
  Base = -> Extrude056
  Edges = 4 edges r=1.99: [Edge6,Edge12,Edge18,Edge24]
FEATURE [Part::Cut] Cut045
  Base = -> Extrude055
  Placement = pos=(0,6,0) rot=(0,0,1;0rad)
  Tool = -> Fillet041
FEATURE [Part::MultiFuse] Fusion095  label="pcbScrewPillars"
  Placement = pos=(-3.2,-1,72.3) rot=(0,0,1;0rad)
  Shapes = -> [Cut045,Extrude054]
FEATURE [Part::Feature] Face113
  shape: bbox 3.2 x 1.5 x 2e-07 mm, 1 faces, 0 solids (baked)
FEATURE [Part::Revolution] Revolve121  label="backCaseScrewRetainer002"
  Angle = 360
  Axis = (0,1,0)
  Base = (0,0,0)
  FaceMakerClass = Part::FaceMakerBullseye
  Placement = pos=(12.5,3,62) rot=(0,0,1;0rad)
  Solid = false
  Source = -> Face113
  Symmetric = false
FEATURE [Part::Feature] Face114
  shape: bbox 3.2 x 1.5 x 2e-07 mm, 1 faces, 0 solids (baked)
FEATURE [Part::Feature] Face115
  shape: bbox 3.2 x 1.5 x 2e-07 mm, 1 faces, 0 solids (baked)
FEATURE [Part::Feature] Face116
  shape: bbox 3.2 x 1.5 x 2e-07 mm, 1 faces, 0 solids (baked)
FEATURE [Part::Revolution] Revolve122  label="frontCaseScrewRetainer004"
  Angle = 360
  Axis = (0,1,0)
  Base = (0,0,0)
  FaceMakerClass = Part::FaceMakerBullseye
  Placement = pos=(89.5,3,68.5) rot=(0,0,1;0rad)
  Solid = false
  Source = -> Face115
  Symmetric = false
FEATURE [Part::Revolution] Revolve123  label="frontCaseScrewRetainer005"
  Angle = 360
  Axis = (0,1,0)
  Base = (0,0,0)
  FaceMakerClass = Part::FaceMakerBullseye
  Placement = pos=(89.5,3,3.5) rot=(0,0,1;0rad)
  Solid = false
  Source = -> Face116
  Symmetric = false
FEATURE [Part::Revolution] Revolve124  label="backCaseScrewRetainer003"
  Angle = 360
  Axis = (0,1,0)
  Base = (0,0,0)
  FaceMakerClass = Part::FaceMakerBullseye
  Placement = pos=(12.5,3,10) rot=(0,0,1;0rad)
  Solid = false
  Source = -> Face114
  Symmetric = false
FEATURE [Part::Feature] Face117
  shape: bbox 3.6 x 3.2 x 2e-07 mm, 1 faces, 0 solids (baked)
FEATURE [Part::Revolution] Revolve125  label="moreFrontCaseScrewRetainer004"
  Angle = 360
  Axis = (0,1,0)
  Base = (0,0,0)
  FaceMakerClass = Part::FaceMakerBullseye
  Placement = pos=(109.5,4.5,68.5) rot=(0,0,1;0rad)
  Solid = false
  Source = -> Face117
  Symmetric = false
FEATURE [Part::Feature] Face118
  shape: bbox 3.6 x 3.2 x 2e-07 mm, 1 faces, 0 solids (baked)
FEATURE [Part::Revolution] Revolve126  label="moreFrontCaseScrewRetainer005"
  Angle = 360
  Axis = (0,1,0)
  Base = (0,0,0)
  FaceMakerClass = Part::FaceMakerBullseye
  Placement = pos=(109.5,4.5,3.5) rot=(0,0,1;0rad)
  Solid = false
  Source = -> Face118
  Symmetric = false
FEATURE [Part::MultiFuse] Fusion096  label="screwRetainers001"
  Shapes = -> [Revolve126,Revolve125,Revolve124,Revolve123,Revolve122,Revolve121]
FEATURE [Part::Feature] Face119
  shape: bbox 10 x 16.5 x 2e-07 mm, 1 faces, 0 solids (baked)
FEATURE [Part::Revolution] Revolve130  label="plugHousing050"
  Angle = 360
  Axis = (0,1,0)
  Base = (0,0,0)
  FaceMakerClass = Part::FaceMakerBullseye
  Placement = pos=(0,0,36.15) rot=(0,0,1;0rad)
  Solid = false
  Source = -> Face119
  Symmetric = false
FEATURE [Part::Feature] Face120
  shape: bbox 10 x 16.5 x 2e-07 mm, 1 faces, 0 solids (baked)
FEATURE [Part::Feature] Face121
  shape: bbox 10 x 16.5 x 2e-07 mm, 1 faces, 0 solids (baked)
FEATURE [Part::Revolution] Revolve127  label="plugHousing047"
  Angle = 360
  Axis = (0,1,0)
  Base = (0,0,0)
  FaceMakerClass = Part::FaceMakerBullseye
  Placement = pos=(0,0,36.15) rot=(0,0,1;0rad)
  Solid = false
  Source = -> Face121
  Symmetric = false
FEATURE [Part::Feature] Face122
  shape: bbox 10 x 16.5 x 2e-07 mm, 1 faces, 0 solids (baked)
FEATURE [Part::Feature] Face123
  shape: bbox 10 x 16.5 x 2e-07 mm, 1 faces, 0 solids (baked)
FEATURE [Part::Revolution] Revolve128  label="plugHousing048"
  Angle = 360
  Axis = (0,1,0)
  Base = (0,0,0)
  FaceMakerClass = Part::FaceMakerBullseye
  Placement = pos=(0,0,36.15) rot=(0,0,1;0rad)
  Solid = false
  Source = -> Face123
  Symmetric = false
FEATURE [Part::MultiFuse] Fusion100  label="plugHousing054"
  Placement = pos=(0,0,0) rot=(0,0,1;1.5708rad)
  Shapes = -> [Revolve130,Revolve128]
FEATURE [Part::Feature] Face124
  shape: bbox 10 x 16.5 x 2e-07 mm, 1 faces, 0 solids (baked)
FEATURE [Part::Feature] Face125
  shape: bbox 10 x 16.5 x 2e-07 mm, 1 faces, 0 solids (baked)
FEATURE [Part::Revolution] Revolve129  label="plugHousing049"
  Angle = 360
  Axis = (0,1,0)
  Base = (0,0,0)
  FaceMakerClass = Part::FaceMakerBullseye
  Placement = pos=(0,0,36.15) rot=(0,0,1;0rad)
  Solid = false
  Source = -> Face125
  Symmetric = false
FEATURE [Part::Feature] Face126
  shape: bbox 10 x 16.5 x 2e-07 mm, 1 faces, 0 solids (baked)
FEATURE [Part::Revolution] Revolve131  label="plugHousing058"
  Angle = 360
  Axis = (0,1,0)
  Base = (0,0,0)
  FaceMakerClass = Part::FaceMakerBullseye
  Placement = pos=(0,0,36.15) rot=(0,0,1;0rad)
  Solid = false
  Source = -> Face120
  Symmetric = false
FEATURE [Part::MultiFuse] Fusion099  label="plugHousing053"
  Placement = pos=(0,0,0) rot=(0,0,1;1.5708rad)
  Shapes = -> [Revolve127,Revolve131]
FEATURE [Part::MultiFuse] Fusion102  label="plugHousing056"
  Placement = pos=(0,19,0) rot=(0,0,1;3.14159rad)
  Shapes = -> [Fusion100,Fusion099]
FEATURE [Part::Revolution] Revolve132  label="plugHousing059"
  Angle = 360
  Axis = (0,1,0)
  Base = (0,0,0)
  FaceMakerClass = Part::FaceMakerBullseye
  Placement = pos=(0,0,36.15) rot=(0,0,1;0rad)
  Solid = false
  Source = -> Face126
  Symmetric = false
FEATURE [Part::Revolution] Revolve133  label="plugHousing060"
  Angle = 360
  Axis = (0,1,0)
  Base = (0,0,0)
  FaceMakerClass = Part::FaceMakerBullseye
  Placement = pos=(0,0,36.15) rot=(0,0,1;0rad)
  Solid = false
  Source = -> Face122
  Symmetric = false
FEATURE [Part::MultiFuse] Fusion097  label="plugHousing051"
  Placement = pos=(0,0,0) rot=(0,0,1;1.5708rad)
  Shapes = -> [Revolve133,Revolve132]
FEATURE [Part::Revolution] Revolve134  label="plugHousing061"
  Angle = 360
  Axis = (0,1,0)
  Base = (0,0,0)
  FaceMakerClass = Part::FaceMakerBullseye
  Placement = pos=(0,0,36.15) rot=(0,0,1;0rad)
  Solid = false
  Source = -> Face124
  Symmetric = false
FEATURE [Part::MultiFuse] Fusion101  label="plugHousing055"
  Placement = pos=(0,0,0) rot=(0,0,1;1.5708rad)
  Shapes = -> [Revolve129,Revolve134]
FEATURE [Part::MultiFuse] Fusion098  label="plugHousing052"
  Placement = pos=(0,19,0) rot=(0,0,1;3.14159rad)
  Shapes = -> [Fusion097,Fusion101]
FEATURE [Part::MultiFuse] Fusion103  label="plugHousing057"
  Placement = pos=(122.621,0,-0.15) rot=(0,0,1;0rad)
  Shapes = -> [Fusion102,Fusion098]
FEATURE [Part::Box] Box028  label="Cube015"
  AttacherType = Attacher::AttachEngine3D
  Height = 28
  Length = 3
  Placement = pos=(110.7,19,22) rot=(0,0,1;0rad)
  Width = 15.7
FEATURE [Part::Cylinder] Cylinder044
  Angle = 360
  AttacherType = Attacher::AttachEngine3D
  Height = 20
  Placement = pos=(0,0,36.15) rot=(0,0,1;0rad)
  Radius = 10.3
FEATURE [Part::Cylinder] Cylinder045
  Angle = 360
  AttacherType = Attacher::AttachEngine3D
  Height = 10
  Placement = pos=(0,0,36.15) rot=(0,0,1;0rad)
  Radius = 4
FEATURE [Part::MultiFuse] Fusion104  label="removeToCreteHoleForPlugHousing040"
  Placement = pos=(70,19,36) rot=(0,1,0;1.5708rad)
  Shapes = -> [Cylinder044,Cylinder045]
FEATURE [Part::Cut] Cut046  label="plugHousingTab003"
  Base = -> Box028
  Tool = -> Fusion104
FEATURE [Part::MultiFuse] Fusion105  label="plugHousing062"
  Shapes = -> [Fusion103,Cut046]
FEATURE [Part::Fillet] Fillet042
  Base = -> Fusion105
  Edges = 1 edges r=2: [Edge25]
FEATURE [Part::Fillet] Fillet043  label="plugHousing063"
  Base = -> Fillet042
  Edges = 1 edges r=2: [Edge8]
  Placement = pos=(7,0,0) rot=(0,0,1;0rad)
FEATURE [Part::Feature] Face127
  shape: bbox 10 x 16.5 x 2e-07 mm, 1 faces, 0 solids (baked)
FEATURE [Part::Feature] Face128
  shape: bbox 10 x 16.5 x 2e-07 mm, 1 faces, 0 solids (baked)
FEATURE [Part::Revolution] Revolve137  label="plugHousing070"
  Angle = 360
  Axis = (0,1,0)
  Base = (0,0,0)
  FaceMakerClass = Part::FaceMakerBullseye
  Placement = pos=(0,0,36.15) rot=(0,0,1;0rad)
  Solid = false
  Source = -> Face127
  Symmetric = false
FEATURE [Part::Revolution] Revolve140  label="plugHousing073"
  Angle = 360
  Axis = (0,1,0)
  Base = (0,0,0)
  FaceMakerClass = Part::FaceMakerBullseye
  Placement = pos=(0,0,36.15) rot=(0,0,1;0rad)
  Solid = false
  Source = -> Face128
  Symmetric = false
FEATURE [Part::Feature] Face129
  shape: bbox 10 x 16.5 x 2e-07 mm, 1 faces, 0 solids (baked)
FEATURE [Part::Revolution] Revolve138  label="plugHousing071"
  Angle = 360
  Axis = (0,1,0)
  Base = (0,0,0)
  FaceMakerClass = Part::FaceMakerBullseye
  Placement = pos=(0,0,36.15) rot=(0,0,1;0rad)
  Solid = false
  Source = -> Face129
  Symmetric = false
FEATURE [Part::Feature] Face130
  shape: bbox 10 x 16.5 x 2e-07 mm, 1 faces, 0 solids (baked)
FEATURE [Part::Revolution] Revolve139  label="plugHousing072"
  Angle = 360
  Axis = (0,1,0)
  Base = (0,0,0)
  FaceMakerClass = Part::FaceMakerBullseye
  Placement = pos=(0,0,36.15) rot=(0,0,1;0rad)
  Solid = false
  Source = -> Face130
  Symmetric = false
FEATURE [Part::Feature] Face131
  shape: bbox 10 x 16.5 x 2e-07 mm, 1 faces, 0 solids (baked)
FEATURE [Part::Revolution] Revolve135  label="plugHousing068"
  Angle = 360
  Axis = (0,1,0)
  Base = (0,0,0)
  FaceMakerClass = Part::FaceMakerBullseye
  Placement = pos=(0,0,36.15) rot=(0,0,1;0rad)
  Solid = false
  Source = -> Face131
  Symmetric = false
FEATURE [Part::MultiFuse] Fusion112  label="plugHousing078"
  Placement = pos=(0,0,0) rot=(0,0,1;1.5708rad)
  Shapes = -> [Revolve135,Revolve139]
FEATURE [Part::Feature] Face132
  shape: bbox 10 x 16.5 x 2e-07 mm, 1 faces, 0 solids (baked)
FEATURE [Part::Revolution] Revolve141  label="plugHousing074"
  Angle = 360
  Axis = (0,1,0)
  Base = (0,0,0)
  FaceMakerClass = Part::FaceMakerBullseye
  Placement = pos=(0,0,36.15) rot=(0,0,1;0rad)
  Solid = false
  Source = -> Face132
  Symmetric = false
FEATURE [Part::MultiFuse] Fusion110  label="plugHousing076"
  Placement = pos=(0,0,0) rot=(0,0,1;1.5708rad)
  Shapes = -> [Revolve141,Revolve140]
FEATURE [Part::Feature] Face133
  shape: bbox 10 x 16.5 x 2e-07 mm, 1 faces, 0 solids (baked)
FEATURE [Part::Revolution] Revolve136  label="plugHousing069"
  Angle = 360
  Axis = (0,1,0)
  Base = (0,0,0)
  FaceMakerClass = Part::FaceMakerBullseye
  Placement = pos=(0,0,36.15) rot=(0,0,1;0rad)
  Solid = false
  Source = -> Face133
  Symmetric = false
FEATURE [Part::MultiFuse] Fusion106  label="plugHousing064"
  Placement = pos=(0,0,0) rot=(0,0,1;1.5708rad)
  Shapes = -> [Revolve138,Revolve136]
FEATURE [Part::MultiFuse] Fusion108  label="plugHousing066"
  Placement = pos=(0,19,0) rot=(0,0,1;3.14159rad)
  Shapes = -> [Fusion106,Fusion112]
FEATURE [Part::Feature] Face134
  shape: bbox 10 x 16.5 x 2e-07 mm, 1 faces, 0 solids (baked)
FEATURE [Part::Revolution] Revolve142  label="plugHousing075"
  Angle = 360
  Axis = (0,1,0)
  Base = (0,0,0)
  FaceMakerClass = Part::FaceMakerBullseye
  Placement = pos=(0,0,36.15) rot=(0,0,1;0rad)
  Solid = false
  Source = -> Face134
  Symmetric = false
FEATURE [Part::MultiFuse] Fusion107  label="plugHousing065"
  Placement = pos=(0,0,0) rot=(0,0,1;1.5708rad)
  Shapes = -> [Revolve137,Revolve142]
FEATURE [Part::MultiFuse] Fusion111  label="plugHousing077"
  Placement = pos=(0,19,0) rot=(0,0,1;3.14159rad)
  Shapes = -> [Fusion110,Fusion107]
FEATURE [Part::MultiFuse] Fusion109  label="plugHousing067"
  Placement = pos=(131.236,0,-0.15) rot=(0,0,1;0rad)
  Shapes = -> [Fusion108,Fusion111]
FEATURE [Part::MultiFuse] Fusion113  label="plugHousing079"
  Shapes = -> [Fillet043,Fusion109]
FEATURE [Part::Feature] Face135
  shape: bbox 3.5 x 17.8 x 2e-07 mm, 1 faces, 0 solids (baked)
FEATURE [Part::Revolution] Revolve143  label="removeToCreateScrewAndThreadedInsertHole049"
  Angle = 360
  Axis = (0,1,0)
  Base = (0,0,0)
  FaceMakerClass = Part::FaceMakerBullseye
  Placement = pos=(12.5,0,10) rot=(0,0,1;0rad)
  Solid = false
  Source = -> Face135
  Symmetric = false
FEATURE [Part::Feature] Face136
  shape: bbox 3.5 x 17.8 x 2e-07 mm, 1 faces, 0 solids (baked)
FEATURE [Part::Revolution] Revolve144  label="removeToCreateScrewAndThreadedInsertHole050"
  Angle = 360
  Axis = (0,1,0)
  Base = (0,0,0)
  FaceMakerClass = Part::FaceMakerBullseye
  Placement = pos=(12.5,0,62) rot=(0,0,1;0rad)
  Solid = false
  Source = -> Face136
  Symmetric = false
FEATURE [Part::Feature] Face137
  shape: bbox 3.5 x 17.8 x 2e-07 mm, 1 faces, 0 solids (baked)
FEATURE [Part::Revolution] Revolve145  label="removeToCreateScrewAndThreadedInsertHole051"
  Angle = 360
  Axis = (0,1,0)
  Base = (0,0,0)
  FaceMakerClass = Part::FaceMakerBullseye
  Placement = pos=(89.5,0,68.5) rot=(0,0,1;0rad)
  Solid = false
  Source = -> Face137
  Symmetric = false
FEATURE [Part::Feature] Face138
  shape: bbox 3.5 x 17.8 x 2e-07 mm, 1 faces, 0 solids (baked)
FEATURE [Part::Revolution] Revolve146  label="removeToCreateScrewAndThreadedInsertHole052"
  Angle = 360
  Axis = (0,1,0)
  Base = (0,0,0)
  FaceMakerClass = Part::FaceMakerBullseye
  Placement = pos=(89.5,0,3.5) rot=(0,0,1;0rad)
  Solid = false
  Source = -> Face138
  Symmetric = false
FEATURE [Part::Feature] Face139
  shape: bbox 3.5 x 17.8 x 2e-07 mm, 1 faces, 0 solids (baked)
FEATURE [Part::Revolution] Revolve147  label="removeToCreateScrewAndThreadedInsertHole053"
  Angle = 360
  Axis = (0,1,0)
  Base = (0,0,0)
  FaceMakerClass = Part::FaceMakerBullseye
  Placement = pos=(109.5,4.7,3.5) rot=(0,0,1;0rad)
  Solid = false
  Source = -> Face139
  Symmetric = false
FEATURE [Part::Feature] Face140
  shape: bbox 3.5 x 17.8 x 2e-07 mm, 1 faces, 0 solids (baked)
FEATURE [Part::Revolution] Revolve148  label="removeToCreateScrewAndThreadedInsertHole054"
  Angle = 360
  Axis = (0,1,0)
  Base = (0,0,0)
  FaceMakerClass = Part::FaceMakerBullseye
  Placement = pos=(109.5,4.7,68.5) rot=(0,0,1;0rad)
  Solid = false
  Source = -> Face140
  Symmetric = false
FEATURE [Part::MultiFuse] Fusion114  label="removeToCreateScrewAndThreadedInsertHole055"
  Shapes = -> [Revolve148,Revolve147,Revolve146,Revolve145,Revolve144,Revolve143]
FEATURE [Part::Cut] Cut047  label="casePillars004"
  Base = -> Cut037
  Tool = -> Fusion114
FEATURE [Part::Feature] Face141
  shape: bbox 3.5 x 17.8 x 2e-07 mm, 1 faces, 0 solids (baked)
FEATURE [Part::Feature] Face142
  shape: bbox 3.5 x 17.8 x 2e-07 mm, 1 faces, 0 solids (baked)
FEATURE [Part::Feature] Face143
  shape: bbox 3.5 x 17.8 x 2e-07 mm, 1 faces, 0 solids (baked)
FEATURE [Part::Revolution] Revolve149  label="removeToCreateScrewAndThreadedInsertHole057"
  Angle = 360
  Axis = (0,1,0)
  Base = (0,0,0)
  FaceMakerClass = Part::FaceMakerBullseye
  Placement = pos=(12.5,0,10) rot=(0,0,1;0rad)
  Solid = false
  Source = -> Face141
  Symmetric = false
FEATURE [Part::Feature] Face144
  shape: bbox 3.5 x 17.8 x 2e-07 mm, 1 faces, 0 solids (baked)
FEATURE [Part::Feature] Face145
  shape: bbox 3.5 x 17.8 x 2e-07 mm, 1 faces, 0 solids (baked)
FEATURE [Part::Feature] Face146
  shape: bbox 3.5 x 17.8 x 2e-07 mm, 1 faces, 0 solids (baked)
FEATURE [Part::Revolution] Revolve150  label="removeToCreateScrewAndThreadedInsertHole058"
  Angle = 360
  Axis = (0,1,0)
  Base = (0,0,0)
  FaceMakerClass = Part::FaceMakerBullseye
  Placement = pos=(12.5,0,62) rot=(0,0,1;0rad)
  Solid = false
  Source = -> Face146
  Symmetric = false
FEATURE [Part::Revolution] Revolve151  label="removeToCreateScrewAndThreadedInsertHole059"
  Angle = 360
  Axis = (0,1,0)
  Base = (0,0,0)
  FaceMakerClass = Part::FaceMakerBullseye
  Placement = pos=(89.5,0,68.5) rot=(0,0,1;0rad)
  Solid = false
  Source = -> Face143
  Symmetric = false
FEATURE [Part::Revolution] Revolve152  label="removeToCreateScrewAndThreadedInsertHole060"
  Angle = 360
  Axis = (0,1,0)
  Base = (0,0,0)
  FaceMakerClass = Part::FaceMakerBullseye
  Placement = pos=(89.5,0,3.5) rot=(0,0,1;0rad)
  Solid = false
  Source = -> Face142
  Symmetric = false
FEATURE [Part::Revolution] Revolve153  label="removeToCreateScrewAndThreadedInsertHole061"
  Angle = 360
  Axis = (0,1,0)
  Base = (0,0,0)
  FaceMakerClass = Part::FaceMakerBullseye
  Placement = pos=(109.5,4.7,3.5) rot=(0,0,1;0rad)
  Solid = false
  Source = -> Face145
  Symmetric = false
FEATURE [Part::Revolution] Revolve154  label="removeToCreateScrewAndThreadedInsertHole062"
  Angle = 360
  Axis = (0,1,0)
  Base = (0,0,0)
  FaceMakerClass = Part::FaceMakerBullseye
  Placement = pos=(109.5,4.7,68.5) rot=(0,0,1;0rad)
  Solid = false
  Source = -> Face144
  Symmetric = false
FEATURE [Part::MultiFuse] Fusion115  label="removeToCreateScrewAndThreadedInsertHole056"
  Shapes = -> [Revolve154,Revolve153,Revolve152,Revolve151,Revolve150,Revolve149]
FEATURE [Part::Feature] Face147
  shape: bbox 9.8 x 26.5 x 2e-07 mm, 1 faces, 0 solids (baked)
FEATURE [Part::Revolution] Revolve155
  Angle = 360
  Axis = (0,1,0)
  Base = (0,0,0)
  FaceMakerClass = Part::FaceMakerBullseye
  Placement = pos=(0,0,0) rot=(0,0,1;1.5708rad)
  Solid = false
  Source = -> Face147
  Symmetric = false
FEATURE [Part::Feature] Face148
  shape: bbox 9.8 x 26.5 x 2e-07 mm, 1 faces, 0 solids (baked)
FEATURE [Part::Revolution] Revolve156
  Angle = 360
  Axis = (0,1,0)
  Base = (0,0,0)
  FaceMakerClass = Part::FaceMakerBullseye
  Placement = pos=(0,0,0) rot=(0,0,1;1.5708rad)
  Solid = false
  Source = -> Face148
  Symmetric = false
FEATURE [Part::MultiFuse] Fusion116
  Placement = pos=(-18,19,36) rot=(0,0,1;0rad)
  Shapes = -> [Revolve156,Revolve155]
FEATURE [Part::Box] Box029  label="Cube016"
  AttacherType = Attacher::AttachEngine3D
  Height = 28
  Length = 3
  Placement = pos=(110.7,19,22) rot=(0,0,1;0rad)
  Width = 15.7
FEATURE [Part::Cylinder] Cylinder046
  Angle = 360
  AttacherType = Attacher::AttachEngine3D
  Height = 10
  Placement = pos=(0,0,36.15) rot=(0,0,1;0rad)
  Radius = 4
FEATURE [Part::Cylinder] Cylinder047
  Angle = 360
  AttacherType = Attacher::AttachEngine3D
  Height = 20
  Placement = pos=(0,0,36.15) rot=(0,0,1;0rad)
  Radius = 10.3
FEATURE [Part::MultiFuse] Fusion117  label="removeToCreteHoleForPlugHousing041"
  Placement = pos=(70,19,36) rot=(0,1,0;1.5708rad)
  Shapes = -> [Cylinder047,Cylinder046]
FEATURE [Part::Cut] Cut049  label="plugHousingTab004"
  Base = -> Box029
  Placement = pos=(-107.4,-14,0) rot=(0,0,1;0rad)
  Tool = -> Fusion117
FEATURE [Part::Box] Box030  label="Cube017"
  AttacherType = Attacher::AttachEngine3D
  Height = 28
  Length = 3
  Placement = pos=(110.7,19,22) rot=(0,0,1;0rad)
  Width = 15.7
FEATURE [Part::Cylinder] Cylinder048
  Angle = 360
  AttacherType = Attacher::AttachEngine3D
  Height = 10
  Placement = pos=(0,0,36.15) rot=(0,0,1;0rad)
  Radius = 4
FEATURE [Part::Cylinder] Cylinder049
  Angle = 360
  AttacherType = Attacher::AttachEngine3D
  Height = 20
  Placement = pos=(0,0,36.15) rot=(0,0,1;0rad)
  Radius = 10.3
FEATURE [Part::MultiFuse] Fusion118  label="removeToCreteHoleForPlugHousing042"
  Placement = pos=(70,19,36) rot=(0,1,0;1.5708rad)
  Shapes = -> [Cylinder049,Cylinder048]
FEATURE [Part::Cut] Cut050  label="plugHousingTab005"
  Base = -> Box030
  Placement = pos=(-107.4,-14,0) rot=(0,0,1;0rad)
  Tool = -> Fusion118
FEATURE [Part::MultiFuse] Fusion119
  Placement = pos=(9.6,23,0) rot=(0,0,1;3.14159rad)
  Shapes = -> [Cut049,Cut050]
FEATURE [Part::Box] Box031  label="Cube018"
  AttacherType = Attacher::AttachEngine3D
  Height = 10
  Length = 3
  Placement = pos=(3.3,4,12) rot=(0,0,1;0rad)
  Width = 10
FEATURE [Part::Fillet] Fillet044
  Base = -> Box031
  Edges = 1 edges r=2: [Edge11]
FEATURE [Part::Box] Box032  label="Cube019"
  AttacherType = Attacher::AttachEngine3D
  Height = 10
  Length = 3
  Placement = pos=(3.3,4,50) rot=(0,0,1;0rad)
  Width = 10
FEATURE [Part::Fillet] Fillet045
  Base = -> Box032
  Edges = 1 edges r=2: [Edge12]
FEATURE [Part::Box] Box033  label="Cube020"
  AttacherType = Attacher::AttachEngine3D
  Height = 28
  Length = 4
  Placement = pos=(5,0,22) rot=(0,0,1;0rad)
  Width = 10
FEATURE [Part::Fillet] Fillet046
  Base = -> Box033
  Edges = 1 edges r=1: [Edge7]
FEATURE [Part::Fillet] Fillet047
  Base = -> Fillet046
  Edges = 1 edges r=2: [Edge5]
FEATURE [Part::Fillet] Fillet048
  Base = -> Fillet047
  Edges = 1 edges r=2: [Edge2]
FEATURE [Part::Cylinder] Cylinder050
  Angle = 360
  AttacherType = Attacher::AttachEngine3D
  Height = 20
  Placement = pos=(0,0,36.15) rot=(0,0,1;0rad)
  Radius = 8.2
FEATURE [Part::Cylinder] Cylinder051
  Angle = 360
  AttacherType = Attacher::AttachEngine3D
  Height = 10
  Placement = pos=(0,0,36.15) rot=(0,0,1;0rad)
  Radius = 4
FEATURE [Part::MultiFuse] Fusion120  label="removeToCreteHoleForPlugHousing043"
  Placement = pos=(-42,19,36) rot=(0,1,0;1.5708rad)
  Shapes = -> [Cylinder050,Cylinder051]
FEATURE [Sketcher::SketchObject] Sketch067  label="topSketch018"
  FullyConstrained = true
  sketch-geometry (4):
    g0: LineSegment StartX=16.8446 StartY=31.512 StartZ=0 EndX=16.3251 EndY=34.4666 EndZ=0
    g1: ArcOfCircle CenterX=19 CenterY=19.2524 CenterZ=0 NormalX=0 NormalY=0 NormalZ=1 AngleXU=0 Radius=15.4476 StartAngle=1.74483 EndAngle=2.72717
    g2: ArcOfCircle CenterX=19 CenterY=19.2524 CenterZ=0 NormalX=0 NormalY=0 NormalZ=1 AngleXU=0 Radius=12.4476 StartAngle=1.74483 EndAngle=2.73189
    g3: LineSegment StartX=4.86004 StartY=25.4725 StartZ=0 EndX=7.58253 EndY=24.2107 EndZ=0
  constraints (7):
    c: Block(g0)
    c: Coincident(g1,g0)
    c: Coincident(g2,g0)
    c: Coincident(g3,g1)
    c: Coincident(g3,g2)
    c: Block(g1)
    c: Block(g2)
FEATURE [Part::Extrusion] Extrude058
  Base = -> Sketch067
  Dir = (0,0,1)
  DirMode = 2
  FaceMakerClass = Part::FaceMakerBullseye
  LengthFwd = 10
  LengthRev = 0
  Placement = pos=(0,0,31) rot=(0,0,1;0rad)
  Solid = true
  Symmetric = false
FEATURE [Part::Cut] Cut051
  Base = -> Extrude058
  Tool = -> Fusion120
FEATURE [Part::Fillet] Fillet049
  Base = -> Cut051
  Edges = 1 edges r=2: [Edge1]
FEATURE [Part::Fillet] Fillet050
  Base = -> Fillet049
  Edges = 1 edges r=2.5: [Edge1]
FEATURE [Part::Fillet] Fillet051
  Base = -> Fillet050
  Edges = 1 edges r=2.5: [Edge2]
FEATURE [Part::MultiFuse] Fusion121  label="wireHolder003"
  Shapes = -> [Fusion116,Fillet051]
FEATURE [Part::MultiFuse] Fusion122
  Shapes = -> [Fillet045,Fusion121]
FEATURE [Part::MultiFuse] Fusion123  label="wireHolder004"
  Shapes = -> [Fusion122,Fillet048]
FEATURE [Part::MultiFuse] Fusion124  label="wireHolder005"
  Shapes = -> [Fillet044,Fusion119,Fusion123]
FEATURE [Sketcher::SketchObject] Sketch068  label="topSketch019"
  FullyConstrained = true
  sketch-geometry (6):
    g0: LineSegment StartX=19 StartY=38 StartZ=0 EndX=117 EndY=38 EndZ=0
    g1: ArcOfCircle CenterX=19 CenterY=19 CenterZ=0 NormalX=0 NormalY=0 NormalZ=1 AngleXU=0 Radius=19 StartAngle=1.5708 EndAngle=3.14159
    g2: LineSegment StartX=117 StartY=38 StartZ=0 EndX=117 EndY=19 EndZ=0
    g3: LineSegment StartX=98 StartY=1.0161e-12 StartZ=0 EndX=5.22862e-06 EndY=1.0161e-12 EndZ=0
    g4: LineSegment StartX=5.22862e-06 StartY=19 StartZ=0 EndX=5.22862e-06 EndY=1.0161e-12 EndZ=0
    g5: ArcOfCircle CenterX=98 CenterY=19 CenterZ=0 NormalX=0 NormalY=0 NormalZ=1 AngleXU=0 Radius=19 StartAngle=4.71239 EndAngle=6.28319
  constraints (16):
    c: Horizontal(g0)
    c: Distance(g0) = 98
    c: Coincident(g1,g0)
    c: Block(g1)
    c: Coincident(g2,g0)
    c: Vertical(g2)
    c: Distance(g2) = 19
    c: Horizontal(g3)
    c: Coincident(g4,g1)
    c: Vertical(g4)
    c: Coincident(g3,g4)
    c: Block(g3)
    c: Coincident(g5,g2)
    c: Coincident(g5,g3)
    c: Block(g0)
    c: Block(g5)
FEATURE [Part::Extrusion] Extrude059  label="sideA002"
  Base = -> Sketch068
  Dir = (0,0,1)
  DirMode = 2
  FaceMakerClass = Part::FaceMakerBullseye
  LengthFwd = 3
  LengthRev = 0
  Placement = pos=(0,0,-2.7) rot=(0,0,1;0rad)
  Solid = true
  Symmetric = false
FEATURE [Sketcher::SketchObject] Sketch069  label="topSketch020"
  FullyConstrained = true
  sketch-geometry (6):
    g0: LineSegment StartX=19 StartY=38 StartZ=0 EndX=117 EndY=38 EndZ=0
    g1: ArcOfCircle CenterX=19 CenterY=19 CenterZ=0 NormalX=0 NormalY=0 NormalZ=1 AngleXU=0 Radius=19 StartAngle=1.5708 EndAngle=3.14159
    g2: LineSegment StartX=117 StartY=38 StartZ=0 EndX=117 EndY=19 EndZ=0
    g3: LineSegment StartX=98 StartY=1.0161e-12 StartZ=0 EndX=5.22862e-06 EndY=1.0161e-12 EndZ=0
    g4: LineSegment StartX=5.22862e-06 StartY=19 StartZ=0 EndX=5.22862e-06 EndY=1.0161e-12 EndZ=0
    g5: ArcOfCircle CenterX=98 CenterY=19 CenterZ=0 NormalX=0 NormalY=0 NormalZ=1 AngleXU=0 Radius=19 StartAngle=4.71239 EndAngle=6.28319
  constraints (16):
    c: Horizontal(g0)
    c: Distance(g0) = 98
    c: Coincident(g1,g0)
    c: Block(g1)
    c: Coincident(g2,g0)
    c: Vertical(g2)
    c: Distance(g2) = 19
    c: Horizontal(g3)
    c: Coincident(g4,g1)
    c: Vertical(g4)
    c: Coincident(g3,g4)
    c: Block(g3)
    c: Coincident(g5,g2)
    c: Coincident(g5,g3)
    c: Block(g0)
    c: Block(g5)
FEATURE [Part::Extrusion] Extrude060  label="sideB002"
  Base = -> Sketch069
  Dir = (0,0,1)
  DirMode = 2
  FaceMakerClass = Part::FaceMakerBullseye
  LengthFwd = 3
  LengthRev = 0
  Placement = pos=(0,0,71.7) rot=(0,0,1;0rad)
  Solid = true
  Symmetric = false
FEATURE [Part::MultiFuse] Fusion127  label="removeFromBottom001"
  Placement = pos=(2,0,0) rot=(0,0,1;0rad)
  Shapes = -> [Extrude059,Extrude060]
FEATURE [Part::Cylinder] Cylinder052
  Angle = 360
  AttacherType = Attacher::AttachEngine3D
  Height = 20
  Placement = pos=(0,0,36.15) rot=(0,0,1;0rad)
  Radius = 14
FEATURE [Part::Cylinder] Cylinder053
  Angle = 360
  AttacherType = Attacher::AttachEngine3D
  Height = 10
  Placement = pos=(0,0,36.15) rot=(0,0,1;0rad)
  Radius = 4
FEATURE [Part::MultiFuse] Fusion128  label="removeToCreteHoleForPlugHousing044"
  Placement = pos=(70,19,36) rot=(0,1,0;1.5708rad)
  Shapes = -> [Cylinder052,Cylinder053]
FEATURE [Part::Cut] Cut052  label="bottom011"
  Base = -> Extrude043
  Tool = -> Fusion128
FEATURE [Part::Cut] Cut054  label="bottom012"
  Base = -> Cut052
  Tool = -> Fusion115
FEATURE [Sketcher::SketchObject] Sketch070
  FullyConstrained = true
  Placement = pos=(117,19,0) rot=(0.57735,0.57735,0.57735;2.0944rad)
  sketch-geometry (48):
    g0: LineSegment StartX=-49.19 StartY=69.25 StartZ=0 EndX=-49.19 EndY=66.25 EndZ=0
    g1: LineSegment StartX=-49.19 StartY=63.5 StartZ=0 EndX=-49.19 EndY=60.5 EndZ=0
    g2: LineSegment StartX=-49.19 StartY=57.75 StartZ=0 EndX=-49.19 EndY=54.75 EndZ=0
    g3: LineSegment StartX=-49.19 StartY=52 StartZ=0 EndX=-49.19 EndY=49 EndZ=0
    g4: LineSegment StartX=-49.19 StartY=46.25 StartZ=0 EndX=-49.19 EndY=43.25 EndZ=0
    g5: LineSegment StartX=-49.19 StartY=40.5 StartZ=0 EndX=-49.19 EndY=37.5 EndZ=0
    g6: LineSegment StartX=-49.19 StartY=34.5 StartZ=0 EndX=-49.19 EndY=31.5 EndZ=0
    g7: LineSegment StartX=-49.19 StartY=28.75 StartZ=0 EndX=-49.19 EndY=25.75 EndZ=0
    g8: LineSegment StartX=-49.19 StartY=23 StartZ=0 EndX=-49.19 EndY=20 EndZ=0
    g9: LineSegment StartX=-49.19 StartY=17.25 StartZ=0 EndX=-49.19 EndY=14.25 EndZ=0
    g10: LineSegment StartX=-49.19 StartY=11.5 StartZ=0 EndX=-49.19 EndY=8.5 EndZ=0
    g11: LineSegment StartX=-49.19 StartY=5.75 StartZ=0 EndX=-49.19 EndY=2.75 EndZ=0
    g12: ArcOfCircle CenterX=-1.5 CenterY=67.75 CenterZ=0 NormalX=0 NormalY=0 NormalZ=1 AngleXU=0 Radius=1.5 StartAngle=4.71239 EndAngle=7.85398
    g13: ArcOfCircle CenterX=-1.5 CenterY=62 CenterZ=0 NormalX=0 NormalY=0 NormalZ=1 AngleXU=0 Radius=1.5 StartAngle=4.71239 EndAngle=7.85398
    g14: ArcOfCircle CenterX=-1.5 CenterY=56.25 CenterZ=0 NormalX=0 NormalY=0 NormalZ=1 AngleXU=0 Radius=1.5 StartAngle=4.71239 EndAngle=7.85398
    g15: ArcOfCircle CenterX=-11.49 CenterY=50.5 CenterZ=0 NormalX=0 NormalY=0 NormalZ=1 AngleXU=0 Radius=1.5 StartAngle=4.71239 EndAngle=7.85398
    g16: ArcOfCircle CenterX=-16.28 CenterY=44.75 CenterZ=0 NormalX=0 NormalY=0 NormalZ=1 AngleXU=0 Radius=1.5 StartAngle=4.71239 EndAngle=7.85398
    g17: ArcOfCircle CenterX=-18.2337 CenterY=39 CenterZ=0 NormalX=0 NormalY=0 NormalZ=1 AngleXU=0 Radius=1.5 StartAngle=4.71485 EndAngle=7.85398
    g18: ArcOfCircle CenterX=-16.2837 CenterY=27.25 CenterZ=0 NormalX=0 NormalY=0 NormalZ=1 AngleXU=0 Radius=1.5 StartAngle=4.71485 EndAngle=7.85398
    g19: ArcOfCircle CenterX=-18.2337 CenterY=33 CenterZ=0 NormalX=0 NormalY=0 NormalZ=1 AngleXU=0 Radius=1.5 StartAngle=4.71485 EndAngle=7.85398
    g20: ArcOfCircle CenterX=-11.49 CenterY=21.5 CenterZ=0 NormalX=0 NormalY=0 NormalZ=1 AngleXU=0 Radius=1.5 StartAngle=4.71239 EndAngle=7.85398
    g21: ArcOfCircle CenterX=-1.5 CenterY=4.25 CenterZ=0 NormalX=0 NormalY=0 NormalZ=1 AngleXU=0 Radius=1.5 StartAngle=4.71239 EndAngle=7.85398
    g22: ArcOfCircle CenterX=-1.5 CenterY=10 CenterZ=0 NormalX=0 NormalY=0 NormalZ=1 AngleXU=0 Radius=1.5 StartAngle=4.71239 EndAngle=7.85398
    g23: ArcOfCircle CenterX=-1.5 CenterY=15.75 CenterZ=0 NormalX=0 NormalY=0 NormalZ=1 AngleXU=0 Radius=1.5 StartAngle=4.71239 EndAngle=7.85398
    g24: LineSegment StartX=-49.19 StartY=69.25 StartZ=0 EndX=-1.5 EndY=69.25 EndZ=0
    g25: LineSegment StartX=-49.19 StartY=66.25 StartZ=0 EndX=-1.5 EndY=66.25 EndZ=0
    g26: LineSegment StartX=-49.19 StartY=63.5 StartZ=0 EndX=-1.5 EndY=63.5 EndZ=0
    g27: LineSegment StartX=-49.19 StartY=60.5 StartZ=0 EndX=-1.5 EndY=60.5 EndZ=0
    g28: LineSegment StartX=-49.19 StartY=57.75 StartZ=0 EndX=-1.5 EndY=57.75 EndZ=0
    g29: LineSegment StartX=-49.19 StartY=54.75 StartZ=0 EndX=-1.5 EndY=54.75 EndZ=0
    g30: LineSegment StartX=-49.19 StartY=52 StartZ=0 EndX=-11.49 EndY=52 EndZ=0
    g31: LineSegment StartX=-49.19 StartY=49 StartZ=0 EndX=-11.49 EndY=49 EndZ=0
    g32: LineSegment StartX=-49.19 StartY=46.25 StartZ=0 EndX=-16.28 EndY=46.25 EndZ=0
    g33: LineSegment StartX=-49.19 StartY=43.25 StartZ=0 EndX=-16.28 EndY=43.25 EndZ=0
    g34: LineSegment StartX=-49.19 StartY=40.5 StartZ=0 EndX=-18.2337 EndY=40.5 EndZ=0
    g35: LineSegment StartX=-49.19 StartY=37.5 StartZ=0 EndX=-18.23 EndY=37.5 EndZ=0
    g36: LineSegment StartX=-49.19 StartY=34.5 StartZ=0 EndX=-18.2337 EndY=34.5 EndZ=0
    g37: LineSegment StartX=-49.19 StartY=31.5 StartZ=0 EndX=-18.23 EndY=31.5 EndZ=0
    g38: LineSegment StartX=-49.19 StartY=28.75 StartZ=0 EndX=-16.2837 EndY=28.75 EndZ=0
    g39: LineSegment StartX=-49.19 StartY=25.75 StartZ=0 EndX=-16.28 EndY=25.75 EndZ=0
    g40: LineSegment StartX=-49.19 StartY=23 StartZ=0 EndX=-11.49 EndY=23 EndZ=0
    g41: LineSegment StartX=-49.19 StartY=20 StartZ=0 EndX=-11.49 EndY=20 EndZ=0
    g42: LineSegment StartX=-49.19 StartY=17.25 StartZ=0 EndX=-1.5 EndY=17.25 EndZ=0
    g43: LineSegment StartX=-49.19 StartY=14.25 StartZ=0 EndX=-1.5 EndY=14.25 EndZ=0
    g44: LineSegment StartX=-49.19 StartY=11.5 StartZ=0 EndX=-1.5 EndY=11.5 EndZ=0
    g45: LineSegment StartX=-49.19 StartY=8.5 StartZ=0 EndX=-1.5 EndY=8.5 EndZ=0
    g46: LineSegment StartX=-49.19 StartY=5.75 StartZ=0 EndX=-1.5 EndY=5.75 EndZ=0
    g47: LineSegment StartX=-49.19 StartY=2.75 StartZ=0 EndX=-1.5 EndY=2.75 EndZ=0
  constraints (120):
    c: Vertical(g0)
    c: Distance(g0) = 3
    c: Block(g0)
    c: Vertical(g1)
    c: Distance(g1) = 3
    c: Vertical(g2)
    c: Equal(g0,g2) = 3
    c: Block(g2)
    c: Vertical(g3)
    c: Equal(g1,g3) = 3
    c: Vertical(g4)
    c: Equal(g0,g4) = 3
    c: Block(g4)
    c: Vertical(g5)
    c: Equal(g1,g5) = 3
    c: Vertical(g6)
    c: Equal(g0,g6) = 3
    c: Block(g6)
    c: Vertical(g7)
    c: Equal(g1,g7) = 3
    c: Vertical(g8)
    c: Equal(g0,g8) = 3
    c: Block(g8)
    c: Vertical(g9)
    c: Equal(g1,g9) = 3
    c: Vertical(g10)
    c: Equal(g0,g10) = 3
    c: Block(g10)
    c: Vertical(g11)
    c: Equal(g1,g11) = 3
    c: Block(g12)
    c: Block(g13)
    c: Block(g14)
    c: Block(g15)
    c: Block(g16)
    c: Block(g17)
    c: Block(g18)
    c: Block(g19)
    c: Block(g20)
    c: Block(g21)
    c: Block(g22)
    c: Block(g23)
    c: Block(g11)
    c: Block(g9)
    c: Block(g7)
    c: Block(g5)
    c: Block(g3)
    c: Block(g1)
    c: Coincident(g24,g0)
    c: Coincident(g24,g12)
    c: Horizontal(g24)
    c: Coincident(g25,g0)
    c: Coincident(g25,g12)
    c: Horizontal(g25)
    c: Coincident(g26,g1)
    c: Coincident(g26,g13)
    c: Horizontal(g26)
    c: Coincident(g27,g1)
    c: Coincident(g27,g13)
    c: Horizontal(g27)
    c: Coincident(g28,g2)
    c: Coincident(g28,g14)
    c: Horizontal(g28)
    c: Coincident(g29,g2)
    c: Coincident(g29,g14)
    c: Horizontal(g29)
    c: Coincident(g30,g3)
    c: Coincident(g30,g15)
    c: Horizontal(g30)
    c: Coincident(g31,g3)
    c: Coincident(g31,g15)
    c: Horizontal(g31)
    c: Coincident(g32,g4)
    c: Coincident(g32,g16)
    c: Horizontal(g32)
    c: Coincident(g33,g4)
    c: Coincident(g33,g16)
    c: Horizontal(g33)
    c: Coincident(g34,g5)
    c: Coincident(g34,g17)
    c: Horizontal(g34)
    c: Coincident(g35,g5)
    c: Coincident(g35,g17)
    c: Horizontal(g35)
    c: Coincident(g36,g6)
    c: Coincident(g36,g19)
    c: Horizontal(g36)
    c: Coincident(g37,g6)
    c: Coincident(g37,g19)
    c: Horizontal(g37)
    c: Coincident(g38,g7)
    c: Coincident(g38,g18)
    c: Horizontal(g38)
    c: Coincident(g39,g7)
    c: Coincident(g39,g18)
    c: Horizontal(g39)
    c: Coincident(g40,g8)
    c: Coincident(g40,g20)
    c: Horizontal(g40)
    c: Coincident(g41,g8)
    c: Coincident(g41,g20)
    c: Horizontal(g41)
    c: Coincident(g42,g9)
    c: Coincident(g42,g23)
    c: Horizontal(g42)
    c: Coincident(g43,g9)
    c: Coincident(g43,g23)
    c: Horizontal(g43)
    c: Coincident(g44,g10)
    c: Coincident(g44,g22)
    c: Horizontal(g44)
    c: Coincident(g45,g10)
    c: Coincident(g45,g22)
    c: Horizontal(g45)
    c: Coincident(g46,g11)
    c: Coincident(g46,g21)
    c: Horizontal(g46)
    c: Coincident(g47,g11)
    c: Coincident(g47,g21)
    c: Horizontal(g47)
FEATURE [Part::Extrusion] Extrude061
  Base = -> Sketch070
  Dir = (1,0,0)
  DirMode = 2
  FaceMakerClass = Part::FaceMakerBullseye
  LengthFwd = 23
  LengthRev = 0
  Placement = pos=(-19,0,0) rot=(0,0,1;0rad)
  Solid = true
  Symmetric = false
FEATURE [Part::Fillet] Fillet052  label="removeToCreateVentalationHoles002"
  Base = -> Extrude061
  Edges = <same value as first occurrence — deduplicated (x6 in doc)>
  Placement = pos=(7,0.02,0) rot=(0,0,1;0rad)
FEATURE [Part::MultiFuse] Fusion130  label="bottom013"
  Shapes = -> [Cut054,Cut034]
FEATURE [Part::Cut] Cut055
  Base = -> Fusion130
  Tool = -> Fillet052
FEATURE [Part::Cylinder] Cylinder054
  Angle = 360
  AttacherType = Attacher::AttachEngine3D
  Height = 20
  Placement = pos=(0,0,36.15) rot=(0,0,1;0rad)
  Radius = 4
FEATURE [Sketcher::SketchObject] Sketch071  label="bottomSketch002"
  FullyConstrained = true
  sketch-geometry (32):
    g0: LineSegment StartX=3.3 StartY=-6.03275e-07 StartZ=0 EndX=98 EndY=-6.03275e-07 EndZ=0
    g1: ArcOfCircle CenterX=98 CenterY=19 CenterZ=0 NormalX=0 NormalY=0 NormalZ=1 AngleXU=0 Radius=19 StartAngle=4.71239 EndAngle=5.71103
    g2: LineSegment StartX=6.3 StartY=8 StartZ=0 EndX=3.3 EndY=8 EndZ=0
    g3: LineSegment StartX=3.3 StartY=8 StartZ=0 EndX=3.3 EndY=-6.03275e-07 EndZ=0
    g4: ArcOfCircle CenterX=8.3 CenterY=5 CenterZ=0 NormalX=0 NormalY=0 NormalZ=1 AngleXU=0 Radius=2 StartAngle=3.14159 EndAngle=4.71239
    g5: LineSegment StartX=6.3 StartY=8 StartZ=0 EndX=6.3 EndY=5 EndZ=0
    g6: ArcOfCircle CenterX=98 CenterY=19 CenterZ=0 NormalX=0 NormalY=0 NormalZ=1 AngleXU=0 Radius=12.7 StartAngle=4.71239 EndAngle=6.28319
    g7: LineSegment StartX=94.7 StartY=3 StartZ=0 EndX=8.3 EndY=3 EndZ=0
    g8-g12: Circle x5 (B-spline internal-alignment scaffolding for g13; pole/knot coordinates omitted)
    g13: BSplineCurve PolesCount=5 KnotsCount=3 Degree=3 IsPeriodic=0
    g14: GeomPoint X=98 Y=6.3 Z=0
    g15: GeomPoint X=96.3938 Y=4.71946 Z=0
    g16: GeomPoint X=94.7 Y=3 Z=0
    g17-g23: Circle x7 (B-spline internal-alignment scaffolding for g24; pole/knot coordinates omitted)
    g24: BSplineCurve PolesCount=7 KnotsCount=5 Degree=3 IsPeriodic=0
    g25-g29: GeomPoint x5 (B-spline internal-alignment scaffolding for g24; pole/knot coordinates omitted)
    g30: ArcOfCircle CenterX=98 CenterY=19 CenterZ=0 NormalX=0 NormalY=0 NormalZ=1 AngleXU=0 Radius=15.7 StartAngle=5.81226 EndAngle=6.28319
    g31: LineSegment StartX=110.7 StartY=19 StartZ=0 EndX=113.7 EndY=19 EndZ=0
  constraints (41):
    c: Horizontal(g0)
    c: Coincident(g1,g0)
    c: Block(g1)
    c: Horizontal(g2)
    c: Distance(g2) = 3
    c: Coincident(g3,g2)
    c: Vertical(g3)
    c: Coincident(g3,g0)
    c: Block(g4)
    c: Block(g2)
    c: Coincident(g5,g2)
    c: Coincident(g5,g4)
    c: Vertical(g5)
    c: Coincident(g6,g1)
    c: Block(g6)
    c: Coincident(g7,g4)
    c: Horizontal(g7)
    c: Block(g0)
    c: Block(g7)
    c: Block(g3)
    c: Coincident(g13,g6)
    c: Weight(g8) = 1
    c: Equal(g8, g9-g12) x4
    c: Coincident(g13,g7)
    c: InternalAlignment(g8-g12 -> g13) x5
    c: InternalAlignment(g14,g13)
    c: InternalAlignment(g15,g13)
    c: InternalAlignment(g16,g13)
    c: Block(g13)
    c: Weight(g17) = 1
    c: Equal(g17, g18-g23) x6
    c: Coincident(g24,g1)
    c: InternalAlignment(g17-g23 -> g24) x7
    c: InternalAlignment(g25-g29 -> g24) x5
    c: Block(g24)
    c: Coincident(g30,g24)
    c: Coincident(g31,g6)
    c: Coincident(g31,g30)
    c: Horizontal(g31)
    c: Block(g31)
    c: Block(g30)
FEATURE [Part::Extrusion] Extrude062  label="bottom014"
  Base = -> Sketch071
  Dir = (0,0,1)
  DirMode = 2
  FaceMakerClass = Part::FaceMakerBullseye
  LengthFwd = 71.4
  LengthRev = 0
  Placement = pos=(0,0,0.3) rot=(0,0,1;0rad)
  Solid = true
  Symmetric = false
FEATURE [Part::Fillet] Fillet054
  Base = -> Extrude062
  Edges = 1 edges r=2.4: [Edge17]
FEATURE [Part::Fillet] Fillet055  label="bottom015"
  Base = -> Fillet054
  Edges = 1 edges r=2.4: [Edge36]
FEATURE [Part::Cylinder] Cylinder055
  Angle = 360
  AttacherType = Attacher::AttachEngine3D
  Height = 10
  Placement = pos=(0,0,36.15) rot=(0,0,1;0rad)
  Radius = 4
FEATURE [Part::MultiFuse] Fusion131  label="removeToCreateHoleForPlugHousing002"
  Placement = pos=(70,19,36.15) rot=(0,1,0;1.5708rad)
  Shapes = -> [Cylinder054,Cylinder055]
FEATURE [Part::Cut] Cut056  label="Bottom001"
  Base = -> Fillet055
  Placement = pos=(9,0,0) rot=(0,0,1;0rad)
  Tool = -> Fusion131
FEATURE [Part::Cut] Cut057
  Base = -> Cut055
  Tool = -> Cut056
FEATURE [Sketcher::SketchObject] Sketch072  label="topSketch021"
  FullyConstrained = true
  sketch-geometry (4):
    g0: ArcOfCircle CenterX=105 CenterY=19 CenterZ=0 NormalX=0 NormalY=0 NormalZ=1 AngleXU=0 Radius=20.6155 StartAngle=5.54125 EndAngle=6.28319
    g1: ArcOfCircle CenterX=105 CenterY=19 CenterZ=0 NormalX=0 NormalY=0 NormalZ=1 AngleXU=0 Radius=13 StartAngle=5.54125 EndAngle=6.28319
    g2: LineSegment StartX=118 StartY=19 StartZ=0 EndX=125.616 EndY=19 EndZ=0
    g3: LineSegment StartX=114.583 StartY=10.2157 StartZ=0 EndX=120.197 EndY=5.06982 EndZ=0
  constraints (7):
    c: Block(g0)
    c: Block(g1)
    c: Coincident(g2,g1)
    c: Coincident(g2,g0)
    c: Horizontal(g2)
    c: Coincident(g3,g1)
    c: Coincident(g3,g0)
FEATURE [Part::Extrusion] Extrude063  label="bottomPlugHousingBit003"
  Base = -> Sketch072
  Dir = (0,0,1)
  DirMode = 2
  FaceMakerClass = Part::FaceMakerBullseye
  LengthFwd = 72
  LengthRev = 0
  Solid = true
  Symmetric = false
FEATURE [Part::Cylinder] Cylinder056
  Angle = 360
  AttacherType = Attacher::AttachEngine3D
  Height = 20
  Placement = pos=(0,0,36.15) rot=(0,0,1;0rad)
  Radius = 14.3
FEATURE [Part::Cylinder] Cylinder057
  Angle = 360
  AttacherType = Attacher::AttachEngine3D
  Height = 10
  Placement = pos=(0,0,36.15) rot=(0,0,1;0rad)
  Radius = 4
FEATURE [Part::Box] Box034  label="removeToCreteHoleForPlugHousing047"
  AttacherType = Attacher::AttachEngine3D
  Height = 28.6
  Length = 20
  Placement = pos=(106.15,0,21.7) rot=(0,0,1;0rad)
  Width = 19
FEATURE [Part::Cylinder] Cylinder058
  Angle = 360
  AttacherType = Attacher::AttachEngine3D
  Height = 20
  Placement = pos=(0,0,36.15) rot=(0,0,1;0rad)
  Radius = 14.3
FEATURE [Part::Cylinder] Cylinder059
  Angle = 360
  AttacherType = Attacher::AttachEngine3D
  Height = 10
  Placement = pos=(0,0,36.15) rot=(0,0,1;0rad)
  Radius = 4
FEATURE [Part::MultiFuse] Fusion134  label="removeToCreteHoleForPlugHousing046"
  Placement = pos=(70,19,36) rot=(0,1,0;1.5708rad)
  Shapes = -> [Cylinder058,Cylinder059]
FEATURE [Part::Cylinder] Cylinder060
  Angle = 360
  AttacherType = Attacher::AttachEngine3D
  Height = 20
  Placement = pos=(0,0,36.15) rot=(0,0,1;0rad)
  Radius = 14
FEATURE [Part::Cylinder] Cylinder061
  Angle = 360
  AttacherType = Attacher::AttachEngine3D
  Height = 10
  Placement = pos=(0,0,36.15) rot=(0,0,1;0rad)
  Radius = 4
FEATURE [Part::MultiFuse] Fusion135  label="removeToCreteHoleForPlugHousing048"
  Placement = pos=(70,19,36) rot=(0,1,0;1.5708rad)
  Shapes = -> [Cylinder060,Cylinder061]
FEATURE [Part::Box] Box035  label="removeToCreteHoleForPlugHousing049"
  AttacherType = Attacher::AttachEngine3D
  Height = 28.6
  Length = 20
  Placement = pos=(106.15,0,21.7) rot=(0,0,1;0rad)
  Width = 19
FEATURE [Part::MultiFuse] Fusion133  label="removeToCreteHoleForPlugHousing045"
  Placement = pos=(0,0,-28.3) rot=(0,0,1;0rad)
  Shapes = -> [Box035,Fusion134]
FEATURE [Part::MultiFuse] Fusion138  label="removeToCreteHoleForPlugHousing051"
  Placement = pos=(70,19,36) rot=(0,1,0;1.5708rad)
  Shapes = -> [Cylinder056,Cylinder057]
FEATURE [Part::MultiFuse] Fusion137  label="removeToCreteHoleForPlugHousing050"
  Placement = pos=(0,0,28.3) rot=(0,0,1;0rad)
  Shapes = -> [Box034,Fusion138]
FEATURE [Part::MultiFuse] Fusion132  label="removeToCreatePlugHousingBottomBit002"
  Shapes = -> [Fusion133,Fusion137]
FEATURE [Part::MultiFuse] Fusion136  label="removeToCreatePlugHousingBottomBit003"
  Shapes = -> [Fusion135,Fusion132]
FEATURE [Part::Cut] Cut058  label="bottomPlugHousingBit002"
  Base = -> Extrude063
  Placement = pos=(-0.09,0,0) rot=(0,0,1;0rad)
  Tool = -> Fusion136
FEATURE [Sketcher::SketchObject] Sketch073  label="bottomSketch003"
  FullyConstrained = true
  sketch-geometry (45):
    g0: LineSegment StartX=6.29999 StartY=8 StartZ=0 EndX=3.29999 EndY=8 EndZ=0
    g1: LineSegment StartX=3.29999 StartY=8 StartZ=0 EndX=3.29999 EndY=-6.03275e-07 EndZ=0
    g2: ArcOfCircle CenterX=8.29999 CenterY=5 CenterZ=0 NormalX=0 NormalY=0 NormalZ=1 AngleXU=0 Radius=2 StartAngle=3.14159 EndAngle=4.71239
    g3: LineSegment StartX=6.29999 StartY=8 StartZ=0 EndX=6.29999 EndY=5 EndZ=0
    g4: ArcOfCircle CenterX=105 CenterY=19 CenterZ=0 NormalX=0 NormalY=0 NormalZ=1 AngleXU=0 Radius=12.7 StartAngle=4.71239 EndAngle=5.94289
    g5-g11: Circle x7 (B-spline internal-alignment scaffolding for g12; pole/knot coordinates omitted)
    g12: BSplineCurve PolesCount=7 KnotsCount=5 Degree=3 IsPeriodic=0
    g13-g17: GeomPoint x5 (B-spline internal-alignment scaffolding for g12; pole/knot coordinates omitted)
    g18: ArcOfCircle CenterX=105 CenterY=19 CenterZ=0 NormalX=0 NormalY=0 NormalZ=1 AngleXU=0 Radius=15.7 StartAngle=5.81226 EndAngle=6.28319
    g19: BSplineCurve PolesCount=5 KnotsCount=3 Degree=3 IsPeriodic=0
    g20: LineSegment StartX=8.29999 StartY=3 StartZ=0 EndX=101.7 EndY=3 EndZ=0
    g21: LineSegment StartX=3.29999 StartY=-6.03275e-07 StartZ=0 EndX=105 EndY=-6.03275e-07 EndZ=0
    g22: LineSegment StartX=120.974 StartY=8.71251 StartZ=0 EndX=122.332 EndY=7.83778 EndZ=0
    g23: LineSegment StartX=105 StartY=-6.03274e-07 StartZ=0 EndX=113 EndY=-6.03274e-07 EndZ=0
    g24: ArcOfCircle CenterX=105 CenterY=19 CenterZ=0 NormalX=0 NormalY=0 NormalZ=1 AngleXU=0 Radius=20.6155 StartAngle=5.11091 EndAngle=5.71103
    g25: ArcOfCircle CenterX=117.7 CenterY=19 CenterZ=0 NormalX=0 NormalY=0 NormalZ=1 AngleXU=0 Radius=3 StartAngle=1.2e-15 EndAngle=2.10468
    g26: Circle CenterX=116.345 CenterY=16.3232 CenterZ=0 NormalX=0 NormalY=0 NormalZ=1 AngleXU=0 Radius=1
    g27: Circle CenterX=117.24 CenterY=15.7584 CenterZ=0 NormalX=0 NormalY=0 NormalZ=1 AngleXU=0 Radius=1
    g28: Circle CenterX=116.972 CenterY=14.7612 CenterZ=0 NormalX=0 NormalY=0 NormalZ=1 AngleXU=0 Radius=1
    g29: BSplineCurve PolesCount=3 KnotsCount=2 Degree=2 IsPeriodic=0
    g30: GeomPoint X=116.345 Y=16.3232 Z=0
    g31: GeomPoint X=116.972 Y=14.7612 Z=0
    g32: Circle CenterX=115.828 CenterY=17.157 CenterZ=0 NormalX=0 NormalY=0 NormalZ=1 AngleXU=0 Radius=1
    g33: Circle CenterX=115.841 CenterY=16.639 CenterZ=0 NormalX=0 NormalY=0 NormalZ=1 AngleXU=0 Radius=1
    g34: Circle CenterX=116.345 CenterY=16.3232 CenterZ=0 NormalX=0 NormalY=0 NormalZ=1 AngleXU=0 Radius=1
    g35: BSplineCurve PolesCount=3 KnotsCount=2 Degree=2 IsPeriodic=0
    g36: GeomPoint X=115.828 Y=17.157 Z=0
    g37: GeomPoint X=116.345 Y=16.3232 Z=0
    g38: LineSegment StartX=115.828 StartY=17.157 StartZ=0 EndX=115.828 EndY=20.8307 EndZ=0
    g39: Circle CenterX=115.828 CenterY=20.8307 CenterZ=0 NormalX=0 NormalY=0 NormalZ=1 AngleXU=0 Radius=1
    g40: Circle CenterX=115.831 CenterY=21.3396 CenterZ=0 NormalX=0 NormalY=0 NormalZ=1 AngleXU=0 Radius=1
    g41: Circle CenterX=116.173 CenterY=21.5825 CenterZ=0 NormalX=0 NormalY=0 NormalZ=1 AngleXU=0 Radius=1
    g42: BSplineCurve PolesCount=3 KnotsCount=2 Degree=2 IsPeriodic=0
    g43: GeomPoint X=115.828 Y=20.8307 Z=0
    g44: GeomPoint X=116.173 Y=21.5825 Z=0
  constraints (70):
    c: Horizontal(g0)
    c: Distance(g0) = 3
    c: Coincident(g1,g0)
    c: Vertical(g1)
    c: Block(g2)
    c: Block(g0)
    c: Coincident(g3,g0)
    c: Coincident(g3,g2)
    c: Vertical(g3)
    c: Block(g1)
    c: Block(g4)
    c: Coincident(g19,g4)
    c: Block(g19)
    c: Equal(g5, g6-g11) x6
    c: InternalAlignment(g5-g11 -> g12) x7
    c: InternalAlignment(g13-g17 -> g12) x5
    c: Block(g12)
    c: Coincident(g18,g12)
    c: Block(g18)
    c: Coincident(g20,g2)
    c: Coincident(g20,g19)
    c: Horizontal(g20)
    c: Distance(g20) = 93.4
    c: Coincident(g21,g1)
    c: Horizontal(g21)
    c: Distance(g21) = 101.7
    c: Horizontal(g23)
    c: Distance(g23) = 8
    c: Coincident(g24,g23)
    c: Block(g23)
    c: Coincident(g22,g24)
    c: Block(g24)
    c: Block(g22)
    c: Distance(g22) = 1.61553
    c: Coincident(g25,g18)
    c: Block(g25)
    c: Weight(g26) = 1
    c: Equal(g26,g27)
    c: Equal(g26,g28)
    c: Coincident(g29,g4)
    c: InternalAlignment(g26,g29)
    c: InternalAlignment(g27,g29)
    c: InternalAlignment(g28,g29)
    c: InternalAlignment(g30,g29)
    c: InternalAlignment(g31,g29)
    c: Block(g29)
    c: Weight(g32) = 1
    c: Equal(g32,g33)
    c: Equal(g32,g34)
    c: Coincident(g35,g29)
    c: InternalAlignment(g32,g35)
    c: InternalAlignment(g33,g35)
    c: InternalAlignment(g34,g35)
    c: InternalAlignment(g36,g35)
    c: InternalAlignment(g37,g35)
    c: Block(g35)
    c: Coincident(g38,g35)
    c: Vertical(g38)
    c: Block(g38)
    c: Coincident(g42,g38)
    c: Weight(g39) = 1
    c: Equal(g39,g40)
    c: Equal(g39,g41)
    c: Coincident(g42,g25)
    c: InternalAlignment(g39,g42)
    c: InternalAlignment(g40,g42)
    c: InternalAlignment(g41,g42)
    c: InternalAlignment(g43,g42)
    c: InternalAlignment(g44,g42)
    c: Block(g42)
FEATURE [Part::Extrusion] Extrude064  label="bottom016"
  Base = -> Sketch073
  Dir = (0,0,1)
  DirMode = 2
  FaceMakerClass = Part::FaceMakerBullseye
  LengthFwd = 71.4
  LengthRev = 0
  Placement = pos=(0,0,0.3) rot=(0,0,1;0rad)
  Solid = true
  Symmetric = false
FEATURE [Part::Revolution] Revolve157  label="removeToCreateScrewAndThreadedInsertHole063"
  Angle = 360
  Axis = (0,1,0)
  Base = (0,0,0)
  FaceMakerClass = Part::FaceMakerBullseye
  Placement = pos=(12.5,0,10) rot=(0,0,1;0rad)
  Solid = false
  Source = -> Face141
  Symmetric = false
FEATURE [Sketcher::SketchObject] Sketch074
  FullyConstrained = true
  Placement = pos=(117,19,0) rot=(0.57735,0.57735,0.57735;2.0944rad)
  sketch-geometry (48):
    g0: LineSegment StartX=-49.19 StartY=69.25 StartZ=0 EndX=-49.19 EndY=66.25 EndZ=0
    g1: LineSegment StartX=-49.19 StartY=63.5 StartZ=0 EndX=-49.19 EndY=60.5 EndZ=0
    g2: LineSegment StartX=-49.19 StartY=57.75 StartZ=0 EndX=-49.19 EndY=54.75 EndZ=0
    g3: LineSegment StartX=-49.19 StartY=52 StartZ=0 EndX=-49.19 EndY=49 EndZ=0
    g4: LineSegment StartX=-49.19 StartY=46.25 StartZ=0 EndX=-49.19 EndY=43.25 EndZ=0
    g5: LineSegment StartX=-49.19 StartY=40.5 StartZ=0 EndX=-49.19 EndY=37.5 EndZ=0
    g6: LineSegment StartX=-49.19 StartY=34.5 StartZ=0 EndX=-49.19 EndY=31.5 EndZ=0
    g7: LineSegment StartX=-49.19 StartY=28.75 StartZ=0 EndX=-49.19 EndY=25.75 EndZ=0
    g8: LineSegment StartX=-49.19 StartY=23 StartZ=0 EndX=-49.19 EndY=20 EndZ=0
    g9: LineSegment StartX=-49.19 StartY=17.25 StartZ=0 EndX=-49.19 EndY=14.25 EndZ=0
    g10: LineSegment StartX=-49.19 StartY=11.5 StartZ=0 EndX=-49.19 EndY=8.5 EndZ=0
    g11: LineSegment StartX=-49.19 StartY=5.75 StartZ=0 EndX=-49.19 EndY=2.75 EndZ=0
    g12: ArcOfCircle CenterX=-1.5 CenterY=67.75 CenterZ=0 NormalX=0 NormalY=0 NormalZ=1 AngleXU=0 Radius=1.5 StartAngle=4.71239 EndAngle=7.85398
    g13: ArcOfCircle CenterX=-1.5 CenterY=62 CenterZ=0 NormalX=0 NormalY=0 NormalZ=1 AngleXU=0 Radius=1.5 StartAngle=4.71239 EndAngle=7.85398
    g14: ArcOfCircle CenterX=-1.5 CenterY=56.25 CenterZ=0 NormalX=0 NormalY=0 NormalZ=1 AngleXU=0 Radius=1.5 StartAngle=4.71239 EndAngle=7.85398
    g15: ArcOfCircle CenterX=-11.49 CenterY=50.5 CenterZ=0 NormalX=0 NormalY=0 NormalZ=1 AngleXU=0 Radius=1.5 StartAngle=4.71239 EndAngle=7.85398
    g16: ArcOfCircle CenterX=-16.28 CenterY=44.75 CenterZ=0 NormalX=0 NormalY=0 NormalZ=1 AngleXU=0 Radius=1.5 StartAngle=4.71239 EndAngle=7.85398
    g17: ArcOfCircle CenterX=-18.2337 CenterY=39 CenterZ=0 NormalX=0 NormalY=0 NormalZ=1 AngleXU=0 Radius=1.5 StartAngle=4.71485 EndAngle=7.85398
    g18: ArcOfCircle CenterX=-16.2837 CenterY=27.25 CenterZ=0 NormalX=0 NormalY=0 NormalZ=1 AngleXU=0 Radius=1.5 StartAngle=4.71485 EndAngle=7.85398
    g19: ArcOfCircle CenterX=-18.2337 CenterY=33 CenterZ=0 NormalX=0 NormalY=0 NormalZ=1 AngleXU=0 Radius=1.5 StartAngle=4.71485 EndAngle=7.85398
    g20: ArcOfCircle CenterX=-11.49 CenterY=21.5 CenterZ=0 NormalX=0 NormalY=0 NormalZ=1 AngleXU=0 Radius=1.5 StartAngle=4.71239 EndAngle=7.85398
    g21: ArcOfCircle CenterX=-1.5 CenterY=4.25 CenterZ=0 NormalX=0 NormalY=0 NormalZ=1 AngleXU=0 Radius=1.5 StartAngle=4.71239 EndAngle=7.85398
    g22: ArcOfCircle CenterX=-1.5 CenterY=10 CenterZ=0 NormalX=0 NormalY=0 NormalZ=1 AngleXU=0 Radius=1.5 StartAngle=4.71239 EndAngle=7.85398
    g23: ArcOfCircle CenterX=-1.5 CenterY=15.75 CenterZ=0 NormalX=0 NormalY=0 NormalZ=1 AngleXU=0 Radius=1.5 StartAngle=4.71239 EndAngle=7.85398
    g24: LineSegment StartX=-49.19 StartY=69.25 StartZ=0 EndX=-1.5 EndY=69.25 EndZ=0
    g25: LineSegment StartX=-49.19 StartY=66.25 StartZ=0 EndX=-1.5 EndY=66.25 EndZ=0
    g26: LineSegment StartX=-49.19 StartY=63.5 StartZ=0 EndX=-1.5 EndY=63.5 EndZ=0
    g27: LineSegment StartX=-49.19 StartY=60.5 StartZ=0 EndX=-1.5 EndY=60.5 EndZ=0
    g28: LineSegment StartX=-49.19 StartY=57.75 StartZ=0 EndX=-1.5 EndY=57.75 EndZ=0
    g29: LineSegment StartX=-49.19 StartY=54.75 StartZ=0 EndX=-1.5 EndY=54.75 EndZ=0
    g30: LineSegment StartX=-49.19 StartY=52 StartZ=0 EndX=-11.49 EndY=52 EndZ=0
    g31: LineSegment StartX=-49.19 StartY=49 StartZ=0 EndX=-11.49 EndY=49 EndZ=0
    g32: LineSegment StartX=-49.19 StartY=46.25 StartZ=0 EndX=-16.28 EndY=46.25 EndZ=0
    g33: LineSegment StartX=-49.19 StartY=43.25 StartZ=0 EndX=-16.28 EndY=43.25 EndZ=0
    g34: LineSegment StartX=-49.19 StartY=40.5 StartZ=0 EndX=-18.2337 EndY=40.5 EndZ=0
    g35: LineSegment StartX=-49.19 StartY=37.5 StartZ=0 EndX=-18.23 EndY=37.5 EndZ=0
    g36: LineSegment StartX=-49.19 StartY=34.5 StartZ=0 EndX=-18.2337 EndY=34.5 EndZ=0
    g37: LineSegment StartX=-49.19 StartY=31.5 StartZ=0 EndX=-18.23 EndY=31.5 EndZ=0
    g38: LineSegment StartX=-49.19 StartY=28.75 StartZ=0 EndX=-16.2837 EndY=28.75 EndZ=0
    g39: LineSegment StartX=-49.19 StartY=25.75 StartZ=0 EndX=-16.28 EndY=25.75 EndZ=0
    g40: LineSegment StartX=-49.19 StartY=23 StartZ=0 EndX=-11.49 EndY=23 EndZ=0
    g41: LineSegment StartX=-49.19 StartY=20 StartZ=0 EndX=-11.49 EndY=20 EndZ=0
    g42: LineSegment StartX=-49.19 StartY=17.25 StartZ=0 EndX=-1.5 EndY=17.25 EndZ=0
    g43: LineSegment StartX=-49.19 StartY=14.25 StartZ=0 EndX=-1.5 EndY=14.25 EndZ=0
    g44: LineSegment StartX=-49.19 StartY=11.5 StartZ=0 EndX=-1.5 EndY=11.5 EndZ=0
    g45: LineSegment StartX=-49.19 StartY=8.5 StartZ=0 EndX=-1.5 EndY=8.5 EndZ=0
    g46: LineSegment StartX=-49.19 StartY=5.75 StartZ=0 EndX=-1.5 EndY=5.75 EndZ=0
    g47: LineSegment StartX=-49.19 StartY=2.75 StartZ=0 EndX=-1.5 EndY=2.75 EndZ=0
  constraints (120):
    c: Vertical(g0)
    c: Distance(g0) = 3
    c: Block(g0)
    c: Vertical(g1)
    c: Distance(g1) = 3
    c: Vertical(g2)
    c: Equal(g0,g2) = 3
    c: Block(g2)
    c: Vertical(g3)
    c: Equal(g1,g3) = 3
    c: Vertical(g4)
    c: Equal(g0,g4) = 3
    c: Block(g4)
    c: Vertical(g5)
    c: Equal(g1,g5) = 3
    c: Vertical(g6)
    c: Equal(g0,g6) = 3
    c: Block(g6)
    c: Vertical(g7)
    c: Equal(g1,g7) = 3
    c: Vertical(g8)
    c: Equal(g0,g8) = 3
    c: Block(g8)
    c: Vertical(g9)
    c: Equal(g1,g9) = 3
    c: Vertical(g10)
    c: Equal(g0,g10) = 3
    c: Block(g10)
    c: Vertical(g11)
    c: Equal(g1,g11) = 3
    c: Block(g12)
    c: Block(g13)
    c: Block(g14)
    c: Block(g15)
    c: Block(g16)
    c: Block(g17)
    c: Block(g18)
    c: Block(g19)
    c: Block(g20)
    c: Block(g21)
    c: Block(g22)
    c: Block(g23)
    c: Block(g11)
    c: Block(g9)
    c: Block(g7)
    c: Block(g5)
    c: Block(g3)
    c: Block(g1)
    c: Coincident(g24,g0)
    c: Coincident(g24,g12)
    c: Horizontal(g24)
    c: Coincident(g25,g0)
    c: Coincident(g25,g12)
    c: Horizontal(g25)
    c: Coincident(g26,g1)
    c: Coincident(g26,g13)
    c: Horizontal(g26)
    c: Coincident(g27,g1)
    c: Coincident(g27,g13)
    c: Horizontal(g27)
    c: Coincident(g28,g2)
    c: Coincident(g28,g14)
    c: Horizontal(g28)
    c: Coincident(g29,g2)
    c: Coincident(g29,g14)
    c: Horizontal(g29)
    c: Coincident(g30,g3)
    c: Coincident(g30,g15)
    c: Horizontal(g30)
    c: Coincident(g31,g3)
    c: Coincident(g31,g15)
    c: Horizontal(g31)
    c: Coincident(g32,g4)
    c: Coincident(g32,g16)
    c: Horizontal(g32)
    c: Coincident(g33,g4)
    c: Coincident(g33,g16)
    c: Horizontal(g33)
    c: Coincident(g34,g5)
    c: Coincident(g34,g17)
    c: Horizontal(g34)
    c: Coincident(g35,g5)
    c: Coincident(g35,g17)
    c: Horizontal(g35)
    c: Coincident(g36,g6)
    c: Coincident(g36,g19)
    c: Horizontal(g36)
    c: Coincident(g37,g6)
    c: Coincident(g37,g19)
    c: Horizontal(g37)
    c: Coincident(g38,g7)
    c: Coincident(g38,g18)
    c: Horizontal(g38)
    c: Coincident(g39,g7)
    c: Coincident(g39,g18)
    c: Horizontal(g39)
    c: Coincident(g40,g8)
    c: Coincident(g40,g20)
    c: Horizontal(g40)
    c: Coincident(g41,g8)
    c: Coincident(g41,g20)
    c: Horizontal(g41)
    c: Coincident(g42,g9)
    c: Coincident(g42,g23)
    c: Horizontal(g42)
    c: Coincident(g43,g9)
    c: Coincident(g43,g23)
    c: Horizontal(g43)
    c: Coincident(g44,g10)
    c: Coincident(g44,g22)
    c: Horizontal(g44)
    c: Coincident(g45,g10)
    c: Coincident(g45,g22)
    c: Horizontal(g45)
    c: Coincident(g46,g11)
    c: Coincident(g46,g21)
    c: Horizontal(g46)
    c: Coincident(g47,g11)
    c: Coincident(g47,g21)
    c: Horizontal(g47)
FEATURE [Part::Extrusion] Extrude065
  Base = -> Sketch074
  Dir = (1,0,0)
  DirMode = 2
  FaceMakerClass = Part::FaceMakerBullseye
  LengthFwd = 23
  LengthRev = 0
  Placement = pos=(-19,0,0) rot=(0,0,1;0rad)
  Solid = true
  Symmetric = false
FEATURE [Part::Fillet] Fillet056  label="removeToCreateVentalationHoles003"
  Base = -> Extrude065
  Edges = <same value as first occurrence — deduplicated (x6 in doc)>
  Placement = pos=(7,0.02,0) rot=(0,0,1;0rad)
FEATURE [Part::Revolution] Revolve158  label="removeToCreateScrewAndThreadedInsertHole065"
  Angle = 360
  Axis = (0,1,0)
  Base = (0,0,0)
  FaceMakerClass = Part::FaceMakerBullseye
  Placement = pos=(12.5,0,62) rot=(0,0,1;0rad)
  Solid = false
  Source = -> Face146
  Symmetric = false
FEATURE [Part::Revolution] Revolve159  label="removeToCreateScrewAndThreadedInsertHole066"
  Angle = 360
  Axis = (0,1,0)
  Base = (0,0,0)
  FaceMakerClass = Part::FaceMakerBullseye
  Placement = pos=(89.5,0,68.5) rot=(0,0,1;0rad)
  Solid = false
  Source = -> Face143
  Symmetric = false
FEATURE [Part::Revolution] Revolve160  label="removeToCreateScrewAndThreadedInsertHole067"
  Angle = 360
  Axis = (0,1,0)
  Base = (0,0,0)
  FaceMakerClass = Part::FaceMakerBullseye
  Placement = pos=(89.5,0,3.5) rot=(0,0,1;0rad)
  Solid = false
  Source = -> Face142
  Symmetric = false
FEATURE [Part::Revolution] Revolve161  label="removeToCreateScrewAndThreadedInsertHole068"
  Angle = 360
  Axis = (0,1,0)
  Base = (0,0,0)
  FaceMakerClass = Part::FaceMakerBullseye
  Placement = pos=(109.5,4.7,3.5) rot=(0,0,1;0rad)
  Solid = false
  Source = -> Face145
  Symmetric = false
FEATURE [Part::Revolution] Revolve162  label="removeToCreateScrewAndThreadedInsertHole069"
  Angle = 360
  Axis = (0,1,0)
  Base = (0,0,0)
  FaceMakerClass = Part::FaceMakerBullseye
  Placement = pos=(109.5,4.7,68.5) rot=(0,0,1;0rad)
  Solid = false
  Source = -> Face144
  Symmetric = false
FEATURE [Part::MultiFuse] Fusion141  label="removeToCreateScrewAndThreadedInsertHole064"
  Shapes = -> [Revolve162,Revolve161,Revolve160,Revolve159,Revolve158,Revolve157]
FEATURE [Part::Cylinder] Cylinder062
  Angle = 360
  AttacherType = Attacher::AttachEngine3D
  Height = 20
  Placement = pos=(0,0,36.15) rot=(0,0,1;0rad)
  Radius = 14
FEATURE [Part::Cylinder] Cylinder063
  Angle = 360
  AttacherType = Attacher::AttachEngine3D
  Height = 10
  Placement = pos=(0,0,36.15) rot=(0,0,1;0rad)
  Radius = 4
FEATURE [Part::MultiFuse] Fusion139  label="removeToCreteHoleForPlugHousing052"
  Placement = pos=(70,19,36) rot=(0,1,0;1.5708rad)
  Shapes = -> [Cylinder062,Cylinder063]
FEATURE [Part::Cut] Cut060  label="bottom017"
  Base = -> Extrude064
  Tool = -> Fusion139
FEATURE [Part::Cut] Cut061  label="bottom019"
  Base = -> Cut060
  Tool = -> Fusion141
FEATURE [Part::MultiFuse] Fusion140  label="bottom018"
  Shapes = -> [Cut061,Cut058]
FEATURE [Part::Cut] Cut059  label="bottom020"
  Base = -> Fusion140
  Tool = -> Fillet056
FEATURE [Part::Box] Box036  label="Cube021"
  AttacherType = Attacher::AttachEngine3D
  Height = 80
  Length = 26
  Placement = pos=(0,-1,-5) rot=(0,0,1;0rad)
  Width = 11
FEATURE [Part::Cut] Cut062  label="removeFromBottom002"
  Base = -> Cut057
  Tool = -> Box036
FEATURE [Part::Cut] Cut063
  Base = -> Cut059
  Tool = -> Cut062
FEATURE [Part::Cut] Cut064  label="pcbStands"
  Base = -> Fusion095
  Tool = -> Fusion127
FEATURE [Sketcher::SketchObject] Sketch075  label="topSketch022"
  FullyConstrained = true
  sketch-geometry (6):
    g0: LineSegment StartX=19 StartY=38 StartZ=0 EndX=117 EndY=38 EndZ=0
    g1: ArcOfCircle CenterX=19 CenterY=19 CenterZ=0 NormalX=0 NormalY=0 NormalZ=1 AngleXU=0 Radius=19 StartAngle=1.5708 EndAngle=3.14159
    g2: LineSegment StartX=117 StartY=38 StartZ=0 EndX=117 EndY=19 EndZ=0
    g3: LineSegment StartX=98 StartY=1.0161e-12 StartZ=0 EndX=5.22862e-06 EndY=1.0161e-12 EndZ=0
    g4: LineSegment StartX=5.22862e-06 StartY=19 StartZ=0 EndX=5.22862e-06 EndY=1.0161e-12 EndZ=0
    g5: ArcOfCircle CenterX=98 CenterY=19 CenterZ=0 NormalX=0 NormalY=0 NormalZ=1 AngleXU=0 Radius=19 StartAngle=4.71239 EndAngle=6.28319
  constraints (16):
    c: Horizontal(g0)
    c: Distance(g0) = 98
    c: Coincident(g1,g0)
    c: Block(g1)
    c: Coincident(g2,g0)
    c: Vertical(g2)
    c: Distance(g2) = 19
    c: Horizontal(g3)
    c: Coincident(g4,g1)
    c: Vertical(g4)
    c: Coincident(g3,g4)
    c: Block(g3)
    c: Coincident(g5,g2)
    c: Coincident(g5,g3)
    c: Block(g0)
    c: Block(g5)
FEATURE [Part::Extrusion] Extrude067  label="sideB003"
  Base = -> Sketch075
  Dir = (0,0,1)
  DirMode = 2
  FaceMakerClass = Part::FaceMakerBullseye
  LengthFwd = 3
  LengthRev = 0
  Placement = pos=(0,0,71.7) rot=(0,0,1;0rad)
  Solid = true
  Symmetric = false
FEATURE [Sketcher::SketchObject] Sketch076  label="topSketch023"
  FullyConstrained = true
  sketch-geometry (6):
    g0: LineSegment StartX=19 StartY=38 StartZ=0 EndX=117 EndY=38 EndZ=0
    g1: ArcOfCircle CenterX=19 CenterY=19 CenterZ=0 NormalX=0 NormalY=0 NormalZ=1 AngleXU=0 Radius=19 StartAngle=1.5708 EndAngle=3.14159
    g2: LineSegment StartX=117 StartY=38 StartZ=0 EndX=117 EndY=19 EndZ=0
    g3: LineSegment StartX=98 StartY=1.0161e-12 StartZ=0 EndX=5.22862e-06 EndY=1.0161e-12 EndZ=0
    g4: LineSegment StartX=5.22862e-06 StartY=19 StartZ=0 EndX=5.22862e-06 EndY=1.0161e-12 EndZ=0
    g5: ArcOfCircle CenterX=98 CenterY=19 CenterZ=0 NormalX=0 NormalY=0 NormalZ=1 AngleXU=0 Radius=19 StartAngle=4.71239 EndAngle=6.28319
  constraints (16):
    c: Horizontal(g0)
    c: Distance(g0) = 98
    c: Coincident(g1,g0)
    c: Block(g1)
    c: Coincident(g2,g0)
    c: Vertical(g2)
    c: Distance(g2) = 19
    c: Horizontal(g3)
    c: Coincident(g4,g1)
    c: Vertical(g4)
    c: Coincident(g3,g4)
    c: Block(g3)
    c: Coincident(g5,g2)
    c: Coincident(g5,g3)
    c: Block(g0)
    c: Block(g5)
FEATURE [Part::Extrusion] Extrude066  label="sideA003"
  Base = -> Sketch076
  Dir = (0,0,1)
  DirMode = 2
  FaceMakerClass = Part::FaceMakerBullseye
  LengthFwd = 3
  LengthRev = 0
  Placement = pos=(0,0,-2.7) rot=(0,0,1;0rad)
  Solid = true
  Symmetric = false
FEATURE [Part::MultiFuse] Fusion142  label="removeFromBottom003"
  Placement = pos=(2,0,0) rot=(0,0,1;0rad)
  Shapes = -> [Extrude066,Extrude067]
FEATURE [Part::Cut] Cut065  label="screwRetainers002"
  Base = -> Fusion096
  Tool = -> Fusion142
FEATURE [Sketcher::SketchObject] Sketch077
  FullyConstrained = true
  Placement = pos=(117,19,0) rot=(0.57735,0.57735,0.57735;2.0944rad)
  sketch-geometry (8):
    g0: LineSegment StartX=-49.19 StartY=63.5 StartZ=0 EndX=-49.19 EndY=60.5 EndZ=0
    g1: LineSegment StartX=-49.19 StartY=11.5 StartZ=0 EndX=-49.19 EndY=8.5 EndZ=0
    g2: ArcOfCircle CenterX=-1.5 CenterY=62 CenterZ=0 NormalX=0 NormalY=0 NormalZ=1 AngleXU=0 Radius=1.5 StartAngle=4.71239 EndAngle=7.85398
    g3: ArcOfCircle CenterX=-1.5 CenterY=10 CenterZ=0 NormalX=0 NormalY=0 NormalZ=1 AngleXU=0 Radius=1.5 StartAngle=4.71239 EndAngle=7.85398
    g4: LineSegment StartX=-49.19 StartY=63.5 StartZ=0 EndX=-1.5 EndY=63.5 EndZ=0
    g5: LineSegment StartX=-49.19 StartY=60.5 StartZ=0 EndX=-1.5 EndY=60.5 EndZ=0
    g6: LineSegment StartX=-49.19 StartY=11.5 StartZ=0 EndX=-1.5 EndY=11.5 EndZ=0
    g7: LineSegment StartX=-49.19 StartY=8.5 StartZ=0 EndX=-1.5 EndY=8.5 EndZ=0
  constraints (19):
    c: Vertical(g0)
    c: Distance(g0) = 3
    c: Vertical(g1)
    c: Block(g1)
    c: Block(g2)
    c: Block(g3)
    c: Block(g0)
    c: Coincident(g4,g0)
    c: Coincident(g4,g2)
    c: Horizontal(g4)
    c: Coincident(g5,g0)
    c: Coincident(g5,g2)
    c: Horizontal(g5)
    c: Coincident(g6,g1)
    c: Coincident(g6,g3)
    c: Horizontal(g6)
    c: Coincident(g7,g1)
    c: Coincident(g7,g3)
    c: Horizontal(g7)
FEATURE [Part::Extrusion] Extrude068
  Base = -> Sketch077
  Dir = (1,0,0)
  DirMode = 2
  FaceMakerClass = Part::FaceMakerBullseye
  LengthFwd = 10
  LengthRev = 0
  Solid = true
  Symmetric = false
FEATURE [Part::Fillet] Fillet057  label="removeFromtMoreFrontCaseScrewRetainers002"
  Base = -> Extrude068
  Edges = 4 edges r=1.49: [Edge6,Edge11,Edge18,Edge23]
  Placement = pos=(-12,0,0) rot=(0,0,1;0rad)
FEATURE [Sketcher::SketchObject] Sketch078
  FullyConstrained = true
  Placement = pos=(117,19,0) rot=(0.57735,0.57735,0.57735;2.0944rad)
  sketch-geometry (8):
    g0: LineSegment StartX=-49.19 StartY=69.25 StartZ=0 EndX=-49.19 EndY=66.25 EndZ=0
    g1: LineSegment StartX=-49.19 StartY=5.75 StartZ=0 EndX=-49.19 EndY=2.75 EndZ=0
    g2: ArcOfCircle CenterX=-1.5 CenterY=67.75 CenterZ=0 NormalX=0 NormalY=0 NormalZ=1 AngleXU=0 Radius=1.5 StartAngle=4.71239 EndAngle=7.85398
    g3: ArcOfCircle CenterX=-1.5 CenterY=4.25 CenterZ=0 NormalX=0 NormalY=0 NormalZ=1 AngleXU=0 Radius=1.5 StartAngle=4.71239 EndAngle=7.85398
    g4: LineSegment StartX=-49.19 StartY=69.25 StartZ=0 EndX=-1.5 EndY=69.25 EndZ=0
    g5: LineSegment StartX=-49.19 StartY=66.25 StartZ=0 EndX=-1.5 EndY=66.25 EndZ=0
    g6: LineSegment StartX=-49.19 StartY=5.75 StartZ=0 EndX=-1.5 EndY=5.75 EndZ=0
    g7: LineSegment StartX=-49.19 StartY=2.75 StartZ=0 EndX=-1.5 EndY=2.75 EndZ=0
  constraints (19):
    c: Vertical(g0)
    c: Distance(g0) = 3
    c: Block(g0)
    c: Vertical(g1)
    c: Block(g2)
    c: Block(g3)
    c: Block(g1)
    c: Coincident(g4,g0)
    c: Coincident(g4,g2)
    c: Horizontal(g4)
    c: Coincident(g5,g0)
    c: Coincident(g5,g2)
    c: Horizontal(g5)
    c: Coincident(g6,g1)
    c: Coincident(g6,g3)
    c: Horizontal(g6)
    c: Coincident(g7,g1)
    c: Coincident(g7,g3)
    c: Horizontal(g7)
FEATURE [Part::Extrusion] Extrude069
  Base = -> Sketch078
  Dir = (1,0,0)
  DirMode = 2
  FaceMakerClass = Part::FaceMakerBullseye
  LengthFwd = 10
  LengthRev = 0
  Solid = true
  Symmetric = false
FEATURE [Part::Fillet] Fillet058  label="removeFromtMoreFrontCaseScrewRetainers003"
  Base = -> Extrude069
  Edges = 4 edges r=1.49: [Edge6,Edge11,Edge18,Edge23]
  Placement = pos=(-4,0,0) rot=(0,0,1;0rad)
FEATURE [Part::Cut] Cut066
  Base = -> Cut065
  Tool = -> Fillet058
FEATURE [Part::Cut] Cut067  label="screwPillars"
  Base = -> Cut066
  Tool = -> Fillet057
FEATURE [Part::MultiFuse] Fusion143  label="bottom021"
  Shapes = -> [Cut031,Cut063]
FEATURE [Part::Cylinder] Cylinder
  Angle = 360
  AttacherType = Attacher::AttachEngine3D
  Height = 10
  Placement = pos=(20.65,12,4.68) rot=(1,0,0;1.5708rad)
  Radius = 2
FEATURE [Part::Cylinder] Cylinder064
  Angle = 360
  AttacherType = Attacher::AttachEngine3D
  Height = 10
  Placement = pos=(20.65,12,67.38) rot=(1,0,0;1.5708rad)
  Radius = 2
FEATURE [Part::Cylinder] Cylinder065
  Angle = 360
  AttacherType = Attacher::AttachEngine3D
  Height = 10
  Placement = pos=(77.15,12,67.38) rot=(1,0,0;1.5708rad)
  Radius = 2
FEATURE [Part::Cylinder] Cylinder066
  Angle = 360
  AttacherType = Attacher::AttachEngine3D
  Height = 10
  Placement = pos=(77.15,12,4.68) rot=(1,0,0;1.5708rad)
  Radius = 2
FEATURE [Part::MultiFuse] Fusion144  label="removeFromThreadedInsertHousing"
  Shapes = -> [Cylinder065,Cylinder064,Cylinder,Cylinder066]
FEATURE [Part::Cut] Cut068  label="pcbStands001"
  Base = -> Cut064
  Tool = -> Fusion144
FEATURE [Part::MultiFuse] Fusion145
  Shapes = -> [Cut068,Fusion143]
FEATURE [Part::MultiFuse] Fusion146
  Shapes = -> [Fusion145]
FEATURE [Part::MultiFuse] Fusion147  label="bottom022"
  Shapes = -> [Cut067,Fusion146]
FEATURE [Part::MultiFuse] Fusion148  label="casePillars005"
  Shapes = -> [Cut047,Fusion092]
FEATURE [Part::MultiFuse] Fusion149  label="bottom023"
  Shapes = -> [Fusion124,Fusion113,Fusion147]
FEATURE [Part::MultiFuse] Fusion150  label="topBits"
  Shapes = -> [Cut025,Fusion148,Cut030,Fillet034]
FEATURE [Part::Feature] Face149 .. Face152  x4 (patterned run collapsed; names and placements below)
  shape: bbox 3.2 x 1.5 x 2e-07 mm, 1 faces, 0 solids (baked)
FEATURE [Part::Feature] Face153
  shape: bbox 3.6 x 3.2 x 2e-07 mm, 1 faces, 0 solids (baked)
FEATURE [Part::Feature] Face154
  shape: bbox 3.6 x 3.2 x 2e-07 mm, 1 faces, 0 solids (baked)
FEATURE [Sketcher::SketchObject] Sketch079  label="topSketch024"
  FullyConstrained = true
  sketch-geometry (6):
    g0: LineSegment StartX=19 StartY=38 StartZ=0 EndX=117 EndY=38 EndZ=0
    g1: ArcOfCircle CenterX=19 CenterY=19 CenterZ=0 NormalX=0 NormalY=0 NormalZ=1 AngleXU=0 Radius=19 StartAngle=1.5708 EndAngle=3.14159
    g2: LineSegment StartX=117 StartY=38 StartZ=0 EndX=117 EndY=19 EndZ=0
    g3: LineSegment StartX=98 StartY=1.0161e-12 StartZ=0 EndX=5.22862e-06 EndY=1.0161e-12 EndZ=0
    g4: LineSegment StartX=5.22862e-06 StartY=19 StartZ=0 EndX=5.22862e-06 EndY=1.0161e-12 EndZ=0
    g5: ArcOfCircle CenterX=98 CenterY=19 CenterZ=0 NormalX=0 NormalY=0 NormalZ=1 AngleXU=0 Radius=19 StartAngle=4.71239 EndAngle=6.28319
  constraints (16):
    c: Horizontal(g0)
    c: Distance(g0) = 98
    c: Coincident(g1,g0)
    c: Block(g1)
    c: Coincident(g2,g0)
    c: Vertical(g2)
    c: Distance(g2) = 19
    c: Horizontal(g3)
    c: Coincident(g4,g1)
    c: Vertical(g4)
    c: Coincident(g3,g4)
    c: Block(g3)
    c: Coincident(g5,g2)
    c: Coincident(g5,g3)
    c: Block(g0)
    c: Block(g5)
FEATURE [Sketcher::SketchObject] Sketch080  label="topSketch025"
  FullyConstrained = true
  sketch-geometry (6):
    g0: LineSegment StartX=19 StartY=38 StartZ=0 EndX=117 EndY=38 EndZ=0
    g1: ArcOfCircle CenterX=19 CenterY=19 CenterZ=0 NormalX=0 NormalY=0 NormalZ=1 AngleXU=0 Radius=19 StartAngle=1.5708 EndAngle=3.14159
    g2: LineSegment StartX=117 StartY=38 StartZ=0 EndX=117 EndY=19 EndZ=0
    g3: LineSegment StartX=98 StartY=1.0161e-12 StartZ=0 EndX=5.22862e-06 EndY=1.0161e-12 EndZ=0
    g4: LineSegment StartX=5.22862e-06 StartY=19 StartZ=0 EndX=5.22862e-06 EndY=1.0161e-12 EndZ=0
    g5: ArcOfCircle CenterX=98 CenterY=19 CenterZ=0 NormalX=0 NormalY=0 NormalZ=1 AngleXU=0 Radius=19 StartAngle=4.71239 EndAngle=6.28319
  constraints (16):
    c: Horizontal(g0)
    c: Distance(g0) = 98
    c: Coincident(g1,g0)
    c: Block(g1)
    c: Coincident(g2,g0)
    c: Vertical(g2)
    c: Distance(g2) = 19
    c: Horizontal(g3)
    c: Coincident(g4,g1)
    c: Vertical(g4)
    c: Coincident(g3,g4)
    c: Block(g3)
    c: Coincident(g5,g2)
    c: Coincident(g5,g3)
    c: Block(g0)
    c: Block(g5)
FEATURE [Part::Extrusion] Extrude070  label="sideA004"
  Base = -> Sketch080
  Dir = (0,0,1)
  DirMode = 2
  FaceMakerClass = Part::FaceMakerBullseye
  LengthFwd = 3
  LengthRev = 0
  Placement = pos=(0,0,-2.7) rot=(0,0,1;0rad)
  Solid = true
  Symmetric = false
FEATURE [Sketcher::SketchObject] Sketch081
  FullyConstrained = true
  Placement = pos=(117,19,0) rot=(0.57735,0.57735,0.57735;2.0944rad)
  sketch-geometry (8):
    g0: LineSegment StartX=-49.19 StartY=63.5 StartZ=0 EndX=-49.19 EndY=60.5 EndZ=0
    g1: LineSegment StartX=-49.19 StartY=11.5 StartZ=0 EndX=-49.19 EndY=8.5 EndZ=0
    g2: ArcOfCircle CenterX=-1.5 CenterY=62 CenterZ=0 NormalX=0 NormalY=0 NormalZ=1 AngleXU=0 Radius=1.5 StartAngle=4.71239 EndAngle=7.85398
    g3: ArcOfCircle CenterX=-1.5 CenterY=10 CenterZ=0 NormalX=0 NormalY=0 NormalZ=1 AngleXU=0 Radius=1.5 StartAngle=4.71239 EndAngle=7.85398
    g4: LineSegment StartX=-49.19 StartY=63.5 StartZ=0 EndX=-1.5 EndY=63.5 EndZ=0
    g5: LineSegment StartX=-49.19 StartY=60.5 StartZ=0 EndX=-1.5 EndY=60.5 EndZ=0
    g6: LineSegment StartX=-49.19 StartY=11.5 StartZ=0 EndX=-1.5 EndY=11.5 EndZ=0
    g7: LineSegment StartX=-49.19 StartY=8.5 StartZ=0 EndX=-1.5 EndY=8.5 EndZ=0
  constraints (19):
    c: Vertical(g0)
    c: Distance(g0) = 3
    c: Vertical(g1)
    c: Block(g1)
    c: Block(g2)
    c: Block(g3)
    c: Block(g0)
    c: Coincident(g4,g0)
    c: Coincident(g4,g2)
    c: Horizontal(g4)
    c: Coincident(g5,g0)
    c: Coincident(g5,g2)
    c: Horizontal(g5)
    c: Coincident(g6,g1)
    c: Coincident(g6,g3)
    c: Horizontal(g6)
    c: Coincident(g7,g1)
    c: Coincident(g7,g3)
    c: Horizontal(g7)
FEATURE [Part::Extrusion] Extrude071  label="sideB004"
  Base = -> Sketch079
  Dir = (0,0,1)
  DirMode = 2
  FaceMakerClass = Part::FaceMakerBullseye
  LengthFwd = 3
  LengthRev = 0
  Placement = pos=(0,0,71.7) rot=(0,0,1;0rad)
  Solid = true
  Symmetric = false
FEATURE [Part::MultiFuse] Fusion152  label="removeFromBottom004"
  Placement = pos=(2,0,0) rot=(0,0,1;0rad)
  Shapes = -> [Extrude070,Extrude071]
FEATURE [Part::Extrusion] Extrude072
  Base = -> Sketch081
  Dir = (1,0,0)
  DirMode = 2
  FaceMakerClass = Part::FaceMakerBullseye
  LengthFwd = 10
  LengthRev = 0
  Solid = true
  Symmetric = false
FEATURE [Part::Fillet] Fillet059  label="removeFromtMoreFrontCaseScrewRetainers004"
  Base = -> Extrude072
  Edges = 4 edges r=1.49: [Edge6,Edge11,Edge18,Edge23]
  Placement = pos=(-12,0,0) rot=(0,0,1;0rad)
FEATURE [Sketcher::SketchObject] Sketch082
  FullyConstrained = true
  Placement = pos=(117,19,0) rot=(0.57735,0.57735,0.57735;2.0944rad)
  sketch-geometry (8):
    g0: LineSegment StartX=-49.19 StartY=69.25 StartZ=0 EndX=-49.19 EndY=66.25 EndZ=0
    g1: LineSegment StartX=-49.19 StartY=5.75 StartZ=0 EndX=-49.19 EndY=2.75 EndZ=0
    g2: ArcOfCircle CenterX=-1.5 CenterY=67.75 CenterZ=0 NormalX=0 NormalY=0 NormalZ=1 AngleXU=0 Radius=1.5 StartAngle=4.71239 EndAngle=7.85398
    g3: ArcOfCircle CenterX=-1.5 CenterY=4.25 CenterZ=0 NormalX=0 NormalY=0 NormalZ=1 AngleXU=0 Radius=1.5 StartAngle=4.71239 EndAngle=7.85398
    g4: LineSegment StartX=-49.19 StartY=69.25 StartZ=0 EndX=-1.5 EndY=69.25 EndZ=0
    g5: LineSegment StartX=-49.19 StartY=66.25 StartZ=0 EndX=-1.5 EndY=66.25 EndZ=0
    g6: LineSegment StartX=-49.19 StartY=5.75 StartZ=0 EndX=-1.5 EndY=5.75 EndZ=0
    g7: LineSegment StartX=-49.19 StartY=2.75 StartZ=0 EndX=-1.5 EndY=2.75 EndZ=0
  constraints (19):
    c: Vertical(g0)
    c: Distance(g0) = 3
    c: Block(g0)
    c: Vertical(g1)
    c: Block(g2)
    c: Block(g3)
    c: Block(g1)
    c: Coincident(g4,g0)
    c: Coincident(g4,g2)
    c: Horizontal(g4)
    c: Coincident(g5,g0)
    c: Coincident(g5,g2)
    c: Horizontal(g5)
    c: Coincident(g6,g1)
    c: Coincident(g6,g3)
    c: Horizontal(g6)
    c: Coincident(g7,g1)
    c: Coincident(g7,g3)
    c: Horizontal(g7)
FEATURE [Part::Extrusion] Extrude073
  Base = -> Sketch082
  Dir = (1,0,0)
  DirMode = 2
  FaceMakerClass = Part::FaceMakerBullseye
  LengthFwd = 10
  LengthRev = 0
  Solid = true
  Symmetric = false
FEATURE [Part::Fillet] Fillet060  label="removeFromtMoreFrontCaseScrewRetainers005"
  Base = -> Extrude073
  Edges = 4 edges r=1.49: [Edge6,Edge11,Edge18,Edge23]
  Placement = pos=(-4,0,0) rot=(0,0,1;0rad)
FEATURE [Part::Revolution] Revolve163  label="backCaseScrewRetainer004"
  Angle = 360
  Axis = (0,1,0)
  Base = (0,0,0)
  FaceMakerClass = Part::FaceMakerBullseye
  Placement = pos=(12.5,3,62) rot=(0,0,1;0rad)
  Solid = false
  Source = -> Face149
  Symmetric = false
FEATURE [Part::Revolution] Revolve164  label="frontCaseScrewRetainer006"
  Angle = 360
  Axis = (0,1,0)
  Base = (0,0,0)
  FaceMakerClass = Part::FaceMakerBullseye
  Placement = pos=(89.5,3,68.5) rot=(0,0,1;0rad)
  Solid = false
  Source = -> Face151
  Symmetric = false
FEATURE [Part::Revolution] Revolve165  label="frontCaseScrewRetainer007"
  Angle = 360
  Axis = (0,1,0)
  Base = (0,0,0)
  FaceMakerClass = Part::FaceMakerBullseye
  Placement = pos=(89.5,3,3.5) rot=(0,0,1;0rad)
  Solid = false
  Source = -> Face152
  Symmetric = false
FEATURE [Part::Revolution] Revolve166  label="backCaseScrewRetainer005"
  Angle = 360
  Axis = (0,1,0)
  Base = (0,0,0)
  FaceMakerClass = Part::FaceMakerBullseye
  Placement = pos=(12.5,3,10) rot=(0,0,1;0rad)
  Solid = false
  Source = -> Face150
  Symmetric = false
FEATURE [Part::Revolution] Revolve167  label="moreFrontCaseScrewRetainer006"
  Angle = 360
  Axis = (0,1,0)
  Base = (0,0,0)
  FaceMakerClass = Part::FaceMakerBullseye
  Placement = pos=(109.5,4.5,68.5) rot=(0,0,1;0rad)
  Solid = false
  Source = -> Face153
  Symmetric = false
FEATURE [Part::Revolution] Revolve168  label="moreFrontCaseScrewRetainer007"
  Angle = 360
  Axis = (0,1,0)
  Base = (0,0,0)
  FaceMakerClass = Part::FaceMakerBullseye
  Placement = pos=(109.5,4.5,3.5) rot=(0,0,1;0rad)
  Solid = false
  Source = -> Face154
  Symmetric = false
FEATURE [Part::MultiFuse] Fusion151  label="screwRetainers003"
  Shapes = -> [Revolve168,Revolve167,Revolve166,Revolve165,Revolve164,Revolve163]
FEATURE [Part::Cut] Cut069  label="screwRetainers004"
  Base = -> Fusion151
  Tool = -> Fusion152
FEATURE [Part::Cut] Cut070
  Base = -> Cut069
  Tool = -> Fillet060
FEATURE [Part::Cut] Cut071  label="screwPillars001"
  Base = -> Cut070
  Tool = -> Fillet059
FEATURE [Part::MultiFuse] Fusion153  label="bottom024"
  Shapes = -> [Fusion149,Cut071]
FEATURE [Part::Cylinder] Cylinder067
  Angle = 360
  AttacherType = Attacher::AttachEngine3D
  Height = 10
  Placement = pos=(20.65,12,4.68) rot=(1,0,0;1.5708rad)
  Radius = 2
FEATURE [Part::Cylinder] Cylinder068
  Angle = 360
  AttacherType = Attacher::AttachEngine3D
  Height = 10
  Placement = pos=(20.65,12,67.38) rot=(1,0,0;1.5708rad)
  Radius = 2
FEATURE [Part::Cylinder] Cylinder069
  Angle = 360
  AttacherType = Attacher::AttachEngine3D
  Height = 10
  Placement = pos=(77.15,12,67.38) rot=(1,0,0;1.5708rad)
  Radius = 2
FEATURE [Part::Cylinder] Cylinder070
  Angle = 360
  AttacherType = Attacher::AttachEngine3D
  Height = 10
  Placement = pos=(77.15,12,4.68) rot=(1,0,0;1.5708rad)
  Radius = 2
FEATURE [Part::MultiFuse] Fusion154  label="removeFromThreadedInsertHousing001"
  Shapes = -> [Cylinder069,Cylinder068,Cylinder067,Cylinder070]
FEATURE [Part::Cut] Cut072  label="bottom025"
  Base = -> Fusion153
  Tool = -> Fusion154
FEATURE [Image::ImagePlane] ImagePlane
  XSize = 339
  YSize = 72
FEATURE [Sketcher::SketchObject] Sketch083
  FullyConstrained = true
  MapMode = 5
  Support = -> [XY_Plane]
  sketch-geometry (194):
    g0: LineSegment StartX=-151.619 StartY=28.8932 StartZ=0 EndX=-140.819 EndY=28.8932 EndZ=0
    g1: LineSegment StartX=-151.619 StartY=24.0313 StartZ=0 EndX=-151.619 EndY=28.8932 EndZ=0
    g2: LineSegment StartX=-140.819 StartY=17.7713 StartZ=0 EndX=-151.619 EndY=17.7713 EndZ=0
    g3: LineSegment StartX=-151.619 StartY=17.7713 StartZ=0 EndX=-151.619 EndY=22.6313 EndZ=0
    g4: LineSegment StartX=-151.619 StartY=22.6313 StartZ=0 EndX=-145.128 EndY=22.6313 EndZ=0
    g5: LineSegment StartX=-145.128 StartY=24.0313 StartZ=0 EndX=-140.819 EndY=28.8932 EndZ=0
    g6: LineSegment StartX=-145.128 StartY=22.6313 StartZ=0 EndX=-140.819 EndY=17.7713 EndZ=0
    g7: ArcOfCircle CenterX=-155.157 CenterY=23.3323 CenterZ=0 NormalX=0 NormalY=0 NormalZ=1 AngleXU=0 Radius=6.92354 StartAngle=1.03434 EndAngle=5.24885
    g8: ArcOfCircle CenterX=-155.157 CenterY=23.3323 CenterZ=0 NormalX=0 NormalY=0 NormalZ=1 AngleXU=0 Radius=12.6269 StartAngle=1.28675 EndAngle=4.99643
    g9: LineSegment StartX=-151.619 StartY=35.4532 StartZ=0 EndX=-151.619 EndY=29.2832 EndZ=0
    g10: LineSegment StartX=-151.619 StartY=17.3813 StartZ=0 EndX=-151.619 EndY=11.2113 EndZ=0
    g11-g21: Circle x11 (B-spline internal-alignment scaffolding for g22; pole/knot coordinates omitted)
    g22: BSplineCurve PolesCount=11 KnotsCount=9 Degree=3 IsPeriodic=0
    g23-g31: GeomPoint x9 (B-spline internal-alignment scaffolding for g22; pole/knot coordinates omitted)
    g32-g49: Circle x18 (B-spline internal-alignment scaffolding for g50; pole/knot coordinates omitted)
    g50: BSplineCurve PolesCount=18 KnotsCount=16 Degree=3 IsPeriodic=0
    g51-g66: GeomPoint x16 (B-spline internal-alignment scaffolding for g50; pole/knot coordinates omitted)
    g67: LineSegment StartX=-117.124 StartY=30.093 StartZ=0 EndX=-117.603 EndY=26.5272 EndZ=0
    g68: LineSegment StartX=-117.603 StartY=17.8472 StartZ=0 EndX=-117.124 EndY=14.2659 EndZ=0
    g69: Ellipse CenterX=-109.671 CenterY=20.025 CenterZ=0 NormalX=0 NormalY=0 NormalZ=1 MajorRadius=3.34798 MinorRadius=2.71052 AngleXU=-1.56793
    g70: GeomPoint X=-109.666 Y=18.0598 Z=0
    g71: GeomPoint X=-109.677 Y=21.9902 Z=0
    g72: Ellipse CenterX=-109.671 CenterY=20.0123 CenterZ=0 NormalX=0 NormalY=0 NormalZ=1 MajorRadius=6.93002 MinorRadius=6.36273 AngleXU=-3.13976
    g73: GeomPoint X=-112.417 Y=20.0073 Z=0
    g74: GeomPoint X=-106.925 Y=20.0173 Z=0
    g75: Ellipse CenterX=-51.7682 CenterY=20.1463 CenterZ=0 NormalX=0 NormalY=0 NormalZ=1 MajorRadius=3.19279 MinorRadius=2.71052 AngleXU=-1.52774
    g76: GeomPoint X=-51.6955 Y=18.4606 Z=0
    g77: GeomPoint X=-51.8408 Y=21.832 Z=0
    g78: GeomPoint X=-54.5142 Y=20.1413 Z=0
    g79: GeomPoint X=-49.0221 Y=20.1513 Z=0
    g80: Ellipse CenterX=-51.7682 CenterY=20.1463 CenterZ=0 NormalX=0 NormalY=0 NormalZ=1 MajorRadius=6.93002 MinorRadius=6.36273 AngleXU=-3.13976
    g81: Ellipse CenterX=-22.8436 CenterY=20.1783 CenterZ=0 NormalX=0 NormalY=0 NormalZ=1 MajorRadius=3.31512 MinorRadius=2.71052 AngleXU=-1.60214
    g82: GeomPoint X=-22.9034 Y=18.2706 Z=0
    g83: GeomPoint X=-22.7838 Y=22.0861 Z=0
    g84: GeomPoint X=-25.5897 Y=20.1733 Z=0
    g85: GeomPoint X=-20.0976 Y=20.1833 Z=0
    g86: Ellipse CenterX=-22.8436 CenterY=20.1783 CenterZ=0 NormalX=0 NormalY=0 NormalZ=1 MajorRadius=6.93002 MinorRadius=6.36273 AngleXU=-3.13976
    g87: LineSegment StartX=-101.889 StartY=14.1107 StartZ=0 EndX=-97.7455 EndY=14.1107 EndZ=0
    g88: LineSegment StartX=-93.8155 StartY=14.1107 StartZ=0 EndX=-89.6755 EndY=14.1107 EndZ=0
    g89: LineSegment StartX=-85.7455 StartY=14.1107 StartZ=0 EndX=-81.6055 EndY=14.1107 EndZ=0
    g90: LineSegment StartX=-101.889 StartY=14.1107 StartZ=0 EndX=-101.889 EndY=25.9907 EndZ=0
    g91: LineSegment StartX=-101.889 StartY=25.9907 StartZ=0 EndX=-97.8594 EndY=25.9907 EndZ=0
    g92: LineSegment StartX=-97.8594 StartY=25.9907 StartZ=0 EndX=-97.8594 EndY=24.0907 EndZ=0
    g93: LineSegment StartX=-97.7455 StartY=14.1107 StartZ=0 EndX=-97.7455 EndY=19.9107 EndZ=0
    g94: LineSegment StartX=-89.6755 StartY=14.1107 StartZ=0 EndX=-89.6755 EndY=19.9107 EndZ=0
    g95: LineSegment StartX=-93.8155 StartY=14.1107 StartZ=0 EndX=-93.8155 EndY=21.0107 EndZ=0
    g96-g106: Circle x11 (B-spline internal-alignment scaffolding for g107; pole/knot coordinates omitted)
    g107: BSplineCurve PolesCount=11 KnotsCount=9 Degree=3 IsPeriodic=0
    g108-g116: GeomPoint x9 (B-spline internal-alignment scaffolding for g107; pole/knot coordinates omitted)
    g117: BSplineCurve PolesCount=11 KnotsCount=9 Degree=3 IsPeriodic=0
    g118-g125: Circle x8 (B-spline internal-alignment scaffolding for g126; pole/knot coordinates omitted)
    g126: BSplineCurve PolesCount=8 KnotsCount=6 Degree=3 IsPeriodic=0
    g127-g132: GeomPoint x6 (B-spline internal-alignment scaffolding for g126; pole/knot coordinates omitted)
    g133: BSplineCurve PolesCount=8 KnotsCount=6 Degree=3 IsPeriodic=0
    g134: LineSegment StartX=-85.7455 StartY=21.0107 StartZ=0 EndX=-85.7455 EndY=14.1107 EndZ=0
    g135: LineSegment StartX=-80.0879 StartY=14.1107 StartZ=0 EndX=-75.944 EndY=14.1107 EndZ=0
    g136: LineSegment StartX=-72.014 StartY=14.1107 StartZ=0 EndX=-67.874 EndY=14.1107 EndZ=0
    g137: LineSegment StartX=-63.944 StartY=14.1107 StartZ=0 EndX=-59.804 EndY=14.1107 EndZ=0
    g138: LineSegment StartX=-80.0879 StartY=14.1107 StartZ=0 EndX=-80.0879 EndY=25.9907 EndZ=0
    g139: LineSegment StartX=-80.0879 StartY=25.9907 StartZ=0 EndX=-76.0579 EndY=25.9907 EndZ=0
    g140: LineSegment StartX=-76.0579 StartY=25.9907 StartZ=0 EndX=-76.0579 EndY=24.0907 EndZ=0
    g141: LineSegment StartX=-75.944 StartY=14.1107 StartZ=0 EndX=-75.944 EndY=19.9107 EndZ=0
    g142: LineSegment StartX=-67.874 StartY=14.1107 StartZ=0 EndX=-67.874 EndY=19.9107 EndZ=0
    g143: LineSegment StartX=-72.014 StartY=14.1107 StartZ=0 EndX=-72.014 EndY=21.0107 EndZ=0
    g144-g148: Circle x5 (B-spline internal-alignment scaffolding for g149; pole/knot coordinates omitted)
    g149: BSplineCurve PolesCount=11 KnotsCount=9 Degree=3 IsPeriodic=0
    g150-g158: GeomPoint x9 (B-spline internal-alignment scaffolding for g149; pole/knot coordinates omitted)
    g159: BSplineCurve PolesCount=11 KnotsCount=9 Degree=3 IsPeriodic=0
    g160-g167: Circle x8 (B-spline internal-alignment scaffolding for g168; pole/knot coordinates omitted)
    g168: BSplineCurve PolesCount=8 KnotsCount=6 Degree=3 IsPeriodic=0
    g169-g174: GeomPoint x6 (B-spline internal-alignment scaffolding for g168; pole/knot coordinates omitted)
    g175: BSplineCurve PolesCount=8 KnotsCount=6 Degree=3 IsPeriodic=0
    g176: LineSegment StartX=-63.944 StartY=21.0107 StartZ=0 EndX=-63.944 EndY=14.1107 EndZ=0
    g177: LineSegment StartX=-59.804 StartY=14.1107 StartZ=0 EndX=-59.804 EndY=21.5868 EndZ=0
    g178: BSplineCurve PolesCount=4 KnotsCount=2 Degree=3 IsPeriodic=0
    g179: GeomPoint X=-59.804 Y=21.5868 Z=0
    g180: GeomPoint X=-60.2379 Y=24.0907 Z=0
    g181: LineSegment StartX=-81.6055 StartY=14.1107 StartZ=0 EndX=-81.6055 EndY=21.5868 EndZ=0
    g182: LineSegment StartX=-151.619 StartY=24.0313 StartZ=0 EndX=-145.128 EndY=24.0313 EndZ=0
    g183: Circle CenterX=-82.0394 CenterY=24.0907 CenterZ=0 NormalX=0 NormalY=0 NormalZ=1 AngleXU=0 Radius=1
    g184: Circle CenterX=-81.7131 CenterY=23.2736 CenterZ=0 NormalX=0 NormalY=0 NormalZ=1 AngleXU=0 Radius=1
    g185: Circle CenterX=-81.6055 CenterY=21.5868 CenterZ=0 NormalX=0 NormalY=0 NormalZ=1 AngleXU=0 Radius=1
    g186: BSplineCurve PolesCount=3 KnotsCount=2 Degree=2 IsPeriodic=0
    g187: GeomPoint X=-82.0394 Y=24.0907 Z=0
    g188: GeomPoint X=-81.6055 Y=21.5868 Z=0
    g189: Ellipse CenterX=-37.3522 CenterY=19.9515 CenterZ=0 NormalX=0 NormalY=0 NormalZ=1 MajorRadius=2.99755 MinorRadius=2.49 AngleXU=1.5708
    g190: LineSegment StartX=-37.3522 StartY=22.949 StartZ=0 EndX=-37.3522 EndY=16.9539 EndZ=0
    g191: LineSegment StartX=-39.8422 StartY=19.9515 StartZ=0 EndX=-34.8622 EndY=19.9515 EndZ=0
    g192: GeomPoint X=-37.3522 Y=21.6203 Z=0
    g193: GeomPoint X=-37.3522 Y=18.2826 Z=0
  constraints (174):
    c: Coincident(g1,g0)
    c: Horizontal(g0)
    c: Vertical(g1)
    c: Coincident(g2,g3)
    c: Coincident(g3,g4)
    c: Horizontal(g4)
    c: Horizontal(g2)
    c: Vertical(g3)
    c: Block(g1)
    c: Distance(g3) = 4.86
    c: Block(g4)
    c: Distance(g0) = 10.8
    c: Distance(g2) = 10.8
    c: Coincident(g5,g0)
    c: Coincident(g6,g4)
    c: Coincident(g6,g2)
    c: Block(g8)
    c: Block(g7)
    c: Coincident(g9,g8)
    c: Coincident(g9,g7)
    c: Vertical(g9)
    c: Coincident(g10,g7)
    c: Coincident(g10,g8)
    c: Vertical(g10)
    c: Weight(g11) = 1
    c: Equal(g11, g12-g21) x10
    c: InternalAlignment(g11-g21 -> g22) x11
    c: InternalAlignment(g23-g31 -> g22) x9
    c: Block(g22)
    c: Weight(g32) = 1
    c: Equal(g32, g33-g49) x17
    c: InternalAlignment(g32-g49 -> g50) x18
    c: InternalAlignment(g51-g66 -> g50) x16
    c: Block(g50)
    c: Coincident(g67,g50)
    c: Coincident(g67,g22)
    c: Coincident(g68,g22)
    c: Coincident(g68,g50)
    c: InternalAlignment(g70,g69)
    c: InternalAlignment(g71,g69)
    c: Block(g69)
    c: InternalAlignment(g73,g72)
    c: InternalAlignment(g74,g72)
    c: Block(g72)
    c: InternalAlignment(g76,g75)
    c: InternalAlignment(g77,g75)
    c: InternalAlignment(g78,g80)
    c: InternalAlignment(g79,g80)
    c: Block(g80)
    c: Coincident(g75,g80)
    c: Block(g75)
    c: InternalAlignment(g82,g81)
    c: InternalAlignment(g83,g81)
    c: InternalAlignment(g84,g86)
    c: InternalAlignment(g85,g86)
    c: Block(g86)
    c: Coincident(g81,g86)
    c: Block(g81)
    c: Horizontal(g87)
    c: Block(g87)
    c: Horizontal(g88)
    c: Distance(g88) = 4.14
    c: Horizontal(g89)
    c: Equal(g88,g89) = 4.14
    c: Block(g89)
    c: Block(g88)
    c: Coincident(g90,g87)
    c: Vertical(g90)
    c: Distance(g90) = 11.88
    c: Coincident(g91,g90)
    c: Horizontal(g91)
    c: Coincident(g92,g91)
    c: Vertical(g92)
    c: Distance(g91) = 4.03
    c: Distance(g92) = 1.9
    c: Coincident(g93,g87)
    c: Vertical(g93)
    c: Vertical(g94)
    c: Coincident(g94,g88)
    c: Distance(g93) = 5.8
    c: Distance(g94) = 5.8
    c: Vertical(g95)
    c: Coincident(g95,g88)
    c: Distance(g95) = 6.9
    c: Coincident(g107,g92)
    c: Weight(g96) = 1
    c: Equal(g96, g97-g106) x10
    c: InternalAlignment(g96-g106 -> g107) x11
    c: InternalAlignment(g108-g116 -> g107) x9
    c: Block(g107)
    c: Block(g117)
    c: Coincident(g126,g93)
    c: Weight(g118) = 1
    c: Equal(g118, g119-g125) x7
    c: Coincident(g126,g95)
    c: InternalAlignment(g118-g125 -> g126) x8
    c: InternalAlignment(g127-g132 -> g126) x6
    c: Coincident(g133,g94)
    c: Block(g126)
    c: Block(g133)
    c: Coincident(g134,g133)
    c: Coincident(g134,g89)
    c: Vertical(g134)
    c: Horizontal(g135)
    c: Block(g135)
    c: Horizontal(g136)
    c: Equal(g88,g136) = 4.14
    c: Horizontal(g137)
    c: Equal(g136,g137) = 4.14
    c: Block(g137)
    c: Block(g136)
    c: Coincident(g138,g135)
    c: Vertical(g138)
    c: Equal(g90,g138) = 11.88
    c: Coincident(g139,g138)
    c: Horizontal(g139)
    c: Coincident(g140,g139)
    c: Vertical(g140)
    c: Equal(g91,g139) = 4.03
    c: Equal(g92,g140) = 1.9
    c: Coincident(g141,g135)
    c: Vertical(g141)
    c: Vertical(g142)
    c: Coincident(g142,g136)
    c: Equal(g93,g141) = 5.8
    c: Equal(g94,g142) = 5.8
    c: Vertical(g143)
    c: Coincident(g143,g136)
    c: Equal(g95,g143) = 6.9
    c: Coincident(g149,g140)
    c: Equal(g96,g144) = 1
    c: Equal(g144, g145-g148) x4
    c: InternalAlignment(g144-g148 -> g149) x5
    c: InternalAlignment(g150-g158 -> g149) x9
    c: Block(g149)
    c: Block(g159)
    c: Coincident(g168,g141)
    c: Equal(g118,g160) = 1
    c: Equal(g160, g161-g167) x7
    c: Coincident(g168,g143)
    c: InternalAlignment(g160-g167 -> g168) x8
    c: InternalAlignment(g169-g174 -> g168) x6
    c: Coincident(g175,g142)
    c: Block(g168)
    c: Block(g175)
    c: Coincident(g176,g175)
    c: Coincident(g176,g137)
    c: Vertical(g176)
    c: Coincident(g177,g137)
    c: Vertical(g177)
    c: Coincident(g178,g177)
    c: Coincident(g178,g159)
    c: InternalAlignment(g179,g178)
    c: InternalAlignment(g180,g178)
    c: Block(g178)
    c: Vertical(g181)
    c: Coincident(g181,g89)
    c: Block(g5)
    c: Coincident(g182,g1)
    c: Coincident(g182,g5)
    c: Horizontal(g182)
    c: Coincident(g186,g117)
    c: Weight(g183) = 1
    c: Equal(g183,g184)
    c: Equal(g183,g185)
    c: Coincident(g186,g181)
    c: InternalAlignment(g183,g186)
    c: InternalAlignment(g184,g186)
    c: InternalAlignment(g185,g186)
    c: InternalAlignment(g187,g186)
    c: InternalAlignment(g188,g186)
    c: Block(g186)
    c: InternalAlignment(g190-g193 -> g189) x4
    c: Block(g189)
FEATURE [PartDesign::Body] Body
  Group = -> [Sketch083]
  Origin = -> Origin
FEATURE [Sketcher::SketchObject] Sketch084
  FullyConstrained = true
  MapMode = 5
  Support = -> [XY_Plane001]
FEATURE [PartDesign::Body] Body001
  Group = -> [Sketch084]
  Origin = -> Origin001
